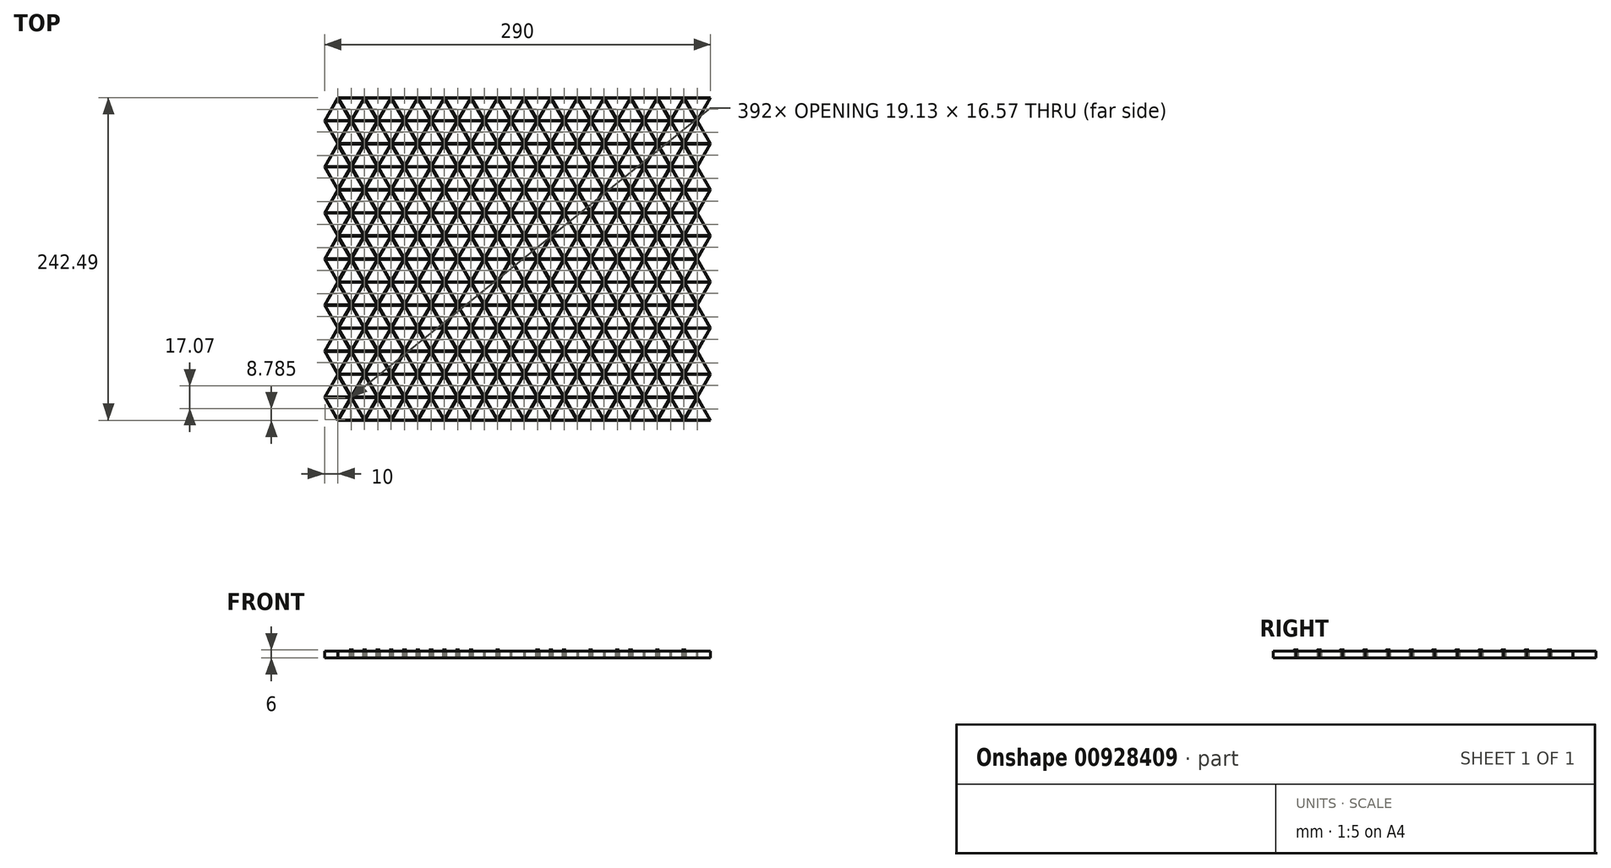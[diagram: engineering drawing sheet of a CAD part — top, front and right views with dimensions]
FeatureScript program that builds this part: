
annotation { "Feature Type Name" : "Feature", "Feature Type Description" : "" }
export const myFeature = defineFeature(function(context is Context, id is Id, definition is map)
    precondition{}
    {
        {
            var Q0;
            Q0=qCreatedBy(makeId("Top.planeOp"),FACE);
            var sketch = newSketch(context, id + "F0", { "sketchPlane" : qUnion([Q0])});
            skLineSegment(sketch, "E0", {"start": v(0, 0) * mm, "end": v(20, 0) * mm, "construction": true});
            skLineSegment(sketch, "E1", {"start": v(20, 0) * mm, "end": v(10, 17.32) * mm, "construction": true});
            skLineSegment(sketch, "E2", {"start": v(10, 17.32) * mm, "end": v(0, 0) * mm});
            skLineSegment(sketch, "E3.MirrorCS", {"start": v(10, -17.32) * mm, "end": v(0, 0) * mm});
            skLineSegment(sketch, "E4.MirrorCS", {"start": v(20, 0) * mm, "end": v(10, -17.32) * mm, "construction": true});
            skLineSegment(sketch, "E5.MirrorCS", {"start": v(30, -17.32) * mm, "end": v(20, 0) * mm, "construction": true});
            skLineSegment(sketch, "E6.MirrorCS", {"start": v(10, -17.32) * mm, "end": v(30, -17.32) * mm});
            skLineSegment(sketch, "E7.MirrorCS", {"start": v(30, 17.32) * mm, "end": v(20, 0) * mm, "construction": true});
            skLineSegment(sketch, "E8.MirrorCS", {"start": v(10, 17.32) * mm, "end": v(30, 17.32) * mm, "construction": true});
            skLineSegment(sketch, "E9.0.1.1", {"start": v(20, 34.64) * mm, "end": v(10, 17.32) * mm, "construction": true});
            skLineSegment(sketch, "E9.0.1.2", {"start": v(30, 17.32) * mm, "end": v(20, 34.64) * mm, "construction": true});
            skLineSegment(sketch, "E9.0.1.3", {"start": v(0, 34.64) * mm, "end": v(20, 34.64) * mm, "construction": true});
            skLineSegment(sketch, "E9.0.1.4", {"start": v(10, 17.32) * mm, "end": v(0, 34.64) * mm});
            skLineSegment(sketch, "E9.0.1.5", {"start": v(10, 51.96) * mm, "end": v(0, 34.64) * mm});
            skLineSegment(sketch, "E9.0.1.6", {"start": v(20, 34.64) * mm, "end": v(10, 51.96) * mm, "construction": true});
            skLineSegment(sketch, "E9.0.1.7", {"start": v(10, 51.96) * mm, "end": v(30, 51.96) * mm, "construction": true});
            skLineSegment(sketch, "E9.0.1.8", {"start": v(30, 51.96) * mm, "end": v(20, 34.64) * mm, "construction": true});
            skLineSegment(sketch, "E9.0.2.0", {"start": v(10, 51.96) * mm, "end": v(30, 51.96) * mm, "construction": true});
            skLineSegment(sketch, "E9.0.2.1", {"start": v(20, 69.28) * mm, "end": v(10, 51.96) * mm, "construction": true});
            skLineSegment(sketch, "E9.0.2.2", {"start": v(30, 51.96) * mm, "end": v(20, 69.28) * mm, "construction": true});
            skLineSegment(sketch, "E9.0.2.3", {"start": v(0, 69.28) * mm, "end": v(20, 69.28) * mm, "construction": true});
            skLineSegment(sketch, "E9.0.2.4", {"start": v(10, 51.96) * mm, "end": v(0, 69.28) * mm});
            skLineSegment(sketch, "E9.0.2.5", {"start": v(10, 86.6) * mm, "end": v(0, 69.28) * mm});
            skLineSegment(sketch, "E9.0.2.6", {"start": v(20, 69.28) * mm, "end": v(10, 86.6) * mm, "construction": true});
            skLineSegment(sketch, "E9.0.2.7", {"start": v(10, 86.6) * mm, "end": v(30, 86.6) * mm, "construction": true});
            skLineSegment(sketch, "E9.0.2.8", {"start": v(30, 86.6) * mm, "end": v(20, 69.28) * mm, "construction": true});
            skLineSegment(sketch, "E9.0.3.0", {"start": v(10, 86.6) * mm, "end": v(30, 86.6) * mm, "construction": true});
            skLineSegment(sketch, "E9.0.3.1", {"start": v(20, 103.92) * mm, "end": v(10, 86.6) * mm, "construction": true});
            skLineSegment(sketch, "E9.0.3.2", {"start": v(30, 86.6) * mm, "end": v(20, 103.92) * mm, "construction": true});
            skLineSegment(sketch, "E9.0.3.3", {"start": v(0, 103.92) * mm, "end": v(20, 103.92) * mm, "construction": true});
            skLineSegment(sketch, "E9.0.3.4", {"start": v(10, 86.6) * mm, "end": v(0, 103.92) * mm});
            skLineSegment(sketch, "E9.0.3.5", {"start": v(10, 121.24) * mm, "end": v(0, 103.92) * mm});
            skLineSegment(sketch, "E9.0.3.6", {"start": v(20, 103.92) * mm, "end": v(10, 121.24) * mm, "construction": true});
            skLineSegment(sketch, "E9.0.3.7", {"start": v(10, 121.24) * mm, "end": v(30, 121.24) * mm, "construction": true});
            skLineSegment(sketch, "E9.0.3.8", {"start": v(30, 121.24) * mm, "end": v(20, 103.92) * mm, "construction": true});
            skLineSegment(sketch, "E9.0.4.0", {"start": v(10, 121.24) * mm, "end": v(30, 121.24) * mm, "construction": true});
            skLineSegment(sketch, "E9.0.4.1", {"start": v(20, 138.56) * mm, "end": v(10, 121.24) * mm, "construction": true});
            skLineSegment(sketch, "E9.0.4.2", {"start": v(30, 121.24) * mm, "end": v(20, 138.56) * mm, "construction": true});
            skLineSegment(sketch, "E9.0.4.3", {"start": v(0, 138.56) * mm, "end": v(20, 138.56) * mm, "construction": true});
            skLineSegment(sketch, "E9.0.4.4", {"start": v(10, 121.24) * mm, "end": v(0, 138.56) * mm});
            skLineSegment(sketch, "E9.0.4.5", {"start": v(10, 155.88) * mm, "end": v(0, 138.56) * mm});
            skLineSegment(sketch, "E9.0.4.6", {"start": v(20, 138.56) * mm, "end": v(10, 155.88) * mm, "construction": true});
            skLineSegment(sketch, "E9.0.4.7", {"start": v(10, 155.88) * mm, "end": v(30, 155.88) * mm, "construction": true});
            skLineSegment(sketch, "E9.0.4.8", {"start": v(30, 155.88) * mm, "end": v(20, 138.56) * mm, "construction": true});
            skLineSegment(sketch, "E9.0.5.0", {"start": v(10, 155.88) * mm, "end": v(30, 155.88) * mm, "construction": true});
            skLineSegment(sketch, "E9.0.5.1", {"start": v(20, 173.2) * mm, "end": v(10, 155.88) * mm, "construction": true});
            skLineSegment(sketch, "E9.0.5.2", {"start": v(30, 155.88) * mm, "end": v(20, 173.2) * mm, "construction": true});
            skLineSegment(sketch, "E9.0.5.3", {"start": v(0, 173.2) * mm, "end": v(20, 173.2) * mm, "construction": true});
            skLineSegment(sketch, "E9.0.5.4", {"start": v(10, 155.88) * mm, "end": v(0, 173.2) * mm});
            skLineSegment(sketch, "E9.0.5.5", {"start": v(10, 190.53) * mm, "end": v(0, 173.2) * mm});
            skLineSegment(sketch, "E9.0.5.6", {"start": v(20, 173.2) * mm, "end": v(10, 190.53) * mm, "construction": true});
            skLineSegment(sketch, "E9.0.5.7", {"start": v(10, 190.53) * mm, "end": v(30, 190.53) * mm, "construction": true});
            skLineSegment(sketch, "E9.0.5.8", {"start": v(30, 190.53) * mm, "end": v(20, 173.2) * mm, "construction": true});
            skLineSegment(sketch, "E9.0.6.0", {"start": v(10, 190.53) * mm, "end": v(30, 190.53) * mm, "construction": true});
            skLineSegment(sketch, "E9.0.6.1", {"start": v(20, 207.85) * mm, "end": v(10, 190.53) * mm, "construction": true});
            skLineSegment(sketch, "E9.0.6.2", {"start": v(30, 190.53) * mm, "end": v(20, 207.85) * mm, "construction": true});
            skLineSegment(sketch, "E9.0.6.3", {"start": v(0, 207.85) * mm, "end": v(20, 207.85) * mm, "construction": true});
            skLineSegment(sketch, "E9.0.6.4", {"start": v(10, 190.53) * mm, "end": v(0, 207.85) * mm});
            skLineSegment(sketch, "E9.0.6.5", {"start": v(10, 225.17) * mm, "end": v(0, 207.85) * mm});
            skLineSegment(sketch, "E9.0.6.6", {"start": v(20, 207.85) * mm, "end": v(10, 225.17) * mm, "construction": true});
            skLineSegment(sketch, "E9.0.6.7", {"start": v(10, 225.17) * mm, "end": v(30, 225.17) * mm});
            skLineSegment(sketch, "E9.0.6.8", {"start": v(30, 225.17) * mm, "end": v(20, 207.85) * mm, "construction": true});
            skLineSegment(sketch, "E9.1.0.0", {"start": v(30, -17.32) * mm, "end": v(50, -17.32) * mm});
            skLineSegment(sketch, "E9.1.0.1", {"start": v(40, 0) * mm, "end": v(30, -17.32) * mm, "construction": true});
            skLineSegment(sketch, "E9.1.0.2", {"start": v(50, -17.32) * mm, "end": v(40, 0) * mm, "construction": true});
            skLineSegment(sketch, "E9.1.0.3", {"start": v(20, 0) * mm, "end": v(40, 0) * mm, "construction": true});
            skLineSegment(sketch, "E9.1.0.6", {"start": v(40, 0) * mm, "end": v(30, 17.32) * mm, "construction": true});
            skLineSegment(sketch, "E9.1.0.7", {"start": v(30, 17.32) * mm, "end": v(50, 17.32) * mm, "construction": true});
            skLineSegment(sketch, "E9.1.0.8", {"start": v(50, 17.32) * mm, "end": v(40, 0) * mm, "construction": true});
            skLineSegment(sketch, "E9.1.1.0", {"start": v(30, 17.32) * mm, "end": v(50, 17.32) * mm, "construction": true});
            skLineSegment(sketch, "E9.1.1.1", {"start": v(40, 34.64) * mm, "end": v(30, 17.32) * mm, "construction": true});
            skLineSegment(sketch, "E9.1.1.2", {"start": v(50, 17.32) * mm, "end": v(40, 34.64) * mm, "construction": true});
            skLineSegment(sketch, "E9.1.1.3", {"start": v(20, 34.64) * mm, "end": v(40, 34.64) * mm, "construction": true});
            skLineSegment(sketch, "E9.1.1.4", {"start": v(30, 17.32) * mm, "end": v(20, 34.64) * mm, "construction": true});
            skLineSegment(sketch, "E9.1.1.5", {"start": v(30, 51.96) * mm, "end": v(20, 34.64) * mm, "construction": true});
            skLineSegment(sketch, "E9.1.1.6", {"start": v(40, 34.64) * mm, "end": v(30, 51.96) * mm, "construction": true});
            skLineSegment(sketch, "E9.1.1.7", {"start": v(30, 51.96) * mm, "end": v(50, 51.96) * mm, "construction": true});
            skLineSegment(sketch, "E9.1.1.8", {"start": v(50, 51.96) * mm, "end": v(40, 34.64) * mm, "construction": true});
            skLineSegment(sketch, "E9.1.2.0", {"start": v(30, 51.96) * mm, "end": v(50, 51.96) * mm, "construction": true});
            skLineSegment(sketch, "E9.1.2.1", {"start": v(40, 69.28) * mm, "end": v(30, 51.96) * mm, "construction": true});
            skLineSegment(sketch, "E9.1.2.2", {"start": v(50, 51.96) * mm, "end": v(40, 69.28) * mm, "construction": true});
            skLineSegment(sketch, "E9.1.2.3", {"start": v(20, 69.28) * mm, "end": v(40, 69.28) * mm, "construction": true});
            skLineSegment(sketch, "E9.1.2.4", {"start": v(30, 51.96) * mm, "end": v(20, 69.28) * mm, "construction": true});
            skLineSegment(sketch, "E9.1.2.5", {"start": v(30, 86.6) * mm, "end": v(20, 69.28) * mm, "construction": true});
            skLineSegment(sketch, "E9.1.2.6", {"start": v(40, 69.28) * mm, "end": v(30, 86.6) * mm, "construction": true});
            skLineSegment(sketch, "E9.1.2.7", {"start": v(30, 86.6) * mm, "end": v(50, 86.6) * mm, "construction": true});
            skLineSegment(sketch, "E9.1.2.8", {"start": v(50, 86.6) * mm, "end": v(40, 69.28) * mm, "construction": true});
            skLineSegment(sketch, "E9.1.3.0", {"start": v(30, 86.6) * mm, "end": v(50, 86.6) * mm, "construction": true});
            skLineSegment(sketch, "E9.1.3.1", {"start": v(40, 103.92) * mm, "end": v(30, 86.6) * mm, "construction": true});
            skLineSegment(sketch, "E9.1.3.2", {"start": v(50, 86.6) * mm, "end": v(40, 103.92) * mm, "construction": true});
            skLineSegment(sketch, "E9.1.3.3", {"start": v(20, 103.92) * mm, "end": v(40, 103.92) * mm, "construction": true});
            skLineSegment(sketch, "E9.1.3.4", {"start": v(30, 86.6) * mm, "end": v(20, 103.92) * mm, "construction": true});
            skLineSegment(sketch, "E9.1.3.5", {"start": v(30, 121.24) * mm, "end": v(20, 103.92) * mm, "construction": true});
            skLineSegment(sketch, "E9.1.3.6", {"start": v(40, 103.92) * mm, "end": v(30, 121.24) * mm, "construction": true});
            skLineSegment(sketch, "E9.1.3.7", {"start": v(30, 121.24) * mm, "end": v(50, 121.24) * mm, "construction": true});
            skLineSegment(sketch, "E9.1.3.8", {"start": v(50, 121.24) * mm, "end": v(40, 103.92) * mm, "construction": true});
            skLineSegment(sketch, "E9.1.4.0", {"start": v(30, 121.24) * mm, "end": v(50, 121.24) * mm, "construction": true});
            skLineSegment(sketch, "E9.1.4.1", {"start": v(40, 138.56) * mm, "end": v(30, 121.24) * mm, "construction": true});
            skLineSegment(sketch, "E9.1.4.2", {"start": v(50, 121.24) * mm, "end": v(40, 138.56) * mm, "construction": true});
            skLineSegment(sketch, "E9.1.4.3", {"start": v(20, 138.56) * mm, "end": v(40, 138.56) * mm, "construction": true});
            skLineSegment(sketch, "E9.1.4.4", {"start": v(30, 121.24) * mm, "end": v(20, 138.56) * mm, "construction": true});
            skLineSegment(sketch, "E9.1.4.5", {"start": v(30, 155.88) * mm, "end": v(20, 138.56) * mm, "construction": true});
            skLineSegment(sketch, "E9.1.4.6", {"start": v(40, 138.56) * mm, "end": v(30, 155.88) * mm, "construction": true});
            skLineSegment(sketch, "E9.1.4.7", {"start": v(30, 155.88) * mm, "end": v(50, 155.88) * mm, "construction": true});
            skLineSegment(sketch, "E9.1.4.8", {"start": v(50, 155.88) * mm, "end": v(40, 138.56) * mm, "construction": true});
            skLineSegment(sketch, "E9.1.5.0", {"start": v(30, 155.88) * mm, "end": v(50, 155.88) * mm, "construction": true});
            skLineSegment(sketch, "E9.1.5.1", {"start": v(40, 173.2) * mm, "end": v(30, 155.88) * mm, "construction": true});
            skLineSegment(sketch, "E9.1.5.2", {"start": v(50, 155.88) * mm, "end": v(40, 173.2) * mm, "construction": true});
            skLineSegment(sketch, "E9.1.5.3", {"start": v(20, 173.2) * mm, "end": v(40, 173.2) * mm, "construction": true});
            skLineSegment(sketch, "E9.1.5.4", {"start": v(30, 155.88) * mm, "end": v(20, 173.2) * mm, "construction": true});
            skLineSegment(sketch, "E9.1.5.5", {"start": v(30, 190.53) * mm, "end": v(20, 173.2) * mm, "construction": true});
            skLineSegment(sketch, "E9.1.5.6", {"start": v(40, 173.2) * mm, "end": v(30, 190.53) * mm, "construction": true});
            skLineSegment(sketch, "E9.1.5.7", {"start": v(30, 190.53) * mm, "end": v(50, 190.53) * mm, "construction": true});
            skLineSegment(sketch, "E9.1.5.8", {"start": v(50, 190.53) * mm, "end": v(40, 173.2) * mm, "construction": true});
            skLineSegment(sketch, "E9.1.6.0", {"start": v(30, 190.53) * mm, "end": v(50, 190.53) * mm, "construction": true});
            skLineSegment(sketch, "E9.1.6.1", {"start": v(40, 207.85) * mm, "end": v(30, 190.53) * mm, "construction": true});
            skLineSegment(sketch, "E9.1.6.2", {"start": v(50, 190.53) * mm, "end": v(40, 207.85) * mm, "construction": true});
            skLineSegment(sketch, "E9.1.6.3", {"start": v(20, 207.85) * mm, "end": v(40, 207.85) * mm, "construction": true});
            skLineSegment(sketch, "E9.1.6.4", {"start": v(30, 190.53) * mm, "end": v(20, 207.85) * mm, "construction": true});
            skLineSegment(sketch, "E9.1.6.5", {"start": v(30, 225.17) * mm, "end": v(20, 207.85) * mm, "construction": true});
            skLineSegment(sketch, "E9.1.6.6", {"start": v(40, 207.85) * mm, "end": v(30, 225.17) * mm, "construction": true});
            skLineSegment(sketch, "E9.1.6.7", {"start": v(30, 225.17) * mm, "end": v(50, 225.17) * mm});
            skLineSegment(sketch, "E9.1.6.8", {"start": v(50, 225.17) * mm, "end": v(40, 207.85) * mm, "construction": true});
            skLineSegment(sketch, "E9.2.0.0", {"start": v(50, -17.32) * mm, "end": v(70, -17.32) * mm});
            skLineSegment(sketch, "E9.2.0.1", {"start": v(60, 0) * mm, "end": v(50, -17.32) * mm, "construction": true});
            skLineSegment(sketch, "E9.2.0.2", {"start": v(70, -17.32) * mm, "end": v(60, 0) * mm, "construction": true});
            skLineSegment(sketch, "E9.2.0.3", {"start": v(40, 0) * mm, "end": v(60, 0) * mm, "construction": true});
            skLineSegment(sketch, "E9.2.0.4", {"start": v(50, -17.32) * mm, "end": v(40, 0) * mm, "construction": true});
            skLineSegment(sketch, "E9.2.0.5", {"start": v(50, 17.32) * mm, "end": v(40, 0) * mm, "construction": true});
            skLineSegment(sketch, "E9.2.0.6", {"start": v(60, 0) * mm, "end": v(50, 17.32) * mm, "construction": true});
            skLineSegment(sketch, "E9.2.0.7", {"start": v(50, 17.32) * mm, "end": v(70, 17.32) * mm, "construction": true});
            skLineSegment(sketch, "E9.2.0.8", {"start": v(70, 17.32) * mm, "end": v(60, 0) * mm, "construction": true});
            skLineSegment(sketch, "E9.2.1.0", {"start": v(50, 17.32) * mm, "end": v(70, 17.32) * mm, "construction": true});
            skLineSegment(sketch, "E9.2.1.1", {"start": v(60, 34.64) * mm, "end": v(50, 17.32) * mm, "construction": true});
            skLineSegment(sketch, "E9.2.1.2", {"start": v(70, 17.32) * mm, "end": v(60, 34.64) * mm, "construction": true});
            skLineSegment(sketch, "E9.2.1.3", {"start": v(40, 34.64) * mm, "end": v(60, 34.64) * mm, "construction": true});
            skLineSegment(sketch, "E9.2.1.4", {"start": v(50, 17.32) * mm, "end": v(40, 34.64) * mm, "construction": true});
            skLineSegment(sketch, "E9.2.1.5", {"start": v(50, 51.96) * mm, "end": v(40, 34.64) * mm, "construction": true});
            skLineSegment(sketch, "E9.2.1.6", {"start": v(60, 34.64) * mm, "end": v(50, 51.96) * mm, "construction": true});
            skLineSegment(sketch, "E9.2.1.7", {"start": v(50, 51.96) * mm, "end": v(70, 51.96) * mm, "construction": true});
            skLineSegment(sketch, "E9.2.1.8", {"start": v(70, 51.96) * mm, "end": v(60, 34.64) * mm, "construction": true});
            skLineSegment(sketch, "E9.2.2.0", {"start": v(50, 51.96) * mm, "end": v(70, 51.96) * mm, "construction": true});
            skLineSegment(sketch, "E9.2.2.1", {"start": v(60, 69.28) * mm, "end": v(50, 51.96) * mm, "construction": true});
            skLineSegment(sketch, "E9.2.2.2", {"start": v(70, 51.96) * mm, "end": v(60, 69.28) * mm, "construction": true});
            skLineSegment(sketch, "E9.2.2.3", {"start": v(40, 69.28) * mm, "end": v(60, 69.28) * mm, "construction": true});
            skLineSegment(sketch, "E9.2.2.4", {"start": v(50, 51.96) * mm, "end": v(40, 69.28) * mm, "construction": true});
            skLineSegment(sketch, "E9.2.2.5", {"start": v(50, 86.6) * mm, "end": v(40, 69.28) * mm, "construction": true});
            skLineSegment(sketch, "E9.2.2.6", {"start": v(60, 69.28) * mm, "end": v(50, 86.6) * mm, "construction": true});
            skLineSegment(sketch, "E9.2.2.7", {"start": v(50, 86.6) * mm, "end": v(70, 86.6) * mm, "construction": true});
            skLineSegment(sketch, "E9.2.2.8", {"start": v(70, 86.6) * mm, "end": v(60, 69.28) * mm, "construction": true});
            skLineSegment(sketch, "E9.2.3.0", {"start": v(50, 86.6) * mm, "end": v(70, 86.6) * mm, "construction": true});
            skLineSegment(sketch, "E9.2.3.1", {"start": v(60, 103.92) * mm, "end": v(50, 86.6) * mm, "construction": true});
            skLineSegment(sketch, "E9.2.3.2", {"start": v(70, 86.6) * mm, "end": v(60, 103.92) * mm, "construction": true});
            skLineSegment(sketch, "E9.2.3.3", {"start": v(40, 103.92) * mm, "end": v(60, 103.92) * mm, "construction": true});
            skLineSegment(sketch, "E9.2.3.4", {"start": v(50, 86.6) * mm, "end": v(40, 103.92) * mm, "construction": true});
            skLineSegment(sketch, "E9.2.3.5", {"start": v(50, 121.24) * mm, "end": v(40, 103.92) * mm, "construction": true});
            skLineSegment(sketch, "E9.2.3.6", {"start": v(60, 103.92) * mm, "end": v(50, 121.24) * mm, "construction": true});
            skLineSegment(sketch, "E9.2.3.7", {"start": v(50, 121.24) * mm, "end": v(70, 121.24) * mm, "construction": true});
            skLineSegment(sketch, "E9.2.3.8", {"start": v(70, 121.24) * mm, "end": v(60, 103.92) * mm, "construction": true});
            skLineSegment(sketch, "E9.2.4.0", {"start": v(50, 121.24) * mm, "end": v(70, 121.24) * mm, "construction": true});
            skLineSegment(sketch, "E9.2.4.1", {"start": v(60, 138.56) * mm, "end": v(50, 121.24) * mm, "construction": true});
            skLineSegment(sketch, "E9.2.4.2", {"start": v(70, 121.24) * mm, "end": v(60, 138.56) * mm, "construction": true});
            skLineSegment(sketch, "E9.2.4.3", {"start": v(40, 138.56) * mm, "end": v(60, 138.56) * mm, "construction": true});
            skLineSegment(sketch, "E9.2.4.4", {"start": v(50, 121.24) * mm, "end": v(40, 138.56) * mm, "construction": true});
            skLineSegment(sketch, "E9.2.4.5", {"start": v(50, 155.88) * mm, "end": v(40, 138.56) * mm, "construction": true});
            skLineSegment(sketch, "E9.2.4.6", {"start": v(60, 138.56) * mm, "end": v(50, 155.88) * mm, "construction": true});
            skLineSegment(sketch, "E9.2.4.7", {"start": v(50, 155.88) * mm, "end": v(70, 155.88) * mm, "construction": true});
            skLineSegment(sketch, "E9.2.4.8", {"start": v(70, 155.88) * mm, "end": v(60, 138.56) * mm, "construction": true});
            skLineSegment(sketch, "E9.2.5.0", {"start": v(50, 155.88) * mm, "end": v(70, 155.88) * mm, "construction": true});
            skLineSegment(sketch, "E9.2.5.1", {"start": v(60, 173.2) * mm, "end": v(50, 155.88) * mm, "construction": true});
            skLineSegment(sketch, "E9.2.5.2", {"start": v(70, 155.88) * mm, "end": v(60, 173.2) * mm, "construction": true});
            skLineSegment(sketch, "E9.2.5.3", {"start": v(40, 173.2) * mm, "end": v(60, 173.2) * mm, "construction": true});
            skLineSegment(sketch, "E9.2.5.4", {"start": v(50, 155.88) * mm, "end": v(40, 173.2) * mm, "construction": true});
            skLineSegment(sketch, "E9.2.5.5", {"start": v(50, 190.53) * mm, "end": v(40, 173.2) * mm, "construction": true});
            skLineSegment(sketch, "E9.2.5.6", {"start": v(60, 173.2) * mm, "end": v(50, 190.53) * mm, "construction": true});
            skLineSegment(sketch, "E9.2.5.7", {"start": v(50, 190.53) * mm, "end": v(70, 190.53) * mm, "construction": true});
            skLineSegment(sketch, "E9.2.5.8", {"start": v(70, 190.53) * mm, "end": v(60, 173.2) * mm, "construction": true});
            skLineSegment(sketch, "E9.2.6.0", {"start": v(50, 190.53) * mm, "end": v(70, 190.53) * mm, "construction": true});
            skLineSegment(sketch, "E9.2.6.1", {"start": v(60, 207.85) * mm, "end": v(50, 190.53) * mm, "construction": true});
            skLineSegment(sketch, "E9.2.6.2", {"start": v(70, 190.53) * mm, "end": v(60, 207.85) * mm, "construction": true});
            skLineSegment(sketch, "E9.2.6.3", {"start": v(40, 207.85) * mm, "end": v(60, 207.85) * mm, "construction": true});
            skLineSegment(sketch, "E9.2.6.4", {"start": v(50, 190.53) * mm, "end": v(40, 207.85) * mm, "construction": true});
            skLineSegment(sketch, "E9.2.6.5", {"start": v(50, 225.17) * mm, "end": v(40, 207.85) * mm, "construction": true});
            skLineSegment(sketch, "E9.2.6.6", {"start": v(60, 207.85) * mm, "end": v(50, 225.17) * mm, "construction": true});
            skLineSegment(sketch, "E9.2.6.7", {"start": v(50, 225.17) * mm, "end": v(70, 225.17) * mm});
            skLineSegment(sketch, "E9.2.6.8", {"start": v(70, 225.17) * mm, "end": v(60, 207.85) * mm, "construction": true});
            skLineSegment(sketch, "E9.3.0.0", {"start": v(70, -17.32) * mm, "end": v(90, -17.32) * mm});
            skLineSegment(sketch, "E9.3.0.1", {"start": v(80, 0) * mm, "end": v(70, -17.32) * mm, "construction": true});
            skLineSegment(sketch, "E9.3.0.2", {"start": v(90, -17.32) * mm, "end": v(80, 0) * mm, "construction": true});
            skLineSegment(sketch, "E9.3.0.3", {"start": v(60, 0) * mm, "end": v(80, 0) * mm, "construction": true});
            skLineSegment(sketch, "E9.3.0.4", {"start": v(70, -17.32) * mm, "end": v(60, 0) * mm, "construction": true});
            skLineSegment(sketch, "E9.3.0.5", {"start": v(70, 17.32) * mm, "end": v(60, 0) * mm, "construction": true});
            skLineSegment(sketch, "E9.3.0.6", {"start": v(80, 0) * mm, "end": v(70, 17.32) * mm, "construction": true});
            skLineSegment(sketch, "E9.3.0.7", {"start": v(70, 17.32) * mm, "end": v(90, 17.32) * mm, "construction": true});
            skLineSegment(sketch, "E9.3.0.8", {"start": v(90, 17.32) * mm, "end": v(80, 0) * mm, "construction": true});
            skLineSegment(sketch, "E9.3.1.0", {"start": v(70, 17.32) * mm, "end": v(90, 17.32) * mm, "construction": true});
            skLineSegment(sketch, "E9.3.1.1", {"start": v(80, 34.64) * mm, "end": v(70, 17.32) * mm, "construction": true});
            skLineSegment(sketch, "E9.3.1.2", {"start": v(90, 17.32) * mm, "end": v(80, 34.64) * mm, "construction": true});
            skLineSegment(sketch, "E9.3.1.3", {"start": v(60, 34.64) * mm, "end": v(80, 34.64) * mm, "construction": true});
            skLineSegment(sketch, "E9.3.1.4", {"start": v(70, 17.32) * mm, "end": v(60, 34.64) * mm, "construction": true});
            skLineSegment(sketch, "E9.3.1.5", {"start": v(70, 51.96) * mm, "end": v(60, 34.64) * mm, "construction": true});
            skLineSegment(sketch, "E9.3.1.6", {"start": v(80, 34.64) * mm, "end": v(70, 51.96) * mm, "construction": true});
            skLineSegment(sketch, "E9.3.1.7", {"start": v(70, 51.96) * mm, "end": v(90, 51.96) * mm, "construction": true});
            skLineSegment(sketch, "E9.3.1.8", {"start": v(90, 51.96) * mm, "end": v(80, 34.64) * mm, "construction": true});
            skLineSegment(sketch, "E9.3.2.0", {"start": v(70, 51.96) * mm, "end": v(90, 51.96) * mm, "construction": true});
            skLineSegment(sketch, "E9.3.2.1", {"start": v(80, 69.28) * mm, "end": v(70, 51.96) * mm, "construction": true});
            skLineSegment(sketch, "E9.3.2.2", {"start": v(90, 51.96) * mm, "end": v(80, 69.28) * mm, "construction": true});
            skLineSegment(sketch, "E9.3.2.3", {"start": v(60, 69.28) * mm, "end": v(80, 69.28) * mm, "construction": true});
            skLineSegment(sketch, "E9.3.2.4", {"start": v(70, 51.96) * mm, "end": v(60, 69.28) * mm, "construction": true});
            skLineSegment(sketch, "E9.3.2.5", {"start": v(70, 86.6) * mm, "end": v(60, 69.28) * mm, "construction": true});
            skLineSegment(sketch, "E9.3.2.6", {"start": v(80, 69.28) * mm, "end": v(70, 86.6) * mm, "construction": true});
            skLineSegment(sketch, "E9.3.2.7", {"start": v(70, 86.6) * mm, "end": v(90, 86.6) * mm, "construction": true});
            skLineSegment(sketch, "E9.3.2.8", {"start": v(90, 86.6) * mm, "end": v(80, 69.28) * mm, "construction": true});
            skLineSegment(sketch, "E9.3.3.0", {"start": v(70, 86.6) * mm, "end": v(90, 86.6) * mm, "construction": true});
            skLineSegment(sketch, "E9.3.3.1", {"start": v(80, 103.92) * mm, "end": v(70, 86.6) * mm, "construction": true});
            skLineSegment(sketch, "E9.3.3.2", {"start": v(90, 86.6) * mm, "end": v(80, 103.92) * mm, "construction": true});
            skLineSegment(sketch, "E9.3.3.3", {"start": v(60, 103.92) * mm, "end": v(80, 103.92) * mm, "construction": true});
            skLineSegment(sketch, "E9.3.3.4", {"start": v(70, 86.6) * mm, "end": v(60, 103.92) * mm, "construction": true});
            skLineSegment(sketch, "E9.3.3.5", {"start": v(70, 121.24) * mm, "end": v(60, 103.92) * mm, "construction": true});
            skLineSegment(sketch, "E9.3.3.6", {"start": v(80, 103.92) * mm, "end": v(70, 121.24) * mm, "construction": true});
            skLineSegment(sketch, "E9.3.3.7", {"start": v(70, 121.24) * mm, "end": v(90, 121.24) * mm, "construction": true});
            skLineSegment(sketch, "E9.3.3.8", {"start": v(90, 121.24) * mm, "end": v(80, 103.92) * mm, "construction": true});
            skLineSegment(sketch, "E9.3.4.0", {"start": v(70, 121.24) * mm, "end": v(90, 121.24) * mm, "construction": true});
            skLineSegment(sketch, "E9.3.4.1", {"start": v(80, 138.56) * mm, "end": v(70, 121.24) * mm, "construction": true});
            skLineSegment(sketch, "E9.3.4.2", {"start": v(90, 121.24) * mm, "end": v(80, 138.56) * mm, "construction": true});
            skLineSegment(sketch, "E9.3.4.3", {"start": v(60, 138.56) * mm, "end": v(80, 138.56) * mm, "construction": true});
            skLineSegment(sketch, "E9.3.4.4", {"start": v(70, 121.24) * mm, "end": v(60, 138.56) * mm, "construction": true});
            skLineSegment(sketch, "E9.3.4.5", {"start": v(70, 155.88) * mm, "end": v(60, 138.56) * mm, "construction": true});
            skLineSegment(sketch, "E9.3.4.6", {"start": v(80, 138.56) * mm, "end": v(70, 155.88) * mm, "construction": true});
            skLineSegment(sketch, "E9.3.4.7", {"start": v(70, 155.88) * mm, "end": v(90, 155.88) * mm, "construction": true});
            skLineSegment(sketch, "E9.3.4.8", {"start": v(90, 155.88) * mm, "end": v(80, 138.56) * mm, "construction": true});
            skLineSegment(sketch, "E9.3.5.0", {"start": v(70, 155.88) * mm, "end": v(90, 155.88) * mm, "construction": true});
            skLineSegment(sketch, "E9.3.5.1", {"start": v(80, 173.2) * mm, "end": v(70, 155.88) * mm, "construction": true});
            skLineSegment(sketch, "E9.3.5.2", {"start": v(90, 155.88) * mm, "end": v(80, 173.2) * mm, "construction": true});
            skLineSegment(sketch, "E9.3.5.3", {"start": v(60, 173.2) * mm, "end": v(80, 173.2) * mm, "construction": true});
            skLineSegment(sketch, "E9.3.5.4", {"start": v(70, 155.88) * mm, "end": v(60, 173.2) * mm, "construction": true});
            skLineSegment(sketch, "E9.3.5.5", {"start": v(70, 190.53) * mm, "end": v(60, 173.2) * mm, "construction": true});
            skLineSegment(sketch, "E9.3.5.6", {"start": v(80, 173.2) * mm, "end": v(70, 190.53) * mm, "construction": true});
            skLineSegment(sketch, "E9.3.5.7", {"start": v(70, 190.53) * mm, "end": v(90, 190.53) * mm, "construction": true});
            skLineSegment(sketch, "E9.3.5.8", {"start": v(90, 190.53) * mm, "end": v(80, 173.2) * mm, "construction": true});
            skLineSegment(sketch, "E9.3.6.0", {"start": v(70, 190.53) * mm, "end": v(90, 190.53) * mm, "construction": true});
            skLineSegment(sketch, "E9.3.6.1", {"start": v(80, 207.85) * mm, "end": v(70, 190.53) * mm, "construction": true});
            skLineSegment(sketch, "E9.3.6.2", {"start": v(90, 190.53) * mm, "end": v(80, 207.85) * mm, "construction": true});
            skLineSegment(sketch, "E9.3.6.3", {"start": v(60, 207.85) * mm, "end": v(80, 207.85) * mm, "construction": true});
            skLineSegment(sketch, "E9.3.6.4", {"start": v(70, 190.53) * mm, "end": v(60, 207.85) * mm, "construction": true});
            skLineSegment(sketch, "E9.3.6.5", {"start": v(70, 225.17) * mm, "end": v(60, 207.85) * mm, "construction": true});
            skLineSegment(sketch, "E9.3.6.6", {"start": v(80, 207.85) * mm, "end": v(70, 225.17) * mm, "construction": true});
            skLineSegment(sketch, "E9.3.6.7", {"start": v(70, 225.17) * mm, "end": v(90, 225.17) * mm});
            skLineSegment(sketch, "E9.3.6.8", {"start": v(90, 225.17) * mm, "end": v(80, 207.85) * mm, "construction": true});
            skLineSegment(sketch, "E9.4.0.0", {"start": v(90, -17.32) * mm, "end": v(110, -17.32) * mm});
            skLineSegment(sketch, "E9.4.0.1", {"start": v(100, 0) * mm, "end": v(90, -17.32) * mm, "construction": true});
            skLineSegment(sketch, "E9.4.0.2", {"start": v(110, -17.32) * mm, "end": v(100, 0) * mm, "construction": true});
            skLineSegment(sketch, "E9.4.0.3", {"start": v(80, 0) * mm, "end": v(100, 0) * mm, "construction": true});
            skLineSegment(sketch, "E9.4.0.4", {"start": v(90, -17.32) * mm, "end": v(80, 0) * mm, "construction": true});
            skLineSegment(sketch, "E9.4.0.5", {"start": v(90, 17.32) * mm, "end": v(80, 0) * mm, "construction": true});
            skLineSegment(sketch, "E9.4.0.6", {"start": v(100, 0) * mm, "end": v(90, 17.32) * mm, "construction": true});
            skLineSegment(sketch, "E9.4.0.7", {"start": v(90, 17.32) * mm, "end": v(110, 17.32) * mm, "construction": true});
            skLineSegment(sketch, "E9.4.0.8", {"start": v(110, 17.32) * mm, "end": v(100, 0) * mm, "construction": true});
            skLineSegment(sketch, "E9.4.1.0", {"start": v(90, 17.32) * mm, "end": v(110, 17.32) * mm, "construction": true});
            skLineSegment(sketch, "E9.4.1.1", {"start": v(100, 34.64) * mm, "end": v(90, 17.32) * mm, "construction": true});
            skLineSegment(sketch, "E9.4.1.2", {"start": v(110, 17.32) * mm, "end": v(100, 34.64) * mm, "construction": true});
            skLineSegment(sketch, "E9.4.1.3", {"start": v(80, 34.64) * mm, "end": v(100, 34.64) * mm, "construction": true});
            skLineSegment(sketch, "E9.4.1.4", {"start": v(90, 17.32) * mm, "end": v(80, 34.64) * mm, "construction": true});
            skLineSegment(sketch, "E9.4.1.5", {"start": v(90, 51.96) * mm, "end": v(80, 34.64) * mm, "construction": true});
            skLineSegment(sketch, "E9.4.1.6", {"start": v(100, 34.64) * mm, "end": v(90, 51.96) * mm, "construction": true});
            skLineSegment(sketch, "E9.4.1.7", {"start": v(90, 51.96) * mm, "end": v(110, 51.96) * mm, "construction": true});
            skLineSegment(sketch, "E9.4.1.8", {"start": v(110, 51.96) * mm, "end": v(100, 34.64) * mm, "construction": true});
            skLineSegment(sketch, "E9.4.2.0", {"start": v(90, 51.96) * mm, "end": v(110, 51.96) * mm, "construction": true});
            skLineSegment(sketch, "E9.4.2.1", {"start": v(100, 69.28) * mm, "end": v(90, 51.96) * mm, "construction": true});
            skLineSegment(sketch, "E9.4.2.2", {"start": v(110, 51.96) * mm, "end": v(100, 69.28) * mm, "construction": true});
            skLineSegment(sketch, "E9.4.2.3", {"start": v(80, 69.28) * mm, "end": v(100, 69.28) * mm, "construction": true});
            skLineSegment(sketch, "E9.4.2.4", {"start": v(90, 51.96) * mm, "end": v(80, 69.28) * mm, "construction": true});
            skLineSegment(sketch, "E9.4.2.5", {"start": v(90, 86.6) * mm, "end": v(80, 69.28) * mm, "construction": true});
            skLineSegment(sketch, "E9.4.2.6", {"start": v(100, 69.28) * mm, "end": v(90, 86.6) * mm, "construction": true});
            skLineSegment(sketch, "E9.4.2.7", {"start": v(90, 86.6) * mm, "end": v(110, 86.6) * mm, "construction": true});
            skLineSegment(sketch, "E9.4.2.8", {"start": v(110, 86.6) * mm, "end": v(100, 69.28) * mm, "construction": true});
            skLineSegment(sketch, "E9.4.3.0", {"start": v(90, 86.6) * mm, "end": v(110, 86.6) * mm, "construction": true});
            skLineSegment(sketch, "E9.4.3.1", {"start": v(100, 103.92) * mm, "end": v(90, 86.6) * mm, "construction": true});
            skLineSegment(sketch, "E9.4.3.2", {"start": v(110, 86.6) * mm, "end": v(100, 103.92) * mm, "construction": true});
            skLineSegment(sketch, "E9.4.3.3", {"start": v(80, 103.92) * mm, "end": v(100, 103.92) * mm, "construction": true});
            skLineSegment(sketch, "E9.4.3.4", {"start": v(90, 86.6) * mm, "end": v(80, 103.92) * mm, "construction": true});
            skLineSegment(sketch, "E9.4.3.5", {"start": v(90, 121.24) * mm, "end": v(80, 103.92) * mm, "construction": true});
            skLineSegment(sketch, "E9.4.3.6", {"start": v(100, 103.92) * mm, "end": v(90, 121.24) * mm, "construction": true});
            skLineSegment(sketch, "E9.4.3.7", {"start": v(90, 121.24) * mm, "end": v(110, 121.24) * mm, "construction": true});
            skLineSegment(sketch, "E9.4.3.8", {"start": v(110, 121.24) * mm, "end": v(100, 103.92) * mm, "construction": true});
            skLineSegment(sketch, "E9.4.4.0", {"start": v(90, 121.24) * mm, "end": v(110, 121.24) * mm, "construction": true});
            skLineSegment(sketch, "E9.4.4.1", {"start": v(100, 138.56) * mm, "end": v(90, 121.24) * mm, "construction": true});
            skLineSegment(sketch, "E9.4.4.2", {"start": v(110, 121.24) * mm, "end": v(100, 138.56) * mm, "construction": true});
            skLineSegment(sketch, "E9.4.4.3", {"start": v(80, 138.56) * mm, "end": v(100, 138.56) * mm, "construction": true});
            skLineSegment(sketch, "E9.4.4.4", {"start": v(90, 121.24) * mm, "end": v(80, 138.56) * mm, "construction": true});
            skLineSegment(sketch, "E9.4.4.5", {"start": v(90, 155.88) * mm, "end": v(80, 138.56) * mm, "construction": true});
            skLineSegment(sketch, "E9.4.4.6", {"start": v(100, 138.56) * mm, "end": v(90, 155.88) * mm, "construction": true});
            skLineSegment(sketch, "E9.4.4.7", {"start": v(90, 155.88) * mm, "end": v(110, 155.88) * mm, "construction": true});
            skLineSegment(sketch, "E9.4.4.8", {"start": v(110, 155.88) * mm, "end": v(100, 138.56) * mm, "construction": true});
            skLineSegment(sketch, "E9.4.5.0", {"start": v(90, 155.88) * mm, "end": v(110, 155.88) * mm, "construction": true});
            skLineSegment(sketch, "E9.4.5.1", {"start": v(100, 173.2) * mm, "end": v(90, 155.88) * mm, "construction": true});
            skLineSegment(sketch, "E9.4.5.2", {"start": v(110, 155.88) * mm, "end": v(100, 173.2) * mm, "construction": true});
            skLineSegment(sketch, "E9.4.5.3", {"start": v(80, 173.2) * mm, "end": v(100, 173.2) * mm, "construction": true});
            skLineSegment(sketch, "E9.4.5.4", {"start": v(90, 155.88) * mm, "end": v(80, 173.2) * mm, "construction": true});
            skLineSegment(sketch, "E9.4.5.5", {"start": v(90, 190.53) * mm, "end": v(80, 173.2) * mm, "construction": true});
            skLineSegment(sketch, "E9.4.5.6", {"start": v(100, 173.2) * mm, "end": v(90, 190.53) * mm, "construction": true});
            skLineSegment(sketch, "E9.4.5.7", {"start": v(90, 190.53) * mm, "end": v(110, 190.53) * mm, "construction": true});
            skLineSegment(sketch, "E9.4.5.8", {"start": v(110, 190.53) * mm, "end": v(100, 173.2) * mm, "construction": true});
            skLineSegment(sketch, "E9.4.6.0", {"start": v(90, 190.53) * mm, "end": v(110, 190.53) * mm, "construction": true});
            skLineSegment(sketch, "E9.4.6.1", {"start": v(100, 207.85) * mm, "end": v(90, 190.53) * mm, "construction": true});
            skLineSegment(sketch, "E9.4.6.2", {"start": v(110, 190.53) * mm, "end": v(100, 207.85) * mm, "construction": true});
            skLineSegment(sketch, "E9.4.6.3", {"start": v(80, 207.85) * mm, "end": v(100, 207.85) * mm, "construction": true});
            skLineSegment(sketch, "E9.4.6.4", {"start": v(90, 190.53) * mm, "end": v(80, 207.85) * mm, "construction": true});
            skLineSegment(sketch, "E9.4.6.5", {"start": v(90, 225.17) * mm, "end": v(80, 207.85) * mm, "construction": true});
            skLineSegment(sketch, "E9.4.6.6", {"start": v(100, 207.85) * mm, "end": v(90, 225.17) * mm, "construction": true});
            skLineSegment(sketch, "E9.4.6.7", {"start": v(90, 225.17) * mm, "end": v(110, 225.17) * mm});
            skLineSegment(sketch, "E9.4.6.8", {"start": v(110, 225.17) * mm, "end": v(100, 207.85) * mm, "construction": true});
            skLineSegment(sketch, "E9.5.0.0", {"start": v(110, -17.32) * mm, "end": v(130, -17.32) * mm});
            skLineSegment(sketch, "E9.5.0.1", {"start": v(120, 0) * mm, "end": v(110, -17.32) * mm, "construction": true});
            skLineSegment(sketch, "E9.5.0.2", {"start": v(130, -17.32) * mm, "end": v(120, 0) * mm, "construction": true});
            skLineSegment(sketch, "E9.5.0.3", {"start": v(100, 0) * mm, "end": v(120, 0) * mm, "construction": true});
            skLineSegment(sketch, "E9.5.0.4", {"start": v(110, -17.32) * mm, "end": v(100, 0) * mm, "construction": true});
            skLineSegment(sketch, "E9.5.0.5", {"start": v(110, 17.32) * mm, "end": v(100, 0) * mm, "construction": true});
            skLineSegment(sketch, "E9.5.0.6", {"start": v(120, 0) * mm, "end": v(110, 17.32) * mm, "construction": true});
            skLineSegment(sketch, "E9.5.0.7", {"start": v(110, 17.32) * mm, "end": v(130, 17.32) * mm, "construction": true});
            skLineSegment(sketch, "E9.5.0.8", {"start": v(130, 17.32) * mm, "end": v(120, 0) * mm, "construction": true});
            skLineSegment(sketch, "E9.5.1.0", {"start": v(110, 17.32) * mm, "end": v(130, 17.32) * mm, "construction": true});
            skLineSegment(sketch, "E9.5.1.1", {"start": v(120, 34.64) * mm, "end": v(110, 17.32) * mm, "construction": true});
            skLineSegment(sketch, "E9.5.1.2", {"start": v(130, 17.32) * mm, "end": v(120, 34.64) * mm, "construction": true});
            skLineSegment(sketch, "E9.5.1.3", {"start": v(100, 34.64) * mm, "end": v(120, 34.64) * mm, "construction": true});
            skLineSegment(sketch, "E9.5.1.4", {"start": v(110, 17.32) * mm, "end": v(100, 34.64) * mm, "construction": true});
            skLineSegment(sketch, "E9.5.1.5", {"start": v(110, 51.96) * mm, "end": v(100, 34.64) * mm, "construction": true});
            skLineSegment(sketch, "E9.5.1.6", {"start": v(120, 34.64) * mm, "end": v(110, 51.96) * mm, "construction": true});
            skLineSegment(sketch, "E9.5.1.7", {"start": v(110, 51.96) * mm, "end": v(130, 51.96) * mm, "construction": true});
            skLineSegment(sketch, "E9.5.1.8", {"start": v(130, 51.96) * mm, "end": v(120, 34.64) * mm, "construction": true});
            skLineSegment(sketch, "E9.5.2.0", {"start": v(110, 51.96) * mm, "end": v(130, 51.96) * mm, "construction": true});
            skLineSegment(sketch, "E9.5.2.1", {"start": v(120, 69.28) * mm, "end": v(110, 51.96) * mm, "construction": true});
            skLineSegment(sketch, "E9.5.2.2", {"start": v(130, 51.96) * mm, "end": v(120, 69.28) * mm, "construction": true});
            skLineSegment(sketch, "E9.5.2.3", {"start": v(100, 69.28) * mm, "end": v(120, 69.28) * mm, "construction": true});
            skLineSegment(sketch, "E9.5.2.4", {"start": v(110, 51.96) * mm, "end": v(100, 69.28) * mm, "construction": true});
            skLineSegment(sketch, "E9.5.2.5", {"start": v(110, 86.6) * mm, "end": v(100, 69.28) * mm, "construction": true});
            skLineSegment(sketch, "E9.5.2.6", {"start": v(120, 69.28) * mm, "end": v(110, 86.6) * mm, "construction": true});
            skLineSegment(sketch, "E9.5.2.7", {"start": v(110, 86.6) * mm, "end": v(130, 86.6) * mm, "construction": true});
            skLineSegment(sketch, "E9.5.2.8", {"start": v(130, 86.6) * mm, "end": v(120, 69.28) * mm, "construction": true});
            skLineSegment(sketch, "E9.5.3.0", {"start": v(110, 86.6) * mm, "end": v(130, 86.6) * mm, "construction": true});
            skLineSegment(sketch, "E9.5.3.1", {"start": v(120, 103.92) * mm, "end": v(110, 86.6) * mm, "construction": true});
            skLineSegment(sketch, "E9.5.3.2", {"start": v(130, 86.6) * mm, "end": v(120, 103.92) * mm, "construction": true});
            skLineSegment(sketch, "E9.5.3.3", {"start": v(100, 103.92) * mm, "end": v(120, 103.92) * mm, "construction": true});
            skLineSegment(sketch, "E9.5.3.4", {"start": v(110, 86.6) * mm, "end": v(100, 103.92) * mm, "construction": true});
            skLineSegment(sketch, "E9.5.3.5", {"start": v(110, 121.24) * mm, "end": v(100, 103.92) * mm, "construction": true});
            skLineSegment(sketch, "E9.5.3.6", {"start": v(120, 103.92) * mm, "end": v(110, 121.24) * mm, "construction": true});
            skLineSegment(sketch, "E9.5.3.7", {"start": v(110, 121.24) * mm, "end": v(130, 121.24) * mm, "construction": true});
            skLineSegment(sketch, "E9.5.3.8", {"start": v(130, 121.24) * mm, "end": v(120, 103.92) * mm, "construction": true});
            skLineSegment(sketch, "E9.5.4.0", {"start": v(110, 121.24) * mm, "end": v(130, 121.24) * mm, "construction": true});
            skLineSegment(sketch, "E9.5.4.1", {"start": v(120, 138.56) * mm, "end": v(110, 121.24) * mm, "construction": true});
            skLineSegment(sketch, "E9.5.4.2", {"start": v(130, 121.24) * mm, "end": v(120, 138.56) * mm, "construction": true});
            skLineSegment(sketch, "E9.5.4.3", {"start": v(100, 138.56) * mm, "end": v(120, 138.56) * mm, "construction": true});
            skLineSegment(sketch, "E9.5.4.4", {"start": v(110, 121.24) * mm, "end": v(100, 138.56) * mm, "construction": true});
            skLineSegment(sketch, "E9.5.4.5", {"start": v(110, 155.88) * mm, "end": v(100, 138.56) * mm, "construction": true});
            skLineSegment(sketch, "E9.5.4.6", {"start": v(120, 138.56) * mm, "end": v(110, 155.88) * mm, "construction": true});
            skLineSegment(sketch, "E9.5.4.7", {"start": v(110, 155.88) * mm, "end": v(130, 155.88) * mm, "construction": true});
            skLineSegment(sketch, "E9.5.4.8", {"start": v(130, 155.88) * mm, "end": v(120, 138.56) * mm, "construction": true});
            skLineSegment(sketch, "E9.5.5.0", {"start": v(110, 155.88) * mm, "end": v(130, 155.88) * mm, "construction": true});
            skLineSegment(sketch, "E9.5.5.1", {"start": v(120, 173.2) * mm, "end": v(110, 155.88) * mm, "construction": true});
            skLineSegment(sketch, "E9.5.5.2", {"start": v(130, 155.88) * mm, "end": v(120, 173.2) * mm, "construction": true});
            skLineSegment(sketch, "E9.5.5.3", {"start": v(100, 173.2) * mm, "end": v(120, 173.2) * mm, "construction": true});
            skLineSegment(sketch, "E9.5.5.4", {"start": v(110, 155.88) * mm, "end": v(100, 173.2) * mm, "construction": true});
            skLineSegment(sketch, "E9.5.5.5", {"start": v(110, 190.53) * mm, "end": v(100, 173.2) * mm, "construction": true});
            skLineSegment(sketch, "E9.5.5.6", {"start": v(120, 173.2) * mm, "end": v(110, 190.53) * mm, "construction": true});
            skLineSegment(sketch, "E9.5.5.7", {"start": v(110, 190.53) * mm, "end": v(130, 190.53) * mm, "construction": true});
            skLineSegment(sketch, "E9.5.5.8", {"start": v(130, 190.53) * mm, "end": v(120, 173.2) * mm, "construction": true});
            skLineSegment(sketch, "E9.5.6.0", {"start": v(110, 190.53) * mm, "end": v(130, 190.53) * mm, "construction": true});
            skLineSegment(sketch, "E9.5.6.1", {"start": v(120, 207.85) * mm, "end": v(110, 190.53) * mm, "construction": true});
            skLineSegment(sketch, "E9.5.6.2", {"start": v(130, 190.53) * mm, "end": v(120, 207.85) * mm, "construction": true});
            skLineSegment(sketch, "E9.5.6.3", {"start": v(100, 207.85) * mm, "end": v(120, 207.85) * mm, "construction": true});
            skLineSegment(sketch, "E9.5.6.4", {"start": v(110, 190.53) * mm, "end": v(100, 207.85) * mm, "construction": true});
            skLineSegment(sketch, "E9.5.6.5", {"start": v(110, 225.17) * mm, "end": v(100, 207.85) * mm, "construction": true});
            skLineSegment(sketch, "E9.5.6.6", {"start": v(120, 207.85) * mm, "end": v(110, 225.17) * mm, "construction": true});
            skLineSegment(sketch, "E9.5.6.7", {"start": v(110, 225.17) * mm, "end": v(130, 225.17) * mm});
            skLineSegment(sketch, "E9.5.6.8", {"start": v(130, 225.17) * mm, "end": v(120, 207.85) * mm, "construction": true});
            skLineSegment(sketch, "E9.6.0.0", {"start": v(130, -17.32) * mm, "end": v(150, -17.32) * mm});
            skLineSegment(sketch, "E9.6.0.1", {"start": v(140, 0) * mm, "end": v(130, -17.32) * mm, "construction": true});
            skLineSegment(sketch, "E9.6.0.2", {"start": v(150, -17.32) * mm, "end": v(140, 0) * mm, "construction": true});
            skLineSegment(sketch, "E9.6.0.3", {"start": v(120, 0) * mm, "end": v(140, 0) * mm, "construction": true});
            skLineSegment(sketch, "E9.6.0.4", {"start": v(130, -17.32) * mm, "end": v(120, 0) * mm, "construction": true});
            skLineSegment(sketch, "E9.6.0.5", {"start": v(130, 17.32) * mm, "end": v(120, 0) * mm, "construction": true});
            skLineSegment(sketch, "E9.6.0.6", {"start": v(140, 0) * mm, "end": v(130, 17.32) * mm, "construction": true});
            skLineSegment(sketch, "E9.6.0.7", {"start": v(130, 17.32) * mm, "end": v(150, 17.32) * mm, "construction": true});
            skLineSegment(sketch, "E9.6.0.8", {"start": v(150, 17.32) * mm, "end": v(140, 0) * mm, "construction": true});
            skLineSegment(sketch, "E9.6.1.0", {"start": v(130, 17.32) * mm, "end": v(150, 17.32) * mm, "construction": true});
            skLineSegment(sketch, "E9.6.1.1", {"start": v(140, 34.64) * mm, "end": v(130, 17.32) * mm, "construction": true});
            skLineSegment(sketch, "E9.6.1.2", {"start": v(150, 17.32) * mm, "end": v(140, 34.64) * mm, "construction": true});
            skLineSegment(sketch, "E9.6.1.3", {"start": v(120, 34.64) * mm, "end": v(140, 34.64) * mm, "construction": true});
            skLineSegment(sketch, "E9.6.1.4", {"start": v(130, 17.32) * mm, "end": v(120, 34.64) * mm, "construction": true});
            skLineSegment(sketch, "E9.6.1.5", {"start": v(130, 51.96) * mm, "end": v(120, 34.64) * mm, "construction": true});
            skLineSegment(sketch, "E9.6.1.6", {"start": v(140, 34.64) * mm, "end": v(130, 51.96) * mm, "construction": true});
            skLineSegment(sketch, "E9.6.1.7", {"start": v(130, 51.96) * mm, "end": v(150, 51.96) * mm, "construction": true});
            skLineSegment(sketch, "E9.6.1.8", {"start": v(150, 51.96) * mm, "end": v(140, 34.64) * mm, "construction": true});
            skLineSegment(sketch, "E9.6.2.0", {"start": v(130, 51.96) * mm, "end": v(150, 51.96) * mm, "construction": true});
            skLineSegment(sketch, "E9.6.2.1", {"start": v(140, 69.28) * mm, "end": v(130, 51.96) * mm, "construction": true});
            skLineSegment(sketch, "E9.6.2.2", {"start": v(150, 51.96) * mm, "end": v(140, 69.28) * mm, "construction": true});
            skLineSegment(sketch, "E9.6.2.3", {"start": v(120, 69.28) * mm, "end": v(140, 69.28) * mm, "construction": true});
            skLineSegment(sketch, "E9.6.2.4", {"start": v(130, 51.96) * mm, "end": v(120, 69.28) * mm, "construction": true});
            skLineSegment(sketch, "E9.6.2.5", {"start": v(130, 86.6) * mm, "end": v(120, 69.28) * mm, "construction": true});
            skLineSegment(sketch, "E9.6.2.6", {"start": v(140, 69.28) * mm, "end": v(130, 86.6) * mm, "construction": true});
            skLineSegment(sketch, "E9.6.2.7", {"start": v(130, 86.6) * mm, "end": v(150, 86.6) * mm, "construction": true});
            skLineSegment(sketch, "E9.6.2.8", {"start": v(150, 86.6) * mm, "end": v(140, 69.28) * mm, "construction": true});
            skLineSegment(sketch, "E9.6.3.0", {"start": v(130, 86.6) * mm, "end": v(150, 86.6) * mm, "construction": true});
            skLineSegment(sketch, "E9.6.3.1", {"start": v(140, 103.92) * mm, "end": v(130, 86.6) * mm, "construction": true});
            skLineSegment(sketch, "E9.6.3.2", {"start": v(150, 86.6) * mm, "end": v(140, 103.92) * mm, "construction": true});
            skLineSegment(sketch, "E9.6.3.3", {"start": v(120, 103.92) * mm, "end": v(140, 103.92) * mm, "construction": true});
            skLineSegment(sketch, "E9.6.3.4", {"start": v(130, 86.6) * mm, "end": v(120, 103.92) * mm, "construction": true});
            skLineSegment(sketch, "E9.6.3.5", {"start": v(130, 121.24) * mm, "end": v(120, 103.92) * mm, "construction": true});
            skLineSegment(sketch, "E9.6.3.6", {"start": v(140, 103.92) * mm, "end": v(130, 121.24) * mm, "construction": true});
            skLineSegment(sketch, "E9.6.3.7", {"start": v(130, 121.24) * mm, "end": v(150, 121.24) * mm, "construction": true});
            skLineSegment(sketch, "E9.6.3.8", {"start": v(150, 121.24) * mm, "end": v(140, 103.92) * mm, "construction": true});
            skLineSegment(sketch, "E9.6.4.0", {"start": v(130, 121.24) * mm, "end": v(150, 121.24) * mm, "construction": true});
            skLineSegment(sketch, "E9.6.4.1", {"start": v(140, 138.56) * mm, "end": v(130, 121.24) * mm, "construction": true});
            skLineSegment(sketch, "E9.6.4.2", {"start": v(150, 121.24) * mm, "end": v(140, 138.56) * mm, "construction": true});
            skLineSegment(sketch, "E9.6.4.3", {"start": v(120, 138.56) * mm, "end": v(140, 138.56) * mm, "construction": true});
            skLineSegment(sketch, "E9.6.4.4", {"start": v(130, 121.24) * mm, "end": v(120, 138.56) * mm, "construction": true});
            skLineSegment(sketch, "E9.6.4.5", {"start": v(130, 155.88) * mm, "end": v(120, 138.56) * mm, "construction": true});
            skLineSegment(sketch, "E9.6.4.6", {"start": v(140, 138.56) * mm, "end": v(130, 155.88) * mm, "construction": true});
            skLineSegment(sketch, "E9.6.4.7", {"start": v(130, 155.88) * mm, "end": v(150, 155.88) * mm, "construction": true});
            skLineSegment(sketch, "E9.6.4.8", {"start": v(150, 155.88) * mm, "end": v(140, 138.56) * mm, "construction": true});
            skLineSegment(sketch, "E9.6.5.0", {"start": v(130, 155.88) * mm, "end": v(150, 155.88) * mm, "construction": true});
            skLineSegment(sketch, "E9.6.5.1", {"start": v(140, 173.2) * mm, "end": v(130, 155.88) * mm, "construction": true});
            skLineSegment(sketch, "E9.6.5.2", {"start": v(150, 155.88) * mm, "end": v(140, 173.2) * mm, "construction": true});
            skLineSegment(sketch, "E9.6.5.3", {"start": v(120, 173.2) * mm, "end": v(140, 173.2) * mm, "construction": true});
            skLineSegment(sketch, "E9.6.5.4", {"start": v(130, 155.88) * mm, "end": v(120, 173.2) * mm, "construction": true});
            skLineSegment(sketch, "E9.6.5.5", {"start": v(130, 190.53) * mm, "end": v(120, 173.2) * mm, "construction": true});
            skLineSegment(sketch, "E9.6.5.6", {"start": v(140, 173.2) * mm, "end": v(130, 190.53) * mm, "construction": true});
            skLineSegment(sketch, "E9.6.5.7", {"start": v(130, 190.53) * mm, "end": v(150, 190.53) * mm, "construction": true});
            skLineSegment(sketch, "E9.6.5.8", {"start": v(150, 190.53) * mm, "end": v(140, 173.2) * mm, "construction": true});
            skLineSegment(sketch, "E9.6.6.0", {"start": v(130, 190.53) * mm, "end": v(150, 190.53) * mm, "construction": true});
            skLineSegment(sketch, "E9.6.6.1", {"start": v(140, 207.85) * mm, "end": v(130, 190.53) * mm, "construction": true});
            skLineSegment(sketch, "E9.6.6.2", {"start": v(150, 190.53) * mm, "end": v(140, 207.85) * mm, "construction": true});
            skLineSegment(sketch, "E9.6.6.3", {"start": v(120, 207.85) * mm, "end": v(140, 207.85) * mm, "construction": true});
            skLineSegment(sketch, "E9.6.6.4", {"start": v(130, 190.53) * mm, "end": v(120, 207.85) * mm, "construction": true});
            skLineSegment(sketch, "E9.6.6.5", {"start": v(130, 225.17) * mm, "end": v(120, 207.85) * mm, "construction": true});
            skLineSegment(sketch, "E9.6.6.6", {"start": v(140, 207.85) * mm, "end": v(130, 225.17) * mm, "construction": true});
            skLineSegment(sketch, "E9.6.6.7", {"start": v(130, 225.17) * mm, "end": v(150, 225.17) * mm});
            skLineSegment(sketch, "E9.6.6.8", {"start": v(150, 225.17) * mm, "end": v(140, 207.85) * mm, "construction": true});
            skLineSegment(sketch, "E9.7.0.0", {"start": v(150, -17.32) * mm, "end": v(170, -17.32) * mm});
            skLineSegment(sketch, "E9.7.0.1", {"start": v(160, 0) * mm, "end": v(150, -17.32) * mm, "construction": true});
            skLineSegment(sketch, "E9.7.0.2", {"start": v(170, -17.32) * mm, "end": v(160, 0) * mm, "construction": true});
            skLineSegment(sketch, "E9.7.0.3", {"start": v(140, 0) * mm, "end": v(160, 0) * mm, "construction": true});
            skLineSegment(sketch, "E9.7.0.4", {"start": v(150, -17.32) * mm, "end": v(140, 0) * mm, "construction": true});
            skLineSegment(sketch, "E9.7.0.5", {"start": v(150, 17.32) * mm, "end": v(140, 0) * mm, "construction": true});
            skLineSegment(sketch, "E9.7.0.6", {"start": v(160, 0) * mm, "end": v(150, 17.32) * mm, "construction": true});
            skLineSegment(sketch, "E9.7.0.7", {"start": v(150, 17.32) * mm, "end": v(170, 17.32) * mm, "construction": true});
            skLineSegment(sketch, "E9.7.0.8", {"start": v(170, 17.32) * mm, "end": v(160, 0) * mm, "construction": true});
            skLineSegment(sketch, "E9.7.1.0", {"start": v(150, 17.32) * mm, "end": v(170, 17.32) * mm, "construction": true});
            skLineSegment(sketch, "E9.7.1.1", {"start": v(160, 34.64) * mm, "end": v(150, 17.32) * mm, "construction": true});
            skLineSegment(sketch, "E9.7.1.2", {"start": v(170, 17.32) * mm, "end": v(160, 34.64) * mm, "construction": true});
            skLineSegment(sketch, "E9.7.1.3", {"start": v(140, 34.64) * mm, "end": v(160, 34.64) * mm, "construction": true});
            skLineSegment(sketch, "E9.7.1.4", {"start": v(150, 17.32) * mm, "end": v(140, 34.64) * mm, "construction": true});
            skLineSegment(sketch, "E9.7.1.5", {"start": v(150, 51.96) * mm, "end": v(140, 34.64) * mm, "construction": true});
            skLineSegment(sketch, "E9.7.1.6", {"start": v(160, 34.64) * mm, "end": v(150, 51.96) * mm, "construction": true});
            skLineSegment(sketch, "E9.7.1.7", {"start": v(150, 51.96) * mm, "end": v(170, 51.96) * mm, "construction": true});
            skLineSegment(sketch, "E9.7.1.8", {"start": v(170, 51.96) * mm, "end": v(160, 34.64) * mm, "construction": true});
            skLineSegment(sketch, "E9.7.2.0", {"start": v(150, 51.96) * mm, "end": v(170, 51.96) * mm, "construction": true});
            skLineSegment(sketch, "E9.7.2.1", {"start": v(160, 69.28) * mm, "end": v(150, 51.96) * mm, "construction": true});
            skLineSegment(sketch, "E9.7.2.2", {"start": v(170, 51.96) * mm, "end": v(160, 69.28) * mm, "construction": true});
            skLineSegment(sketch, "E9.7.2.3", {"start": v(140, 69.28) * mm, "end": v(160, 69.28) * mm, "construction": true});
            skLineSegment(sketch, "E9.7.2.4", {"start": v(150, 51.96) * mm, "end": v(140, 69.28) * mm, "construction": true});
            skLineSegment(sketch, "E9.7.2.5", {"start": v(150, 86.6) * mm, "end": v(140, 69.28) * mm, "construction": true});
            skLineSegment(sketch, "E9.7.2.6", {"start": v(160, 69.28) * mm, "end": v(150, 86.6) * mm, "construction": true});
            skLineSegment(sketch, "E9.7.2.7", {"start": v(150, 86.6) * mm, "end": v(170, 86.6) * mm, "construction": true});
            skLineSegment(sketch, "E9.7.2.8", {"start": v(170, 86.6) * mm, "end": v(160, 69.28) * mm, "construction": true});
            skLineSegment(sketch, "E9.7.3.0", {"start": v(150, 86.6) * mm, "end": v(170, 86.6) * mm, "construction": true});
            skLineSegment(sketch, "E9.7.3.1", {"start": v(160, 103.92) * mm, "end": v(150, 86.6) * mm, "construction": true});
            skLineSegment(sketch, "E9.7.3.2", {"start": v(170, 86.6) * mm, "end": v(160, 103.92) * mm, "construction": true});
            skLineSegment(sketch, "E9.7.3.3", {"start": v(140, 103.92) * mm, "end": v(160, 103.92) * mm, "construction": true});
            skLineSegment(sketch, "E9.7.3.4", {"start": v(150, 86.6) * mm, "end": v(140, 103.92) * mm, "construction": true});
            skLineSegment(sketch, "E9.7.3.5", {"start": v(150, 121.24) * mm, "end": v(140, 103.92) * mm, "construction": true});
            skLineSegment(sketch, "E9.7.3.6", {"start": v(160, 103.92) * mm, "end": v(150, 121.24) * mm, "construction": true});
            skLineSegment(sketch, "E9.7.3.7", {"start": v(150, 121.24) * mm, "end": v(170, 121.24) * mm, "construction": true});
            skLineSegment(sketch, "E9.7.3.8", {"start": v(170, 121.24) * mm, "end": v(160, 103.92) * mm, "construction": true});
            skLineSegment(sketch, "E9.7.4.0", {"start": v(150, 121.24) * mm, "end": v(170, 121.24) * mm, "construction": true});
            skLineSegment(sketch, "E9.7.4.1", {"start": v(160, 138.56) * mm, "end": v(150, 121.24) * mm, "construction": true});
            skLineSegment(sketch, "E9.7.4.2", {"start": v(170, 121.24) * mm, "end": v(160, 138.56) * mm, "construction": true});
            skLineSegment(sketch, "E9.7.4.3", {"start": v(140, 138.56) * mm, "end": v(160, 138.56) * mm, "construction": true});
            skLineSegment(sketch, "E9.7.4.4", {"start": v(150, 121.24) * mm, "end": v(140, 138.56) * mm, "construction": true});
            skLineSegment(sketch, "E9.7.4.5", {"start": v(150, 155.88) * mm, "end": v(140, 138.56) * mm, "construction": true});
            skLineSegment(sketch, "E9.7.4.6", {"start": v(160, 138.56) * mm, "end": v(150, 155.88) * mm, "construction": true});
            skLineSegment(sketch, "E9.7.4.7", {"start": v(150, 155.88) * mm, "end": v(170, 155.88) * mm, "construction": true});
            skLineSegment(sketch, "E9.7.4.8", {"start": v(170, 155.88) * mm, "end": v(160, 138.56) * mm, "construction": true});
            skLineSegment(sketch, "E9.7.5.0", {"start": v(150, 155.88) * mm, "end": v(170, 155.88) * mm, "construction": true});
            skLineSegment(sketch, "E9.7.5.1", {"start": v(160, 173.2) * mm, "end": v(150, 155.88) * mm, "construction": true});
            skLineSegment(sketch, "E9.7.5.2", {"start": v(170, 155.88) * mm, "end": v(160, 173.2) * mm, "construction": true});
            skLineSegment(sketch, "E9.7.5.3", {"start": v(140, 173.2) * mm, "end": v(160, 173.2) * mm, "construction": true});
            skLineSegment(sketch, "E9.7.5.4", {"start": v(150, 155.88) * mm, "end": v(140, 173.2) * mm, "construction": true});
            skLineSegment(sketch, "E9.7.5.5", {"start": v(150, 190.53) * mm, "end": v(140, 173.2) * mm, "construction": true});
            skLineSegment(sketch, "E9.7.5.6", {"start": v(160, 173.2) * mm, "end": v(150, 190.53) * mm, "construction": true});
            skLineSegment(sketch, "E9.7.5.7", {"start": v(150, 190.53) * mm, "end": v(170, 190.53) * mm, "construction": true});
            skLineSegment(sketch, "E9.7.5.8", {"start": v(170, 190.53) * mm, "end": v(160, 173.2) * mm, "construction": true});
            skLineSegment(sketch, "E9.7.6.0", {"start": v(150, 190.53) * mm, "end": v(170, 190.53) * mm, "construction": true});
            skLineSegment(sketch, "E9.7.6.1", {"start": v(160, 207.85) * mm, "end": v(150, 190.53) * mm, "construction": true});
            skLineSegment(sketch, "E9.7.6.2", {"start": v(170, 190.53) * mm, "end": v(160, 207.85) * mm, "construction": true});
            skLineSegment(sketch, "E9.7.6.3", {"start": v(140, 207.85) * mm, "end": v(160, 207.85) * mm, "construction": true});
            skLineSegment(sketch, "E9.7.6.4", {"start": v(150, 190.53) * mm, "end": v(140, 207.85) * mm, "construction": true});
            skLineSegment(sketch, "E9.7.6.5", {"start": v(150, 225.17) * mm, "end": v(140, 207.85) * mm, "construction": true});
            skLineSegment(sketch, "E9.7.6.6", {"start": v(160, 207.85) * mm, "end": v(150, 225.17) * mm, "construction": true});
            skLineSegment(sketch, "E9.7.6.7", {"start": v(150, 225.17) * mm, "end": v(170, 225.17) * mm});
            skLineSegment(sketch, "E9.7.6.8", {"start": v(170, 225.17) * mm, "end": v(160, 207.85) * mm, "construction": true});
            skLineSegment(sketch, "E9.8.0.0", {"start": v(170, -17.32) * mm, "end": v(190, -17.32) * mm});
            skLineSegment(sketch, "E9.8.0.1", {"start": v(180, 0) * mm, "end": v(170, -17.32) * mm, "construction": true});
            skLineSegment(sketch, "E9.8.0.2", {"start": v(190, -17.32) * mm, "end": v(180, 0) * mm, "construction": true});
            skLineSegment(sketch, "E9.8.0.3", {"start": v(160, 0) * mm, "end": v(180, 0) * mm, "construction": true});
            skLineSegment(sketch, "E9.8.0.4", {"start": v(170, -17.32) * mm, "end": v(160, 0) * mm, "construction": true});
            skLineSegment(sketch, "E9.8.0.5", {"start": v(170, 17.32) * mm, "end": v(160, 0) * mm, "construction": true});
            skLineSegment(sketch, "E9.8.0.6", {"start": v(180, 0) * mm, "end": v(170, 17.32) * mm, "construction": true});
            skLineSegment(sketch, "E9.8.0.7", {"start": v(170, 17.32) * mm, "end": v(190, 17.32) * mm, "construction": true});
            skLineSegment(sketch, "E9.8.0.8", {"start": v(190, 17.32) * mm, "end": v(180, 0) * mm, "construction": true});
            skLineSegment(sketch, "E9.8.1.0", {"start": v(170, 17.32) * mm, "end": v(190, 17.32) * mm, "construction": true});
            skLineSegment(sketch, "E9.8.1.1", {"start": v(180, 34.64) * mm, "end": v(170, 17.32) * mm, "construction": true});
            skLineSegment(sketch, "E9.8.1.2", {"start": v(190, 17.32) * mm, "end": v(180, 34.64) * mm, "construction": true});
            skLineSegment(sketch, "E9.8.1.3", {"start": v(160, 34.64) * mm, "end": v(180, 34.64) * mm, "construction": true});
            skLineSegment(sketch, "E9.8.1.4", {"start": v(170, 17.32) * mm, "end": v(160, 34.64) * mm, "construction": true});
            skLineSegment(sketch, "E9.8.1.5", {"start": v(170, 51.96) * mm, "end": v(160, 34.64) * mm, "construction": true});
            skLineSegment(sketch, "E9.8.1.6", {"start": v(180, 34.64) * mm, "end": v(170, 51.96) * mm, "construction": true});
            skLineSegment(sketch, "E9.8.1.7", {"start": v(170, 51.96) * mm, "end": v(190, 51.96) * mm, "construction": true});
            skLineSegment(sketch, "E9.8.1.8", {"start": v(190, 51.96) * mm, "end": v(180, 34.64) * mm, "construction": true});
            skLineSegment(sketch, "E9.8.2.0", {"start": v(170, 51.96) * mm, "end": v(190, 51.96) * mm, "construction": true});
            skLineSegment(sketch, "E9.8.2.1", {"start": v(180, 69.28) * mm, "end": v(170, 51.96) * mm, "construction": true});
            skLineSegment(sketch, "E9.8.2.2", {"start": v(190, 51.96) * mm, "end": v(180, 69.28) * mm, "construction": true});
            skLineSegment(sketch, "E9.8.2.3", {"start": v(160, 69.28) * mm, "end": v(180, 69.28) * mm, "construction": true});
            skLineSegment(sketch, "E9.8.2.4", {"start": v(170, 51.96) * mm, "end": v(160, 69.28) * mm, "construction": true});
            skLineSegment(sketch, "E9.8.2.5", {"start": v(170, 86.6) * mm, "end": v(160, 69.28) * mm, "construction": true});
            skLineSegment(sketch, "E9.8.2.6", {"start": v(180, 69.28) * mm, "end": v(170, 86.6) * mm, "construction": true});
            skLineSegment(sketch, "E9.8.2.7", {"start": v(170, 86.6) * mm, "end": v(190, 86.6) * mm, "construction": true});
            skLineSegment(sketch, "E9.8.2.8", {"start": v(190, 86.6) * mm, "end": v(180, 69.28) * mm, "construction": true});
            skLineSegment(sketch, "E9.8.3.0", {"start": v(170, 86.6) * mm, "end": v(190, 86.6) * mm, "construction": true});
            skLineSegment(sketch, "E9.8.3.1", {"start": v(180, 103.92) * mm, "end": v(170, 86.6) * mm, "construction": true});
            skLineSegment(sketch, "E9.8.3.2", {"start": v(190, 86.6) * mm, "end": v(180, 103.92) * mm, "construction": true});
            skLineSegment(sketch, "E9.8.3.3", {"start": v(160, 103.92) * mm, "end": v(180, 103.92) * mm, "construction": true});
            skLineSegment(sketch, "E9.8.3.4", {"start": v(170, 86.6) * mm, "end": v(160, 103.92) * mm, "construction": true});
            skLineSegment(sketch, "E9.8.3.5", {"start": v(170, 121.24) * mm, "end": v(160, 103.92) * mm, "construction": true});
            skLineSegment(sketch, "E9.8.3.6", {"start": v(180, 103.92) * mm, "end": v(170, 121.24) * mm, "construction": true});
            skLineSegment(sketch, "E9.8.3.7", {"start": v(170, 121.24) * mm, "end": v(190, 121.24) * mm, "construction": true});
            skLineSegment(sketch, "E9.8.3.8", {"start": v(190, 121.24) * mm, "end": v(180, 103.92) * mm, "construction": true});
            skLineSegment(sketch, "E9.8.4.0", {"start": v(170, 121.24) * mm, "end": v(190, 121.24) * mm, "construction": true});
            skLineSegment(sketch, "E9.8.4.1", {"start": v(180, 138.56) * mm, "end": v(170, 121.24) * mm, "construction": true});
            skLineSegment(sketch, "E9.8.4.2", {"start": v(190, 121.24) * mm, "end": v(180, 138.56) * mm, "construction": true});
            skLineSegment(sketch, "E9.8.4.3", {"start": v(160, 138.56) * mm, "end": v(180, 138.56) * mm, "construction": true});
            skLineSegment(sketch, "E9.8.4.4", {"start": v(170, 121.24) * mm, "end": v(160, 138.56) * mm, "construction": true});
            skLineSegment(sketch, "E9.8.4.5", {"start": v(170, 155.88) * mm, "end": v(160, 138.56) * mm, "construction": true});
            skLineSegment(sketch, "E9.8.4.6", {"start": v(180, 138.56) * mm, "end": v(170, 155.88) * mm, "construction": true});
            skLineSegment(sketch, "E9.8.4.7", {"start": v(170, 155.88) * mm, "end": v(190, 155.88) * mm, "construction": true});
            skLineSegment(sketch, "E9.8.4.8", {"start": v(190, 155.88) * mm, "end": v(180, 138.56) * mm, "construction": true});
            skLineSegment(sketch, "E9.8.5.0", {"start": v(170, 155.88) * mm, "end": v(190, 155.88) * mm, "construction": true});
            skLineSegment(sketch, "E9.8.5.1", {"start": v(180, 173.2) * mm, "end": v(170, 155.88) * mm, "construction": true});
            skLineSegment(sketch, "E9.8.5.2", {"start": v(190, 155.88) * mm, "end": v(180, 173.2) * mm, "construction": true});
            skLineSegment(sketch, "E9.8.5.3", {"start": v(160, 173.2) * mm, "end": v(180, 173.2) * mm, "construction": true});
            skLineSegment(sketch, "E9.8.5.4", {"start": v(170, 155.88) * mm, "end": v(160, 173.2) * mm, "construction": true});
            skLineSegment(sketch, "E9.8.5.5", {"start": v(170, 190.53) * mm, "end": v(160, 173.2) * mm, "construction": true});
            skLineSegment(sketch, "E9.8.5.6", {"start": v(180, 173.2) * mm, "end": v(170, 190.53) * mm, "construction": true});
            skLineSegment(sketch, "E9.8.5.7", {"start": v(170, 190.53) * mm, "end": v(190, 190.53) * mm, "construction": true});
            skLineSegment(sketch, "E9.8.5.8", {"start": v(190, 190.53) * mm, "end": v(180, 173.2) * mm, "construction": true});
            skLineSegment(sketch, "E9.8.6.0", {"start": v(170, 190.53) * mm, "end": v(190, 190.53) * mm, "construction": true});
            skLineSegment(sketch, "E9.8.6.1", {"start": v(180, 207.85) * mm, "end": v(170, 190.53) * mm, "construction": true});
            skLineSegment(sketch, "E9.8.6.2", {"start": v(190, 190.53) * mm, "end": v(180, 207.85) * mm, "construction": true});
            skLineSegment(sketch, "E9.8.6.3", {"start": v(160, 207.85) * mm, "end": v(180, 207.85) * mm, "construction": true});
            skLineSegment(sketch, "E9.8.6.4", {"start": v(170, 190.53) * mm, "end": v(160, 207.85) * mm, "construction": true});
            skLineSegment(sketch, "E9.8.6.5", {"start": v(170, 225.17) * mm, "end": v(160, 207.85) * mm, "construction": true});
            skLineSegment(sketch, "E9.8.6.6", {"start": v(180, 207.85) * mm, "end": v(170, 225.17) * mm, "construction": true});
            skLineSegment(sketch, "E9.8.6.7", {"start": v(170, 225.17) * mm, "end": v(190, 225.17) * mm});
            skLineSegment(sketch, "E9.8.6.8", {"start": v(190, 225.17) * mm, "end": v(180, 207.85) * mm, "construction": true});
            skLineSegment(sketch, "E9.9.0.0", {"start": v(190, -17.32) * mm, "end": v(210, -17.32) * mm});
            skLineSegment(sketch, "E9.9.0.1", {"start": v(200, 0) * mm, "end": v(190, -17.32) * mm, "construction": true});
            skLineSegment(sketch, "E9.9.0.2", {"start": v(210, -17.32) * mm, "end": v(200, 0) * mm, "construction": true});
            skLineSegment(sketch, "E9.9.0.3", {"start": v(180, 0) * mm, "end": v(200, 0) * mm, "construction": true});
            skLineSegment(sketch, "E9.9.0.4", {"start": v(190, -17.32) * mm, "end": v(180, 0) * mm, "construction": true});
            skLineSegment(sketch, "E9.9.0.5", {"start": v(190, 17.32) * mm, "end": v(180, 0) * mm, "construction": true});
            skLineSegment(sketch, "E9.9.0.6", {"start": v(200, 0) * mm, "end": v(190, 17.32) * mm, "construction": true});
            skLineSegment(sketch, "E9.9.0.7", {"start": v(190, 17.32) * mm, "end": v(210, 17.32) * mm, "construction": true});
            skLineSegment(sketch, "E9.9.0.8", {"start": v(210, 17.32) * mm, "end": v(200, 0) * mm, "construction": true});
            skLineSegment(sketch, "E9.9.1.0", {"start": v(190, 17.32) * mm, "end": v(210, 17.32) * mm, "construction": true});
            skLineSegment(sketch, "E9.9.1.1", {"start": v(200, 34.64) * mm, "end": v(190, 17.32) * mm, "construction": true});
            skLineSegment(sketch, "E9.9.1.2", {"start": v(210, 17.32) * mm, "end": v(200, 34.64) * mm, "construction": true});
            skLineSegment(sketch, "E9.9.1.3", {"start": v(180, 34.64) * mm, "end": v(200, 34.64) * mm, "construction": true});
            skLineSegment(sketch, "E9.9.1.4", {"start": v(190, 17.32) * mm, "end": v(180, 34.64) * mm, "construction": true});
            skLineSegment(sketch, "E9.9.1.5", {"start": v(190, 51.96) * mm, "end": v(180, 34.64) * mm, "construction": true});
            skLineSegment(sketch, "E9.9.1.6", {"start": v(200, 34.64) * mm, "end": v(190, 51.96) * mm, "construction": true});
            skLineSegment(sketch, "E9.9.1.7", {"start": v(190, 51.96) * mm, "end": v(210, 51.96) * mm, "construction": true});
            skLineSegment(sketch, "E9.9.1.8", {"start": v(210, 51.96) * mm, "end": v(200, 34.64) * mm, "construction": true});
            skLineSegment(sketch, "E9.9.2.0", {"start": v(190, 51.96) * mm, "end": v(210, 51.96) * mm, "construction": true});
            skLineSegment(sketch, "E9.9.2.1", {"start": v(200, 69.28) * mm, "end": v(190, 51.96) * mm, "construction": true});
            skLineSegment(sketch, "E9.9.2.2", {"start": v(210, 51.96) * mm, "end": v(200, 69.28) * mm, "construction": true});
            skLineSegment(sketch, "E9.9.2.3", {"start": v(180, 69.28) * mm, "end": v(200, 69.28) * mm, "construction": true});
            skLineSegment(sketch, "E9.9.2.4", {"start": v(190, 51.96) * mm, "end": v(180, 69.28) * mm, "construction": true});
            skLineSegment(sketch, "E9.9.2.5", {"start": v(190, 86.6) * mm, "end": v(180, 69.28) * mm, "construction": true});
            skLineSegment(sketch, "E9.9.2.6", {"start": v(200, 69.28) * mm, "end": v(190, 86.6) * mm, "construction": true});
            skLineSegment(sketch, "E9.9.2.7", {"start": v(190, 86.6) * mm, "end": v(210, 86.6) * mm, "construction": true});
            skLineSegment(sketch, "E9.9.2.8", {"start": v(210, 86.6) * mm, "end": v(200, 69.28) * mm, "construction": true});
            skLineSegment(sketch, "E9.9.3.0", {"start": v(190, 86.6) * mm, "end": v(210, 86.6) * mm, "construction": true});
            skLineSegment(sketch, "E9.9.3.1", {"start": v(200, 103.92) * mm, "end": v(190, 86.6) * mm, "construction": true});
            skLineSegment(sketch, "E9.9.3.2", {"start": v(210, 86.6) * mm, "end": v(200, 103.92) * mm, "construction": true});
            skLineSegment(sketch, "E9.9.3.3", {"start": v(180, 103.92) * mm, "end": v(200, 103.92) * mm, "construction": true});
            skLineSegment(sketch, "E9.9.3.4", {"start": v(190, 86.6) * mm, "end": v(180, 103.92) * mm, "construction": true});
            skLineSegment(sketch, "E9.9.3.5", {"start": v(190, 121.24) * mm, "end": v(180, 103.92) * mm, "construction": true});
            skLineSegment(sketch, "E9.9.3.6", {"start": v(200, 103.92) * mm, "end": v(190, 121.24) * mm, "construction": true});
            skLineSegment(sketch, "E9.9.3.7", {"start": v(190, 121.24) * mm, "end": v(210, 121.24) * mm, "construction": true});
            skLineSegment(sketch, "E9.9.3.8", {"start": v(210, 121.24) * mm, "end": v(200, 103.92) * mm, "construction": true});
            skLineSegment(sketch, "E9.9.4.0", {"start": v(190, 121.24) * mm, "end": v(210, 121.24) * mm, "construction": true});
            skLineSegment(sketch, "E9.9.4.1", {"start": v(200, 138.56) * mm, "end": v(190, 121.24) * mm, "construction": true});
            skLineSegment(sketch, "E9.9.4.2", {"start": v(210, 121.24) * mm, "end": v(200, 138.56) * mm, "construction": true});
            skLineSegment(sketch, "E9.9.4.3", {"start": v(180, 138.56) * mm, "end": v(200, 138.56) * mm, "construction": true});
            skLineSegment(sketch, "E9.9.4.4", {"start": v(190, 121.24) * mm, "end": v(180, 138.56) * mm, "construction": true});
            skLineSegment(sketch, "E9.9.4.5", {"start": v(190, 155.88) * mm, "end": v(180, 138.56) * mm, "construction": true});
            skLineSegment(sketch, "E9.9.4.6", {"start": v(200, 138.56) * mm, "end": v(190, 155.88) * mm, "construction": true});
            skLineSegment(sketch, "E9.9.4.7", {"start": v(190, 155.88) * mm, "end": v(210, 155.88) * mm, "construction": true});
            skLineSegment(sketch, "E9.9.4.8", {"start": v(210, 155.88) * mm, "end": v(200, 138.56) * mm, "construction": true});
            skLineSegment(sketch, "E9.9.5.0", {"start": v(190, 155.88) * mm, "end": v(210, 155.88) * mm, "construction": true});
            skLineSegment(sketch, "E9.9.5.1", {"start": v(200, 173.2) * mm, "end": v(190, 155.88) * mm, "construction": true});
            skLineSegment(sketch, "E9.9.5.2", {"start": v(210, 155.88) * mm, "end": v(200, 173.2) * mm, "construction": true});
            skLineSegment(sketch, "E9.9.5.3", {"start": v(180, 173.2) * mm, "end": v(200, 173.2) * mm, "construction": true});
            skLineSegment(sketch, "E9.9.5.4", {"start": v(190, 155.88) * mm, "end": v(180, 173.2) * mm, "construction": true});
            skLineSegment(sketch, "E9.9.5.5", {"start": v(190, 190.53) * mm, "end": v(180, 173.2) * mm, "construction": true});
            skLineSegment(sketch, "E9.9.5.6", {"start": v(200, 173.2) * mm, "end": v(190, 190.53) * mm, "construction": true});
            skLineSegment(sketch, "E9.9.5.7", {"start": v(190, 190.53) * mm, "end": v(210, 190.53) * mm, "construction": true});
            skLineSegment(sketch, "E9.9.5.8", {"start": v(210, 190.53) * mm, "end": v(200, 173.2) * mm, "construction": true});
            skLineSegment(sketch, "E9.9.6.0", {"start": v(190, 190.53) * mm, "end": v(210, 190.53) * mm, "construction": true});
            skLineSegment(sketch, "E9.9.6.1", {"start": v(200, 207.85) * mm, "end": v(190, 190.53) * mm, "construction": true});
            skLineSegment(sketch, "E9.9.6.2", {"start": v(210, 190.53) * mm, "end": v(200, 207.85) * mm, "construction": true});
            skLineSegment(sketch, "E9.9.6.3", {"start": v(180, 207.85) * mm, "end": v(200, 207.85) * mm, "construction": true});
            skLineSegment(sketch, "E9.9.6.4", {"start": v(190, 190.53) * mm, "end": v(180, 207.85) * mm, "construction": true});
            skLineSegment(sketch, "E9.9.6.5", {"start": v(190, 225.17) * mm, "end": v(180, 207.85) * mm, "construction": true});
            skLineSegment(sketch, "E9.9.6.6", {"start": v(200, 207.85) * mm, "end": v(190, 225.17) * mm, "construction": true});
            skLineSegment(sketch, "E9.9.6.7", {"start": v(190, 225.17) * mm, "end": v(210, 225.17) * mm});
            skLineSegment(sketch, "E9.9.6.8", {"start": v(210, 225.17) * mm, "end": v(200, 207.85) * mm, "construction": true});
            skLineSegment(sketch, "E9.10.0.0", {"start": v(210, -17.32) * mm, "end": v(230, -17.32) * mm});
            skLineSegment(sketch, "E9.10.0.1", {"start": v(220, 0) * mm, "end": v(210, -17.32) * mm, "construction": true});
            skLineSegment(sketch, "E9.10.0.2", {"start": v(230, -17.32) * mm, "end": v(220, 0) * mm, "construction": true});
            skLineSegment(sketch, "E9.10.0.3", {"start": v(200, 0) * mm, "end": v(220, 0) * mm, "construction": true});
            skLineSegment(sketch, "E9.10.0.4", {"start": v(210, -17.32) * mm, "end": v(200, 0) * mm, "construction": true});
            skLineSegment(sketch, "E9.10.0.5", {"start": v(210, 17.32) * mm, "end": v(200, 0) * mm, "construction": true});
            skLineSegment(sketch, "E9.10.0.6", {"start": v(220, 0) * mm, "end": v(210, 17.32) * mm, "construction": true});
            skLineSegment(sketch, "E9.10.0.7", {"start": v(210, 17.32) * mm, "end": v(230, 17.32) * mm, "construction": true});
            skLineSegment(sketch, "E9.10.0.8", {"start": v(230, 17.32) * mm, "end": v(220, 0) * mm, "construction": true});
            skLineSegment(sketch, "E9.10.1.0", {"start": v(210, 17.32) * mm, "end": v(230, 17.32) * mm, "construction": true});
            skLineSegment(sketch, "E9.10.1.1", {"start": v(220, 34.64) * mm, "end": v(210, 17.32) * mm, "construction": true});
            skLineSegment(sketch, "E9.10.1.2", {"start": v(230, 17.32) * mm, "end": v(220, 34.64) * mm, "construction": true});
            skLineSegment(sketch, "E9.10.1.3", {"start": v(200, 34.64) * mm, "end": v(220, 34.64) * mm, "construction": true});
            skLineSegment(sketch, "E9.10.1.4", {"start": v(210, 17.32) * mm, "end": v(200, 34.64) * mm, "construction": true});
            skLineSegment(sketch, "E9.10.1.5", {"start": v(210, 51.96) * mm, "end": v(200, 34.64) * mm, "construction": true});
            skLineSegment(sketch, "E9.10.1.6", {"start": v(220, 34.64) * mm, "end": v(210, 51.96) * mm, "construction": true});
            skLineSegment(sketch, "E9.10.1.7", {"start": v(210, 51.96) * mm, "end": v(230, 51.96) * mm, "construction": true});
            skLineSegment(sketch, "E9.10.1.8", {"start": v(230, 51.96) * mm, "end": v(220, 34.64) * mm, "construction": true});
            skLineSegment(sketch, "E9.10.2.0", {"start": v(210, 51.96) * mm, "end": v(230, 51.96) * mm, "construction": true});
            skLineSegment(sketch, "E9.10.2.1", {"start": v(220, 69.28) * mm, "end": v(210, 51.96) * mm, "construction": true});
            skLineSegment(sketch, "E9.10.2.2", {"start": v(230, 51.96) * mm, "end": v(220, 69.28) * mm, "construction": true});
            skLineSegment(sketch, "E9.10.2.3", {"start": v(200, 69.28) * mm, "end": v(220, 69.28) * mm, "construction": true});
            skLineSegment(sketch, "E9.10.2.4", {"start": v(210, 51.96) * mm, "end": v(200, 69.28) * mm, "construction": true});
            skLineSegment(sketch, "E9.10.2.5", {"start": v(210, 86.6) * mm, "end": v(200, 69.28) * mm, "construction": true});
            skLineSegment(sketch, "E9.10.2.6", {"start": v(220, 69.28) * mm, "end": v(210, 86.6) * mm, "construction": true});
            skLineSegment(sketch, "E9.10.2.7", {"start": v(210, 86.6) * mm, "end": v(230, 86.6) * mm, "construction": true});
            skLineSegment(sketch, "E9.10.2.8", {"start": v(230, 86.6) * mm, "end": v(220, 69.28) * mm, "construction": true});
            skLineSegment(sketch, "E9.10.3.0", {"start": v(210, 86.6) * mm, "end": v(230, 86.6) * mm, "construction": true});
            skLineSegment(sketch, "E9.10.3.1", {"start": v(220, 103.92) * mm, "end": v(210, 86.6) * mm, "construction": true});
            skLineSegment(sketch, "E9.10.3.2", {"start": v(230, 86.6) * mm, "end": v(220, 103.92) * mm, "construction": true});
            skLineSegment(sketch, "E9.10.3.3", {"start": v(200, 103.92) * mm, "end": v(220, 103.92) * mm, "construction": true});
            skLineSegment(sketch, "E9.10.3.4", {"start": v(210, 86.6) * mm, "end": v(200, 103.92) * mm, "construction": true});
            skLineSegment(sketch, "E9.10.3.5", {"start": v(210, 121.24) * mm, "end": v(200, 103.92) * mm, "construction": true});
            skLineSegment(sketch, "E9.10.3.6", {"start": v(220, 103.92) * mm, "end": v(210, 121.24) * mm, "construction": true});
            skLineSegment(sketch, "E9.10.3.7", {"start": v(210, 121.24) * mm, "end": v(230, 121.24) * mm, "construction": true});
            skLineSegment(sketch, "E9.10.3.8", {"start": v(230, 121.24) * mm, "end": v(220, 103.92) * mm, "construction": true});
            skLineSegment(sketch, "E9.10.4.0", {"start": v(210, 121.24) * mm, "end": v(230, 121.24) * mm, "construction": true});
            skLineSegment(sketch, "E9.10.4.1", {"start": v(220, 138.56) * mm, "end": v(210, 121.24) * mm, "construction": true});
            skLineSegment(sketch, "E9.10.4.2", {"start": v(230, 121.24) * mm, "end": v(220, 138.56) * mm, "construction": true});
            skLineSegment(sketch, "E9.10.4.3", {"start": v(200, 138.56) * mm, "end": v(220, 138.56) * mm, "construction": true});
            skLineSegment(sketch, "E9.10.4.4", {"start": v(210, 121.24) * mm, "end": v(200, 138.56) * mm, "construction": true});
            skLineSegment(sketch, "E9.10.4.5", {"start": v(210, 155.88) * mm, "end": v(200, 138.56) * mm, "construction": true});
            skLineSegment(sketch, "E9.10.4.6", {"start": v(220, 138.56) * mm, "end": v(210, 155.88) * mm, "construction": true});
            skLineSegment(sketch, "E9.10.4.7", {"start": v(210, 155.88) * mm, "end": v(230, 155.88) * mm, "construction": true});
            skLineSegment(sketch, "E9.10.4.8", {"start": v(230, 155.88) * mm, "end": v(220, 138.56) * mm, "construction": true});
            skLineSegment(sketch, "E9.10.5.0", {"start": v(210, 155.88) * mm, "end": v(230, 155.88) * mm, "construction": true});
            skLineSegment(sketch, "E9.10.5.1", {"start": v(220, 173.2) * mm, "end": v(210, 155.88) * mm, "construction": true});
            skLineSegment(sketch, "E9.10.5.2", {"start": v(230, 155.88) * mm, "end": v(220, 173.2) * mm, "construction": true});
            skLineSegment(sketch, "E9.10.5.3", {"start": v(200, 173.2) * mm, "end": v(220, 173.2) * mm, "construction": true});
            skLineSegment(sketch, "E9.10.5.4", {"start": v(210, 155.88) * mm, "end": v(200, 173.2) * mm, "construction": true});
            skLineSegment(sketch, "E9.10.5.5", {"start": v(210, 190.53) * mm, "end": v(200, 173.2) * mm, "construction": true});
            skLineSegment(sketch, "E9.10.5.6", {"start": v(220, 173.2) * mm, "end": v(210, 190.53) * mm, "construction": true});
            skLineSegment(sketch, "E9.10.5.7", {"start": v(210, 190.53) * mm, "end": v(230, 190.53) * mm, "construction": true});
            skLineSegment(sketch, "E9.10.5.8", {"start": v(230, 190.53) * mm, "end": v(220, 173.2) * mm, "construction": true});
            skLineSegment(sketch, "E9.10.6.0", {"start": v(210, 190.53) * mm, "end": v(230, 190.53) * mm, "construction": true});
            skLineSegment(sketch, "E9.10.6.1", {"start": v(220, 207.85) * mm, "end": v(210, 190.53) * mm, "construction": true});
            skLineSegment(sketch, "E9.10.6.2", {"start": v(230, 190.53) * mm, "end": v(220, 207.85) * mm, "construction": true});
            skLineSegment(sketch, "E9.10.6.3", {"start": v(200, 207.85) * mm, "end": v(220, 207.85) * mm, "construction": true});
            skLineSegment(sketch, "E9.10.6.4", {"start": v(210, 190.53) * mm, "end": v(200, 207.85) * mm, "construction": true});
            skLineSegment(sketch, "E9.10.6.5", {"start": v(210, 225.17) * mm, "end": v(200, 207.85) * mm, "construction": true});
            skLineSegment(sketch, "E9.10.6.6", {"start": v(220, 207.85) * mm, "end": v(210, 225.17) * mm, "construction": true});
            skLineSegment(sketch, "E9.10.6.7", {"start": v(210, 225.17) * mm, "end": v(230, 225.17) * mm});
            skLineSegment(sketch, "E9.10.6.8", {"start": v(230, 225.17) * mm, "end": v(220, 207.85) * mm, "construction": true});
            skLineSegment(sketch, "E9.11.0.0", {"start": v(230, -17.32) * mm, "end": v(250, -17.32) * mm});
            skLineSegment(sketch, "E9.11.0.1", {"start": v(240, 0) * mm, "end": v(230, -17.32) * mm, "construction": true});
            skLineSegment(sketch, "E9.11.0.2", {"start": v(250, -17.32) * mm, "end": v(240, 0) * mm, "construction": true});
            skLineSegment(sketch, "E9.11.0.3", {"start": v(220, 0) * mm, "end": v(240, 0) * mm, "construction": true});
            skLineSegment(sketch, "E9.11.0.4", {"start": v(230, -17.32) * mm, "end": v(220, 0) * mm, "construction": true});
            skLineSegment(sketch, "E9.11.0.5", {"start": v(230, 17.32) * mm, "end": v(220, 0) * mm, "construction": true});
            skLineSegment(sketch, "E9.11.0.6", {"start": v(240, 0) * mm, "end": v(230, 17.32) * mm, "construction": true});
            skLineSegment(sketch, "E9.11.0.7", {"start": v(230, 17.32) * mm, "end": v(250, 17.32) * mm, "construction": true});
            skLineSegment(sketch, "E9.11.0.8", {"start": v(250, 17.32) * mm, "end": v(240, 0) * mm, "construction": true});
            skLineSegment(sketch, "E9.11.1.0", {"start": v(230, 17.32) * mm, "end": v(250, 17.32) * mm, "construction": true});
            skLineSegment(sketch, "E9.11.1.1", {"start": v(240, 34.64) * mm, "end": v(230, 17.32) * mm, "construction": true});
            skLineSegment(sketch, "E9.11.1.2", {"start": v(250, 17.32) * mm, "end": v(240, 34.64) * mm, "construction": true});
            skLineSegment(sketch, "E9.11.1.3", {"start": v(220, 34.64) * mm, "end": v(240, 34.64) * mm, "construction": true});
            skLineSegment(sketch, "E9.11.1.4", {"start": v(230, 17.32) * mm, "end": v(220, 34.64) * mm, "construction": true});
            skLineSegment(sketch, "E9.11.1.5", {"start": v(230, 51.96) * mm, "end": v(220, 34.64) * mm, "construction": true});
            skLineSegment(sketch, "E9.11.1.6", {"start": v(240, 34.64) * mm, "end": v(230, 51.96) * mm, "construction": true});
            skLineSegment(sketch, "E9.11.1.7", {"start": v(230, 51.96) * mm, "end": v(250, 51.96) * mm, "construction": true});
            skLineSegment(sketch, "E9.11.1.8", {"start": v(250, 51.96) * mm, "end": v(240, 34.64) * mm, "construction": true});
            skLineSegment(sketch, "E9.11.2.0", {"start": v(230, 51.96) * mm, "end": v(250, 51.96) * mm, "construction": true});
            skLineSegment(sketch, "E9.11.2.1", {"start": v(240, 69.28) * mm, "end": v(230, 51.96) * mm, "construction": true});
            skLineSegment(sketch, "E9.11.2.2", {"start": v(250, 51.96) * mm, "end": v(240, 69.28) * mm, "construction": true});
            skLineSegment(sketch, "E9.11.2.3", {"start": v(220, 69.28) * mm, "end": v(240, 69.28) * mm, "construction": true});
            skLineSegment(sketch, "E9.11.2.4", {"start": v(230, 51.96) * mm, "end": v(220, 69.28) * mm, "construction": true});
            skLineSegment(sketch, "E9.11.2.5", {"start": v(230, 86.6) * mm, "end": v(220, 69.28) * mm, "construction": true});
            skLineSegment(sketch, "E9.11.2.6", {"start": v(240, 69.28) * mm, "end": v(230, 86.6) * mm, "construction": true});
            skLineSegment(sketch, "E9.11.2.7", {"start": v(230, 86.6) * mm, "end": v(250, 86.6) * mm, "construction": true});
            skLineSegment(sketch, "E9.11.2.8", {"start": v(250, 86.6) * mm, "end": v(240, 69.28) * mm, "construction": true});
            skLineSegment(sketch, "E9.11.3.0", {"start": v(230, 86.6) * mm, "end": v(250, 86.6) * mm, "construction": true});
            skLineSegment(sketch, "E9.11.3.1", {"start": v(240, 103.92) * mm, "end": v(230, 86.6) * mm, "construction": true});
            skLineSegment(sketch, "E9.11.3.2", {"start": v(250, 86.6) * mm, "end": v(240, 103.92) * mm, "construction": true});
            skLineSegment(sketch, "E9.11.3.3", {"start": v(220, 103.92) * mm, "end": v(240, 103.92) * mm, "construction": true});
            skLineSegment(sketch, "E9.11.3.4", {"start": v(230, 86.6) * mm, "end": v(220, 103.92) * mm, "construction": true});
            skLineSegment(sketch, "E9.11.3.5", {"start": v(230, 121.24) * mm, "end": v(220, 103.92) * mm, "construction": true});
            skLineSegment(sketch, "E9.11.3.6", {"start": v(240, 103.92) * mm, "end": v(230, 121.24) * mm, "construction": true});
            skLineSegment(sketch, "E9.11.3.7", {"start": v(230, 121.24) * mm, "end": v(250, 121.24) * mm, "construction": true});
            skLineSegment(sketch, "E9.11.3.8", {"start": v(250, 121.24) * mm, "end": v(240, 103.92) * mm, "construction": true});
            skLineSegment(sketch, "E9.11.4.0", {"start": v(230, 121.24) * mm, "end": v(250, 121.24) * mm, "construction": true});
            skLineSegment(sketch, "E9.11.4.1", {"start": v(240, 138.56) * mm, "end": v(230, 121.24) * mm, "construction": true});
            skLineSegment(sketch, "E9.11.4.2", {"start": v(250, 121.24) * mm, "end": v(240, 138.56) * mm, "construction": true});
            skLineSegment(sketch, "E9.11.4.3", {"start": v(220, 138.56) * mm, "end": v(240, 138.56) * mm, "construction": true});
            skLineSegment(sketch, "E9.11.4.4", {"start": v(230, 121.24) * mm, "end": v(220, 138.56) * mm, "construction": true});
            skLineSegment(sketch, "E9.11.4.5", {"start": v(230, 155.88) * mm, "end": v(220, 138.56) * mm, "construction": true});
            skLineSegment(sketch, "E9.11.4.6", {"start": v(240, 138.56) * mm, "end": v(230, 155.88) * mm, "construction": true});
            skLineSegment(sketch, "E9.11.4.7", {"start": v(230, 155.88) * mm, "end": v(250, 155.88) * mm, "construction": true});
            skLineSegment(sketch, "E9.11.4.8", {"start": v(250, 155.88) * mm, "end": v(240, 138.56) * mm, "construction": true});
            skLineSegment(sketch, "E9.11.5.0", {"start": v(230, 155.88) * mm, "end": v(250, 155.88) * mm, "construction": true});
            skLineSegment(sketch, "E9.11.5.1", {"start": v(240, 173.2) * mm, "end": v(230, 155.88) * mm, "construction": true});
            skLineSegment(sketch, "E9.11.5.2", {"start": v(250, 155.88) * mm, "end": v(240, 173.2) * mm, "construction": true});
            skLineSegment(sketch, "E9.11.5.3", {"start": v(220, 173.2) * mm, "end": v(240, 173.2) * mm, "construction": true});
            skLineSegment(sketch, "E9.11.5.4", {"start": v(230, 155.88) * mm, "end": v(220, 173.2) * mm, "construction": true});
            skLineSegment(sketch, "E9.11.5.5", {"start": v(230, 190.53) * mm, "end": v(220, 173.2) * mm, "construction": true});
            skLineSegment(sketch, "E9.11.5.6", {"start": v(240, 173.2) * mm, "end": v(230, 190.53) * mm, "construction": true});
            skLineSegment(sketch, "E9.11.5.7", {"start": v(230, 190.53) * mm, "end": v(250, 190.53) * mm, "construction": true});
            skLineSegment(sketch, "E9.11.5.8", {"start": v(250, 190.53) * mm, "end": v(240, 173.2) * mm, "construction": true});
            skLineSegment(sketch, "E9.11.6.0", {"start": v(230, 190.53) * mm, "end": v(250, 190.53) * mm, "construction": true});
            skLineSegment(sketch, "E9.11.6.1", {"start": v(240, 207.85) * mm, "end": v(230, 190.53) * mm, "construction": true});
            skLineSegment(sketch, "E9.11.6.2", {"start": v(250, 190.53) * mm, "end": v(240, 207.85) * mm, "construction": true});
            skLineSegment(sketch, "E9.11.6.3", {"start": v(220, 207.85) * mm, "end": v(240, 207.85) * mm, "construction": true});
            skLineSegment(sketch, "E9.11.6.4", {"start": v(230, 190.53) * mm, "end": v(220, 207.85) * mm, "construction": true});
            skLineSegment(sketch, "E9.11.6.5", {"start": v(230, 225.17) * mm, "end": v(220, 207.85) * mm, "construction": true});
            skLineSegment(sketch, "E9.11.6.6", {"start": v(240, 207.85) * mm, "end": v(230, 225.17) * mm, "construction": true});
            skLineSegment(sketch, "E9.11.6.7", {"start": v(230, 225.17) * mm, "end": v(250, 225.17) * mm});
            skLineSegment(sketch, "E9.11.6.8", {"start": v(250, 225.17) * mm, "end": v(240, 207.85) * mm, "construction": true});
            skLineSegment(sketch, "E9.12.0.0", {"start": v(250, -17.32) * mm, "end": v(270, -17.32) * mm});
            skLineSegment(sketch, "E9.12.0.1", {"start": v(260, 0) * mm, "end": v(250, -17.32) * mm, "construction": true});
            skLineSegment(sketch, "E9.12.0.2", {"start": v(270, -17.32) * mm, "end": v(260, 0) * mm, "construction": true});
            skLineSegment(sketch, "E9.12.0.3", {"start": v(240, 0) * mm, "end": v(260, 0) * mm, "construction": true});
            skLineSegment(sketch, "E9.12.0.4", {"start": v(250, -17.32) * mm, "end": v(240, 0) * mm, "construction": true});
            skLineSegment(sketch, "E9.12.0.5", {"start": v(250, 17.32) * mm, "end": v(240, 0) * mm, "construction": true});
            skLineSegment(sketch, "E9.12.0.6", {"start": v(260, 0) * mm, "end": v(250, 17.32) * mm, "construction": true});
            skLineSegment(sketch, "E9.12.0.7", {"start": v(250, 17.32) * mm, "end": v(270, 17.32) * mm, "construction": true});
            skLineSegment(sketch, "E9.12.0.8", {"start": v(270, 17.32) * mm, "end": v(260, 0) * mm, "construction": true});
            skLineSegment(sketch, "E9.12.1.0", {"start": v(250, 17.32) * mm, "end": v(270, 17.32) * mm, "construction": true});
            skLineSegment(sketch, "E9.12.1.1", {"start": v(260, 34.64) * mm, "end": v(250, 17.32) * mm, "construction": true});
            skLineSegment(sketch, "E9.12.1.2", {"start": v(270, 17.32) * mm, "end": v(260, 34.64) * mm, "construction": true});
            skLineSegment(sketch, "E9.12.1.3", {"start": v(240, 34.64) * mm, "end": v(260, 34.64) * mm, "construction": true});
            skLineSegment(sketch, "E9.12.1.4", {"start": v(250, 17.32) * mm, "end": v(240, 34.64) * mm, "construction": true});
            skLineSegment(sketch, "E9.12.1.5", {"start": v(250, 51.96) * mm, "end": v(240, 34.64) * mm, "construction": true});
            skLineSegment(sketch, "E9.12.1.6", {"start": v(260, 34.64) * mm, "end": v(250, 51.96) * mm, "construction": true});
            skLineSegment(sketch, "E9.12.1.7", {"start": v(250, 51.96) * mm, "end": v(270, 51.96) * mm, "construction": true});
            skLineSegment(sketch, "E9.12.1.8", {"start": v(270, 51.96) * mm, "end": v(260, 34.64) * mm, "construction": true});
            skLineSegment(sketch, "E9.12.2.0", {"start": v(250, 51.96) * mm, "end": v(270, 51.96) * mm, "construction": true});
            skLineSegment(sketch, "E9.12.2.1", {"start": v(260, 69.28) * mm, "end": v(250, 51.96) * mm, "construction": true});
            skLineSegment(sketch, "E9.12.2.2", {"start": v(270, 51.96) * mm, "end": v(260, 69.28) * mm, "construction": true});
            skLineSegment(sketch, "E9.12.2.3", {"start": v(240, 69.28) * mm, "end": v(260, 69.28) * mm, "construction": true});
            skLineSegment(sketch, "E9.12.2.4", {"start": v(250, 51.96) * mm, "end": v(240, 69.28) * mm, "construction": true});
            skLineSegment(sketch, "E9.12.2.5", {"start": v(250, 86.6) * mm, "end": v(240, 69.28) * mm, "construction": true});
            skLineSegment(sketch, "E9.12.2.6", {"start": v(260, 69.28) * mm, "end": v(250, 86.6) * mm, "construction": true});
            skLineSegment(sketch, "E9.12.2.7", {"start": v(250, 86.6) * mm, "end": v(270, 86.6) * mm, "construction": true});
            skLineSegment(sketch, "E9.12.2.8", {"start": v(270, 86.6) * mm, "end": v(260, 69.28) * mm, "construction": true});
            skLineSegment(sketch, "E9.12.3.0", {"start": v(250, 86.6) * mm, "end": v(270, 86.6) * mm, "construction": true});
            skLineSegment(sketch, "E9.12.3.1", {"start": v(260, 103.92) * mm, "end": v(250, 86.6) * mm, "construction": true});
            skLineSegment(sketch, "E9.12.3.2", {"start": v(270, 86.6) * mm, "end": v(260, 103.92) * mm, "construction": true});
            skLineSegment(sketch, "E9.12.3.3", {"start": v(240, 103.92) * mm, "end": v(260, 103.92) * mm, "construction": true});
            skLineSegment(sketch, "E9.12.3.4", {"start": v(250, 86.6) * mm, "end": v(240, 103.92) * mm, "construction": true});
            skLineSegment(sketch, "E9.12.3.5", {"start": v(250, 121.24) * mm, "end": v(240, 103.92) * mm, "construction": true});
            skLineSegment(sketch, "E9.12.3.6", {"start": v(260, 103.92) * mm, "end": v(250, 121.24) * mm, "construction": true});
            skLineSegment(sketch, "E9.12.3.7", {"start": v(250, 121.24) * mm, "end": v(270, 121.24) * mm, "construction": true});
            skLineSegment(sketch, "E9.12.3.8", {"start": v(270, 121.24) * mm, "end": v(260, 103.92) * mm, "construction": true});
            skLineSegment(sketch, "E9.12.4.0", {"start": v(250, 121.24) * mm, "end": v(270, 121.24) * mm, "construction": true});
            skLineSegment(sketch, "E9.12.4.1", {"start": v(260, 138.56) * mm, "end": v(250, 121.24) * mm, "construction": true});
            skLineSegment(sketch, "E9.12.4.2", {"start": v(270, 121.24) * mm, "end": v(260, 138.56) * mm, "construction": true});
            skLineSegment(sketch, "E9.12.4.3", {"start": v(240, 138.56) * mm, "end": v(260, 138.56) * mm, "construction": true});
            skLineSegment(sketch, "E9.12.4.4", {"start": v(250, 121.24) * mm, "end": v(240, 138.56) * mm, "construction": true});
            skLineSegment(sketch, "E9.12.4.5", {"start": v(250, 155.88) * mm, "end": v(240, 138.56) * mm, "construction": true});
            skLineSegment(sketch, "E9.12.4.6", {"start": v(260, 138.56) * mm, "end": v(250, 155.88) * mm, "construction": true});
            skLineSegment(sketch, "E9.12.4.7", {"start": v(250, 155.88) * mm, "end": v(270, 155.88) * mm, "construction": true});
            skLineSegment(sketch, "E9.12.4.8", {"start": v(270, 155.88) * mm, "end": v(260, 138.56) * mm, "construction": true});
            skLineSegment(sketch, "E9.12.5.0", {"start": v(250, 155.88) * mm, "end": v(270, 155.88) * mm, "construction": true});
            skLineSegment(sketch, "E9.12.5.1", {"start": v(260, 173.2) * mm, "end": v(250, 155.88) * mm, "construction": true});
            skLineSegment(sketch, "E9.12.5.2", {"start": v(270, 155.88) * mm, "end": v(260, 173.2) * mm, "construction": true});
            skLineSegment(sketch, "E9.12.5.3", {"start": v(240, 173.2) * mm, "end": v(260, 173.2) * mm, "construction": true});
            skLineSegment(sketch, "E9.12.5.4", {"start": v(250, 155.88) * mm, "end": v(240, 173.2) * mm, "construction": true});
            skLineSegment(sketch, "E9.12.5.5", {"start": v(250, 190.53) * mm, "end": v(240, 173.2) * mm, "construction": true});
            skLineSegment(sketch, "E9.12.5.6", {"start": v(260, 173.2) * mm, "end": v(250, 190.53) * mm, "construction": true});
            skLineSegment(sketch, "E9.12.5.7", {"start": v(250, 190.53) * mm, "end": v(270, 190.53) * mm, "construction": true});
            skLineSegment(sketch, "E9.12.5.8", {"start": v(270, 190.53) * mm, "end": v(260, 173.2) * mm, "construction": true});
            skLineSegment(sketch, "E9.12.6.0", {"start": v(250, 190.53) * mm, "end": v(270, 190.53) * mm, "construction": true});
            skLineSegment(sketch, "E9.12.6.1", {"start": v(260, 207.85) * mm, "end": v(250, 190.53) * mm, "construction": true});
            skLineSegment(sketch, "E9.12.6.2", {"start": v(270, 190.53) * mm, "end": v(260, 207.85) * mm, "construction": true});
            skLineSegment(sketch, "E9.12.6.3", {"start": v(240, 207.85) * mm, "end": v(260, 207.85) * mm, "construction": true});
            skLineSegment(sketch, "E9.12.6.4", {"start": v(250, 190.53) * mm, "end": v(240, 207.85) * mm, "construction": true});
            skLineSegment(sketch, "E9.12.6.5", {"start": v(250, 225.17) * mm, "end": v(240, 207.85) * mm, "construction": true});
            skLineSegment(sketch, "E9.12.6.6", {"start": v(260, 207.85) * mm, "end": v(250, 225.17) * mm, "construction": true});
            skLineSegment(sketch, "E9.12.6.7", {"start": v(250, 225.17) * mm, "end": v(270, 225.17) * mm});
            skLineSegment(sketch, "E9.12.6.8", {"start": v(270, 225.17) * mm, "end": v(260, 207.85) * mm, "construction": true});
            skLineSegment(sketch, "E9.13.0.0", {"start": v(270, -17.32) * mm, "end": v(290, -17.32) * mm});
            skLineSegment(sketch, "E9.13.0.1", {"start": v(280, 0) * mm, "end": v(270, -17.32) * mm, "construction": true});
            skLineSegment(sketch, "E9.13.0.2", {"start": v(290, -17.32) * mm, "end": v(280, 0) * mm});
            skLineSegment(sketch, "E9.13.0.3", {"start": v(260, 0) * mm, "end": v(280, 0) * mm, "construction": true});
            skLineSegment(sketch, "E9.13.0.4", {"start": v(270, -17.32) * mm, "end": v(260, 0) * mm, "construction": true});
            skLineSegment(sketch, "E9.13.0.5", {"start": v(270, 17.32) * mm, "end": v(260, 0) * mm, "construction": true});
            skLineSegment(sketch, "E9.13.0.6", {"start": v(280, 0) * mm, "end": v(270, 17.32) * mm, "construction": true});
            skLineSegment(sketch, "E9.13.0.7", {"start": v(270, 17.32) * mm, "end": v(290, 17.32) * mm, "construction": true});
            skLineSegment(sketch, "E9.13.0.8", {"start": v(290, 17.32) * mm, "end": v(280, 0) * mm});
            skLineSegment(sketch, "E9.13.1.0", {"start": v(270, 17.32) * mm, "end": v(290, 17.32) * mm, "construction": true});
            skLineSegment(sketch, "E9.13.1.1", {"start": v(280, 34.64) * mm, "end": v(270, 17.32) * mm, "construction": true});
            skLineSegment(sketch, "E9.13.1.2", {"start": v(290, 17.32) * mm, "end": v(280, 34.64) * mm});
            skLineSegment(sketch, "E9.13.1.3", {"start": v(260, 34.64) * mm, "end": v(280, 34.64) * mm, "construction": true});
            skLineSegment(sketch, "E9.13.1.4", {"start": v(270, 17.32) * mm, "end": v(260, 34.64) * mm, "construction": true});
            skLineSegment(sketch, "E9.13.1.5", {"start": v(270, 51.96) * mm, "end": v(260, 34.64) * mm, "construction": true});
            skLineSegment(sketch, "E9.13.1.6", {"start": v(280, 34.64) * mm, "end": v(270, 51.96) * mm, "construction": true});
            skLineSegment(sketch, "E9.13.1.7", {"start": v(270, 51.96) * mm, "end": v(290, 51.96) * mm, "construction": true});
            skLineSegment(sketch, "E9.13.1.8", {"start": v(290, 51.96) * mm, "end": v(280, 34.64) * mm});
            skLineSegment(sketch, "E9.13.2.0", {"start": v(270, 51.96) * mm, "end": v(290, 51.96) * mm, "construction": true});
            skLineSegment(sketch, "E9.13.2.1", {"start": v(280, 69.28) * mm, "end": v(270, 51.96) * mm, "construction": true});
            skLineSegment(sketch, "E9.13.2.2", {"start": v(290, 51.96) * mm, "end": v(280, 69.28) * mm});
            skLineSegment(sketch, "E9.13.2.3", {"start": v(260, 69.28) * mm, "end": v(280, 69.28) * mm, "construction": true});
            skLineSegment(sketch, "E9.13.2.4", {"start": v(270, 51.96) * mm, "end": v(260, 69.28) * mm, "construction": true});
            skLineSegment(sketch, "E9.13.2.5", {"start": v(270, 86.6) * mm, "end": v(260, 69.28) * mm, "construction": true});
            skLineSegment(sketch, "E9.13.2.6", {"start": v(280, 69.28) * mm, "end": v(270, 86.6) * mm, "construction": true});
            skLineSegment(sketch, "E9.13.2.7", {"start": v(270, 86.6) * mm, "end": v(290, 86.6) * mm, "construction": true});
            skLineSegment(sketch, "E9.13.2.8", {"start": v(290, 86.6) * mm, "end": v(280, 69.28) * mm});
            skLineSegment(sketch, "E9.13.3.0", {"start": v(270, 86.6) * mm, "end": v(290, 86.6) * mm, "construction": true});
            skLineSegment(sketch, "E9.13.3.1", {"start": v(280, 103.92) * mm, "end": v(270, 86.6) * mm, "construction": true});
            skLineSegment(sketch, "E9.13.3.2", {"start": v(290, 86.6) * mm, "end": v(280, 103.92) * mm});
            skLineSegment(sketch, "E9.13.3.3", {"start": v(260, 103.92) * mm, "end": v(280, 103.92) * mm, "construction": true});
            skLineSegment(sketch, "E9.13.3.4", {"start": v(270, 86.6) * mm, "end": v(260, 103.92) * mm, "construction": true});
            skLineSegment(sketch, "E9.13.3.5", {"start": v(270, 121.24) * mm, "end": v(260, 103.92) * mm, "construction": true});
            skLineSegment(sketch, "E9.13.3.6", {"start": v(280, 103.92) * mm, "end": v(270, 121.24) * mm, "construction": true});
            skLineSegment(sketch, "E9.13.3.7", {"start": v(270, 121.24) * mm, "end": v(290, 121.24) * mm, "construction": true});
            skLineSegment(sketch, "E9.13.3.8", {"start": v(290, 121.24) * mm, "end": v(280, 103.92) * mm});
            skLineSegment(sketch, "E9.13.4.0", {"start": v(270, 121.24) * mm, "end": v(290, 121.24) * mm, "construction": true});
            skLineSegment(sketch, "E9.13.4.1", {"start": v(280, 138.56) * mm, "end": v(270, 121.24) * mm, "construction": true});
            skLineSegment(sketch, "E9.13.4.2", {"start": v(290, 121.24) * mm, "end": v(280, 138.56) * mm});
            skLineSegment(sketch, "E9.13.4.3", {"start": v(260, 138.56) * mm, "end": v(280, 138.56) * mm, "construction": true});
            skLineSegment(sketch, "E9.13.4.4", {"start": v(270, 121.24) * mm, "end": v(260, 138.56) * mm, "construction": true});
            skLineSegment(sketch, "E9.13.4.5", {"start": v(270, 155.88) * mm, "end": v(260, 138.56) * mm, "construction": true});
            skLineSegment(sketch, "E9.13.4.6", {"start": v(280, 138.56) * mm, "end": v(270, 155.88) * mm, "construction": true});
            skLineSegment(sketch, "E9.13.4.7", {"start": v(270, 155.88) * mm, "end": v(290, 155.88) * mm, "construction": true});
            skLineSegment(sketch, "E9.13.4.8", {"start": v(290, 155.88) * mm, "end": v(280, 138.56) * mm});
            skLineSegment(sketch, "E9.13.5.0", {"start": v(270, 155.88) * mm, "end": v(290, 155.88) * mm, "construction": true});
            skLineSegment(sketch, "E9.13.5.1", {"start": v(280, 173.2) * mm, "end": v(270, 155.88) * mm, "construction": true});
            skLineSegment(sketch, "E9.13.5.2", {"start": v(290, 155.88) * mm, "end": v(280, 173.2) * mm});
            skLineSegment(sketch, "E9.13.5.3", {"start": v(260, 173.2) * mm, "end": v(280, 173.2) * mm, "construction": true});
            skLineSegment(sketch, "E9.13.5.4", {"start": v(270, 155.88) * mm, "end": v(260, 173.2) * mm, "construction": true});
            skLineSegment(sketch, "E9.13.5.5", {"start": v(270, 190.53) * mm, "end": v(260, 173.2) * mm, "construction": true});
            skLineSegment(sketch, "E9.13.5.6", {"start": v(280, 173.2) * mm, "end": v(270, 190.53) * mm, "construction": true});
            skLineSegment(sketch, "E9.13.5.7", {"start": v(270, 190.53) * mm, "end": v(290, 190.53) * mm, "construction": true});
            skLineSegment(sketch, "E9.13.5.8", {"start": v(290, 190.53) * mm, "end": v(280, 173.2) * mm});
            skLineSegment(sketch, "E9.13.6.0", {"start": v(270, 190.53) * mm, "end": v(290, 190.53) * mm, "construction": true});
            skLineSegment(sketch, "E9.13.6.1", {"start": v(280, 207.85) * mm, "end": v(270, 190.53) * mm, "construction": true});
            skLineSegment(sketch, "E9.13.6.2", {"start": v(290, 190.53) * mm, "end": v(280, 207.85) * mm});
            skLineSegment(sketch, "E9.13.6.3", {"start": v(260, 207.85) * mm, "end": v(280, 207.85) * mm, "construction": true});
            skLineSegment(sketch, "E9.13.6.4", {"start": v(270, 190.53) * mm, "end": v(260, 207.85) * mm, "construction": true});
            skLineSegment(sketch, "E9.13.6.5", {"start": v(270, 225.17) * mm, "end": v(260, 207.85) * mm, "construction": true});
            skLineSegment(sketch, "E9.13.6.6", {"start": v(280, 207.85) * mm, "end": v(270, 225.17) * mm, "construction": true});
            skLineSegment(sketch, "E9.13.6.7", {"start": v(270, 225.17) * mm, "end": v(290, 225.17) * mm});
            skLineSegment(sketch, "E9.13.6.8", {"start": v(290, 225.17) * mm, "end": v(280, 207.85) * mm});
            skLineSegment(sketch, "E9.direction1", {"start": v(10, -17.32) * mm, "end": v(30, -17.32) * mm, "construction": true});
            skLineSegment(sketch, "E9.direction2", {"start": v(10, -17.32) * mm, "end": v(10, 17.32) * mm, "construction": true});
            skLineSegment(sketch, "E10.bottom", {"start": v(-70, -44.58) * mm, "end": v(350, -44.58) * mm});
            skLineSegment(sketch, "E10.top", {"start": v(-70, 252.42) * mm, "end": v(350, 252.42) * mm});
            skLineSegment(sketch, "E10.left", {"start": v(-70, -44.58) * mm, "end": v(-70, 252.42) * mm});
            skLineSegment(sketch, "E10.right", {"start": v(350, -44.58) * mm, "end": v(350, 252.42) * mm});
            skPoint(sketch, "E10.middle", {"position": v(140, 103.92) * mm});
            skLineSegment(sketch, "E11", {"start": v(0.43, -0.25) * mm, "end": v(19.57, -0.25) * mm});
            skLineSegment(sketch, "E12", {"start": v(19.57, -0.25) * mm, "end": v(10, -16.82) * mm});
            skLineSegment(sketch, "E13", {"start": v(10, -16.82) * mm, "end": v(0.43, -0.25) * mm});
            skLineSegment(sketch, "E14.MirrorCS", {"start": v(0.43, 0.25) * mm, "end": v(19.57, 0.25) * mm});
            skLineSegment(sketch, "E15.MirrorCS", {"start": v(10, 16.82) * mm, "end": v(0.43, 0.25) * mm});
            skLineSegment(sketch, "E16.MirrorCS", {"start": v(19.57, 0.25) * mm, "end": v(10, 16.82) * mm});
            skLineSegment(sketch, "E17.MirrorCS", {"start": v(20, -0.5) * mm, "end": v(10.43, -17.07) * mm});
            skLineSegment(sketch, "E18.MirrorCS", {"start": v(29.57, -17.07) * mm, "end": v(20, -0.5) * mm});
            skLineSegment(sketch, "E19.MirrorCS", {"start": v(10.43, -17.07) * mm, "end": v(29.57, -17.07) * mm});
            skLineSegment(sketch, "E20.MirrorCS", {"start": v(20, 0.5) * mm, "end": v(10.43, 17.07) * mm});
            skLineSegment(sketch, "E21.MirrorCS", {"start": v(10.43, 17.07) * mm, "end": v(29.57, 17.07) * mm});
            skLineSegment(sketch, "E22.MirrorCS", {"start": v(29.57, 17.07) * mm, "end": v(20, 0.5) * mm});
            skLineSegment(sketch, "E23.0.1.0", {"start": v(10.43, 17.57) * mm, "end": v(29.57, 17.57) * mm});
            skLineSegment(sketch, "E23.0.1.1", {"start": v(20, 34.14) * mm, "end": v(10.43, 17.57) * mm});
            skLineSegment(sketch, "E23.0.1.2", {"start": v(29.57, 17.57) * mm, "end": v(20, 34.14) * mm});
            skLineSegment(sketch, "E23.0.1.3", {"start": v(0.43, 34.4) * mm, "end": v(19.57, 34.4) * mm});
            skLineSegment(sketch, "E23.0.1.4", {"start": v(19.57, 34.4) * mm, "end": v(10, 17.82) * mm});
            skLineSegment(sketch, "E23.0.1.5", {"start": v(10, 17.82) * mm, "end": v(0.43, 34.4) * mm});
            skLineSegment(sketch, "E23.0.1.6", {"start": v(10, 51.46) * mm, "end": v(0.43, 34.9) * mm});
            skLineSegment(sketch, "E23.0.1.7", {"start": v(0.43, 34.9) * mm, "end": v(19.57, 34.9) * mm});
            skLineSegment(sketch, "E23.0.1.8", {"start": v(19.57, 34.9) * mm, "end": v(10, 51.46) * mm});
            skLineSegment(sketch, "E23.0.1.9", {"start": v(20, 35.14) * mm, "end": v(10.43, 51.71) * mm});
            skLineSegment(sketch, "E23.0.1.10", {"start": v(29.57, 51.71) * mm, "end": v(20, 35.14) * mm});
            skLineSegment(sketch, "E23.0.1.11", {"start": v(10.43, 51.71) * mm, "end": v(29.57, 51.71) * mm});
            skLineSegment(sketch, "E23.0.2.0", {"start": v(10.43, 52.21) * mm, "end": v(29.57, 52.21) * mm});
            skLineSegment(sketch, "E23.0.2.1", {"start": v(20, 68.78) * mm, "end": v(10.43, 52.21) * mm});
            skLineSegment(sketch, "E23.0.2.2", {"start": v(29.57, 52.21) * mm, "end": v(20, 68.78) * mm});
            skLineSegment(sketch, "E23.0.2.3", {"start": v(0.43, 69.03) * mm, "end": v(19.57, 69.03) * mm});
            skLineSegment(sketch, "E23.0.2.4", {"start": v(19.57, 69.03) * mm, "end": v(10, 52.46) * mm});
            skLineSegment(sketch, "E23.0.2.5", {"start": v(10, 52.46) * mm, "end": v(0.43, 69.03) * mm});
            skLineSegment(sketch, "E23.0.2.6", {"start": v(10, 86.1) * mm, "end": v(0.43, 69.53) * mm});
            skLineSegment(sketch, "E23.0.2.7", {"start": v(0.43, 69.53) * mm, "end": v(19.57, 69.53) * mm});
            skLineSegment(sketch, "E23.0.2.8", {"start": v(19.57, 69.53) * mm, "end": v(10, 86.1) * mm});
            skLineSegment(sketch, "E23.0.2.9", {"start": v(20, 69.78) * mm, "end": v(10.43, 86.35) * mm});
            skLineSegment(sketch, "E23.0.2.10", {"start": v(29.57, 86.35) * mm, "end": v(20, 69.78) * mm});
            skLineSegment(sketch, "E23.0.2.11", {"start": v(10.43, 86.35) * mm, "end": v(29.57, 86.35) * mm});
            skLineSegment(sketch, "E23.0.3.0", {"start": v(10.43, 86.85) * mm, "end": v(29.57, 86.85) * mm});
            skLineSegment(sketch, "E23.0.3.1", {"start": v(20, 103.42) * mm, "end": v(10.43, 86.85) * mm});
            skLineSegment(sketch, "E23.0.3.2", {"start": v(29.57, 86.85) * mm, "end": v(20, 103.42) * mm});
            skLineSegment(sketch, "E23.0.3.3", {"start": v(0.43, 103.67) * mm, "end": v(19.57, 103.67) * mm});
            skLineSegment(sketch, "E23.0.3.4", {"start": v(19.57, 103.67) * mm, "end": v(10, 87.1) * mm});
            skLineSegment(sketch, "E23.0.3.5", {"start": v(10, 87.1) * mm, "end": v(0.43, 103.67) * mm});
            skLineSegment(sketch, "E23.0.3.6", {"start": v(10, 120.74) * mm, "end": v(0.43, 104.17) * mm});
            skLineSegment(sketch, "E23.0.3.7", {"start": v(0.43, 104.17) * mm, "end": v(19.57, 104.17) * mm});
            skLineSegment(sketch, "E23.0.3.8", {"start": v(19.57, 104.17) * mm, "end": v(10, 120.74) * mm});
            skLineSegment(sketch, "E23.0.3.9", {"start": v(20, 104.42) * mm, "end": v(10.43, 121) * mm});
            skLineSegment(sketch, "E23.0.3.10", {"start": v(29.57, 121) * mm, "end": v(20, 104.42) * mm});
            skLineSegment(sketch, "E23.0.3.11", {"start": v(10.43, 121) * mm, "end": v(29.57, 121) * mm});
            skLineSegment(sketch, "E23.0.4.0", {"start": v(10.43, 121.5) * mm, "end": v(29.57, 121.5) * mm});
            skLineSegment(sketch, "E23.0.4.1", {"start": v(20, 138.06) * mm, "end": v(10.43, 121.5) * mm});
            skLineSegment(sketch, "E23.0.4.2", {"start": v(29.57, 121.5) * mm, "end": v(20, 138.06) * mm});
            skLineSegment(sketch, "E23.0.4.3", {"start": v(0.43, 138.31) * mm, "end": v(19.57, 138.31) * mm});
            skLineSegment(sketch, "E23.0.4.4", {"start": v(19.57, 138.31) * mm, "end": v(10, 121.74) * mm});
            skLineSegment(sketch, "E23.0.4.5", {"start": v(10, 121.74) * mm, "end": v(0.43, 138.31) * mm});
            skLineSegment(sketch, "E23.0.4.6", {"start": v(10, 155.38) * mm, "end": v(0.43, 138.81) * mm});
            skLineSegment(sketch, "E23.0.4.7", {"start": v(0.43, 138.81) * mm, "end": v(19.57, 138.81) * mm});
            skLineSegment(sketch, "E23.0.4.8", {"start": v(19.57, 138.81) * mm, "end": v(10, 155.38) * mm});
            skLineSegment(sketch, "E23.0.4.9", {"start": v(20, 139.06) * mm, "end": v(10.43, 155.63) * mm});
            skLineSegment(sketch, "E23.0.4.10", {"start": v(29.57, 155.63) * mm, "end": v(20, 139.06) * mm});
            skLineSegment(sketch, "E23.0.4.11", {"start": v(10.43, 155.63) * mm, "end": v(29.57, 155.63) * mm});
            skLineSegment(sketch, "E23.0.5.0", {"start": v(10.43, 156.13) * mm, "end": v(29.57, 156.13) * mm});
            skLineSegment(sketch, "E23.0.5.1", {"start": v(20, 172.7) * mm, "end": v(10.43, 156.13) * mm});
            skLineSegment(sketch, "E23.0.5.2", {"start": v(29.57, 156.13) * mm, "end": v(20, 172.7) * mm});
            skLineSegment(sketch, "E23.0.5.3", {"start": v(0.43, 172.96) * mm, "end": v(19.57, 172.96) * mm});
            skLineSegment(sketch, "E23.0.5.4", {"start": v(19.57, 172.96) * mm, "end": v(10, 156.38) * mm});
            skLineSegment(sketch, "E23.0.5.5", {"start": v(10, 156.38) * mm, "end": v(0.43, 172.96) * mm});
            skLineSegment(sketch, "E23.0.5.6", {"start": v(10, 190.03) * mm, "end": v(0.43, 173.46) * mm});
            skLineSegment(sketch, "E23.0.5.7", {"start": v(0.43, 173.46) * mm, "end": v(19.57, 173.46) * mm});
            skLineSegment(sketch, "E23.0.5.8", {"start": v(19.57, 173.46) * mm, "end": v(10, 190.03) * mm});
            skLineSegment(sketch, "E23.0.5.9", {"start": v(20, 173.7) * mm, "end": v(10.43, 190.28) * mm});
            skLineSegment(sketch, "E23.0.5.10", {"start": v(29.57, 190.28) * mm, "end": v(20, 173.7) * mm});
            skLineSegment(sketch, "E23.0.5.11", {"start": v(10.43, 190.28) * mm, "end": v(29.57, 190.28) * mm});
            skLineSegment(sketch, "E23.0.6.0", {"start": v(10.43, 190.78) * mm, "end": v(29.57, 190.78) * mm});
            skLineSegment(sketch, "E23.0.6.1", {"start": v(20, 207.35) * mm, "end": v(10.43, 190.78) * mm});
            skLineSegment(sketch, "E23.0.6.2", {"start": v(29.57, 190.78) * mm, "end": v(20, 207.35) * mm});
            skLineSegment(sketch, "E23.0.6.3", {"start": v(0.43, 207.6) * mm, "end": v(19.57, 207.6) * mm});
            skLineSegment(sketch, "E23.0.6.4", {"start": v(19.57, 207.6) * mm, "end": v(10, 191.03) * mm});
            skLineSegment(sketch, "E23.0.6.5", {"start": v(10, 191.03) * mm, "end": v(0.43, 207.6) * mm});
            skLineSegment(sketch, "E23.0.6.6", {"start": v(10, 224.67) * mm, "end": v(0.43, 208.1) * mm});
            skLineSegment(sketch, "E23.0.6.7", {"start": v(0.43, 208.1) * mm, "end": v(19.57, 208.1) * mm});
            skLineSegment(sketch, "E23.0.6.8", {"start": v(19.57, 208.1) * mm, "end": v(10, 224.67) * mm});
            skLineSegment(sketch, "E23.0.6.9", {"start": v(20, 208.35) * mm, "end": v(10.43, 224.92) * mm});
            skLineSegment(sketch, "E23.0.6.10", {"start": v(29.57, 224.92) * mm, "end": v(20, 208.35) * mm});
            skLineSegment(sketch, "E23.0.6.11", {"start": v(10.43, 224.92) * mm, "end": v(29.57, 224.92) * mm});
            skLineSegment(sketch, "E23.1.0.0", {"start": v(30.43, -17.07) * mm, "end": v(49.57, -17.07) * mm});
            skLineSegment(sketch, "E23.1.0.1", {"start": v(40, -0.5) * mm, "end": v(30.43, -17.07) * mm});
            skLineSegment(sketch, "E23.1.0.2", {"start": v(49.57, -17.07) * mm, "end": v(40, -0.5) * mm});
            skLineSegment(sketch, "E23.1.0.3", {"start": v(20.43, -0.25) * mm, "end": v(39.57, -0.25) * mm});
            skLineSegment(sketch, "E23.1.0.4", {"start": v(39.57, -0.25) * mm, "end": v(30, -16.82) * mm});
            skLineSegment(sketch, "E23.1.0.5", {"start": v(30, -16.82) * mm, "end": v(20.43, -0.25) * mm});
            skLineSegment(sketch, "E23.1.0.6", {"start": v(30, 16.82) * mm, "end": v(20.43, 0.25) * mm});
            skLineSegment(sketch, "E23.1.0.7", {"start": v(20.43, 0.25) * mm, "end": v(39.57, 0.25) * mm});
            skLineSegment(sketch, "E23.1.0.8", {"start": v(39.57, 0.25) * mm, "end": v(30, 16.82) * mm});
            skLineSegment(sketch, "E23.1.0.9", {"start": v(40, 0.5) * mm, "end": v(30.43, 17.07) * mm});
            skLineSegment(sketch, "E23.1.0.10", {"start": v(49.57, 17.07) * mm, "end": v(40, 0.5) * mm});
            skLineSegment(sketch, "E23.1.0.11", {"start": v(30.43, 17.07) * mm, "end": v(49.57, 17.07) * mm});
            skLineSegment(sketch, "E23.1.1.0", {"start": v(30.43, 17.57) * mm, "end": v(49.57, 17.57) * mm});
            skLineSegment(sketch, "E23.1.1.1", {"start": v(40, 34.14) * mm, "end": v(30.43, 17.57) * mm});
            skLineSegment(sketch, "E23.1.1.2", {"start": v(49.57, 17.57) * mm, "end": v(40, 34.14) * mm});
            skLineSegment(sketch, "E23.1.1.3", {"start": v(20.43, 34.4) * mm, "end": v(39.57, 34.4) * mm});
            skLineSegment(sketch, "E23.1.1.4", {"start": v(39.57, 34.4) * mm, "end": v(30, 17.82) * mm});
            skLineSegment(sketch, "E23.1.1.5", {"start": v(30, 17.82) * mm, "end": v(20.43, 34.4) * mm});
            skLineSegment(sketch, "E23.1.1.6", {"start": v(30, 51.46) * mm, "end": v(20.43, 34.9) * mm});
            skLineSegment(sketch, "E23.1.1.7", {"start": v(20.43, 34.9) * mm, "end": v(39.57, 34.9) * mm});
            skLineSegment(sketch, "E23.1.1.8", {"start": v(39.57, 34.9) * mm, "end": v(30, 51.46) * mm});
            skLineSegment(sketch, "E23.1.1.9", {"start": v(40, 35.14) * mm, "end": v(30.43, 51.71) * mm});
            skLineSegment(sketch, "E23.1.1.10", {"start": v(49.57, 51.71) * mm, "end": v(40, 35.14) * mm});
            skLineSegment(sketch, "E23.1.1.11", {"start": v(30.43, 51.71) * mm, "end": v(49.57, 51.71) * mm});
            skLineSegment(sketch, "E23.1.2.0", {"start": v(30.43, 52.21) * mm, "end": v(49.57, 52.21) * mm});
            skLineSegment(sketch, "E23.1.2.1", {"start": v(40, 68.78) * mm, "end": v(30.43, 52.21) * mm});
            skLineSegment(sketch, "E23.1.2.2", {"start": v(49.57, 52.21) * mm, "end": v(40, 68.78) * mm});
            skLineSegment(sketch, "E23.1.2.3", {"start": v(20.43, 69.03) * mm, "end": v(39.57, 69.03) * mm});
            skLineSegment(sketch, "E23.1.2.4", {"start": v(39.57, 69.03) * mm, "end": v(30, 52.46) * mm});
            skLineSegment(sketch, "E23.1.2.5", {"start": v(30, 52.46) * mm, "end": v(20.43, 69.03) * mm});
            skLineSegment(sketch, "E23.1.2.6", {"start": v(30, 86.1) * mm, "end": v(20.43, 69.53) * mm});
            skLineSegment(sketch, "E23.1.2.7", {"start": v(20.43, 69.53) * mm, "end": v(39.57, 69.53) * mm});
            skLineSegment(sketch, "E23.1.2.8", {"start": v(39.57, 69.53) * mm, "end": v(30, 86.1) * mm});
            skLineSegment(sketch, "E23.1.2.9", {"start": v(40, 69.78) * mm, "end": v(30.43, 86.35) * mm});
            skLineSegment(sketch, "E23.1.2.10", {"start": v(49.57, 86.35) * mm, "end": v(40, 69.78) * mm});
            skLineSegment(sketch, "E23.1.2.11", {"start": v(30.43, 86.35) * mm, "end": v(49.57, 86.35) * mm});
            skLineSegment(sketch, "E23.1.3.0", {"start": v(30.43, 86.85) * mm, "end": v(49.57, 86.85) * mm});
            skLineSegment(sketch, "E23.1.3.1", {"start": v(40, 103.42) * mm, "end": v(30.43, 86.85) * mm});
            skLineSegment(sketch, "E23.1.3.2", {"start": v(49.57, 86.85) * mm, "end": v(40, 103.42) * mm});
            skLineSegment(sketch, "E23.1.3.3", {"start": v(20.43, 103.67) * mm, "end": v(39.57, 103.67) * mm});
            skLineSegment(sketch, "E23.1.3.4", {"start": v(39.57, 103.67) * mm, "end": v(30, 87.1) * mm});
            skLineSegment(sketch, "E23.1.3.5", {"start": v(30, 87.1) * mm, "end": v(20.43, 103.67) * mm});
            skLineSegment(sketch, "E23.1.3.6", {"start": v(30, 120.74) * mm, "end": v(20.43, 104.17) * mm});
            skLineSegment(sketch, "E23.1.3.7", {"start": v(20.43, 104.17) * mm, "end": v(39.57, 104.17) * mm});
            skLineSegment(sketch, "E23.1.3.8", {"start": v(39.57, 104.17) * mm, "end": v(30, 120.74) * mm});
            skLineSegment(sketch, "E23.1.3.9", {"start": v(40, 104.42) * mm, "end": v(30.43, 121) * mm});
            skLineSegment(sketch, "E23.1.3.10", {"start": v(49.57, 121) * mm, "end": v(40, 104.42) * mm});
            skLineSegment(sketch, "E23.1.3.11", {"start": v(30.43, 121) * mm, "end": v(49.57, 121) * mm});
            skLineSegment(sketch, "E23.1.4.0", {"start": v(30.43, 121.5) * mm, "end": v(49.57, 121.5) * mm});
            skLineSegment(sketch, "E23.1.4.1", {"start": v(40, 138.06) * mm, "end": v(30.43, 121.5) * mm});
            skLineSegment(sketch, "E23.1.4.2", {"start": v(49.57, 121.5) * mm, "end": v(40, 138.06) * mm});
            skLineSegment(sketch, "E23.1.4.3", {"start": v(20.43, 138.31) * mm, "end": v(39.57, 138.31) * mm});
            skLineSegment(sketch, "E23.1.4.4", {"start": v(39.57, 138.31) * mm, "end": v(30, 121.74) * mm});
            skLineSegment(sketch, "E23.1.4.5", {"start": v(30, 121.74) * mm, "end": v(20.43, 138.31) * mm});
            skLineSegment(sketch, "E23.1.4.6", {"start": v(30, 155.38) * mm, "end": v(20.43, 138.81) * mm});
            skLineSegment(sketch, "E23.1.4.7", {"start": v(20.43, 138.81) * mm, "end": v(39.57, 138.81) * mm});
            skLineSegment(sketch, "E23.1.4.8", {"start": v(39.57, 138.81) * mm, "end": v(30, 155.38) * mm});
            skLineSegment(sketch, "E23.1.4.9", {"start": v(40, 139.06) * mm, "end": v(30.43, 155.63) * mm});
            skLineSegment(sketch, "E23.1.4.10", {"start": v(49.57, 155.63) * mm, "end": v(40, 139.06) * mm});
            skLineSegment(sketch, "E23.1.4.11", {"start": v(30.43, 155.63) * mm, "end": v(49.57, 155.63) * mm});
            skLineSegment(sketch, "E23.1.5.0", {"start": v(30.43, 156.13) * mm, "end": v(49.57, 156.13) * mm});
            skLineSegment(sketch, "E23.1.5.1", {"start": v(40, 172.7) * mm, "end": v(30.43, 156.13) * mm});
            skLineSegment(sketch, "E23.1.5.2", {"start": v(49.57, 156.13) * mm, "end": v(40, 172.7) * mm});
            skLineSegment(sketch, "E23.1.5.3", {"start": v(20.43, 172.96) * mm, "end": v(39.57, 172.96) * mm});
            skLineSegment(sketch, "E23.1.5.4", {"start": v(39.57, 172.96) * mm, "end": v(30, 156.38) * mm});
            skLineSegment(sketch, "E23.1.5.5", {"start": v(30, 156.38) * mm, "end": v(20.43, 172.96) * mm});
            skLineSegment(sketch, "E23.1.5.6", {"start": v(30, 190.03) * mm, "end": v(20.43, 173.46) * mm});
            skLineSegment(sketch, "E23.1.5.7", {"start": v(20.43, 173.46) * mm, "end": v(39.57, 173.46) * mm});
            skLineSegment(sketch, "E23.1.5.8", {"start": v(39.57, 173.46) * mm, "end": v(30, 190.03) * mm});
            skLineSegment(sketch, "E23.1.5.9", {"start": v(40, 173.7) * mm, "end": v(30.43, 190.28) * mm});
            skLineSegment(sketch, "E23.1.5.10", {"start": v(49.57, 190.28) * mm, "end": v(40, 173.7) * mm});
            skLineSegment(sketch, "E23.1.5.11", {"start": v(30.43, 190.28) * mm, "end": v(49.57, 190.28) * mm});
            skLineSegment(sketch, "E23.1.6.0", {"start": v(30.43, 190.78) * mm, "end": v(49.57, 190.78) * mm});
            skLineSegment(sketch, "E23.1.6.1", {"start": v(40, 207.35) * mm, "end": v(30.43, 190.78) * mm});
            skLineSegment(sketch, "E23.1.6.2", {"start": v(49.57, 190.78) * mm, "end": v(40, 207.35) * mm});
            skLineSegment(sketch, "E23.1.6.3", {"start": v(20.43, 207.6) * mm, "end": v(39.57, 207.6) * mm});
            skLineSegment(sketch, "E23.1.6.4", {"start": v(39.57, 207.6) * mm, "end": v(30, 191.03) * mm});
            skLineSegment(sketch, "E23.1.6.5", {"start": v(30, 191.03) * mm, "end": v(20.43, 207.6) * mm});
            skLineSegment(sketch, "E23.1.6.6", {"start": v(30, 224.67) * mm, "end": v(20.43, 208.1) * mm});
            skLineSegment(sketch, "E23.1.6.7", {"start": v(20.43, 208.1) * mm, "end": v(39.57, 208.1) * mm});
            skLineSegment(sketch, "E23.1.6.8", {"start": v(39.57, 208.1) * mm, "end": v(30, 224.67) * mm});
            skLineSegment(sketch, "E23.1.6.9", {"start": v(40, 208.35) * mm, "end": v(30.43, 224.92) * mm});
            skLineSegment(sketch, "E23.1.6.10", {"start": v(49.57, 224.92) * mm, "end": v(40, 208.35) * mm});
            skLineSegment(sketch, "E23.1.6.11", {"start": v(30.43, 224.92) * mm, "end": v(49.57, 224.92) * mm});
            skLineSegment(sketch, "E23.2.0.0", {"start": v(50.43, -17.07) * mm, "end": v(69.57, -17.07) * mm});
            skLineSegment(sketch, "E23.2.0.1", {"start": v(60, -0.5) * mm, "end": v(50.43, -17.07) * mm});
            skLineSegment(sketch, "E23.2.0.2", {"start": v(69.57, -17.07) * mm, "end": v(60, -0.5) * mm});
            skLineSegment(sketch, "E23.2.0.3", {"start": v(40.43, -0.25) * mm, "end": v(59.57, -0.25) * mm});
            skLineSegment(sketch, "E23.2.0.4", {"start": v(59.57, -0.25) * mm, "end": v(50, -16.82) * mm});
            skLineSegment(sketch, "E23.2.0.5", {"start": v(50, -16.82) * mm, "end": v(40.43, -0.25) * mm});
            skLineSegment(sketch, "E23.2.0.6", {"start": v(50, 16.82) * mm, "end": v(40.43, 0.25) * mm});
            skLineSegment(sketch, "E23.2.0.7", {"start": v(40.43, 0.25) * mm, "end": v(59.57, 0.25) * mm});
            skLineSegment(sketch, "E23.2.0.8", {"start": v(59.57, 0.25) * mm, "end": v(50, 16.82) * mm});
            skLineSegment(sketch, "E23.2.0.9", {"start": v(60, 0.5) * mm, "end": v(50.43, 17.07) * mm});
            skLineSegment(sketch, "E23.2.0.10", {"start": v(69.57, 17.07) * mm, "end": v(60, 0.5) * mm});
            skLineSegment(sketch, "E23.2.0.11", {"start": v(50.43, 17.07) * mm, "end": v(69.57, 17.07) * mm});
            skLineSegment(sketch, "E23.2.1.0", {"start": v(50.43, 17.57) * mm, "end": v(69.57, 17.57) * mm});
            skLineSegment(sketch, "E23.2.1.1", {"start": v(60, 34.14) * mm, "end": v(50.43, 17.57) * mm});
            skLineSegment(sketch, "E23.2.1.2", {"start": v(69.57, 17.57) * mm, "end": v(60, 34.14) * mm});
            skLineSegment(sketch, "E23.2.1.3", {"start": v(40.43, 34.4) * mm, "end": v(59.57, 34.4) * mm});
            skLineSegment(sketch, "E23.2.1.4", {"start": v(59.57, 34.4) * mm, "end": v(50, 17.82) * mm});
            skLineSegment(sketch, "E23.2.1.5", {"start": v(50, 17.82) * mm, "end": v(40.43, 34.4) * mm});
            skLineSegment(sketch, "E23.2.1.6", {"start": v(50, 51.46) * mm, "end": v(40.43, 34.9) * mm});
            skLineSegment(sketch, "E23.2.1.7", {"start": v(40.43, 34.9) * mm, "end": v(59.57, 34.9) * mm});
            skLineSegment(sketch, "E23.2.1.8", {"start": v(59.57, 34.9) * mm, "end": v(50, 51.46) * mm});
            skLineSegment(sketch, "E23.2.1.9", {"start": v(60, 35.14) * mm, "end": v(50.43, 51.71) * mm});
            skLineSegment(sketch, "E23.2.1.10", {"start": v(69.57, 51.71) * mm, "end": v(60, 35.14) * mm});
            skLineSegment(sketch, "E23.2.1.11", {"start": v(50.43, 51.71) * mm, "end": v(69.57, 51.71) * mm});
            skLineSegment(sketch, "E23.2.2.0", {"start": v(50.43, 52.21) * mm, "end": v(69.57, 52.21) * mm});
            skLineSegment(sketch, "E23.2.2.1", {"start": v(60, 68.78) * mm, "end": v(50.43, 52.21) * mm});
            skLineSegment(sketch, "E23.2.2.2", {"start": v(69.57, 52.21) * mm, "end": v(60, 68.78) * mm});
            skLineSegment(sketch, "E23.2.2.3", {"start": v(40.43, 69.03) * mm, "end": v(59.57, 69.03) * mm});
            skLineSegment(sketch, "E23.2.2.4", {"start": v(59.57, 69.03) * mm, "end": v(50, 52.46) * mm});
            skLineSegment(sketch, "E23.2.2.5", {"start": v(50, 52.46) * mm, "end": v(40.43, 69.03) * mm});
            skLineSegment(sketch, "E23.2.2.6", {"start": v(50, 86.1) * mm, "end": v(40.43, 69.53) * mm});
            skLineSegment(sketch, "E23.2.2.7", {"start": v(40.43, 69.53) * mm, "end": v(59.57, 69.53) * mm});
            skLineSegment(sketch, "E23.2.2.8", {"start": v(59.57, 69.53) * mm, "end": v(50, 86.1) * mm});
            skLineSegment(sketch, "E23.2.2.9", {"start": v(60, 69.78) * mm, "end": v(50.43, 86.35) * mm});
            skLineSegment(sketch, "E23.2.2.10", {"start": v(69.57, 86.35) * mm, "end": v(60, 69.78) * mm});
            skLineSegment(sketch, "E23.2.2.11", {"start": v(50.43, 86.35) * mm, "end": v(69.57, 86.35) * mm});
            skLineSegment(sketch, "E23.2.3.0", {"start": v(50.43, 86.85) * mm, "end": v(69.57, 86.85) * mm});
            skLineSegment(sketch, "E23.2.3.1", {"start": v(60, 103.42) * mm, "end": v(50.43, 86.85) * mm});
            skLineSegment(sketch, "E23.2.3.2", {"start": v(69.57, 86.85) * mm, "end": v(60, 103.42) * mm});
            skLineSegment(sketch, "E23.2.3.3", {"start": v(40.43, 103.67) * mm, "end": v(59.57, 103.67) * mm});
            skLineSegment(sketch, "E23.2.3.4", {"start": v(59.57, 103.67) * mm, "end": v(50, 87.1) * mm});
            skLineSegment(sketch, "E23.2.3.5", {"start": v(50, 87.1) * mm, "end": v(40.43, 103.67) * mm});
            skLineSegment(sketch, "E23.2.3.6", {"start": v(50, 120.74) * mm, "end": v(40.43, 104.17) * mm});
            skLineSegment(sketch, "E23.2.3.7", {"start": v(40.43, 104.17) * mm, "end": v(59.57, 104.17) * mm});
            skLineSegment(sketch, "E23.2.3.8", {"start": v(59.57, 104.17) * mm, "end": v(50, 120.74) * mm});
            skLineSegment(sketch, "E23.2.3.9", {"start": v(60, 104.42) * mm, "end": v(50.43, 121) * mm});
            skLineSegment(sketch, "E23.2.3.10", {"start": v(69.57, 121) * mm, "end": v(60, 104.42) * mm});
            skLineSegment(sketch, "E23.2.3.11", {"start": v(50.43, 121) * mm, "end": v(69.57, 121) * mm});
            skLineSegment(sketch, "E23.2.4.0", {"start": v(50.43, 121.5) * mm, "end": v(69.57, 121.5) * mm});
            skLineSegment(sketch, "E23.2.4.1", {"start": v(60, 138.06) * mm, "end": v(50.43, 121.5) * mm});
            skLineSegment(sketch, "E23.2.4.2", {"start": v(69.57, 121.5) * mm, "end": v(60, 138.06) * mm});
            skLineSegment(sketch, "E23.2.4.3", {"start": v(40.43, 138.31) * mm, "end": v(59.57, 138.31) * mm});
            skLineSegment(sketch, "E23.2.4.4", {"start": v(59.57, 138.31) * mm, "end": v(50, 121.74) * mm});
            skLineSegment(sketch, "E23.2.4.5", {"start": v(50, 121.74) * mm, "end": v(40.43, 138.31) * mm});
            skLineSegment(sketch, "E23.2.4.6", {"start": v(50, 155.38) * mm, "end": v(40.43, 138.81) * mm});
            skLineSegment(sketch, "E23.2.4.7", {"start": v(40.43, 138.81) * mm, "end": v(59.57, 138.81) * mm});
            skLineSegment(sketch, "E23.2.4.8", {"start": v(59.57, 138.81) * mm, "end": v(50, 155.38) * mm});
            skLineSegment(sketch, "E23.2.4.9", {"start": v(60, 139.06) * mm, "end": v(50.43, 155.63) * mm});
            skLineSegment(sketch, "E23.2.4.10", {"start": v(69.57, 155.63) * mm, "end": v(60, 139.06) * mm});
            skLineSegment(sketch, "E23.2.4.11", {"start": v(50.43, 155.63) * mm, "end": v(69.57, 155.63) * mm});
            skLineSegment(sketch, "E23.2.5.0", {"start": v(50.43, 156.13) * mm, "end": v(69.57, 156.13) * mm});
            skLineSegment(sketch, "E23.2.5.1", {"start": v(60, 172.7) * mm, "end": v(50.43, 156.13) * mm});
            skLineSegment(sketch, "E23.2.5.2", {"start": v(69.57, 156.13) * mm, "end": v(60, 172.7) * mm});
            skLineSegment(sketch, "E23.2.5.3", {"start": v(40.43, 172.96) * mm, "end": v(59.57, 172.96) * mm});
            skLineSegment(sketch, "E23.2.5.4", {"start": v(59.57, 172.96) * mm, "end": v(50, 156.38) * mm});
            skLineSegment(sketch, "E23.2.5.5", {"start": v(50, 156.38) * mm, "end": v(40.43, 172.96) * mm});
            skLineSegment(sketch, "E23.2.5.6", {"start": v(50, 190.03) * mm, "end": v(40.43, 173.46) * mm});
            skLineSegment(sketch, "E23.2.5.7", {"start": v(40.43, 173.46) * mm, "end": v(59.57, 173.46) * mm});
            skLineSegment(sketch, "E23.2.5.8", {"start": v(59.57, 173.46) * mm, "end": v(50, 190.03) * mm});
            skLineSegment(sketch, "E23.2.5.9", {"start": v(60, 173.7) * mm, "end": v(50.43, 190.28) * mm});
            skLineSegment(sketch, "E23.2.5.10", {"start": v(69.57, 190.28) * mm, "end": v(60, 173.7) * mm});
            skLineSegment(sketch, "E23.2.5.11", {"start": v(50.43, 190.28) * mm, "end": v(69.57, 190.28) * mm});
            skLineSegment(sketch, "E23.2.6.0", {"start": v(50.43, 190.78) * mm, "end": v(69.57, 190.78) * mm});
            skLineSegment(sketch, "E23.2.6.1", {"start": v(60, 207.35) * mm, "end": v(50.43, 190.78) * mm});
            skLineSegment(sketch, "E23.2.6.2", {"start": v(69.57, 190.78) * mm, "end": v(60, 207.35) * mm});
            skLineSegment(sketch, "E23.2.6.3", {"start": v(40.43, 207.6) * mm, "end": v(59.57, 207.6) * mm});
            skLineSegment(sketch, "E23.2.6.4", {"start": v(59.57, 207.6) * mm, "end": v(50, 191.03) * mm});
            skLineSegment(sketch, "E23.2.6.5", {"start": v(50, 191.03) * mm, "end": v(40.43, 207.6) * mm});
            skLineSegment(sketch, "E23.2.6.6", {"start": v(50, 224.67) * mm, "end": v(40.43, 208.1) * mm});
            skLineSegment(sketch, "E23.2.6.7", {"start": v(40.43, 208.1) * mm, "end": v(59.57, 208.1) * mm});
            skLineSegment(sketch, "E23.2.6.8", {"start": v(59.57, 208.1) * mm, "end": v(50, 224.67) * mm});
            skLineSegment(sketch, "E23.2.6.9", {"start": v(60, 208.35) * mm, "end": v(50.43, 224.92) * mm});
            skLineSegment(sketch, "E23.2.6.10", {"start": v(69.57, 224.92) * mm, "end": v(60, 208.35) * mm});
            skLineSegment(sketch, "E23.2.6.11", {"start": v(50.43, 224.92) * mm, "end": v(69.57, 224.92) * mm});
            skLineSegment(sketch, "E23.3.0.0", {"start": v(70.43, -17.07) * mm, "end": v(89.57, -17.07) * mm});
            skLineSegment(sketch, "E23.3.0.1", {"start": v(80, -0.5) * mm, "end": v(70.43, -17.07) * mm});
            skLineSegment(sketch, "E23.3.0.2", {"start": v(89.57, -17.07) * mm, "end": v(80, -0.5) * mm});
            skLineSegment(sketch, "E23.3.0.3", {"start": v(60.43, -0.25) * mm, "end": v(79.57, -0.25) * mm});
            skLineSegment(sketch, "E23.3.0.4", {"start": v(79.57, -0.25) * mm, "end": v(70, -16.82) * mm});
            skLineSegment(sketch, "E23.3.0.5", {"start": v(70, -16.82) * mm, "end": v(60.43, -0.25) * mm});
            skLineSegment(sketch, "E23.3.0.6", {"start": v(70, 16.82) * mm, "end": v(60.43, 0.25) * mm});
            skLineSegment(sketch, "E23.3.0.7", {"start": v(60.43, 0.25) * mm, "end": v(79.57, 0.25) * mm});
            skLineSegment(sketch, "E23.3.0.8", {"start": v(79.57, 0.25) * mm, "end": v(70, 16.82) * mm});
            skLineSegment(sketch, "E23.3.0.9", {"start": v(80, 0.5) * mm, "end": v(70.43, 17.07) * mm});
            skLineSegment(sketch, "E23.3.0.10", {"start": v(89.57, 17.07) * mm, "end": v(80, 0.5) * mm});
            skLineSegment(sketch, "E23.3.0.11", {"start": v(70.43, 17.07) * mm, "end": v(89.57, 17.07) * mm});
            skLineSegment(sketch, "E23.3.1.0", {"start": v(70.43, 17.57) * mm, "end": v(89.57, 17.57) * mm});
            skLineSegment(sketch, "E23.3.1.1", {"start": v(80, 34.14) * mm, "end": v(70.43, 17.57) * mm});
            skLineSegment(sketch, "E23.3.1.2", {"start": v(89.57, 17.57) * mm, "end": v(80, 34.14) * mm});
            skLineSegment(sketch, "E23.3.1.3", {"start": v(60.43, 34.4) * mm, "end": v(79.57, 34.4) * mm});
            skLineSegment(sketch, "E23.3.1.4", {"start": v(79.57, 34.4) * mm, "end": v(70, 17.82) * mm});
            skLineSegment(sketch, "E23.3.1.5", {"start": v(70, 17.82) * mm, "end": v(60.43, 34.4) * mm});
            skLineSegment(sketch, "E23.3.1.6", {"start": v(70, 51.46) * mm, "end": v(60.43, 34.9) * mm});
            skLineSegment(sketch, "E23.3.1.7", {"start": v(60.43, 34.9) * mm, "end": v(79.57, 34.9) * mm});
            skLineSegment(sketch, "E23.3.1.8", {"start": v(79.57, 34.9) * mm, "end": v(70, 51.46) * mm});
            skLineSegment(sketch, "E23.3.1.9", {"start": v(80, 35.14) * mm, "end": v(70.43, 51.71) * mm});
            skLineSegment(sketch, "E23.3.1.10", {"start": v(89.57, 51.71) * mm, "end": v(80, 35.14) * mm});
            skLineSegment(sketch, "E23.3.1.11", {"start": v(70.43, 51.71) * mm, "end": v(89.57, 51.71) * mm});
            skLineSegment(sketch, "E23.3.2.0", {"start": v(70.43, 52.21) * mm, "end": v(89.57, 52.21) * mm});
            skLineSegment(sketch, "E23.3.2.1", {"start": v(80, 68.78) * mm, "end": v(70.43, 52.21) * mm});
            skLineSegment(sketch, "E23.3.2.2", {"start": v(89.57, 52.21) * mm, "end": v(80, 68.78) * mm});
            skLineSegment(sketch, "E23.3.2.3", {"start": v(60.43, 69.03) * mm, "end": v(79.57, 69.03) * mm});
            skLineSegment(sketch, "E23.3.2.4", {"start": v(79.57, 69.03) * mm, "end": v(70, 52.46) * mm});
            skLineSegment(sketch, "E23.3.2.5", {"start": v(70, 52.46) * mm, "end": v(60.43, 69.03) * mm});
            skLineSegment(sketch, "E23.3.2.6", {"start": v(70, 86.1) * mm, "end": v(60.43, 69.53) * mm});
            skLineSegment(sketch, "E23.3.2.7", {"start": v(60.43, 69.53) * mm, "end": v(79.57, 69.53) * mm});
            skLineSegment(sketch, "E23.3.2.8", {"start": v(79.57, 69.53) * mm, "end": v(70, 86.1) * mm});
            skLineSegment(sketch, "E23.3.2.9", {"start": v(80, 69.78) * mm, "end": v(70.43, 86.35) * mm});
            skLineSegment(sketch, "E23.3.2.10", {"start": v(89.57, 86.35) * mm, "end": v(80, 69.78) * mm});
            skLineSegment(sketch, "E23.3.2.11", {"start": v(70.43, 86.35) * mm, "end": v(89.57, 86.35) * mm});
            skLineSegment(sketch, "E23.3.3.0", {"start": v(70.43, 86.85) * mm, "end": v(89.57, 86.85) * mm});
            skLineSegment(sketch, "E23.3.3.1", {"start": v(80, 103.42) * mm, "end": v(70.43, 86.85) * mm});
            skLineSegment(sketch, "E23.3.3.2", {"start": v(89.57, 86.85) * mm, "end": v(80, 103.42) * mm});
            skLineSegment(sketch, "E23.3.3.3", {"start": v(60.43, 103.67) * mm, "end": v(79.57, 103.67) * mm});
            skLineSegment(sketch, "E23.3.3.4", {"start": v(79.57, 103.67) * mm, "end": v(70, 87.1) * mm});
            skLineSegment(sketch, "E23.3.3.5", {"start": v(70, 87.1) * mm, "end": v(60.43, 103.67) * mm});
            skLineSegment(sketch, "E23.3.3.6", {"start": v(70, 120.74) * mm, "end": v(60.43, 104.17) * mm});
            skLineSegment(sketch, "E23.3.3.7", {"start": v(60.43, 104.17) * mm, "end": v(79.57, 104.17) * mm});
            skLineSegment(sketch, "E23.3.3.8", {"start": v(79.57, 104.17) * mm, "end": v(70, 120.74) * mm});
            skLineSegment(sketch, "E23.3.3.9", {"start": v(80, 104.42) * mm, "end": v(70.43, 121) * mm});
            skLineSegment(sketch, "E23.3.3.10", {"start": v(89.57, 121) * mm, "end": v(80, 104.42) * mm});
            skLineSegment(sketch, "E23.3.3.11", {"start": v(70.43, 121) * mm, "end": v(89.57, 121) * mm});
            skLineSegment(sketch, "E23.3.4.0", {"start": v(70.43, 121.5) * mm, "end": v(89.57, 121.5) * mm});
            skLineSegment(sketch, "E23.3.4.1", {"start": v(80, 138.06) * mm, "end": v(70.43, 121.5) * mm});
            skLineSegment(sketch, "E23.3.4.2", {"start": v(89.57, 121.5) * mm, "end": v(80, 138.06) * mm});
            skLineSegment(sketch, "E23.3.4.3", {"start": v(60.43, 138.31) * mm, "end": v(79.57, 138.31) * mm});
            skLineSegment(sketch, "E23.3.4.4", {"start": v(79.57, 138.31) * mm, "end": v(70, 121.74) * mm});
            skLineSegment(sketch, "E23.3.4.5", {"start": v(70, 121.74) * mm, "end": v(60.43, 138.31) * mm});
            skLineSegment(sketch, "E23.3.4.6", {"start": v(70, 155.38) * mm, "end": v(60.43, 138.81) * mm});
            skLineSegment(sketch, "E23.3.4.7", {"start": v(60.43, 138.81) * mm, "end": v(79.57, 138.81) * mm});
            skLineSegment(sketch, "E23.3.4.8", {"start": v(79.57, 138.81) * mm, "end": v(70, 155.38) * mm});
            skLineSegment(sketch, "E23.3.4.9", {"start": v(80, 139.06) * mm, "end": v(70.43, 155.63) * mm});
            skLineSegment(sketch, "E23.3.4.10", {"start": v(89.57, 155.63) * mm, "end": v(80, 139.06) * mm});
            skLineSegment(sketch, "E23.3.4.11", {"start": v(70.43, 155.63) * mm, "end": v(89.57, 155.63) * mm});
            skLineSegment(sketch, "E23.3.5.0", {"start": v(70.43, 156.13) * mm, "end": v(89.57, 156.13) * mm});
            skLineSegment(sketch, "E23.3.5.1", {"start": v(80, 172.7) * mm, "end": v(70.43, 156.13) * mm});
            skLineSegment(sketch, "E23.3.5.2", {"start": v(89.57, 156.13) * mm, "end": v(80, 172.7) * mm});
            skLineSegment(sketch, "E23.3.5.3", {"start": v(60.43, 172.96) * mm, "end": v(79.57, 172.96) * mm});
            skLineSegment(sketch, "E23.3.5.4", {"start": v(79.57, 172.96) * mm, "end": v(70, 156.38) * mm});
            skLineSegment(sketch, "E23.3.5.5", {"start": v(70, 156.38) * mm, "end": v(60.43, 172.96) * mm});
            skLineSegment(sketch, "E23.3.5.6", {"start": v(70, 190.03) * mm, "end": v(60.43, 173.46) * mm});
            skLineSegment(sketch, "E23.3.5.7", {"start": v(60.43, 173.46) * mm, "end": v(79.57, 173.46) * mm});
            skLineSegment(sketch, "E23.3.5.8", {"start": v(79.57, 173.46) * mm, "end": v(70, 190.03) * mm});
            skLineSegment(sketch, "E23.3.5.9", {"start": v(80, 173.7) * mm, "end": v(70.43, 190.28) * mm});
            skLineSegment(sketch, "E23.3.5.10", {"start": v(89.57, 190.28) * mm, "end": v(80, 173.7) * mm});
            skLineSegment(sketch, "E23.3.5.11", {"start": v(70.43, 190.28) * mm, "end": v(89.57, 190.28) * mm});
            skLineSegment(sketch, "E23.3.6.0", {"start": v(70.43, 190.78) * mm, "end": v(89.57, 190.78) * mm});
            skLineSegment(sketch, "E23.3.6.1", {"start": v(80, 207.35) * mm, "end": v(70.43, 190.78) * mm});
            skLineSegment(sketch, "E23.3.6.2", {"start": v(89.57, 190.78) * mm, "end": v(80, 207.35) * mm});
            skLineSegment(sketch, "E23.3.6.3", {"start": v(60.43, 207.6) * mm, "end": v(79.57, 207.6) * mm});
            skLineSegment(sketch, "E23.3.6.4", {"start": v(79.57, 207.6) * mm, "end": v(70, 191.03) * mm});
            skLineSegment(sketch, "E23.3.6.5", {"start": v(70, 191.03) * mm, "end": v(60.43, 207.6) * mm});
            skLineSegment(sketch, "E23.3.6.6", {"start": v(70, 224.67) * mm, "end": v(60.43, 208.1) * mm});
            skLineSegment(sketch, "E23.3.6.7", {"start": v(60.43, 208.1) * mm, "end": v(79.57, 208.1) * mm});
            skLineSegment(sketch, "E23.3.6.8", {"start": v(79.57, 208.1) * mm, "end": v(70, 224.67) * mm});
            skLineSegment(sketch, "E23.3.6.9", {"start": v(80, 208.35) * mm, "end": v(70.43, 224.92) * mm});
            skLineSegment(sketch, "E23.3.6.10", {"start": v(89.57, 224.92) * mm, "end": v(80, 208.35) * mm});
            skLineSegment(sketch, "E23.3.6.11", {"start": v(70.43, 224.92) * mm, "end": v(89.57, 224.92) * mm});
            skLineSegment(sketch, "E23.4.0.0", {"start": v(90.43, -17.07) * mm, "end": v(109.57, -17.07) * mm});
            skLineSegment(sketch, "E23.4.0.1", {"start": v(100, -0.5) * mm, "end": v(90.43, -17.07) * mm});
            skLineSegment(sketch, "E23.4.0.2", {"start": v(109.57, -17.07) * mm, "end": v(100, -0.5) * mm});
            skLineSegment(sketch, "E23.4.0.3", {"start": v(80.43, -0.25) * mm, "end": v(99.57, -0.25) * mm});
            skLineSegment(sketch, "E23.4.0.4", {"start": v(99.57, -0.25) * mm, "end": v(90, -16.82) * mm});
            skLineSegment(sketch, "E23.4.0.5", {"start": v(90, -16.82) * mm, "end": v(80.43, -0.25) * mm});
            skLineSegment(sketch, "E23.4.0.6", {"start": v(90, 16.82) * mm, "end": v(80.43, 0.25) * mm});
            skLineSegment(sketch, "E23.4.0.7", {"start": v(80.43, 0.25) * mm, "end": v(99.57, 0.25) * mm});
            skLineSegment(sketch, "E23.4.0.8", {"start": v(99.57, 0.25) * mm, "end": v(90, 16.82) * mm});
            skLineSegment(sketch, "E23.4.0.9", {"start": v(100, 0.5) * mm, "end": v(90.43, 17.07) * mm});
            skLineSegment(sketch, "E23.4.0.10", {"start": v(109.57, 17.07) * mm, "end": v(100, 0.5) * mm});
            skLineSegment(sketch, "E23.4.0.11", {"start": v(90.43, 17.07) * mm, "end": v(109.57, 17.07) * mm});
            skLineSegment(sketch, "E23.4.1.0", {"start": v(90.43, 17.57) * mm, "end": v(109.57, 17.57) * mm});
            skLineSegment(sketch, "E23.4.1.1", {"start": v(100, 34.14) * mm, "end": v(90.43, 17.57) * mm});
            skLineSegment(sketch, "E23.4.1.2", {"start": v(109.57, 17.57) * mm, "end": v(100, 34.14) * mm});
            skLineSegment(sketch, "E23.4.1.3", {"start": v(80.43, 34.4) * mm, "end": v(99.57, 34.4) * mm});
            skLineSegment(sketch, "E23.4.1.4", {"start": v(99.57, 34.4) * mm, "end": v(90, 17.82) * mm});
            skLineSegment(sketch, "E23.4.1.5", {"start": v(90, 17.82) * mm, "end": v(80.43, 34.4) * mm});
            skLineSegment(sketch, "E23.4.1.6", {"start": v(90, 51.46) * mm, "end": v(80.43, 34.9) * mm});
            skLineSegment(sketch, "E23.4.1.7", {"start": v(80.43, 34.9) * mm, "end": v(99.57, 34.9) * mm});
            skLineSegment(sketch, "E23.4.1.8", {"start": v(99.57, 34.9) * mm, "end": v(90, 51.46) * mm});
            skLineSegment(sketch, "E23.4.1.9", {"start": v(100, 35.14) * mm, "end": v(90.43, 51.71) * mm});
            skLineSegment(sketch, "E23.4.1.10", {"start": v(109.57, 51.71) * mm, "end": v(100, 35.14) * mm});
            skLineSegment(sketch, "E23.4.1.11", {"start": v(90.43, 51.71) * mm, "end": v(109.57, 51.71) * mm});
            skLineSegment(sketch, "E23.4.2.0", {"start": v(90.43, 52.21) * mm, "end": v(109.57, 52.21) * mm});
            skLineSegment(sketch, "E23.4.2.1", {"start": v(100, 68.78) * mm, "end": v(90.43, 52.21) * mm});
            skLineSegment(sketch, "E23.4.2.2", {"start": v(109.57, 52.21) * mm, "end": v(100, 68.78) * mm});
            skLineSegment(sketch, "E23.4.2.3", {"start": v(80.43, 69.03) * mm, "end": v(99.57, 69.03) * mm});
            skLineSegment(sketch, "E23.4.2.4", {"start": v(99.57, 69.03) * mm, "end": v(90, 52.46) * mm});
            skLineSegment(sketch, "E23.4.2.5", {"start": v(90, 52.46) * mm, "end": v(80.43, 69.03) * mm});
            skLineSegment(sketch, "E23.4.2.6", {"start": v(90, 86.1) * mm, "end": v(80.43, 69.53) * mm});
            skLineSegment(sketch, "E23.4.2.7", {"start": v(80.43, 69.53) * mm, "end": v(99.57, 69.53) * mm});
            skLineSegment(sketch, "E23.4.2.8", {"start": v(99.57, 69.53) * mm, "end": v(90, 86.1) * mm});
            skLineSegment(sketch, "E23.4.2.9", {"start": v(100, 69.78) * mm, "end": v(90.43, 86.35) * mm});
            skLineSegment(sketch, "E23.4.2.10", {"start": v(109.57, 86.35) * mm, "end": v(100, 69.78) * mm});
            skLineSegment(sketch, "E23.4.2.11", {"start": v(90.43, 86.35) * mm, "end": v(109.57, 86.35) * mm});
            skLineSegment(sketch, "E23.4.3.0", {"start": v(90.43, 86.85) * mm, "end": v(109.57, 86.85) * mm});
            skLineSegment(sketch, "E23.4.3.1", {"start": v(100, 103.42) * mm, "end": v(90.43, 86.85) * mm});
            skLineSegment(sketch, "E23.4.3.2", {"start": v(109.57, 86.85) * mm, "end": v(100, 103.42) * mm});
            skLineSegment(sketch, "E23.4.3.3", {"start": v(80.43, 103.67) * mm, "end": v(99.57, 103.67) * mm});
            skLineSegment(sketch, "E23.4.3.4", {"start": v(99.57, 103.67) * mm, "end": v(90, 87.1) * mm});
            skLineSegment(sketch, "E23.4.3.5", {"start": v(90, 87.1) * mm, "end": v(80.43, 103.67) * mm});
            skLineSegment(sketch, "E23.4.3.6", {"start": v(90, 120.74) * mm, "end": v(80.43, 104.17) * mm});
            skLineSegment(sketch, "E23.4.3.7", {"start": v(80.43, 104.17) * mm, "end": v(99.57, 104.17) * mm});
            skLineSegment(sketch, "E23.4.3.8", {"start": v(99.57, 104.17) * mm, "end": v(90, 120.74) * mm});
            skLineSegment(sketch, "E23.4.3.9", {"start": v(100, 104.42) * mm, "end": v(90.43, 121) * mm});
            skLineSegment(sketch, "E23.4.3.10", {"start": v(109.57, 121) * mm, "end": v(100, 104.42) * mm});
            skLineSegment(sketch, "E23.4.3.11", {"start": v(90.43, 121) * mm, "end": v(109.57, 121) * mm});
            skLineSegment(sketch, "E23.4.4.0", {"start": v(90.43, 121.5) * mm, "end": v(109.57, 121.5) * mm});
            skLineSegment(sketch, "E23.4.4.1", {"start": v(100, 138.06) * mm, "end": v(90.43, 121.5) * mm});
            skLineSegment(sketch, "E23.4.4.2", {"start": v(109.57, 121.5) * mm, "end": v(100, 138.06) * mm});
            skLineSegment(sketch, "E23.4.4.3", {"start": v(80.43, 138.31) * mm, "end": v(99.57, 138.31) * mm});
            skLineSegment(sketch, "E23.4.4.4", {"start": v(99.57, 138.31) * mm, "end": v(90, 121.74) * mm});
            skLineSegment(sketch, "E23.4.4.5", {"start": v(90, 121.74) * mm, "end": v(80.43, 138.31) * mm});
            skLineSegment(sketch, "E23.4.4.6", {"start": v(90, 155.38) * mm, "end": v(80.43, 138.81) * mm});
            skLineSegment(sketch, "E23.4.4.7", {"start": v(80.43, 138.81) * mm, "end": v(99.57, 138.81) * mm});
            skLineSegment(sketch, "E23.4.4.8", {"start": v(99.57, 138.81) * mm, "end": v(90, 155.38) * mm});
            skLineSegment(sketch, "E23.4.4.9", {"start": v(100, 139.06) * mm, "end": v(90.43, 155.63) * mm});
            skLineSegment(sketch, "E23.4.4.10", {"start": v(109.57, 155.63) * mm, "end": v(100, 139.06) * mm});
            skLineSegment(sketch, "E23.4.4.11", {"start": v(90.43, 155.63) * mm, "end": v(109.57, 155.63) * mm});
            skLineSegment(sketch, "E23.4.5.0", {"start": v(90.43, 156.13) * mm, "end": v(109.57, 156.13) * mm});
            skLineSegment(sketch, "E23.4.5.1", {"start": v(100, 172.7) * mm, "end": v(90.43, 156.13) * mm});
            skLineSegment(sketch, "E23.4.5.2", {"start": v(109.57, 156.13) * mm, "end": v(100, 172.7) * mm});
            skLineSegment(sketch, "E23.4.5.3", {"start": v(80.43, 172.96) * mm, "end": v(99.57, 172.96) * mm});
            skLineSegment(sketch, "E23.4.5.4", {"start": v(99.57, 172.96) * mm, "end": v(90, 156.38) * mm});
            skLineSegment(sketch, "E23.4.5.5", {"start": v(90, 156.38) * mm, "end": v(80.43, 172.96) * mm});
            skLineSegment(sketch, "E23.4.5.6", {"start": v(90, 190.03) * mm, "end": v(80.43, 173.46) * mm});
            skLineSegment(sketch, "E23.4.5.7", {"start": v(80.43, 173.46) * mm, "end": v(99.57, 173.46) * mm});
            skLineSegment(sketch, "E23.4.5.8", {"start": v(99.57, 173.46) * mm, "end": v(90, 190.03) * mm});
            skLineSegment(sketch, "E23.4.5.9", {"start": v(100, 173.7) * mm, "end": v(90.43, 190.28) * mm});
            skLineSegment(sketch, "E23.4.5.10", {"start": v(109.57, 190.28) * mm, "end": v(100, 173.7) * mm});
            skLineSegment(sketch, "E23.4.5.11", {"start": v(90.43, 190.28) * mm, "end": v(109.57, 190.28) * mm});
            skLineSegment(sketch, "E23.4.6.0", {"start": v(90.43, 190.78) * mm, "end": v(109.57, 190.78) * mm});
            skLineSegment(sketch, "E23.4.6.1", {"start": v(100, 207.35) * mm, "end": v(90.43, 190.78) * mm});
            skLineSegment(sketch, "E23.4.6.2", {"start": v(109.57, 190.78) * mm, "end": v(100, 207.35) * mm});
            skLineSegment(sketch, "E23.4.6.3", {"start": v(80.43, 207.6) * mm, "end": v(99.57, 207.6) * mm});
            skLineSegment(sketch, "E23.4.6.4", {"start": v(99.57, 207.6) * mm, "end": v(90, 191.03) * mm});
            skLineSegment(sketch, "E23.4.6.5", {"start": v(90, 191.03) * mm, "end": v(80.43, 207.6) * mm});
            skLineSegment(sketch, "E23.4.6.6", {"start": v(90, 224.67) * mm, "end": v(80.43, 208.1) * mm});
            skLineSegment(sketch, "E23.4.6.7", {"start": v(80.43, 208.1) * mm, "end": v(99.57, 208.1) * mm});
            skLineSegment(sketch, "E23.4.6.8", {"start": v(99.57, 208.1) * mm, "end": v(90, 224.67) * mm});
            skLineSegment(sketch, "E23.4.6.9", {"start": v(100, 208.35) * mm, "end": v(90.43, 224.92) * mm});
            skLineSegment(sketch, "E23.4.6.10", {"start": v(109.57, 224.92) * mm, "end": v(100, 208.35) * mm});
            skLineSegment(sketch, "E23.4.6.11", {"start": v(90.43, 224.92) * mm, "end": v(109.57, 224.92) * mm});
            skLineSegment(sketch, "E23.5.0.0", {"start": v(110.43, -17.07) * mm, "end": v(129.57, -17.07) * mm});
            skLineSegment(sketch, "E23.5.0.1", {"start": v(120, -0.5) * mm, "end": v(110.43, -17.07) * mm});
            skLineSegment(sketch, "E23.5.0.2", {"start": v(129.57, -17.07) * mm, "end": v(120, -0.5) * mm});
            skLineSegment(sketch, "E23.5.0.3", {"start": v(100.43, -0.25) * mm, "end": v(119.57, -0.25) * mm});
            skLineSegment(sketch, "E23.5.0.4", {"start": v(119.57, -0.25) * mm, "end": v(110, -16.82) * mm});
            skLineSegment(sketch, "E23.5.0.5", {"start": v(110, -16.82) * mm, "end": v(100.43, -0.25) * mm});
            skLineSegment(sketch, "E23.5.0.6", {"start": v(110, 16.82) * mm, "end": v(100.43, 0.25) * mm});
            skLineSegment(sketch, "E23.5.0.7", {"start": v(100.43, 0.25) * mm, "end": v(119.57, 0.25) * mm});
            skLineSegment(sketch, "E23.5.0.8", {"start": v(119.57, 0.25) * mm, "end": v(110, 16.82) * mm});
            skLineSegment(sketch, "E23.5.0.9", {"start": v(120, 0.5) * mm, "end": v(110.43, 17.07) * mm});
            skLineSegment(sketch, "E23.5.0.10", {"start": v(129.57, 17.07) * mm, "end": v(120, 0.5) * mm});
            skLineSegment(sketch, "E23.5.0.11", {"start": v(110.43, 17.07) * mm, "end": v(129.57, 17.07) * mm});
            skLineSegment(sketch, "E23.5.1.0", {"start": v(110.43, 17.57) * mm, "end": v(129.57, 17.57) * mm});
            skLineSegment(sketch, "E23.5.1.1", {"start": v(120, 34.14) * mm, "end": v(110.43, 17.57) * mm});
            skLineSegment(sketch, "E23.5.1.2", {"start": v(129.57, 17.57) * mm, "end": v(120, 34.14) * mm});
            skLineSegment(sketch, "E23.5.1.3", {"start": v(100.43, 34.4) * mm, "end": v(119.57, 34.4) * mm});
            skLineSegment(sketch, "E23.5.1.4", {"start": v(119.57, 34.4) * mm, "end": v(110, 17.82) * mm});
            skLineSegment(sketch, "E23.5.1.5", {"start": v(110, 17.82) * mm, "end": v(100.43, 34.4) * mm});
            skLineSegment(sketch, "E23.5.1.6", {"start": v(110, 51.46) * mm, "end": v(100.43, 34.9) * mm});
            skLineSegment(sketch, "E23.5.1.7", {"start": v(100.43, 34.9) * mm, "end": v(119.57, 34.9) * mm});
            skLineSegment(sketch, "E23.5.1.8", {"start": v(119.57, 34.9) * mm, "end": v(110, 51.46) * mm});
            skLineSegment(sketch, "E23.5.1.9", {"start": v(120, 35.14) * mm, "end": v(110.43, 51.71) * mm});
            skLineSegment(sketch, "E23.5.1.10", {"start": v(129.57, 51.71) * mm, "end": v(120, 35.14) * mm});
            skLineSegment(sketch, "E23.5.1.11", {"start": v(110.43, 51.71) * mm, "end": v(129.57, 51.71) * mm});
            skLineSegment(sketch, "E23.5.2.0", {"start": v(110.43, 52.21) * mm, "end": v(129.57, 52.21) * mm});
            skLineSegment(sketch, "E23.5.2.1", {"start": v(120, 68.78) * mm, "end": v(110.43, 52.21) * mm});
            skLineSegment(sketch, "E23.5.2.2", {"start": v(129.57, 52.21) * mm, "end": v(120, 68.78) * mm});
            skLineSegment(sketch, "E23.5.2.3", {"start": v(100.43, 69.03) * mm, "end": v(119.57, 69.03) * mm});
            skLineSegment(sketch, "E23.5.2.4", {"start": v(119.57, 69.03) * mm, "end": v(110, 52.46) * mm});
            skLineSegment(sketch, "E23.5.2.5", {"start": v(110, 52.46) * mm, "end": v(100.43, 69.03) * mm});
            skLineSegment(sketch, "E23.5.2.6", {"start": v(110, 86.1) * mm, "end": v(100.43, 69.53) * mm});
            skLineSegment(sketch, "E23.5.2.7", {"start": v(100.43, 69.53) * mm, "end": v(119.57, 69.53) * mm});
            skLineSegment(sketch, "E23.5.2.8", {"start": v(119.57, 69.53) * mm, "end": v(110, 86.1) * mm});
            skLineSegment(sketch, "E23.5.2.9", {"start": v(120, 69.78) * mm, "end": v(110.43, 86.35) * mm});
            skLineSegment(sketch, "E23.5.2.10", {"start": v(129.57, 86.35) * mm, "end": v(120, 69.78) * mm});
            skLineSegment(sketch, "E23.5.2.11", {"start": v(110.43, 86.35) * mm, "end": v(129.57, 86.35) * mm});
            skLineSegment(sketch, "E23.5.3.0", {"start": v(110.43, 86.85) * mm, "end": v(129.57, 86.85) * mm});
            skLineSegment(sketch, "E23.5.3.1", {"start": v(120, 103.42) * mm, "end": v(110.43, 86.85) * mm});
            skLineSegment(sketch, "E23.5.3.2", {"start": v(129.57, 86.85) * mm, "end": v(120, 103.42) * mm});
            skLineSegment(sketch, "E23.5.3.3", {"start": v(100.43, 103.67) * mm, "end": v(119.57, 103.67) * mm});
            skLineSegment(sketch, "E23.5.3.4", {"start": v(119.57, 103.67) * mm, "end": v(110, 87.1) * mm});
            skLineSegment(sketch, "E23.5.3.5", {"start": v(110, 87.1) * mm, "end": v(100.43, 103.67) * mm});
            skLineSegment(sketch, "E23.5.3.6", {"start": v(110, 120.74) * mm, "end": v(100.43, 104.17) * mm});
            skLineSegment(sketch, "E23.5.3.7", {"start": v(100.43, 104.17) * mm, "end": v(119.57, 104.17) * mm});
            skLineSegment(sketch, "E23.5.3.8", {"start": v(119.57, 104.17) * mm, "end": v(110, 120.74) * mm});
            skLineSegment(sketch, "E23.5.3.9", {"start": v(120, 104.42) * mm, "end": v(110.43, 121) * mm});
            skLineSegment(sketch, "E23.5.3.10", {"start": v(129.57, 121) * mm, "end": v(120, 104.42) * mm});
            skLineSegment(sketch, "E23.5.3.11", {"start": v(110.43, 121) * mm, "end": v(129.57, 121) * mm});
            skLineSegment(sketch, "E23.5.4.0", {"start": v(110.43, 121.5) * mm, "end": v(129.57, 121.5) * mm});
            skLineSegment(sketch, "E23.5.4.1", {"start": v(120, 138.06) * mm, "end": v(110.43, 121.5) * mm});
            skLineSegment(sketch, "E23.5.4.2", {"start": v(129.57, 121.5) * mm, "end": v(120, 138.06) * mm});
            skLineSegment(sketch, "E23.5.4.3", {"start": v(100.43, 138.31) * mm, "end": v(119.57, 138.31) * mm});
            skLineSegment(sketch, "E23.5.4.4", {"start": v(119.57, 138.31) * mm, "end": v(110, 121.74) * mm});
            skLineSegment(sketch, "E23.5.4.5", {"start": v(110, 121.74) * mm, "end": v(100.43, 138.31) * mm});
            skLineSegment(sketch, "E23.5.4.6", {"start": v(110, 155.38) * mm, "end": v(100.43, 138.81) * mm});
            skLineSegment(sketch, "E23.5.4.7", {"start": v(100.43, 138.81) * mm, "end": v(119.57, 138.81) * mm});
            skLineSegment(sketch, "E23.5.4.8", {"start": v(119.57, 138.81) * mm, "end": v(110, 155.38) * mm});
            skLineSegment(sketch, "E23.5.4.9", {"start": v(120, 139.06) * mm, "end": v(110.43, 155.63) * mm});
            skLineSegment(sketch, "E23.5.4.10", {"start": v(129.57, 155.63) * mm, "end": v(120, 139.06) * mm});
            skLineSegment(sketch, "E23.5.4.11", {"start": v(110.43, 155.63) * mm, "end": v(129.57, 155.63) * mm});
            skLineSegment(sketch, "E23.5.5.0", {"start": v(110.43, 156.13) * mm, "end": v(129.57, 156.13) * mm});
            skLineSegment(sketch, "E23.5.5.1", {"start": v(120, 172.7) * mm, "end": v(110.43, 156.13) * mm});
            skLineSegment(sketch, "E23.5.5.2", {"start": v(129.57, 156.13) * mm, "end": v(120, 172.7) * mm});
            skLineSegment(sketch, "E23.5.5.3", {"start": v(100.43, 172.96) * mm, "end": v(119.57, 172.96) * mm});
            skLineSegment(sketch, "E23.5.5.4", {"start": v(119.57, 172.96) * mm, "end": v(110, 156.38) * mm});
            skLineSegment(sketch, "E23.5.5.5", {"start": v(110, 156.38) * mm, "end": v(100.43, 172.96) * mm});
            skLineSegment(sketch, "E23.5.5.6", {"start": v(110, 190.03) * mm, "end": v(100.43, 173.46) * mm});
            skLineSegment(sketch, "E23.5.5.7", {"start": v(100.43, 173.46) * mm, "end": v(119.57, 173.46) * mm});
            skLineSegment(sketch, "E23.5.5.8", {"start": v(119.57, 173.46) * mm, "end": v(110, 190.03) * mm});
            skLineSegment(sketch, "E23.5.5.9", {"start": v(120, 173.7) * mm, "end": v(110.43, 190.28) * mm});
            skLineSegment(sketch, "E23.5.5.10", {"start": v(129.57, 190.28) * mm, "end": v(120, 173.7) * mm});
            skLineSegment(sketch, "E23.5.5.11", {"start": v(110.43, 190.28) * mm, "end": v(129.57, 190.28) * mm});
            skLineSegment(sketch, "E23.5.6.0", {"start": v(110.43, 190.78) * mm, "end": v(129.57, 190.78) * mm});
            skLineSegment(sketch, "E23.5.6.1", {"start": v(120, 207.35) * mm, "end": v(110.43, 190.78) * mm});
            skLineSegment(sketch, "E23.5.6.2", {"start": v(129.57, 190.78) * mm, "end": v(120, 207.35) * mm});
            skLineSegment(sketch, "E23.5.6.3", {"start": v(100.43, 207.6) * mm, "end": v(119.57, 207.6) * mm});
            skLineSegment(sketch, "E23.5.6.4", {"start": v(119.57, 207.6) * mm, "end": v(110, 191.03) * mm});
            skLineSegment(sketch, "E23.5.6.5", {"start": v(110, 191.03) * mm, "end": v(100.43, 207.6) * mm});
            skLineSegment(sketch, "E23.5.6.6", {"start": v(110, 224.67) * mm, "end": v(100.43, 208.1) * mm});
            skLineSegment(sketch, "E23.5.6.7", {"start": v(100.43, 208.1) * mm, "end": v(119.57, 208.1) * mm});
            skLineSegment(sketch, "E23.5.6.8", {"start": v(119.57, 208.1) * mm, "end": v(110, 224.67) * mm});
            skLineSegment(sketch, "E23.5.6.9", {"start": v(120, 208.35) * mm, "end": v(110.43, 224.92) * mm});
            skLineSegment(sketch, "E23.5.6.10", {"start": v(129.57, 224.92) * mm, "end": v(120, 208.35) * mm});
            skLineSegment(sketch, "E23.5.6.11", {"start": v(110.43, 224.92) * mm, "end": v(129.57, 224.92) * mm});
            skLineSegment(sketch, "E23.6.0.0", {"start": v(130.43, -17.07) * mm, "end": v(149.57, -17.07) * mm});
            skLineSegment(sketch, "E23.6.0.1", {"start": v(140, -0.5) * mm, "end": v(130.43, -17.07) * mm});
            skLineSegment(sketch, "E23.6.0.2", {"start": v(149.57, -17.07) * mm, "end": v(140, -0.5) * mm});
            skLineSegment(sketch, "E23.6.0.3", {"start": v(120.43, -0.25) * mm, "end": v(139.57, -0.25) * mm});
            skLineSegment(sketch, "E23.6.0.4", {"start": v(139.57, -0.25) * mm, "end": v(130, -16.82) * mm});
            skLineSegment(sketch, "E23.6.0.5", {"start": v(130, -16.82) * mm, "end": v(120.43, -0.25) * mm});
            skLineSegment(sketch, "E23.6.0.6", {"start": v(130, 16.82) * mm, "end": v(120.43, 0.25) * mm});
            skLineSegment(sketch, "E23.6.0.7", {"start": v(120.43, 0.25) * mm, "end": v(139.57, 0.25) * mm});
            skLineSegment(sketch, "E23.6.0.8", {"start": v(139.57, 0.25) * mm, "end": v(130, 16.82) * mm});
            skLineSegment(sketch, "E23.6.0.9", {"start": v(140, 0.5) * mm, "end": v(130.43, 17.07) * mm});
            skLineSegment(sketch, "E23.6.0.10", {"start": v(149.57, 17.07) * mm, "end": v(140, 0.5) * mm});
            skLineSegment(sketch, "E23.6.0.11", {"start": v(130.43, 17.07) * mm, "end": v(149.57, 17.07) * mm});
            skLineSegment(sketch, "E23.6.1.0", {"start": v(130.43, 17.57) * mm, "end": v(149.57, 17.57) * mm});
            skLineSegment(sketch, "E23.6.1.1", {"start": v(140, 34.14) * mm, "end": v(130.43, 17.57) * mm});
            skLineSegment(sketch, "E23.6.1.2", {"start": v(149.57, 17.57) * mm, "end": v(140, 34.14) * mm});
            skLineSegment(sketch, "E23.6.1.3", {"start": v(120.43, 34.4) * mm, "end": v(139.57, 34.4) * mm});
            skLineSegment(sketch, "E23.6.1.4", {"start": v(139.57, 34.4) * mm, "end": v(130, 17.82) * mm});
            skLineSegment(sketch, "E23.6.1.5", {"start": v(130, 17.82) * mm, "end": v(120.43, 34.4) * mm});
            skLineSegment(sketch, "E23.6.1.6", {"start": v(130, 51.46) * mm, "end": v(120.43, 34.9) * mm});
            skLineSegment(sketch, "E23.6.1.7", {"start": v(120.43, 34.9) * mm, "end": v(139.57, 34.9) * mm});
            skLineSegment(sketch, "E23.6.1.8", {"start": v(139.57, 34.9) * mm, "end": v(130, 51.46) * mm});
            skLineSegment(sketch, "E23.6.1.9", {"start": v(140, 35.14) * mm, "end": v(130.43, 51.71) * mm});
            skLineSegment(sketch, "E23.6.1.10", {"start": v(149.57, 51.71) * mm, "end": v(140, 35.14) * mm});
            skLineSegment(sketch, "E23.6.1.11", {"start": v(130.43, 51.71) * mm, "end": v(149.57, 51.71) * mm});
            skLineSegment(sketch, "E23.6.2.0", {"start": v(130.43, 52.21) * mm, "end": v(149.57, 52.21) * mm});
            skLineSegment(sketch, "E23.6.2.1", {"start": v(140, 68.78) * mm, "end": v(130.43, 52.21) * mm});
            skLineSegment(sketch, "E23.6.2.2", {"start": v(149.57, 52.21) * mm, "end": v(140, 68.78) * mm});
            skLineSegment(sketch, "E23.6.2.3", {"start": v(120.43, 69.03) * mm, "end": v(139.57, 69.03) * mm});
            skLineSegment(sketch, "E23.6.2.4", {"start": v(139.57, 69.03) * mm, "end": v(130, 52.46) * mm});
            skLineSegment(sketch, "E23.6.2.5", {"start": v(130, 52.46) * mm, "end": v(120.43, 69.03) * mm});
            skLineSegment(sketch, "E23.6.2.6", {"start": v(130, 86.1) * mm, "end": v(120.43, 69.53) * mm});
            skLineSegment(sketch, "E23.6.2.7", {"start": v(120.43, 69.53) * mm, "end": v(139.57, 69.53) * mm});
            skLineSegment(sketch, "E23.6.2.8", {"start": v(139.57, 69.53) * mm, "end": v(130, 86.1) * mm});
            skLineSegment(sketch, "E23.6.2.9", {"start": v(140, 69.78) * mm, "end": v(130.43, 86.35) * mm});
            skLineSegment(sketch, "E23.6.2.10", {"start": v(149.57, 86.35) * mm, "end": v(140, 69.78) * mm});
            skLineSegment(sketch, "E23.6.2.11", {"start": v(130.43, 86.35) * mm, "end": v(149.57, 86.35) * mm});
            skLineSegment(sketch, "E23.6.3.0", {"start": v(130.43, 86.85) * mm, "end": v(149.57, 86.85) * mm});
            skLineSegment(sketch, "E23.6.3.1", {"start": v(140, 103.42) * mm, "end": v(130.43, 86.85) * mm});
            skLineSegment(sketch, "E23.6.3.2", {"start": v(149.57, 86.85) * mm, "end": v(140, 103.42) * mm});
            skLineSegment(sketch, "E23.6.3.3", {"start": v(120.43, 103.67) * mm, "end": v(139.57, 103.67) * mm});
            skLineSegment(sketch, "E23.6.3.4", {"start": v(139.57, 103.67) * mm, "end": v(130, 87.1) * mm});
            skLineSegment(sketch, "E23.6.3.5", {"start": v(130, 87.1) * mm, "end": v(120.43, 103.67) * mm});
            skLineSegment(sketch, "E23.6.3.6", {"start": v(130, 120.74) * mm, "end": v(120.43, 104.17) * mm});
            skLineSegment(sketch, "E23.6.3.7", {"start": v(120.43, 104.17) * mm, "end": v(139.57, 104.17) * mm});
            skLineSegment(sketch, "E23.6.3.8", {"start": v(139.57, 104.17) * mm, "end": v(130, 120.74) * mm});
            skLineSegment(sketch, "E23.6.3.9", {"start": v(140, 104.42) * mm, "end": v(130.43, 121) * mm});
            skLineSegment(sketch, "E23.6.3.10", {"start": v(149.57, 121) * mm, "end": v(140, 104.42) * mm});
            skLineSegment(sketch, "E23.6.3.11", {"start": v(130.43, 121) * mm, "end": v(149.57, 121) * mm});
            skLineSegment(sketch, "E23.6.4.0", {"start": v(130.43, 121.5) * mm, "end": v(149.57, 121.5) * mm});
            skLineSegment(sketch, "E23.6.4.1", {"start": v(140, 138.06) * mm, "end": v(130.43, 121.5) * mm});
            skLineSegment(sketch, "E23.6.4.2", {"start": v(149.57, 121.5) * mm, "end": v(140, 138.06) * mm});
            skLineSegment(sketch, "E23.6.4.3", {"start": v(120.43, 138.31) * mm, "end": v(139.57, 138.31) * mm});
            skLineSegment(sketch, "E23.6.4.4", {"start": v(139.57, 138.31) * mm, "end": v(130, 121.74) * mm});
            skLineSegment(sketch, "E23.6.4.5", {"start": v(130, 121.74) * mm, "end": v(120.43, 138.31) * mm});
            skLineSegment(sketch, "E23.6.4.6", {"start": v(130, 155.38) * mm, "end": v(120.43, 138.81) * mm});
            skLineSegment(sketch, "E23.6.4.7", {"start": v(120.43, 138.81) * mm, "end": v(139.57, 138.81) * mm});
            skLineSegment(sketch, "E23.6.4.8", {"start": v(139.57, 138.81) * mm, "end": v(130, 155.38) * mm});
            skLineSegment(sketch, "E23.6.4.9", {"start": v(140, 139.06) * mm, "end": v(130.43, 155.63) * mm});
            skLineSegment(sketch, "E23.6.4.10", {"start": v(149.57, 155.63) * mm, "end": v(140, 139.06) * mm});
            skLineSegment(sketch, "E23.6.4.11", {"start": v(130.43, 155.63) * mm, "end": v(149.57, 155.63) * mm});
            skLineSegment(sketch, "E23.6.5.0", {"start": v(130.43, 156.13) * mm, "end": v(149.57, 156.13) * mm});
            skLineSegment(sketch, "E23.6.5.1", {"start": v(140, 172.7) * mm, "end": v(130.43, 156.13) * mm});
            skLineSegment(sketch, "E23.6.5.2", {"start": v(149.57, 156.13) * mm, "end": v(140, 172.7) * mm});
            skLineSegment(sketch, "E23.6.5.3", {"start": v(120.43, 172.96) * mm, "end": v(139.57, 172.96) * mm});
            skLineSegment(sketch, "E23.6.5.4", {"start": v(139.57, 172.96) * mm, "end": v(130, 156.38) * mm});
            skLineSegment(sketch, "E23.6.5.5", {"start": v(130, 156.38) * mm, "end": v(120.43, 172.96) * mm});
            skLineSegment(sketch, "E23.6.5.6", {"start": v(130, 190.03) * mm, "end": v(120.43, 173.46) * mm});
            skLineSegment(sketch, "E23.6.5.7", {"start": v(120.43, 173.46) * mm, "end": v(139.57, 173.46) * mm});
            skLineSegment(sketch, "E23.6.5.8", {"start": v(139.57, 173.46) * mm, "end": v(130, 190.03) * mm});
            skLineSegment(sketch, "E23.6.5.9", {"start": v(140, 173.7) * mm, "end": v(130.43, 190.28) * mm});
            skLineSegment(sketch, "E23.6.5.10", {"start": v(149.57, 190.28) * mm, "end": v(140, 173.7) * mm});
            skLineSegment(sketch, "E23.6.5.11", {"start": v(130.43, 190.28) * mm, "end": v(149.57, 190.28) * mm});
            skLineSegment(sketch, "E23.6.6.0", {"start": v(130.43, 190.78) * mm, "end": v(149.57, 190.78) * mm});
            skLineSegment(sketch, "E23.6.6.1", {"start": v(140, 207.35) * mm, "end": v(130.43, 190.78) * mm});
            skLineSegment(sketch, "E23.6.6.2", {"start": v(149.57, 190.78) * mm, "end": v(140, 207.35) * mm});
            skLineSegment(sketch, "E23.6.6.3", {"start": v(120.43, 207.6) * mm, "end": v(139.57, 207.6) * mm});
            skLineSegment(sketch, "E23.6.6.4", {"start": v(139.57, 207.6) * mm, "end": v(130, 191.03) * mm});
            skLineSegment(sketch, "E23.6.6.5", {"start": v(130, 191.03) * mm, "end": v(120.43, 207.6) * mm});
            skLineSegment(sketch, "E23.6.6.6", {"start": v(130, 224.67) * mm, "end": v(120.43, 208.1) * mm});
            skLineSegment(sketch, "E23.6.6.7", {"start": v(120.43, 208.1) * mm, "end": v(139.57, 208.1) * mm});
            skLineSegment(sketch, "E23.6.6.8", {"start": v(139.57, 208.1) * mm, "end": v(130, 224.67) * mm});
            skLineSegment(sketch, "E23.6.6.9", {"start": v(140, 208.35) * mm, "end": v(130.43, 224.92) * mm});
            skLineSegment(sketch, "E23.6.6.10", {"start": v(149.57, 224.92) * mm, "end": v(140, 208.35) * mm});
            skLineSegment(sketch, "E23.6.6.11", {"start": v(130.43, 224.92) * mm, "end": v(149.57, 224.92) * mm});
            skLineSegment(sketch, "E23.7.0.0", {"start": v(150.43, -17.07) * mm, "end": v(169.57, -17.07) * mm});
            skLineSegment(sketch, "E23.7.0.1", {"start": v(160, -0.5) * mm, "end": v(150.43, -17.07) * mm});
            skLineSegment(sketch, "E23.7.0.2", {"start": v(169.57, -17.07) * mm, "end": v(160, -0.5) * mm});
            skLineSegment(sketch, "E23.7.0.3", {"start": v(140.43, -0.25) * mm, "end": v(159.57, -0.25) * mm});
            skLineSegment(sketch, "E23.7.0.4", {"start": v(159.57, -0.25) * mm, "end": v(150, -16.82) * mm});
            skLineSegment(sketch, "E23.7.0.5", {"start": v(150, -16.82) * mm, "end": v(140.43, -0.25) * mm});
            skLineSegment(sketch, "E23.7.0.6", {"start": v(150, 16.82) * mm, "end": v(140.43, 0.25) * mm});
            skLineSegment(sketch, "E23.7.0.7", {"start": v(140.43, 0.25) * mm, "end": v(159.57, 0.25) * mm});
            skLineSegment(sketch, "E23.7.0.8", {"start": v(159.57, 0.25) * mm, "end": v(150, 16.82) * mm});
            skLineSegment(sketch, "E23.7.0.9", {"start": v(160, 0.5) * mm, "end": v(150.43, 17.07) * mm});
            skLineSegment(sketch, "E23.7.0.10", {"start": v(169.57, 17.07) * mm, "end": v(160, 0.5) * mm});
            skLineSegment(sketch, "E23.7.0.11", {"start": v(150.43, 17.07) * mm, "end": v(169.57, 17.07) * mm});
            skLineSegment(sketch, "E23.7.1.0", {"start": v(150.43, 17.57) * mm, "end": v(169.57, 17.57) * mm});
            skLineSegment(sketch, "E23.7.1.1", {"start": v(160, 34.14) * mm, "end": v(150.43, 17.57) * mm});
            skLineSegment(sketch, "E23.7.1.2", {"start": v(169.57, 17.57) * mm, "end": v(160, 34.14) * mm});
            skLineSegment(sketch, "E23.7.1.3", {"start": v(140.43, 34.4) * mm, "end": v(159.57, 34.4) * mm});
            skLineSegment(sketch, "E23.7.1.4", {"start": v(159.57, 34.4) * mm, "end": v(150, 17.82) * mm});
            skLineSegment(sketch, "E23.7.1.5", {"start": v(150, 17.82) * mm, "end": v(140.43, 34.4) * mm});
            skLineSegment(sketch, "E23.7.1.6", {"start": v(150, 51.46) * mm, "end": v(140.43, 34.9) * mm});
            skLineSegment(sketch, "E23.7.1.7", {"start": v(140.43, 34.9) * mm, "end": v(159.57, 34.9) * mm});
            skLineSegment(sketch, "E23.7.1.8", {"start": v(159.57, 34.9) * mm, "end": v(150, 51.46) * mm});
            skLineSegment(sketch, "E23.7.1.9", {"start": v(160, 35.14) * mm, "end": v(150.43, 51.71) * mm});
            skLineSegment(sketch, "E23.7.1.10", {"start": v(169.57, 51.71) * mm, "end": v(160, 35.14) * mm});
            skLineSegment(sketch, "E23.7.1.11", {"start": v(150.43, 51.71) * mm, "end": v(169.57, 51.71) * mm});
            skLineSegment(sketch, "E23.7.2.0", {"start": v(150.43, 52.21) * mm, "end": v(169.57, 52.21) * mm});
            skLineSegment(sketch, "E23.7.2.1", {"start": v(160, 68.78) * mm, "end": v(150.43, 52.21) * mm});
            skLineSegment(sketch, "E23.7.2.2", {"start": v(169.57, 52.21) * mm, "end": v(160, 68.78) * mm});
            skLineSegment(sketch, "E23.7.2.3", {"start": v(140.43, 69.03) * mm, "end": v(159.57, 69.03) * mm});
            skLineSegment(sketch, "E23.7.2.4", {"start": v(159.57, 69.03) * mm, "end": v(150, 52.46) * mm});
            skLineSegment(sketch, "E23.7.2.5", {"start": v(150, 52.46) * mm, "end": v(140.43, 69.03) * mm});
            skLineSegment(sketch, "E23.7.2.6", {"start": v(150, 86.1) * mm, "end": v(140.43, 69.53) * mm});
            skLineSegment(sketch, "E23.7.2.7", {"start": v(140.43, 69.53) * mm, "end": v(159.57, 69.53) * mm});
            skLineSegment(sketch, "E23.7.2.8", {"start": v(159.57, 69.53) * mm, "end": v(150, 86.1) * mm});
            skLineSegment(sketch, "E23.7.2.9", {"start": v(160, 69.78) * mm, "end": v(150.43, 86.35) * mm});
            skLineSegment(sketch, "E23.7.2.10", {"start": v(169.57, 86.35) * mm, "end": v(160, 69.78) * mm});
            skLineSegment(sketch, "E23.7.2.11", {"start": v(150.43, 86.35) * mm, "end": v(169.57, 86.35) * mm});
            skLineSegment(sketch, "E23.7.3.0", {"start": v(150.43, 86.85) * mm, "end": v(169.57, 86.85) * mm});
            skLineSegment(sketch, "E23.7.3.1", {"start": v(160, 103.42) * mm, "end": v(150.43, 86.85) * mm});
            skLineSegment(sketch, "E23.7.3.2", {"start": v(169.57, 86.85) * mm, "end": v(160, 103.42) * mm});
            skLineSegment(sketch, "E23.7.3.3", {"start": v(140.43, 103.67) * mm, "end": v(159.57, 103.67) * mm});
            skLineSegment(sketch, "E23.7.3.4", {"start": v(159.57, 103.67) * mm, "end": v(150, 87.1) * mm});
            skLineSegment(sketch, "E23.7.3.5", {"start": v(150, 87.1) * mm, "end": v(140.43, 103.67) * mm});
            skLineSegment(sketch, "E23.7.3.6", {"start": v(150, 120.74) * mm, "end": v(140.43, 104.17) * mm});
            skLineSegment(sketch, "E23.7.3.7", {"start": v(140.43, 104.17) * mm, "end": v(159.57, 104.17) * mm});
            skLineSegment(sketch, "E23.7.3.8", {"start": v(159.57, 104.17) * mm, "end": v(150, 120.74) * mm});
            skLineSegment(sketch, "E23.7.3.9", {"start": v(160, 104.42) * mm, "end": v(150.43, 121) * mm});
            skLineSegment(sketch, "E23.7.3.10", {"start": v(169.57, 121) * mm, "end": v(160, 104.42) * mm});
            skLineSegment(sketch, "E23.7.3.11", {"start": v(150.43, 121) * mm, "end": v(169.57, 121) * mm});
            skLineSegment(sketch, "E23.7.4.0", {"start": v(150.43, 121.5) * mm, "end": v(169.57, 121.5) * mm});
            skLineSegment(sketch, "E23.7.4.1", {"start": v(160, 138.06) * mm, "end": v(150.43, 121.5) * mm});
            skLineSegment(sketch, "E23.7.4.2", {"start": v(169.57, 121.5) * mm, "end": v(160, 138.06) * mm});
            skLineSegment(sketch, "E23.7.4.3", {"start": v(140.43, 138.31) * mm, "end": v(159.57, 138.31) * mm});
            skLineSegment(sketch, "E23.7.4.4", {"start": v(159.57, 138.31) * mm, "end": v(150, 121.74) * mm});
            skLineSegment(sketch, "E23.7.4.5", {"start": v(150, 121.74) * mm, "end": v(140.43, 138.31) * mm});
            skLineSegment(sketch, "E23.7.4.6", {"start": v(150, 155.38) * mm, "end": v(140.43, 138.81) * mm});
            skLineSegment(sketch, "E23.7.4.7", {"start": v(140.43, 138.81) * mm, "end": v(159.57, 138.81) * mm});
            skLineSegment(sketch, "E23.7.4.8", {"start": v(159.57, 138.81) * mm, "end": v(150, 155.38) * mm});
            skLineSegment(sketch, "E23.7.4.9", {"start": v(160, 139.06) * mm, "end": v(150.43, 155.63) * mm});
            skLineSegment(sketch, "E23.7.4.10", {"start": v(169.57, 155.63) * mm, "end": v(160, 139.06) * mm});
            skLineSegment(sketch, "E23.7.4.11", {"start": v(150.43, 155.63) * mm, "end": v(169.57, 155.63) * mm});
            skLineSegment(sketch, "E23.7.5.0", {"start": v(150.43, 156.13) * mm, "end": v(169.57, 156.13) * mm});
            skLineSegment(sketch, "E23.7.5.1", {"start": v(160, 172.7) * mm, "end": v(150.43, 156.13) * mm});
            skLineSegment(sketch, "E23.7.5.2", {"start": v(169.57, 156.13) * mm, "end": v(160, 172.7) * mm});
            skLineSegment(sketch, "E23.7.5.3", {"start": v(140.43, 172.96) * mm, "end": v(159.57, 172.96) * mm});
            skLineSegment(sketch, "E23.7.5.4", {"start": v(159.57, 172.96) * mm, "end": v(150, 156.38) * mm});
            skLineSegment(sketch, "E23.7.5.5", {"start": v(150, 156.38) * mm, "end": v(140.43, 172.96) * mm});
            skLineSegment(sketch, "E23.7.5.6", {"start": v(150, 190.03) * mm, "end": v(140.43, 173.46) * mm});
            skLineSegment(sketch, "E23.7.5.7", {"start": v(140.43, 173.46) * mm, "end": v(159.57, 173.46) * mm});
            skLineSegment(sketch, "E23.7.5.8", {"start": v(159.57, 173.46) * mm, "end": v(150, 190.03) * mm});
            skLineSegment(sketch, "E23.7.5.9", {"start": v(160, 173.7) * mm, "end": v(150.43, 190.28) * mm});
            skLineSegment(sketch, "E23.7.5.10", {"start": v(169.57, 190.28) * mm, "end": v(160, 173.7) * mm});
            skLineSegment(sketch, "E23.7.5.11", {"start": v(150.43, 190.28) * mm, "end": v(169.57, 190.28) * mm});
            skLineSegment(sketch, "E23.7.6.0", {"start": v(150.43, 190.78) * mm, "end": v(169.57, 190.78) * mm});
            skLineSegment(sketch, "E23.7.6.1", {"start": v(160, 207.35) * mm, "end": v(150.43, 190.78) * mm});
            skLineSegment(sketch, "E23.7.6.2", {"start": v(169.57, 190.78) * mm, "end": v(160, 207.35) * mm});
            skLineSegment(sketch, "E23.7.6.3", {"start": v(140.43, 207.6) * mm, "end": v(159.57, 207.6) * mm});
            skLineSegment(sketch, "E23.7.6.4", {"start": v(159.57, 207.6) * mm, "end": v(150, 191.03) * mm});
            skLineSegment(sketch, "E23.7.6.5", {"start": v(150, 191.03) * mm, "end": v(140.43, 207.6) * mm});
            skLineSegment(sketch, "E23.7.6.6", {"start": v(150, 224.67) * mm, "end": v(140.43, 208.1) * mm});
            skLineSegment(sketch, "E23.7.6.7", {"start": v(140.43, 208.1) * mm, "end": v(159.57, 208.1) * mm});
            skLineSegment(sketch, "E23.7.6.8", {"start": v(159.57, 208.1) * mm, "end": v(150, 224.67) * mm});
            skLineSegment(sketch, "E23.7.6.9", {"start": v(160, 208.35) * mm, "end": v(150.43, 224.92) * mm});
            skLineSegment(sketch, "E23.7.6.10", {"start": v(169.57, 224.92) * mm, "end": v(160, 208.35) * mm});
            skLineSegment(sketch, "E23.7.6.11", {"start": v(150.43, 224.92) * mm, "end": v(169.57, 224.92) * mm});
            skLineSegment(sketch, "E23.8.0.0", {"start": v(170.43, -17.07) * mm, "end": v(189.57, -17.07) * mm});
            skLineSegment(sketch, "E23.8.0.1", {"start": v(180, -0.5) * mm, "end": v(170.43, -17.07) * mm});
            skLineSegment(sketch, "E23.8.0.2", {"start": v(189.57, -17.07) * mm, "end": v(180, -0.5) * mm});
            skLineSegment(sketch, "E23.8.0.3", {"start": v(160.43, -0.25) * mm, "end": v(179.57, -0.25) * mm});
            skLineSegment(sketch, "E23.8.0.4", {"start": v(179.57, -0.25) * mm, "end": v(170, -16.82) * mm});
            skLineSegment(sketch, "E23.8.0.5", {"start": v(170, -16.82) * mm, "end": v(160.43, -0.25) * mm});
            skLineSegment(sketch, "E23.8.0.6", {"start": v(170, 16.82) * mm, "end": v(160.43, 0.25) * mm});
            skLineSegment(sketch, "E23.8.0.7", {"start": v(160.43, 0.25) * mm, "end": v(179.57, 0.25) * mm});
            skLineSegment(sketch, "E23.8.0.8", {"start": v(179.57, 0.25) * mm, "end": v(170, 16.82) * mm});
            skLineSegment(sketch, "E23.8.0.9", {"start": v(180, 0.5) * mm, "end": v(170.43, 17.07) * mm});
            skLineSegment(sketch, "E23.8.0.10", {"start": v(189.57, 17.07) * mm, "end": v(180, 0.5) * mm});
            skLineSegment(sketch, "E23.8.0.11", {"start": v(170.43, 17.07) * mm, "end": v(189.57, 17.07) * mm});
            skLineSegment(sketch, "E23.8.1.0", {"start": v(170.43, 17.57) * mm, "end": v(189.57, 17.57) * mm});
            skLineSegment(sketch, "E23.8.1.1", {"start": v(180, 34.14) * mm, "end": v(170.43, 17.57) * mm});
            skLineSegment(sketch, "E23.8.1.2", {"start": v(189.57, 17.57) * mm, "end": v(180, 34.14) * mm});
            skLineSegment(sketch, "E23.8.1.3", {"start": v(160.43, 34.4) * mm, "end": v(179.57, 34.4) * mm});
            skLineSegment(sketch, "E23.8.1.4", {"start": v(179.57, 34.4) * mm, "end": v(170, 17.82) * mm});
            skLineSegment(sketch, "E23.8.1.5", {"start": v(170, 17.82) * mm, "end": v(160.43, 34.4) * mm});
            skLineSegment(sketch, "E23.8.1.6", {"start": v(170, 51.46) * mm, "end": v(160.43, 34.9) * mm});
            skLineSegment(sketch, "E23.8.1.7", {"start": v(160.43, 34.9) * mm, "end": v(179.57, 34.9) * mm});
            skLineSegment(sketch, "E23.8.1.8", {"start": v(179.57, 34.9) * mm, "end": v(170, 51.46) * mm});
            skLineSegment(sketch, "E23.8.1.9", {"start": v(180, 35.14) * mm, "end": v(170.43, 51.71) * mm});
            skLineSegment(sketch, "E23.8.1.10", {"start": v(189.57, 51.71) * mm, "end": v(180, 35.14) * mm});
            skLineSegment(sketch, "E23.8.1.11", {"start": v(170.43, 51.71) * mm, "end": v(189.57, 51.71) * mm});
            skLineSegment(sketch, "E23.8.2.0", {"start": v(170.43, 52.21) * mm, "end": v(189.57, 52.21) * mm});
            skLineSegment(sketch, "E23.8.2.1", {"start": v(180, 68.78) * mm, "end": v(170.43, 52.21) * mm});
            skLineSegment(sketch, "E23.8.2.2", {"start": v(189.57, 52.21) * mm, "end": v(180, 68.78) * mm});
            skLineSegment(sketch, "E23.8.2.3", {"start": v(160.43, 69.03) * mm, "end": v(179.57, 69.03) * mm});
            skLineSegment(sketch, "E23.8.2.4", {"start": v(179.57, 69.03) * mm, "end": v(170, 52.46) * mm});
            skLineSegment(sketch, "E23.8.2.5", {"start": v(170, 52.46) * mm, "end": v(160.43, 69.03) * mm});
            skLineSegment(sketch, "E23.8.2.6", {"start": v(170, 86.1) * mm, "end": v(160.43, 69.53) * mm});
            skLineSegment(sketch, "E23.8.2.7", {"start": v(160.43, 69.53) * mm, "end": v(179.57, 69.53) * mm});
            skLineSegment(sketch, "E23.8.2.8", {"start": v(179.57, 69.53) * mm, "end": v(170, 86.1) * mm});
            skLineSegment(sketch, "E23.8.2.9", {"start": v(180, 69.78) * mm, "end": v(170.43, 86.35) * mm});
            skLineSegment(sketch, "E23.8.2.10", {"start": v(189.57, 86.35) * mm, "end": v(180, 69.78) * mm});
            skLineSegment(sketch, "E23.8.2.11", {"start": v(170.43, 86.35) * mm, "end": v(189.57, 86.35) * mm});
            skLineSegment(sketch, "E23.8.3.0", {"start": v(170.43, 86.85) * mm, "end": v(189.57, 86.85) * mm});
            skLineSegment(sketch, "E23.8.3.1", {"start": v(180, 103.42) * mm, "end": v(170.43, 86.85) * mm});
            skLineSegment(sketch, "E23.8.3.2", {"start": v(189.57, 86.85) * mm, "end": v(180, 103.42) * mm});
            skLineSegment(sketch, "E23.8.3.3", {"start": v(160.43, 103.67) * mm, "end": v(179.57, 103.67) * mm});
            skLineSegment(sketch, "E23.8.3.4", {"start": v(179.57, 103.67) * mm, "end": v(170, 87.1) * mm});
            skLineSegment(sketch, "E23.8.3.5", {"start": v(170, 87.1) * mm, "end": v(160.43, 103.67) * mm});
            skLineSegment(sketch, "E23.8.3.6", {"start": v(170, 120.74) * mm, "end": v(160.43, 104.17) * mm});
            skLineSegment(sketch, "E23.8.3.7", {"start": v(160.43, 104.17) * mm, "end": v(179.57, 104.17) * mm});
            skLineSegment(sketch, "E23.8.3.8", {"start": v(179.57, 104.17) * mm, "end": v(170, 120.74) * mm});
            skLineSegment(sketch, "E23.8.3.9", {"start": v(180, 104.42) * mm, "end": v(170.43, 121) * mm});
            skLineSegment(sketch, "E23.8.3.10", {"start": v(189.57, 121) * mm, "end": v(180, 104.42) * mm});
            skLineSegment(sketch, "E23.8.3.11", {"start": v(170.43, 121) * mm, "end": v(189.57, 121) * mm});
            skLineSegment(sketch, "E23.8.4.0", {"start": v(170.43, 121.5) * mm, "end": v(189.57, 121.5) * mm});
            skLineSegment(sketch, "E23.8.4.1", {"start": v(180, 138.06) * mm, "end": v(170.43, 121.5) * mm});
            skLineSegment(sketch, "E23.8.4.2", {"start": v(189.57, 121.5) * mm, "end": v(180, 138.06) * mm});
            skLineSegment(sketch, "E23.8.4.3", {"start": v(160.43, 138.31) * mm, "end": v(179.57, 138.31) * mm});
            skLineSegment(sketch, "E23.8.4.4", {"start": v(179.57, 138.31) * mm, "end": v(170, 121.74) * mm});
            skLineSegment(sketch, "E23.8.4.5", {"start": v(170, 121.74) * mm, "end": v(160.43, 138.31) * mm});
            skLineSegment(sketch, "E23.8.4.6", {"start": v(170, 155.38) * mm, "end": v(160.43, 138.81) * mm});
            skLineSegment(sketch, "E23.8.4.7", {"start": v(160.43, 138.81) * mm, "end": v(179.57, 138.81) * mm});
            skLineSegment(sketch, "E23.8.4.8", {"start": v(179.57, 138.81) * mm, "end": v(170, 155.38) * mm});
            skLineSegment(sketch, "E23.8.4.9", {"start": v(180, 139.06) * mm, "end": v(170.43, 155.63) * mm});
            skLineSegment(sketch, "E23.8.4.10", {"start": v(189.57, 155.63) * mm, "end": v(180, 139.06) * mm});
            skLineSegment(sketch, "E23.8.4.11", {"start": v(170.43, 155.63) * mm, "end": v(189.57, 155.63) * mm});
            skLineSegment(sketch, "E23.8.5.0", {"start": v(170.43, 156.13) * mm, "end": v(189.57, 156.13) * mm});
            skLineSegment(sketch, "E23.8.5.1", {"start": v(180, 172.7) * mm, "end": v(170.43, 156.13) * mm});
            skLineSegment(sketch, "E23.8.5.2", {"start": v(189.57, 156.13) * mm, "end": v(180, 172.7) * mm});
            skLineSegment(sketch, "E23.8.5.3", {"start": v(160.43, 172.96) * mm, "end": v(179.57, 172.96) * mm});
            skLineSegment(sketch, "E23.8.5.4", {"start": v(179.57, 172.96) * mm, "end": v(170, 156.38) * mm});
            skLineSegment(sketch, "E23.8.5.5", {"start": v(170, 156.38) * mm, "end": v(160.43, 172.96) * mm});
            skLineSegment(sketch, "E23.8.5.6", {"start": v(170, 190.03) * mm, "end": v(160.43, 173.46) * mm});
            skLineSegment(sketch, "E23.8.5.7", {"start": v(160.43, 173.46) * mm, "end": v(179.57, 173.46) * mm});
            skLineSegment(sketch, "E23.8.5.8", {"start": v(179.57, 173.46) * mm, "end": v(170, 190.03) * mm});
            skLineSegment(sketch, "E23.8.5.9", {"start": v(180, 173.7) * mm, "end": v(170.43, 190.28) * mm});
            skLineSegment(sketch, "E23.8.5.10", {"start": v(189.57, 190.28) * mm, "end": v(180, 173.7) * mm});
            skLineSegment(sketch, "E23.8.5.11", {"start": v(170.43, 190.28) * mm, "end": v(189.57, 190.28) * mm});
            skLineSegment(sketch, "E23.8.6.0", {"start": v(170.43, 190.78) * mm, "end": v(189.57, 190.78) * mm});
            skLineSegment(sketch, "E23.8.6.1", {"start": v(180, 207.35) * mm, "end": v(170.43, 190.78) * mm});
            skLineSegment(sketch, "E23.8.6.2", {"start": v(189.57, 190.78) * mm, "end": v(180, 207.35) * mm});
            skLineSegment(sketch, "E23.8.6.3", {"start": v(160.43, 207.6) * mm, "end": v(179.57, 207.6) * mm});
            skLineSegment(sketch, "E23.8.6.4", {"start": v(179.57, 207.6) * mm, "end": v(170, 191.03) * mm});
            skLineSegment(sketch, "E23.8.6.5", {"start": v(170, 191.03) * mm, "end": v(160.43, 207.6) * mm});
            skLineSegment(sketch, "E23.8.6.6", {"start": v(170, 224.67) * mm, "end": v(160.43, 208.1) * mm});
            skLineSegment(sketch, "E23.8.6.7", {"start": v(160.43, 208.1) * mm, "end": v(179.57, 208.1) * mm});
            skLineSegment(sketch, "E23.8.6.8", {"start": v(179.57, 208.1) * mm, "end": v(170, 224.67) * mm});
            skLineSegment(sketch, "E23.8.6.9", {"start": v(180, 208.35) * mm, "end": v(170.43, 224.92) * mm});
            skLineSegment(sketch, "E23.8.6.10", {"start": v(189.57, 224.92) * mm, "end": v(180, 208.35) * mm});
            skLineSegment(sketch, "E23.8.6.11", {"start": v(170.43, 224.92) * mm, "end": v(189.57, 224.92) * mm});
            skLineSegment(sketch, "E23.9.0.0", {"start": v(190.43, -17.07) * mm, "end": v(209.57, -17.07) * mm});
            skLineSegment(sketch, "E23.9.0.1", {"start": v(200, -0.5) * mm, "end": v(190.43, -17.07) * mm});
            skLineSegment(sketch, "E23.9.0.2", {"start": v(209.57, -17.07) * mm, "end": v(200, -0.5) * mm});
            skLineSegment(sketch, "E23.9.0.3", {"start": v(180.43, -0.25) * mm, "end": v(199.57, -0.25) * mm});
            skLineSegment(sketch, "E23.9.0.4", {"start": v(199.57, -0.25) * mm, "end": v(190, -16.82) * mm});
            skLineSegment(sketch, "E23.9.0.5", {"start": v(190, -16.82) * mm, "end": v(180.43, -0.25) * mm});
            skLineSegment(sketch, "E23.9.0.6", {"start": v(190, 16.82) * mm, "end": v(180.43, 0.25) * mm});
            skLineSegment(sketch, "E23.9.0.7", {"start": v(180.43, 0.25) * mm, "end": v(199.57, 0.25) * mm});
            skLineSegment(sketch, "E23.9.0.8", {"start": v(199.57, 0.25) * mm, "end": v(190, 16.82) * mm});
            skLineSegment(sketch, "E23.9.0.9", {"start": v(200, 0.5) * mm, "end": v(190.43, 17.07) * mm});
            skLineSegment(sketch, "E23.9.0.10", {"start": v(209.57, 17.07) * mm, "end": v(200, 0.5) * mm});
            skLineSegment(sketch, "E23.9.0.11", {"start": v(190.43, 17.07) * mm, "end": v(209.57, 17.07) * mm});
            skLineSegment(sketch, "E23.9.1.0", {"start": v(190.43, 17.57) * mm, "end": v(209.57, 17.57) * mm});
            skLineSegment(sketch, "E23.9.1.1", {"start": v(200, 34.14) * mm, "end": v(190.43, 17.57) * mm});
            skLineSegment(sketch, "E23.9.1.2", {"start": v(209.57, 17.57) * mm, "end": v(200, 34.14) * mm});
            skLineSegment(sketch, "E23.9.1.3", {"start": v(180.43, 34.4) * mm, "end": v(199.57, 34.4) * mm});
            skLineSegment(sketch, "E23.9.1.4", {"start": v(199.57, 34.4) * mm, "end": v(190, 17.82) * mm});
            skLineSegment(sketch, "E23.9.1.5", {"start": v(190, 17.82) * mm, "end": v(180.43, 34.4) * mm});
            skLineSegment(sketch, "E23.9.1.6", {"start": v(190, 51.46) * mm, "end": v(180.43, 34.9) * mm});
            skLineSegment(sketch, "E23.9.1.7", {"start": v(180.43, 34.9) * mm, "end": v(199.57, 34.9) * mm});
            skLineSegment(sketch, "E23.9.1.8", {"start": v(199.57, 34.9) * mm, "end": v(190, 51.46) * mm});
            skLineSegment(sketch, "E23.9.1.9", {"start": v(200, 35.14) * mm, "end": v(190.43, 51.71) * mm});
            skLineSegment(sketch, "E23.9.1.10", {"start": v(209.57, 51.71) * mm, "end": v(200, 35.14) * mm});
            skLineSegment(sketch, "E23.9.1.11", {"start": v(190.43, 51.71) * mm, "end": v(209.57, 51.71) * mm});
            skLineSegment(sketch, "E23.9.2.0", {"start": v(190.43, 52.21) * mm, "end": v(209.57, 52.21) * mm});
            skLineSegment(sketch, "E23.9.2.1", {"start": v(200, 68.78) * mm, "end": v(190.43, 52.21) * mm});
            skLineSegment(sketch, "E23.9.2.2", {"start": v(209.57, 52.21) * mm, "end": v(200, 68.78) * mm});
            skLineSegment(sketch, "E23.9.2.3", {"start": v(180.43, 69.03) * mm, "end": v(199.57, 69.03) * mm});
            skLineSegment(sketch, "E23.9.2.4", {"start": v(199.57, 69.03) * mm, "end": v(190, 52.46) * mm});
            skLineSegment(sketch, "E23.9.2.5", {"start": v(190, 52.46) * mm, "end": v(180.43, 69.03) * mm});
            skLineSegment(sketch, "E23.9.2.6", {"start": v(190, 86.1) * mm, "end": v(180.43, 69.53) * mm});
            skLineSegment(sketch, "E23.9.2.7", {"start": v(180.43, 69.53) * mm, "end": v(199.57, 69.53) * mm});
            skLineSegment(sketch, "E23.9.2.8", {"start": v(199.57, 69.53) * mm, "end": v(190, 86.1) * mm});
            skLineSegment(sketch, "E23.9.2.9", {"start": v(200, 69.78) * mm, "end": v(190.43, 86.35) * mm});
            skLineSegment(sketch, "E23.9.2.10", {"start": v(209.57, 86.35) * mm, "end": v(200, 69.78) * mm});
            skLineSegment(sketch, "E23.9.2.11", {"start": v(190.43, 86.35) * mm, "end": v(209.57, 86.35) * mm});
            skLineSegment(sketch, "E23.9.3.0", {"start": v(190.43, 86.85) * mm, "end": v(209.57, 86.85) * mm});
            skLineSegment(sketch, "E23.9.3.1", {"start": v(200, 103.42) * mm, "end": v(190.43, 86.85) * mm});
            skLineSegment(sketch, "E23.9.3.2", {"start": v(209.57, 86.85) * mm, "end": v(200, 103.42) * mm});
            skLineSegment(sketch, "E23.9.3.3", {"start": v(180.43, 103.67) * mm, "end": v(199.57, 103.67) * mm});
            skLineSegment(sketch, "E23.9.3.4", {"start": v(199.57, 103.67) * mm, "end": v(190, 87.1) * mm});
            skLineSegment(sketch, "E23.9.3.5", {"start": v(190, 87.1) * mm, "end": v(180.43, 103.67) * mm});
            skLineSegment(sketch, "E23.9.3.6", {"start": v(190, 120.74) * mm, "end": v(180.43, 104.17) * mm});
            skLineSegment(sketch, "E23.9.3.7", {"start": v(180.43, 104.17) * mm, "end": v(199.57, 104.17) * mm});
            skLineSegment(sketch, "E23.9.3.8", {"start": v(199.57, 104.17) * mm, "end": v(190, 120.74) * mm});
            skLineSegment(sketch, "E23.9.3.9", {"start": v(200, 104.42) * mm, "end": v(190.43, 121) * mm});
            skLineSegment(sketch, "E23.9.3.10", {"start": v(209.57, 121) * mm, "end": v(200, 104.42) * mm});
            skLineSegment(sketch, "E23.9.3.11", {"start": v(190.43, 121) * mm, "end": v(209.57, 121) * mm});
            skLineSegment(sketch, "E23.9.4.0", {"start": v(190.43, 121.5) * mm, "end": v(209.57, 121.5) * mm});
            skLineSegment(sketch, "E23.9.4.1", {"start": v(200, 138.06) * mm, "end": v(190.43, 121.5) * mm});
            skLineSegment(sketch, "E23.9.4.2", {"start": v(209.57, 121.5) * mm, "end": v(200, 138.06) * mm});
            skLineSegment(sketch, "E23.9.4.3", {"start": v(180.43, 138.31) * mm, "end": v(199.57, 138.31) * mm});
            skLineSegment(sketch, "E23.9.4.4", {"start": v(199.57, 138.31) * mm, "end": v(190, 121.74) * mm});
            skLineSegment(sketch, "E23.9.4.5", {"start": v(190, 121.74) * mm, "end": v(180.43, 138.31) * mm});
            skLineSegment(sketch, "E23.9.4.6", {"start": v(190, 155.38) * mm, "end": v(180.43, 138.81) * mm});
            skLineSegment(sketch, "E23.9.4.7", {"start": v(180.43, 138.81) * mm, "end": v(199.57, 138.81) * mm});
            skLineSegment(sketch, "E23.9.4.8", {"start": v(199.57, 138.81) * mm, "end": v(190, 155.38) * mm});
            skLineSegment(sketch, "E23.9.4.9", {"start": v(200, 139.06) * mm, "end": v(190.43, 155.63) * mm});
            skLineSegment(sketch, "E23.9.4.10", {"start": v(209.57, 155.63) * mm, "end": v(200, 139.06) * mm});
            skLineSegment(sketch, "E23.9.4.11", {"start": v(190.43, 155.63) * mm, "end": v(209.57, 155.63) * mm});
            skLineSegment(sketch, "E23.9.5.0", {"start": v(190.43, 156.13) * mm, "end": v(209.57, 156.13) * mm});
            skLineSegment(sketch, "E23.9.5.1", {"start": v(200, 172.7) * mm, "end": v(190.43, 156.13) * mm});
            skLineSegment(sketch, "E23.9.5.2", {"start": v(209.57, 156.13) * mm, "end": v(200, 172.7) * mm});
            skLineSegment(sketch, "E23.9.5.3", {"start": v(180.43, 172.96) * mm, "end": v(199.57, 172.96) * mm});
            skLineSegment(sketch, "E23.9.5.4", {"start": v(199.57, 172.96) * mm, "end": v(190, 156.38) * mm});
            skLineSegment(sketch, "E23.9.5.5", {"start": v(190, 156.38) * mm, "end": v(180.43, 172.96) * mm});
            skLineSegment(sketch, "E23.9.5.6", {"start": v(190, 190.03) * mm, "end": v(180.43, 173.46) * mm});
            skLineSegment(sketch, "E23.9.5.7", {"start": v(180.43, 173.46) * mm, "end": v(199.57, 173.46) * mm});
            skLineSegment(sketch, "E23.9.5.8", {"start": v(199.57, 173.46) * mm, "end": v(190, 190.03) * mm});
            skLineSegment(sketch, "E23.9.5.9", {"start": v(200, 173.7) * mm, "end": v(190.43, 190.28) * mm});
            skLineSegment(sketch, "E23.9.5.10", {"start": v(209.57, 190.28) * mm, "end": v(200, 173.7) * mm});
            skLineSegment(sketch, "E23.9.5.11", {"start": v(190.43, 190.28) * mm, "end": v(209.57, 190.28) * mm});
            skLineSegment(sketch, "E23.9.6.0", {"start": v(190.43, 190.78) * mm, "end": v(209.57, 190.78) * mm});
            skLineSegment(sketch, "E23.9.6.1", {"start": v(200, 207.35) * mm, "end": v(190.43, 190.78) * mm});
            skLineSegment(sketch, "E23.9.6.2", {"start": v(209.57, 190.78) * mm, "end": v(200, 207.35) * mm});
            skLineSegment(sketch, "E23.9.6.3", {"start": v(180.43, 207.6) * mm, "end": v(199.57, 207.6) * mm});
            skLineSegment(sketch, "E23.9.6.4", {"start": v(199.57, 207.6) * mm, "end": v(190, 191.03) * mm});
            skLineSegment(sketch, "E23.9.6.5", {"start": v(190, 191.03) * mm, "end": v(180.43, 207.6) * mm});
            skLineSegment(sketch, "E23.9.6.6", {"start": v(190, 224.67) * mm, "end": v(180.43, 208.1) * mm});
            skLineSegment(sketch, "E23.9.6.7", {"start": v(180.43, 208.1) * mm, "end": v(199.57, 208.1) * mm});
            skLineSegment(sketch, "E23.9.6.8", {"start": v(199.57, 208.1) * mm, "end": v(190, 224.67) * mm});
            skLineSegment(sketch, "E23.9.6.9", {"start": v(200, 208.35) * mm, "end": v(190.43, 224.92) * mm});
            skLineSegment(sketch, "E23.9.6.10", {"start": v(209.57, 224.92) * mm, "end": v(200, 208.35) * mm});
            skLineSegment(sketch, "E23.9.6.11", {"start": v(190.43, 224.92) * mm, "end": v(209.57, 224.92) * mm});
            skLineSegment(sketch, "E23.10.0.0", {"start": v(210.43, -17.07) * mm, "end": v(229.57, -17.07) * mm});
            skLineSegment(sketch, "E23.10.0.1", {"start": v(220, -0.5) * mm, "end": v(210.43, -17.07) * mm});
            skLineSegment(sketch, "E23.10.0.2", {"start": v(229.57, -17.07) * mm, "end": v(220, -0.5) * mm});
            skLineSegment(sketch, "E23.10.0.3", {"start": v(200.43, -0.25) * mm, "end": v(219.57, -0.25) * mm});
            skLineSegment(sketch, "E23.10.0.4", {"start": v(219.57, -0.25) * mm, "end": v(210, -16.82) * mm});
            skLineSegment(sketch, "E23.10.0.5", {"start": v(210, -16.82) * mm, "end": v(200.43, -0.25) * mm});
            skLineSegment(sketch, "E23.10.0.6", {"start": v(210, 16.82) * mm, "end": v(200.43, 0.25) * mm});
            skLineSegment(sketch, "E23.10.0.7", {"start": v(200.43, 0.25) * mm, "end": v(219.57, 0.25) * mm});
            skLineSegment(sketch, "E23.10.0.8", {"start": v(219.57, 0.25) * mm, "end": v(210, 16.82) * mm});
            skLineSegment(sketch, "E23.10.0.9", {"start": v(220, 0.5) * mm, "end": v(210.43, 17.07) * mm});
            skLineSegment(sketch, "E23.10.0.10", {"start": v(229.57, 17.07) * mm, "end": v(220, 0.5) * mm});
            skLineSegment(sketch, "E23.10.0.11", {"start": v(210.43, 17.07) * mm, "end": v(229.57, 17.07) * mm});
            skLineSegment(sketch, "E23.10.1.0", {"start": v(210.43, 17.57) * mm, "end": v(229.57, 17.57) * mm});
            skLineSegment(sketch, "E23.10.1.1", {"start": v(220, 34.14) * mm, "end": v(210.43, 17.57) * mm});
            skLineSegment(sketch, "E23.10.1.2", {"start": v(229.57, 17.57) * mm, "end": v(220, 34.14) * mm});
            skLineSegment(sketch, "E23.10.1.3", {"start": v(200.43, 34.4) * mm, "end": v(219.57, 34.4) * mm});
            skLineSegment(sketch, "E23.10.1.4", {"start": v(219.57, 34.4) * mm, "end": v(210, 17.82) * mm});
            skLineSegment(sketch, "E23.10.1.5", {"start": v(210, 17.82) * mm, "end": v(200.43, 34.4) * mm});
            skLineSegment(sketch, "E23.10.1.6", {"start": v(210, 51.46) * mm, "end": v(200.43, 34.9) * mm});
            skLineSegment(sketch, "E23.10.1.7", {"start": v(200.43, 34.9) * mm, "end": v(219.57, 34.9) * mm});
            skLineSegment(sketch, "E23.10.1.8", {"start": v(219.57, 34.9) * mm, "end": v(210, 51.46) * mm});
            skLineSegment(sketch, "E23.10.1.9", {"start": v(220, 35.14) * mm, "end": v(210.43, 51.71) * mm});
            skLineSegment(sketch, "E23.10.1.10", {"start": v(229.57, 51.71) * mm, "end": v(220, 35.14) * mm});
            skLineSegment(sketch, "E23.10.1.11", {"start": v(210.43, 51.71) * mm, "end": v(229.57, 51.71) * mm});
            skLineSegment(sketch, "E23.10.2.0", {"start": v(210.43, 52.21) * mm, "end": v(229.57, 52.21) * mm});
            skLineSegment(sketch, "E23.10.2.1", {"start": v(220, 68.78) * mm, "end": v(210.43, 52.21) * mm});
            skLineSegment(sketch, "E23.10.2.2", {"start": v(229.57, 52.21) * mm, "end": v(220, 68.78) * mm});
            skLineSegment(sketch, "E23.10.2.3", {"start": v(200.43, 69.03) * mm, "end": v(219.57, 69.03) * mm});
            skLineSegment(sketch, "E23.10.2.4", {"start": v(219.57, 69.03) * mm, "end": v(210, 52.46) * mm});
            skLineSegment(sketch, "E23.10.2.5", {"start": v(210, 52.46) * mm, "end": v(200.43, 69.03) * mm});
            skLineSegment(sketch, "E23.10.2.6", {"start": v(210, 86.1) * mm, "end": v(200.43, 69.53) * mm});
            skLineSegment(sketch, "E23.10.2.7", {"start": v(200.43, 69.53) * mm, "end": v(219.57, 69.53) * mm});
            skLineSegment(sketch, "E23.10.2.8", {"start": v(219.57, 69.53) * mm, "end": v(210, 86.1) * mm});
            skLineSegment(sketch, "E23.10.2.9", {"start": v(220, 69.78) * mm, "end": v(210.43, 86.35) * mm});
            skLineSegment(sketch, "E23.10.2.10", {"start": v(229.57, 86.35) * mm, "end": v(220, 69.78) * mm});
            skLineSegment(sketch, "E23.10.2.11", {"start": v(210.43, 86.35) * mm, "end": v(229.57, 86.35) * mm});
            skLineSegment(sketch, "E23.10.3.0", {"start": v(210.43, 86.85) * mm, "end": v(229.57, 86.85) * mm});
            skLineSegment(sketch, "E23.10.3.1", {"start": v(220, 103.42) * mm, "end": v(210.43, 86.85) * mm});
            skLineSegment(sketch, "E23.10.3.2", {"start": v(229.57, 86.85) * mm, "end": v(220, 103.42) * mm});
            skLineSegment(sketch, "E23.10.3.3", {"start": v(200.43, 103.67) * mm, "end": v(219.57, 103.67) * mm});
            skLineSegment(sketch, "E23.10.3.4", {"start": v(219.57, 103.67) * mm, "end": v(210, 87.1) * mm});
            skLineSegment(sketch, "E23.10.3.5", {"start": v(210, 87.1) * mm, "end": v(200.43, 103.67) * mm});
            skLineSegment(sketch, "E23.10.3.6", {"start": v(210, 120.74) * mm, "end": v(200.43, 104.17) * mm});
            skLineSegment(sketch, "E23.10.3.7", {"start": v(200.43, 104.17) * mm, "end": v(219.57, 104.17) * mm});
            skLineSegment(sketch, "E23.10.3.8", {"start": v(219.57, 104.17) * mm, "end": v(210, 120.74) * mm});
            skLineSegment(sketch, "E23.10.3.9", {"start": v(220, 104.42) * mm, "end": v(210.43, 121) * mm});
            skLineSegment(sketch, "E23.10.3.10", {"start": v(229.57, 121) * mm, "end": v(220, 104.42) * mm});
            skLineSegment(sketch, "E23.10.3.11", {"start": v(210.43, 121) * mm, "end": v(229.57, 121) * mm});
            skLineSegment(sketch, "E23.10.4.0", {"start": v(210.43, 121.5) * mm, "end": v(229.57, 121.5) * mm});
            skLineSegment(sketch, "E23.10.4.1", {"start": v(220, 138.06) * mm, "end": v(210.43, 121.5) * mm});
            skLineSegment(sketch, "E23.10.4.2", {"start": v(229.57, 121.5) * mm, "end": v(220, 138.06) * mm});
            skLineSegment(sketch, "E23.10.4.3", {"start": v(200.43, 138.31) * mm, "end": v(219.57, 138.31) * mm});
            skLineSegment(sketch, "E23.10.4.4", {"start": v(219.57, 138.31) * mm, "end": v(210, 121.74) * mm});
            skLineSegment(sketch, "E23.10.4.5", {"start": v(210, 121.74) * mm, "end": v(200.43, 138.31) * mm});
            skLineSegment(sketch, "E23.10.4.6", {"start": v(210, 155.38) * mm, "end": v(200.43, 138.81) * mm});
            skLineSegment(sketch, "E23.10.4.7", {"start": v(200.43, 138.81) * mm, "end": v(219.57, 138.81) * mm});
            skLineSegment(sketch, "E23.10.4.8", {"start": v(219.57, 138.81) * mm, "end": v(210, 155.38) * mm});
            skLineSegment(sketch, "E23.10.4.9", {"start": v(220, 139.06) * mm, "end": v(210.43, 155.63) * mm});
            skLineSegment(sketch, "E23.10.4.10", {"start": v(229.57, 155.63) * mm, "end": v(220, 139.06) * mm});
            skLineSegment(sketch, "E23.10.4.11", {"start": v(210.43, 155.63) * mm, "end": v(229.57, 155.63) * mm});
            skLineSegment(sketch, "E23.10.5.0", {"start": v(210.43, 156.13) * mm, "end": v(229.57, 156.13) * mm});
            skLineSegment(sketch, "E23.10.5.1", {"start": v(220, 172.7) * mm, "end": v(210.43, 156.13) * mm});
            skLineSegment(sketch, "E23.10.5.2", {"start": v(229.57, 156.13) * mm, "end": v(220, 172.7) * mm});
            skLineSegment(sketch, "E23.10.5.3", {"start": v(200.43, 172.96) * mm, "end": v(219.57, 172.96) * mm});
            skLineSegment(sketch, "E23.10.5.4", {"start": v(219.57, 172.96) * mm, "end": v(210, 156.38) * mm});
            skLineSegment(sketch, "E23.10.5.5", {"start": v(210, 156.38) * mm, "end": v(200.43, 172.96) * mm});
            skLineSegment(sketch, "E23.10.5.6", {"start": v(210, 190.03) * mm, "end": v(200.43, 173.46) * mm});
            skLineSegment(sketch, "E23.10.5.7", {"start": v(200.43, 173.46) * mm, "end": v(219.57, 173.46) * mm});
            skLineSegment(sketch, "E23.10.5.8", {"start": v(219.57, 173.46) * mm, "end": v(210, 190.03) * mm});
            skLineSegment(sketch, "E23.10.5.9", {"start": v(220, 173.7) * mm, "end": v(210.43, 190.28) * mm});
            skLineSegment(sketch, "E23.10.5.10", {"start": v(229.57, 190.28) * mm, "end": v(220, 173.7) * mm});
            skLineSegment(sketch, "E23.10.5.11", {"start": v(210.43, 190.28) * mm, "end": v(229.57, 190.28) * mm});
            skLineSegment(sketch, "E23.10.6.0", {"start": v(210.43, 190.78) * mm, "end": v(229.57, 190.78) * mm});
            skLineSegment(sketch, "E23.10.6.1", {"start": v(220, 207.35) * mm, "end": v(210.43, 190.78) * mm});
            skLineSegment(sketch, "E23.10.6.2", {"start": v(229.57, 190.78) * mm, "end": v(220, 207.35) * mm});
            skLineSegment(sketch, "E23.10.6.3", {"start": v(200.43, 207.6) * mm, "end": v(219.57, 207.6) * mm});
            skLineSegment(sketch, "E23.10.6.4", {"start": v(219.57, 207.6) * mm, "end": v(210, 191.03) * mm});
            skLineSegment(sketch, "E23.10.6.5", {"start": v(210, 191.03) * mm, "end": v(200.43, 207.6) * mm});
            skLineSegment(sketch, "E23.10.6.6", {"start": v(210, 224.67) * mm, "end": v(200.43, 208.1) * mm});
            skLineSegment(sketch, "E23.10.6.7", {"start": v(200.43, 208.1) * mm, "end": v(219.57, 208.1) * mm});
            skLineSegment(sketch, "E23.10.6.8", {"start": v(219.57, 208.1) * mm, "end": v(210, 224.67) * mm});
            skLineSegment(sketch, "E23.10.6.9", {"start": v(220, 208.35) * mm, "end": v(210.43, 224.92) * mm});
            skLineSegment(sketch, "E23.10.6.10", {"start": v(229.57, 224.92) * mm, "end": v(220, 208.35) * mm});
            skLineSegment(sketch, "E23.10.6.11", {"start": v(210.43, 224.92) * mm, "end": v(229.57, 224.92) * mm});
            skLineSegment(sketch, "E23.11.0.0", {"start": v(230.43, -17.07) * mm, "end": v(249.57, -17.07) * mm});
            skLineSegment(sketch, "E23.11.0.1", {"start": v(240, -0.5) * mm, "end": v(230.43, -17.07) * mm});
            skLineSegment(sketch, "E23.11.0.2", {"start": v(249.57, -17.07) * mm, "end": v(240, -0.5) * mm});
            skLineSegment(sketch, "E23.11.0.3", {"start": v(220.43, -0.25) * mm, "end": v(239.57, -0.25) * mm});
            skLineSegment(sketch, "E23.11.0.4", {"start": v(239.57, -0.25) * mm, "end": v(230, -16.82) * mm});
            skLineSegment(sketch, "E23.11.0.5", {"start": v(230, -16.82) * mm, "end": v(220.43, -0.25) * mm});
            skLineSegment(sketch, "E23.11.0.6", {"start": v(230, 16.82) * mm, "end": v(220.43, 0.25) * mm});
            skLineSegment(sketch, "E23.11.0.7", {"start": v(220.43, 0.25) * mm, "end": v(239.57, 0.25) * mm});
            skLineSegment(sketch, "E23.11.0.8", {"start": v(239.57, 0.25) * mm, "end": v(230, 16.82) * mm});
            skLineSegment(sketch, "E23.11.0.9", {"start": v(240, 0.5) * mm, "end": v(230.43, 17.07) * mm});
            skLineSegment(sketch, "E23.11.0.10", {"start": v(249.57, 17.07) * mm, "end": v(240, 0.5) * mm});
            skLineSegment(sketch, "E23.11.0.11", {"start": v(230.43, 17.07) * mm, "end": v(249.57, 17.07) * mm});
            skLineSegment(sketch, "E23.11.1.0", {"start": v(230.43, 17.57) * mm, "end": v(249.57, 17.57) * mm});
            skLineSegment(sketch, "E23.11.1.1", {"start": v(240, 34.14) * mm, "end": v(230.43, 17.57) * mm});
            skLineSegment(sketch, "E23.11.1.2", {"start": v(249.57, 17.57) * mm, "end": v(240, 34.14) * mm});
            skLineSegment(sketch, "E23.11.1.3", {"start": v(220.43, 34.4) * mm, "end": v(239.57, 34.4) * mm});
            skLineSegment(sketch, "E23.11.1.4", {"start": v(239.57, 34.4) * mm, "end": v(230, 17.82) * mm});
            skLineSegment(sketch, "E23.11.1.5", {"start": v(230, 17.82) * mm, "end": v(220.43, 34.4) * mm});
            skLineSegment(sketch, "E23.11.1.6", {"start": v(230, 51.46) * mm, "end": v(220.43, 34.9) * mm});
            skLineSegment(sketch, "E23.11.1.7", {"start": v(220.43, 34.9) * mm, "end": v(239.57, 34.9) * mm});
            skLineSegment(sketch, "E23.11.1.8", {"start": v(239.57, 34.9) * mm, "end": v(230, 51.46) * mm});
            skLineSegment(sketch, "E23.11.1.9", {"start": v(240, 35.14) * mm, "end": v(230.43, 51.71) * mm});
            skLineSegment(sketch, "E23.11.1.10", {"start": v(249.57, 51.71) * mm, "end": v(240, 35.14) * mm});
            skLineSegment(sketch, "E23.11.1.11", {"start": v(230.43, 51.71) * mm, "end": v(249.57, 51.71) * mm});
            skLineSegment(sketch, "E23.11.2.0", {"start": v(230.43, 52.21) * mm, "end": v(249.57, 52.21) * mm});
            skLineSegment(sketch, "E23.11.2.1", {"start": v(240, 68.78) * mm, "end": v(230.43, 52.21) * mm});
            skLineSegment(sketch, "E23.11.2.2", {"start": v(249.57, 52.21) * mm, "end": v(240, 68.78) * mm});
            skLineSegment(sketch, "E23.11.2.3", {"start": v(220.43, 69.03) * mm, "end": v(239.57, 69.03) * mm});
            skLineSegment(sketch, "E23.11.2.4", {"start": v(239.57, 69.03) * mm, "end": v(230, 52.46) * mm});
            skLineSegment(sketch, "E23.11.2.5", {"start": v(230, 52.46) * mm, "end": v(220.43, 69.03) * mm});
            skLineSegment(sketch, "E23.11.2.6", {"start": v(230, 86.1) * mm, "end": v(220.43, 69.53) * mm});
            skLineSegment(sketch, "E23.11.2.7", {"start": v(220.43, 69.53) * mm, "end": v(239.57, 69.53) * mm});
            skLineSegment(sketch, "E23.11.2.8", {"start": v(239.57, 69.53) * mm, "end": v(230, 86.1) * mm});
            skLineSegment(sketch, "E23.11.2.9", {"start": v(240, 69.78) * mm, "end": v(230.43, 86.35) * mm});
            skLineSegment(sketch, "E23.11.2.10", {"start": v(249.57, 86.35) * mm, "end": v(240, 69.78) * mm});
            skLineSegment(sketch, "E23.11.2.11", {"start": v(230.43, 86.35) * mm, "end": v(249.57, 86.35) * mm});
            skLineSegment(sketch, "E23.11.3.0", {"start": v(230.43, 86.85) * mm, "end": v(249.57, 86.85) * mm});
            skLineSegment(sketch, "E23.11.3.1", {"start": v(240, 103.42) * mm, "end": v(230.43, 86.85) * mm});
            skLineSegment(sketch, "E23.11.3.2", {"start": v(249.57, 86.85) * mm, "end": v(240, 103.42) * mm});
            skLineSegment(sketch, "E23.11.3.3", {"start": v(220.43, 103.67) * mm, "end": v(239.57, 103.67) * mm});
            skLineSegment(sketch, "E23.11.3.4", {"start": v(239.57, 103.67) * mm, "end": v(230, 87.1) * mm});
            skLineSegment(sketch, "E23.11.3.5", {"start": v(230, 87.1) * mm, "end": v(220.43, 103.67) * mm});
            skLineSegment(sketch, "E23.11.3.6", {"start": v(230, 120.74) * mm, "end": v(220.43, 104.17) * mm});
            skLineSegment(sketch, "E23.11.3.7", {"start": v(220.43, 104.17) * mm, "end": v(239.57, 104.17) * mm});
            skLineSegment(sketch, "E23.11.3.8", {"start": v(239.57, 104.17) * mm, "end": v(230, 120.74) * mm});
            skLineSegment(sketch, "E23.11.3.9", {"start": v(240, 104.42) * mm, "end": v(230.43, 121) * mm});
            skLineSegment(sketch, "E23.11.3.10", {"start": v(249.57, 121) * mm, "end": v(240, 104.42) * mm});
            skLineSegment(sketch, "E23.11.3.11", {"start": v(230.43, 121) * mm, "end": v(249.57, 121) * mm});
            skLineSegment(sketch, "E23.11.4.0", {"start": v(230.43, 121.5) * mm, "end": v(249.57, 121.5) * mm});
            skLineSegment(sketch, "E23.11.4.1", {"start": v(240, 138.06) * mm, "end": v(230.43, 121.5) * mm});
            skLineSegment(sketch, "E23.11.4.2", {"start": v(249.57, 121.5) * mm, "end": v(240, 138.06) * mm});
            skLineSegment(sketch, "E23.11.4.3", {"start": v(220.43, 138.31) * mm, "end": v(239.57, 138.31) * mm});
            skLineSegment(sketch, "E23.11.4.4", {"start": v(239.57, 138.31) * mm, "end": v(230, 121.74) * mm});
            skLineSegment(sketch, "E23.11.4.5", {"start": v(230, 121.74) * mm, "end": v(220.43, 138.31) * mm});
            skLineSegment(sketch, "E23.11.4.6", {"start": v(230, 155.38) * mm, "end": v(220.43, 138.81) * mm});
            skLineSegment(sketch, "E23.11.4.7", {"start": v(220.43, 138.81) * mm, "end": v(239.57, 138.81) * mm});
            skLineSegment(sketch, "E23.11.4.8", {"start": v(239.57, 138.81) * mm, "end": v(230, 155.38) * mm});
            skLineSegment(sketch, "E23.11.4.9", {"start": v(240, 139.06) * mm, "end": v(230.43, 155.63) * mm});
            skLineSegment(sketch, "E23.11.4.10", {"start": v(249.57, 155.63) * mm, "end": v(240, 139.06) * mm});
            skLineSegment(sketch, "E23.11.4.11", {"start": v(230.43, 155.63) * mm, "end": v(249.57, 155.63) * mm});
            skLineSegment(sketch, "E23.11.5.0", {"start": v(230.43, 156.13) * mm, "end": v(249.57, 156.13) * mm});
            skLineSegment(sketch, "E23.11.5.1", {"start": v(240, 172.7) * mm, "end": v(230.43, 156.13) * mm});
            skLineSegment(sketch, "E23.11.5.2", {"start": v(249.57, 156.13) * mm, "end": v(240, 172.7) * mm});
            skLineSegment(sketch, "E23.11.5.3", {"start": v(220.43, 172.96) * mm, "end": v(239.57, 172.96) * mm});
            skLineSegment(sketch, "E23.11.5.4", {"start": v(239.57, 172.96) * mm, "end": v(230, 156.38) * mm});
            skLineSegment(sketch, "E23.11.5.5", {"start": v(230, 156.38) * mm, "end": v(220.43, 172.96) * mm});
            skLineSegment(sketch, "E23.11.5.6", {"start": v(230, 190.03) * mm, "end": v(220.43, 173.46) * mm});
            skLineSegment(sketch, "E23.11.5.7", {"start": v(220.43, 173.46) * mm, "end": v(239.57, 173.46) * mm});
            skLineSegment(sketch, "E23.11.5.8", {"start": v(239.57, 173.46) * mm, "end": v(230, 190.03) * mm});
            skLineSegment(sketch, "E23.11.5.9", {"start": v(240, 173.7) * mm, "end": v(230.43, 190.28) * mm});
            skLineSegment(sketch, "E23.11.5.10", {"start": v(249.57, 190.28) * mm, "end": v(240, 173.7) * mm});
            skLineSegment(sketch, "E23.11.5.11", {"start": v(230.43, 190.28) * mm, "end": v(249.57, 190.28) * mm});
            skLineSegment(sketch, "E23.11.6.0", {"start": v(230.43, 190.78) * mm, "end": v(249.57, 190.78) * mm});
            skLineSegment(sketch, "E23.11.6.1", {"start": v(240, 207.35) * mm, "end": v(230.43, 190.78) * mm});
            skLineSegment(sketch, "E23.11.6.2", {"start": v(249.57, 190.78) * mm, "end": v(240, 207.35) * mm});
            skLineSegment(sketch, "E23.11.6.3", {"start": v(220.43, 207.6) * mm, "end": v(239.57, 207.6) * mm});
            skLineSegment(sketch, "E23.11.6.4", {"start": v(239.57, 207.6) * mm, "end": v(230, 191.03) * mm});
            skLineSegment(sketch, "E23.11.6.5", {"start": v(230, 191.03) * mm, "end": v(220.43, 207.6) * mm});
            skLineSegment(sketch, "E23.11.6.6", {"start": v(230, 224.67) * mm, "end": v(220.43, 208.1) * mm});
            skLineSegment(sketch, "E23.11.6.7", {"start": v(220.43, 208.1) * mm, "end": v(239.57, 208.1) * mm});
            skLineSegment(sketch, "E23.11.6.8", {"start": v(239.57, 208.1) * mm, "end": v(230, 224.67) * mm});
            skLineSegment(sketch, "E23.11.6.9", {"start": v(240, 208.35) * mm, "end": v(230.43, 224.92) * mm});
            skLineSegment(sketch, "E23.11.6.10", {"start": v(249.57, 224.92) * mm, "end": v(240, 208.35) * mm});
            skLineSegment(sketch, "E23.11.6.11", {"start": v(230.43, 224.92) * mm, "end": v(249.57, 224.92) * mm});
            skLineSegment(sketch, "E23.12.0.0", {"start": v(250.43, -17.07) * mm, "end": v(269.57, -17.07) * mm});
            skLineSegment(sketch, "E23.12.0.1", {"start": v(260, -0.5) * mm, "end": v(250.43, -17.07) * mm});
            skLineSegment(sketch, "E23.12.0.2", {"start": v(269.57, -17.07) * mm, "end": v(260, -0.5) * mm});
            skLineSegment(sketch, "E23.12.0.3", {"start": v(240.43, -0.25) * mm, "end": v(259.57, -0.25) * mm});
            skLineSegment(sketch, "E23.12.0.4", {"start": v(259.57, -0.25) * mm, "end": v(250, -16.82) * mm});
            skLineSegment(sketch, "E23.12.0.5", {"start": v(250, -16.82) * mm, "end": v(240.43, -0.25) * mm});
            skLineSegment(sketch, "E23.12.0.6", {"start": v(250, 16.82) * mm, "end": v(240.43, 0.25) * mm});
            skLineSegment(sketch, "E23.12.0.7", {"start": v(240.43, 0.25) * mm, "end": v(259.57, 0.25) * mm});
            skLineSegment(sketch, "E23.12.0.8", {"start": v(259.57, 0.25) * mm, "end": v(250, 16.82) * mm});
            skLineSegment(sketch, "E23.12.0.9", {"start": v(260, 0.5) * mm, "end": v(250.43, 17.07) * mm});
            skLineSegment(sketch, "E23.12.0.10", {"start": v(269.57, 17.07) * mm, "end": v(260, 0.5) * mm});
            skLineSegment(sketch, "E23.12.0.11", {"start": v(250.43, 17.07) * mm, "end": v(269.57, 17.07) * mm});
            skLineSegment(sketch, "E23.12.1.0", {"start": v(250.43, 17.57) * mm, "end": v(269.57, 17.57) * mm});
            skLineSegment(sketch, "E23.12.1.1", {"start": v(260, 34.14) * mm, "end": v(250.43, 17.57) * mm});
            skLineSegment(sketch, "E23.12.1.2", {"start": v(269.57, 17.57) * mm, "end": v(260, 34.14) * mm});
            skLineSegment(sketch, "E23.12.1.3", {"start": v(240.43, 34.4) * mm, "end": v(259.57, 34.4) * mm});
            skLineSegment(sketch, "E23.12.1.4", {"start": v(259.57, 34.4) * mm, "end": v(250, 17.82) * mm});
            skLineSegment(sketch, "E23.12.1.5", {"start": v(250, 17.82) * mm, "end": v(240.43, 34.4) * mm});
            skLineSegment(sketch, "E23.12.1.6", {"start": v(250, 51.46) * mm, "end": v(240.43, 34.9) * mm});
            skLineSegment(sketch, "E23.12.1.7", {"start": v(240.43, 34.9) * mm, "end": v(259.57, 34.9) * mm});
            skLineSegment(sketch, "E23.12.1.8", {"start": v(259.57, 34.9) * mm, "end": v(250, 51.46) * mm});
            skLineSegment(sketch, "E23.12.1.9", {"start": v(260, 35.14) * mm, "end": v(250.43, 51.71) * mm});
            skLineSegment(sketch, "E23.12.1.10", {"start": v(269.57, 51.71) * mm, "end": v(260, 35.14) * mm});
            skLineSegment(sketch, "E23.12.1.11", {"start": v(250.43, 51.71) * mm, "end": v(269.57, 51.71) * mm});
            skLineSegment(sketch, "E23.12.2.0", {"start": v(250.43, 52.21) * mm, "end": v(269.57, 52.21) * mm});
            skLineSegment(sketch, "E23.12.2.1", {"start": v(260, 68.78) * mm, "end": v(250.43, 52.21) * mm});
            skLineSegment(sketch, "E23.12.2.2", {"start": v(269.57, 52.21) * mm, "end": v(260, 68.78) * mm});
            skLineSegment(sketch, "E23.12.2.3", {"start": v(240.43, 69.03) * mm, "end": v(259.57, 69.03) * mm});
            skLineSegment(sketch, "E23.12.2.4", {"start": v(259.57, 69.03) * mm, "end": v(250, 52.46) * mm});
            skLineSegment(sketch, "E23.12.2.5", {"start": v(250, 52.46) * mm, "end": v(240.43, 69.03) * mm});
            skLineSegment(sketch, "E23.12.2.6", {"start": v(250, 86.1) * mm, "end": v(240.43, 69.53) * mm});
            skLineSegment(sketch, "E23.12.2.7", {"start": v(240.43, 69.53) * mm, "end": v(259.57, 69.53) * mm});
            skLineSegment(sketch, "E23.12.2.8", {"start": v(259.57, 69.53) * mm, "end": v(250, 86.1) * mm});
            skLineSegment(sketch, "E23.12.2.9", {"start": v(260, 69.78) * mm, "end": v(250.43, 86.35) * mm});
            skLineSegment(sketch, "E23.12.2.10", {"start": v(269.57, 86.35) * mm, "end": v(260, 69.78) * mm});
            skLineSegment(sketch, "E23.12.2.11", {"start": v(250.43, 86.35) * mm, "end": v(269.57, 86.35) * mm});
            skLineSegment(sketch, "E23.12.3.0", {"start": v(250.43, 86.85) * mm, "end": v(269.57, 86.85) * mm});
            skLineSegment(sketch, "E23.12.3.1", {"start": v(260, 103.42) * mm, "end": v(250.43, 86.85) * mm});
            skLineSegment(sketch, "E23.12.3.2", {"start": v(269.57, 86.85) * mm, "end": v(260, 103.42) * mm});
            skLineSegment(sketch, "E23.12.3.3", {"start": v(240.43, 103.67) * mm, "end": v(259.57, 103.67) * mm});
            skLineSegment(sketch, "E23.12.3.4", {"start": v(259.57, 103.67) * mm, "end": v(250, 87.1) * mm});
            skLineSegment(sketch, "E23.12.3.5", {"start": v(250, 87.1) * mm, "end": v(240.43, 103.67) * mm});
            skLineSegment(sketch, "E23.12.3.6", {"start": v(250, 120.74) * mm, "end": v(240.43, 104.17) * mm});
            skLineSegment(sketch, "E23.12.3.7", {"start": v(240.43, 104.17) * mm, "end": v(259.57, 104.17) * mm});
            skLineSegment(sketch, "E23.12.3.8", {"start": v(259.57, 104.17) * mm, "end": v(250, 120.74) * mm});
            skLineSegment(sketch, "E23.12.3.9", {"start": v(260, 104.42) * mm, "end": v(250.43, 121) * mm});
            skLineSegment(sketch, "E23.12.3.10", {"start": v(269.57, 121) * mm, "end": v(260, 104.42) * mm});
            skLineSegment(sketch, "E23.12.3.11", {"start": v(250.43, 121) * mm, "end": v(269.57, 121) * mm});
            skLineSegment(sketch, "E23.12.4.0", {"start": v(250.43, 121.5) * mm, "end": v(269.57, 121.5) * mm});
            skLineSegment(sketch, "E23.12.4.1", {"start": v(260, 138.06) * mm, "end": v(250.43, 121.5) * mm});
            skLineSegment(sketch, "E23.12.4.2", {"start": v(269.57, 121.5) * mm, "end": v(260, 138.06) * mm});
            skLineSegment(sketch, "E23.12.4.3", {"start": v(240.43, 138.31) * mm, "end": v(259.57, 138.31) * mm});
            skLineSegment(sketch, "E23.12.4.4", {"start": v(259.57, 138.31) * mm, "end": v(250, 121.74) * mm});
            skLineSegment(sketch, "E23.12.4.5", {"start": v(250, 121.74) * mm, "end": v(240.43, 138.31) * mm});
            skLineSegment(sketch, "E23.12.4.6", {"start": v(250, 155.38) * mm, "end": v(240.43, 138.81) * mm});
            skLineSegment(sketch, "E23.12.4.7", {"start": v(240.43, 138.81) * mm, "end": v(259.57, 138.81) * mm});
            skLineSegment(sketch, "E23.12.4.8", {"start": v(259.57, 138.81) * mm, "end": v(250, 155.38) * mm});
            skLineSegment(sketch, "E23.12.4.9", {"start": v(260, 139.06) * mm, "end": v(250.43, 155.63) * mm});
            skLineSegment(sketch, "E23.12.4.10", {"start": v(269.57, 155.63) * mm, "end": v(260, 139.06) * mm});
            skLineSegment(sketch, "E23.12.4.11", {"start": v(250.43, 155.63) * mm, "end": v(269.57, 155.63) * mm});
            skLineSegment(sketch, "E23.12.5.0", {"start": v(250.43, 156.13) * mm, "end": v(269.57, 156.13) * mm});
            skLineSegment(sketch, "E23.12.5.1", {"start": v(260, 172.7) * mm, "end": v(250.43, 156.13) * mm});
            skLineSegment(sketch, "E23.12.5.2", {"start": v(269.57, 156.13) * mm, "end": v(260, 172.7) * mm});
            skLineSegment(sketch, "E23.12.5.3", {"start": v(240.43, 172.96) * mm, "end": v(259.57, 172.96) * mm});
            skLineSegment(sketch, "E23.12.5.4", {"start": v(259.57, 172.96) * mm, "end": v(250, 156.38) * mm});
            skLineSegment(sketch, "E23.12.5.5", {"start": v(250, 156.38) * mm, "end": v(240.43, 172.96) * mm});
            skLineSegment(sketch, "E23.12.5.6", {"start": v(250, 190.03) * mm, "end": v(240.43, 173.46) * mm});
            skLineSegment(sketch, "E23.12.5.7", {"start": v(240.43, 173.46) * mm, "end": v(259.57, 173.46) * mm});
            skLineSegment(sketch, "E23.12.5.8", {"start": v(259.57, 173.46) * mm, "end": v(250, 190.03) * mm});
            skLineSegment(sketch, "E23.12.5.9", {"start": v(260, 173.7) * mm, "end": v(250.43, 190.28) * mm});
            skLineSegment(sketch, "E23.12.5.10", {"start": v(269.57, 190.28) * mm, "end": v(260, 173.7) * mm});
            skLineSegment(sketch, "E23.12.5.11", {"start": v(250.43, 190.28) * mm, "end": v(269.57, 190.28) * mm});
            skLineSegment(sketch, "E23.12.6.0", {"start": v(250.43, 190.78) * mm, "end": v(269.57, 190.78) * mm});
            skLineSegment(sketch, "E23.12.6.1", {"start": v(260, 207.35) * mm, "end": v(250.43, 190.78) * mm});
            skLineSegment(sketch, "E23.12.6.2", {"start": v(269.57, 190.78) * mm, "end": v(260, 207.35) * mm});
            skLineSegment(sketch, "E23.12.6.3", {"start": v(240.43, 207.6) * mm, "end": v(259.57, 207.6) * mm});
            skLineSegment(sketch, "E23.12.6.4", {"start": v(259.57, 207.6) * mm, "end": v(250, 191.03) * mm});
            skLineSegment(sketch, "E23.12.6.5", {"start": v(250, 191.03) * mm, "end": v(240.43, 207.6) * mm});
            skLineSegment(sketch, "E23.12.6.6", {"start": v(250, 224.67) * mm, "end": v(240.43, 208.1) * mm});
            skLineSegment(sketch, "E23.12.6.7", {"start": v(240.43, 208.1) * mm, "end": v(259.57, 208.1) * mm});
            skLineSegment(sketch, "E23.12.6.8", {"start": v(259.57, 208.1) * mm, "end": v(250, 224.67) * mm});
            skLineSegment(sketch, "E23.12.6.9", {"start": v(260, 208.35) * mm, "end": v(250.43, 224.92) * mm});
            skLineSegment(sketch, "E23.12.6.10", {"start": v(269.57, 224.92) * mm, "end": v(260, 208.35) * mm});
            skLineSegment(sketch, "E23.12.6.11", {"start": v(250.43, 224.92) * mm, "end": v(269.57, 224.92) * mm});
            skLineSegment(sketch, "E23.13.0.0", {"start": v(270.43, -17.07) * mm, "end": v(289.57, -17.07) * mm});
            skLineSegment(sketch, "E23.13.0.1", {"start": v(280, -0.5) * mm, "end": v(270.43, -17.07) * mm});
            skLineSegment(sketch, "E23.13.0.2", {"start": v(289.57, -17.07) * mm, "end": v(280, -0.5) * mm});
            skLineSegment(sketch, "E23.13.0.3", {"start": v(260.43, -0.25) * mm, "end": v(279.57, -0.25) * mm});
            skLineSegment(sketch, "E23.13.0.4", {"start": v(279.57, -0.25) * mm, "end": v(270, -16.82) * mm});
            skLineSegment(sketch, "E23.13.0.5", {"start": v(270, -16.82) * mm, "end": v(260.43, -0.25) * mm});
            skLineSegment(sketch, "E23.13.0.6", {"start": v(270, 16.82) * mm, "end": v(260.43, 0.25) * mm});
            skLineSegment(sketch, "E23.13.0.7", {"start": v(260.43, 0.25) * mm, "end": v(279.57, 0.25) * mm});
            skLineSegment(sketch, "E23.13.0.8", {"start": v(279.57, 0.25) * mm, "end": v(270, 16.82) * mm});
            skLineSegment(sketch, "E23.13.0.9", {"start": v(280, 0.5) * mm, "end": v(270.43, 17.07) * mm});
            skLineSegment(sketch, "E23.13.0.10", {"start": v(289.57, 17.07) * mm, "end": v(280, 0.5) * mm});
            skLineSegment(sketch, "E23.13.0.11", {"start": v(270.43, 17.07) * mm, "end": v(289.57, 17.07) * mm});
            skLineSegment(sketch, "E23.13.1.0", {"start": v(270.43, 17.57) * mm, "end": v(289.57, 17.57) * mm});
            skLineSegment(sketch, "E23.13.1.1", {"start": v(280, 34.14) * mm, "end": v(270.43, 17.57) * mm});
            skLineSegment(sketch, "E23.13.1.2", {"start": v(289.57, 17.57) * mm, "end": v(280, 34.14) * mm});
            skLineSegment(sketch, "E23.13.1.3", {"start": v(260.43, 34.4) * mm, "end": v(279.57, 34.4) * mm});
            skLineSegment(sketch, "E23.13.1.4", {"start": v(279.57, 34.4) * mm, "end": v(270, 17.82) * mm});
            skLineSegment(sketch, "E23.13.1.5", {"start": v(270, 17.82) * mm, "end": v(260.43, 34.4) * mm});
            skLineSegment(sketch, "E23.13.1.6", {"start": v(270, 51.46) * mm, "end": v(260.43, 34.9) * mm});
            skLineSegment(sketch, "E23.13.1.7", {"start": v(260.43, 34.9) * mm, "end": v(279.57, 34.9) * mm});
            skLineSegment(sketch, "E23.13.1.8", {"start": v(279.57, 34.9) * mm, "end": v(270, 51.46) * mm});
            skLineSegment(sketch, "E23.13.1.9", {"start": v(280, 35.14) * mm, "end": v(270.43, 51.71) * mm});
            skLineSegment(sketch, "E23.13.1.10", {"start": v(289.57, 51.71) * mm, "end": v(280, 35.14) * mm});
            skLineSegment(sketch, "E23.13.1.11", {"start": v(270.43, 51.71) * mm, "end": v(289.57, 51.71) * mm});
            skLineSegment(sketch, "E23.13.2.0", {"start": v(270.43, 52.21) * mm, "end": v(289.57, 52.21) * mm});
            skLineSegment(sketch, "E23.13.2.1", {"start": v(280, 68.78) * mm, "end": v(270.43, 52.21) * mm});
            skLineSegment(sketch, "E23.13.2.2", {"start": v(289.57, 52.21) * mm, "end": v(280, 68.78) * mm});
            skLineSegment(sketch, "E23.13.2.3", {"start": v(260.43, 69.03) * mm, "end": v(279.57, 69.03) * mm});
            skLineSegment(sketch, "E23.13.2.4", {"start": v(279.57, 69.03) * mm, "end": v(270, 52.46) * mm});
            skLineSegment(sketch, "E23.13.2.5", {"start": v(270, 52.46) * mm, "end": v(260.43, 69.03) * mm});
            skLineSegment(sketch, "E23.13.2.6", {"start": v(270, 86.1) * mm, "end": v(260.43, 69.53) * mm});
            skLineSegment(sketch, "E23.13.2.7", {"start": v(260.43, 69.53) * mm, "end": v(279.57, 69.53) * mm});
            skLineSegment(sketch, "E23.13.2.8", {"start": v(279.57, 69.53) * mm, "end": v(270, 86.1) * mm});
            skLineSegment(sketch, "E23.13.2.9", {"start": v(280, 69.78) * mm, "end": v(270.43, 86.35) * mm});
            skLineSegment(sketch, "E23.13.2.10", {"start": v(289.57, 86.35) * mm, "end": v(280, 69.78) * mm});
            skLineSegment(sketch, "E23.13.2.11", {"start": v(270.43, 86.35) * mm, "end": v(289.57, 86.35) * mm});
            skLineSegment(sketch, "E23.13.3.0", {"start": v(270.43, 86.85) * mm, "end": v(289.57, 86.85) * mm});
            skLineSegment(sketch, "E23.13.3.1", {"start": v(280, 103.42) * mm, "end": v(270.43, 86.85) * mm});
            skLineSegment(sketch, "E23.13.3.2", {"start": v(289.57, 86.85) * mm, "end": v(280, 103.42) * mm});
            skLineSegment(sketch, "E23.13.3.3", {"start": v(260.43, 103.67) * mm, "end": v(279.57, 103.67) * mm});
            skLineSegment(sketch, "E23.13.3.4", {"start": v(279.57, 103.67) * mm, "end": v(270, 87.1) * mm});
            skLineSegment(sketch, "E23.13.3.5", {"start": v(270, 87.1) * mm, "end": v(260.43, 103.67) * mm});
            skLineSegment(sketch, "E23.13.3.6", {"start": v(270, 120.74) * mm, "end": v(260.43, 104.17) * mm});
            skLineSegment(sketch, "E23.13.3.7", {"start": v(260.43, 104.17) * mm, "end": v(279.57, 104.17) * mm});
            skLineSegment(sketch, "E23.13.3.8", {"start": v(279.57, 104.17) * mm, "end": v(270, 120.74) * mm});
            skLineSegment(sketch, "E23.13.3.9", {"start": v(280, 104.42) * mm, "end": v(270.43, 121) * mm});
            skLineSegment(sketch, "E23.13.3.10", {"start": v(289.57, 121) * mm, "end": v(280, 104.42) * mm});
            skLineSegment(sketch, "E23.13.3.11", {"start": v(270.43, 121) * mm, "end": v(289.57, 121) * mm});
            skLineSegment(sketch, "E23.13.4.0", {"start": v(270.43, 121.5) * mm, "end": v(289.57, 121.5) * mm});
            skLineSegment(sketch, "E23.13.4.1", {"start": v(280, 138.06) * mm, "end": v(270.43, 121.5) * mm});
            skLineSegment(sketch, "E23.13.4.2", {"start": v(289.57, 121.5) * mm, "end": v(280, 138.06) * mm});
            skLineSegment(sketch, "E23.13.4.3", {"start": v(260.43, 138.31) * mm, "end": v(279.57, 138.31) * mm});
            skLineSegment(sketch, "E23.13.4.4", {"start": v(279.57, 138.31) * mm, "end": v(270, 121.74) * mm});
            skLineSegment(sketch, "E23.13.4.5", {"start": v(270, 121.74) * mm, "end": v(260.43, 138.31) * mm});
            skLineSegment(sketch, "E23.13.4.6", {"start": v(270, 155.38) * mm, "end": v(260.43, 138.81) * mm});
            skLineSegment(sketch, "E23.13.4.7", {"start": v(260.43, 138.81) * mm, "end": v(279.57, 138.81) * mm});
            skLineSegment(sketch, "E23.13.4.8", {"start": v(279.57, 138.81) * mm, "end": v(270, 155.38) * mm});
            skLineSegment(sketch, "E23.13.4.9", {"start": v(280, 139.06) * mm, "end": v(270.43, 155.63) * mm});
            skLineSegment(sketch, "E23.13.4.10", {"start": v(289.57, 155.63) * mm, "end": v(280, 139.06) * mm});
            skLineSegment(sketch, "E23.13.4.11", {"start": v(270.43, 155.63) * mm, "end": v(289.57, 155.63) * mm});
            skLineSegment(sketch, "E23.13.5.0", {"start": v(270.43, 156.13) * mm, "end": v(289.57, 156.13) * mm});
            skLineSegment(sketch, "E23.13.5.1", {"start": v(280, 172.7) * mm, "end": v(270.43, 156.13) * mm});
            skLineSegment(sketch, "E23.13.5.2", {"start": v(289.57, 156.13) * mm, "end": v(280, 172.7) * mm});
            skLineSegment(sketch, "E23.13.5.3", {"start": v(260.43, 172.96) * mm, "end": v(279.57, 172.96) * mm});
            skLineSegment(sketch, "E23.13.5.4", {"start": v(279.57, 172.96) * mm, "end": v(270, 156.38) * mm});
            skLineSegment(sketch, "E23.13.5.5", {"start": v(270, 156.38) * mm, "end": v(260.43, 172.96) * mm});
            skLineSegment(sketch, "E23.13.5.6", {"start": v(270, 190.03) * mm, "end": v(260.43, 173.46) * mm});
            skLineSegment(sketch, "E23.13.5.7", {"start": v(260.43, 173.46) * mm, "end": v(279.57, 173.46) * mm});
            skLineSegment(sketch, "E23.13.5.8", {"start": v(279.57, 173.46) * mm, "end": v(270, 190.03) * mm});
            skLineSegment(sketch, "E23.13.5.9", {"start": v(280, 173.7) * mm, "end": v(270.43, 190.28) * mm});
            skLineSegment(sketch, "E23.13.5.10", {"start": v(289.57, 190.28) * mm, "end": v(280, 173.7) * mm});
            skLineSegment(sketch, "E23.13.5.11", {"start": v(270.43, 190.28) * mm, "end": v(289.57, 190.28) * mm});
            skLineSegment(sketch, "E23.13.6.0", {"start": v(270.43, 190.78) * mm, "end": v(289.57, 190.78) * mm});
            skLineSegment(sketch, "E23.13.6.1", {"start": v(280, 207.35) * mm, "end": v(270.43, 190.78) * mm});
            skLineSegment(sketch, "E23.13.6.2", {"start": v(289.57, 190.78) * mm, "end": v(280, 207.35) * mm});
            skLineSegment(sketch, "E23.13.6.3", {"start": v(260.43, 207.6) * mm, "end": v(279.57, 207.6) * mm});
            skLineSegment(sketch, "E23.13.6.4", {"start": v(279.57, 207.6) * mm, "end": v(270, 191.03) * mm});
            skLineSegment(sketch, "E23.13.6.5", {"start": v(270, 191.03) * mm, "end": v(260.43, 207.6) * mm});
            skLineSegment(sketch, "E23.13.6.6", {"start": v(270, 224.67) * mm, "end": v(260.43, 208.1) * mm});
            skLineSegment(sketch, "E23.13.6.7", {"start": v(260.43, 208.1) * mm, "end": v(279.57, 208.1) * mm});
            skLineSegment(sketch, "E23.13.6.8", {"start": v(279.57, 208.1) * mm, "end": v(270, 224.67) * mm});
            skLineSegment(sketch, "E23.13.6.9", {"start": v(280, 208.35) * mm, "end": v(270.43, 224.92) * mm});
            skLineSegment(sketch, "E23.13.6.10", {"start": v(289.57, 224.92) * mm, "end": v(280, 208.35) * mm});
            skLineSegment(sketch, "E23.13.6.11", {"start": v(270.43, 224.92) * mm, "end": v(289.57, 224.92) * mm});
            skLineSegment(sketch, "E23.direction1", {"start": v(10.43, -17.07) * mm, "end": v(30.43, -17.07) * mm, "construction": true});
            skLineSegment(sketch, "E23.direction2", {"start": v(10.43, -17.07) * mm, "end": v(10.43, 17.57) * mm, "construction": true});
            skPoint(sketch, "E24.middle", {"position": v(-4.97, 0.22) * mm});
            skSolve(sketch);
        }
        {
            var Q0;
            Q0=makeQuery(id+"F0.imprint","IMPRINT",FACE,{"disambiguationData":[TD([[makeQuery(id+"F0.imprint","IMPRINT",EDGE,{"derivedFrom":sQuery(id+"F0.wireOp",EDGE,"E2")}),1.0]])]});
            extrude(context, id + "F1", {"entities" : qUnion([Q0]), "depth" : 5 * mm, "offsetDistance" : 25 * mm});
        }
        {
            var Q0;
            Q0=qCreatedBy(makeId("Top.planeOp"),FACE);
            var sketch = newSketch(context, id + "F2", { "sketchPlane" : qUnion([Q0])});
            skLineSegment(sketch, "E25", {"start": v(0, 0) * mm, "end": v(20, 0) * mm, "construction": true});
            skLineSegment(sketch, "E26", {"start": v(20, 0) * mm, "end": v(10, 17.32) * mm, "construction": true});
            skLineSegment(sketch, "E27", {"start": v(10, 17.32) * mm, "end": v(0, 0) * mm, "construction": true});
            skLineSegment(sketch, "E28.MirrorCS", {"start": v(10, -17.32) * mm, "end": v(0, 0) * mm, "construction": true});
            skLineSegment(sketch, "E29.MirrorCS", {"start": v(20, 0) * mm, "end": v(10, -17.32) * mm, "construction": true});
            skLineSegment(sketch, "E30.MirrorCS", {"start": v(30, -17.32) * mm, "end": v(20, 0) * mm, "construction": true});
            skLineSegment(sketch, "E31.MirrorCS", {"start": v(10, -17.32) * mm, "end": v(30, -17.32) * mm, "construction": true});
            skLineSegment(sketch, "E32.MirrorCS", {"start": v(30, 17.32) * mm, "end": v(20, 0) * mm, "construction": true});
            skLineSegment(sketch, "E33.MirrorCS", {"start": v(10, 17.32) * mm, "end": v(30, 17.32) * mm, "construction": true});
            skLineSegment(sketch, "E34.0.1.1", {"start": v(20, 34.64) * mm, "end": v(10, 17.32) * mm, "construction": true});
            skLineSegment(sketch, "E34.0.1.2", {"start": v(30, 17.32) * mm, "end": v(20, 34.64) * mm, "construction": true});
            skLineSegment(sketch, "E34.0.1.3", {"start": v(0, 34.64) * mm, "end": v(20, 34.64) * mm, "construction": true});
            skLineSegment(sketch, "E34.0.1.4", {"start": v(10, 17.32) * mm, "end": v(0, 34.64) * mm, "construction": true});
            skLineSegment(sketch, "E34.0.1.5", {"start": v(10, 51.96) * mm, "end": v(0, 34.64) * mm, "construction": true});
            skLineSegment(sketch, "E34.0.1.6", {"start": v(20, 34.64) * mm, "end": v(10, 51.96) * mm, "construction": true});
            skLineSegment(sketch, "E34.0.1.7", {"start": v(10, 51.96) * mm, "end": v(30, 51.96) * mm, "construction": true});
            skLineSegment(sketch, "E34.0.1.8", {"start": v(30, 51.96) * mm, "end": v(20, 34.64) * mm, "construction": true});
            skLineSegment(sketch, "E34.0.2.0", {"start": v(10, 51.96) * mm, "end": v(30, 51.96) * mm, "construction": true});
            skLineSegment(sketch, "E34.0.2.1", {"start": v(20, 69.28) * mm, "end": v(10, 51.96) * mm, "construction": true});
            skLineSegment(sketch, "E34.0.2.2", {"start": v(30, 51.96) * mm, "end": v(20, 69.28) * mm, "construction": true});
            skLineSegment(sketch, "E34.0.2.3", {"start": v(0, 69.28) * mm, "end": v(20, 69.28) * mm, "construction": true});
            skLineSegment(sketch, "E34.0.2.4", {"start": v(10, 51.96) * mm, "end": v(0, 69.28) * mm, "construction": true});
            skLineSegment(sketch, "E34.0.2.5", {"start": v(10, 86.6) * mm, "end": v(0, 69.28) * mm, "construction": true});
            skLineSegment(sketch, "E34.0.2.6", {"start": v(20, 69.28) * mm, "end": v(10, 86.6) * mm, "construction": true});
            skLineSegment(sketch, "E34.0.2.7", {"start": v(10, 86.6) * mm, "end": v(30, 86.6) * mm, "construction": true});
            skLineSegment(sketch, "E34.0.2.8", {"start": v(30, 86.6) * mm, "end": v(20, 69.28) * mm, "construction": true});
            skLineSegment(sketch, "E34.0.3.0", {"start": v(10, 86.6) * mm, "end": v(30, 86.6) * mm, "construction": true});
            skLineSegment(sketch, "E34.0.3.1", {"start": v(20, 103.92) * mm, "end": v(10, 86.6) * mm, "construction": true});
            skLineSegment(sketch, "E34.0.3.2", {"start": v(30, 86.6) * mm, "end": v(20, 103.92) * mm, "construction": true});
            skLineSegment(sketch, "E34.0.3.3", {"start": v(0, 103.92) * mm, "end": v(20, 103.92) * mm, "construction": true});
            skLineSegment(sketch, "E34.0.3.4", {"start": v(10, 86.6) * mm, "end": v(0, 103.92) * mm, "construction": true});
            skLineSegment(sketch, "E34.0.3.5", {"start": v(10, 121.24) * mm, "end": v(0, 103.92) * mm, "construction": true});
            skLineSegment(sketch, "E34.0.3.6", {"start": v(20, 103.92) * mm, "end": v(10, 121.24) * mm, "construction": true});
            skLineSegment(sketch, "E34.0.3.7", {"start": v(10, 121.24) * mm, "end": v(30, 121.24) * mm, "construction": true});
            skLineSegment(sketch, "E34.0.3.8", {"start": v(30, 121.24) * mm, "end": v(20, 103.92) * mm, "construction": true});
            skLineSegment(sketch, "E34.0.4.0", {"start": v(10, 121.24) * mm, "end": v(30, 121.24) * mm, "construction": true});
            skLineSegment(sketch, "E34.0.4.1", {"start": v(20, 138.56) * mm, "end": v(10, 121.24) * mm, "construction": true});
            skLineSegment(sketch, "E34.0.4.2", {"start": v(30, 121.24) * mm, "end": v(20, 138.56) * mm, "construction": true});
            skLineSegment(sketch, "E34.0.4.3", {"start": v(0, 138.56) * mm, "end": v(20, 138.56) * mm, "construction": true});
            skLineSegment(sketch, "E34.0.4.4", {"start": v(10, 121.24) * mm, "end": v(0, 138.56) * mm, "construction": true});
            skLineSegment(sketch, "E34.0.4.5", {"start": v(10, 155.88) * mm, "end": v(0, 138.56) * mm, "construction": true});
            skLineSegment(sketch, "E34.0.4.6", {"start": v(20, 138.56) * mm, "end": v(10, 155.88) * mm, "construction": true});
            skLineSegment(sketch, "E34.0.4.7", {"start": v(10, 155.88) * mm, "end": v(30, 155.88) * mm, "construction": true});
            skLineSegment(sketch, "E34.0.4.8", {"start": v(30, 155.88) * mm, "end": v(20, 138.56) * mm, "construction": true});
            skLineSegment(sketch, "E34.0.5.0", {"start": v(10, 155.88) * mm, "end": v(30, 155.88) * mm, "construction": true});
            skLineSegment(sketch, "E34.0.5.1", {"start": v(20, 173.2) * mm, "end": v(10, 155.88) * mm, "construction": true});
            skLineSegment(sketch, "E34.0.5.2", {"start": v(30, 155.88) * mm, "end": v(20, 173.2) * mm, "construction": true});
            skLineSegment(sketch, "E34.0.5.3", {"start": v(0, 173.2) * mm, "end": v(20, 173.2) * mm, "construction": true});
            skLineSegment(sketch, "E34.0.5.4", {"start": v(10, 155.88) * mm, "end": v(0, 173.2) * mm, "construction": true});
            skLineSegment(sketch, "E34.0.5.5", {"start": v(10, 190.53) * mm, "end": v(0, 173.2) * mm, "construction": true});
            skLineSegment(sketch, "E34.0.5.6", {"start": v(20, 173.2) * mm, "end": v(10, 190.53) * mm, "construction": true});
            skLineSegment(sketch, "E34.0.5.7", {"start": v(10, 190.53) * mm, "end": v(30, 190.53) * mm, "construction": true});
            skLineSegment(sketch, "E34.0.5.8", {"start": v(30, 190.53) * mm, "end": v(20, 173.2) * mm, "construction": true});
            skLineSegment(sketch, "E34.0.6.0", {"start": v(10, 190.53) * mm, "end": v(30, 190.53) * mm, "construction": true});
            skLineSegment(sketch, "E34.0.6.1", {"start": v(20, 207.85) * mm, "end": v(10, 190.53) * mm, "construction": true});
            skLineSegment(sketch, "E34.0.6.2", {"start": v(30, 190.53) * mm, "end": v(20, 207.85) * mm, "construction": true});
            skLineSegment(sketch, "E34.0.6.3", {"start": v(0, 207.85) * mm, "end": v(20, 207.85) * mm, "construction": true});
            skLineSegment(sketch, "E34.0.6.4", {"start": v(10, 190.53) * mm, "end": v(0, 207.85) * mm, "construction": true});
            skLineSegment(sketch, "E34.0.6.5", {"start": v(10, 225.17) * mm, "end": v(0, 207.85) * mm, "construction": true});
            skLineSegment(sketch, "E34.0.6.6", {"start": v(20, 207.85) * mm, "end": v(10, 225.17) * mm, "construction": true});
            skLineSegment(sketch, "E34.0.6.7", {"start": v(10, 225.17) * mm, "end": v(30, 225.17) * mm, "construction": true});
            skLineSegment(sketch, "E34.0.6.8", {"start": v(30, 225.17) * mm, "end": v(20, 207.85) * mm, "construction": true});
            skLineSegment(sketch, "E34.1.0.0", {"start": v(30, -17.32) * mm, "end": v(50, -17.32) * mm, "construction": true});
            skLineSegment(sketch, "E34.1.0.1", {"start": v(40, 0) * mm, "end": v(30, -17.32) * mm, "construction": true});
            skLineSegment(sketch, "E34.1.0.2", {"start": v(50, -17.32) * mm, "end": v(40, 0) * mm, "construction": true});
            skLineSegment(sketch, "E34.1.0.3", {"start": v(20, 0) * mm, "end": v(40, 0) * mm, "construction": true});
            skLineSegment(sketch, "E34.1.0.6", {"start": v(40, 0) * mm, "end": v(30, 17.32) * mm, "construction": true});
            skLineSegment(sketch, "E34.1.0.7", {"start": v(30, 17.32) * mm, "end": v(50, 17.32) * mm, "construction": true});
            skLineSegment(sketch, "E34.1.0.8", {"start": v(50, 17.32) * mm, "end": v(40, 0) * mm, "construction": true});
            skLineSegment(sketch, "E34.1.1.0", {"start": v(30, 17.32) * mm, "end": v(50, 17.32) * mm, "construction": true});
            skLineSegment(sketch, "E34.1.1.1", {"start": v(40, 34.64) * mm, "end": v(30, 17.32) * mm, "construction": true});
            skLineSegment(sketch, "E34.1.1.2", {"start": v(50, 17.32) * mm, "end": v(40, 34.64) * mm, "construction": true});
            skLineSegment(sketch, "E34.1.1.3", {"start": v(20, 34.64) * mm, "end": v(40, 34.64) * mm, "construction": true});
            skLineSegment(sketch, "E34.1.1.4", {"start": v(30, 17.32) * mm, "end": v(20, 34.64) * mm, "construction": true});
            skLineSegment(sketch, "E34.1.1.5", {"start": v(30, 51.96) * mm, "end": v(20, 34.64) * mm, "construction": true});
            skLineSegment(sketch, "E34.1.1.6", {"start": v(40, 34.64) * mm, "end": v(30, 51.96) * mm, "construction": true});
            skLineSegment(sketch, "E34.1.1.7", {"start": v(30, 51.96) * mm, "end": v(50, 51.96) * mm, "construction": true});
            skLineSegment(sketch, "E34.1.1.8", {"start": v(50, 51.96) * mm, "end": v(40, 34.64) * mm, "construction": true});
            skLineSegment(sketch, "E34.1.2.0", {"start": v(30, 51.96) * mm, "end": v(50, 51.96) * mm, "construction": true});
            skLineSegment(sketch, "E34.1.2.1", {"start": v(40, 69.28) * mm, "end": v(30, 51.96) * mm, "construction": true});
            skLineSegment(sketch, "E34.1.2.2", {"start": v(50, 51.96) * mm, "end": v(40, 69.28) * mm, "construction": true});
            skLineSegment(sketch, "E34.1.2.3", {"start": v(20, 69.28) * mm, "end": v(40, 69.28) * mm, "construction": true});
            skLineSegment(sketch, "E34.1.2.4", {"start": v(30, 51.96) * mm, "end": v(20, 69.28) * mm, "construction": true});
            skLineSegment(sketch, "E34.1.2.5", {"start": v(30, 86.6) * mm, "end": v(20, 69.28) * mm, "construction": true});
            skLineSegment(sketch, "E34.1.2.6", {"start": v(40, 69.28) * mm, "end": v(30, 86.6) * mm, "construction": true});
            skLineSegment(sketch, "E34.1.2.7", {"start": v(30, 86.6) * mm, "end": v(50, 86.6) * mm, "construction": true});
            skLineSegment(sketch, "E34.1.2.8", {"start": v(50, 86.6) * mm, "end": v(40, 69.28) * mm, "construction": true});
            skLineSegment(sketch, "E34.1.3.0", {"start": v(30, 86.6) * mm, "end": v(50, 86.6) * mm, "construction": true});
            skLineSegment(sketch, "E34.1.3.1", {"start": v(40, 103.92) * mm, "end": v(30, 86.6) * mm, "construction": true});
            skLineSegment(sketch, "E34.1.3.2", {"start": v(50, 86.6) * mm, "end": v(40, 103.92) * mm, "construction": true});
            skLineSegment(sketch, "E34.1.3.3", {"start": v(20, 103.92) * mm, "end": v(40, 103.92) * mm, "construction": true});
            skLineSegment(sketch, "E34.1.3.4", {"start": v(30, 86.6) * mm, "end": v(20, 103.92) * mm, "construction": true});
            skLineSegment(sketch, "E34.1.3.5", {"start": v(30, 121.24) * mm, "end": v(20, 103.92) * mm, "construction": true});
            skLineSegment(sketch, "E34.1.3.6", {"start": v(40, 103.92) * mm, "end": v(30, 121.24) * mm, "construction": true});
            skLineSegment(sketch, "E34.1.3.7", {"start": v(30, 121.24) * mm, "end": v(50, 121.24) * mm, "construction": true});
            skLineSegment(sketch, "E34.1.3.8", {"start": v(50, 121.24) * mm, "end": v(40, 103.92) * mm, "construction": true});
            skLineSegment(sketch, "E34.1.4.0", {"start": v(30, 121.24) * mm, "end": v(50, 121.24) * mm, "construction": true});
            skLineSegment(sketch, "E34.1.4.1", {"start": v(40, 138.56) * mm, "end": v(30, 121.24) * mm, "construction": true});
            skLineSegment(sketch, "E34.1.4.2", {"start": v(50, 121.24) * mm, "end": v(40, 138.56) * mm, "construction": true});
            skLineSegment(sketch, "E34.1.4.3", {"start": v(20, 138.56) * mm, "end": v(40, 138.56) * mm, "construction": true});
            skLineSegment(sketch, "E34.1.4.4", {"start": v(30, 121.24) * mm, "end": v(20, 138.56) * mm, "construction": true});
            skLineSegment(sketch, "E34.1.4.5", {"start": v(30, 155.88) * mm, "end": v(20, 138.56) * mm, "construction": true});
            skLineSegment(sketch, "E34.1.4.6", {"start": v(40, 138.56) * mm, "end": v(30, 155.88) * mm, "construction": true});
            skLineSegment(sketch, "E34.1.4.7", {"start": v(30, 155.88) * mm, "end": v(50, 155.88) * mm, "construction": true});
            skLineSegment(sketch, "E34.1.4.8", {"start": v(50, 155.88) * mm, "end": v(40, 138.56) * mm, "construction": true});
            skLineSegment(sketch, "E34.1.5.0", {"start": v(30, 155.88) * mm, "end": v(50, 155.88) * mm, "construction": true});
            skLineSegment(sketch, "E34.1.5.1", {"start": v(40, 173.2) * mm, "end": v(30, 155.88) * mm, "construction": true});
            skLineSegment(sketch, "E34.1.5.2", {"start": v(50, 155.88) * mm, "end": v(40, 173.2) * mm, "construction": true});
            skLineSegment(sketch, "E34.1.5.3", {"start": v(20, 173.2) * mm, "end": v(40, 173.2) * mm, "construction": true});
            skLineSegment(sketch, "E34.1.5.4", {"start": v(30, 155.88) * mm, "end": v(20, 173.2) * mm, "construction": true});
            skLineSegment(sketch, "E34.1.5.5", {"start": v(30, 190.53) * mm, "end": v(20, 173.2) * mm, "construction": true});
            skLineSegment(sketch, "E34.1.5.6", {"start": v(40, 173.2) * mm, "end": v(30, 190.53) * mm, "construction": true});
            skLineSegment(sketch, "E34.1.5.7", {"start": v(30, 190.53) * mm, "end": v(50, 190.53) * mm, "construction": true});
            skLineSegment(sketch, "E34.1.5.8", {"start": v(50, 190.53) * mm, "end": v(40, 173.2) * mm, "construction": true});
            skLineSegment(sketch, "E34.1.6.0", {"start": v(30, 190.53) * mm, "end": v(50, 190.53) * mm, "construction": true});
            skLineSegment(sketch, "E34.1.6.1", {"start": v(40, 207.85) * mm, "end": v(30, 190.53) * mm, "construction": true});
            skLineSegment(sketch, "E34.1.6.2", {"start": v(50, 190.53) * mm, "end": v(40, 207.85) * mm, "construction": true});
            skLineSegment(sketch, "E34.1.6.3", {"start": v(20, 207.85) * mm, "end": v(40, 207.85) * mm, "construction": true});
            skLineSegment(sketch, "E34.1.6.4", {"start": v(30, 190.53) * mm, "end": v(20, 207.85) * mm, "construction": true});
            skLineSegment(sketch, "E34.1.6.5", {"start": v(30, 225.17) * mm, "end": v(20, 207.85) * mm, "construction": true});
            skLineSegment(sketch, "E34.1.6.6", {"start": v(40, 207.85) * mm, "end": v(30, 225.17) * mm, "construction": true});
            skLineSegment(sketch, "E34.1.6.7", {"start": v(30, 225.17) * mm, "end": v(50, 225.17) * mm, "construction": true});
            skLineSegment(sketch, "E34.1.6.8", {"start": v(50, 225.17) * mm, "end": v(40, 207.85) * mm, "construction": true});
            skLineSegment(sketch, "E34.2.0.0", {"start": v(50, -17.32) * mm, "end": v(70, -17.32) * mm, "construction": true});
            skLineSegment(sketch, "E34.2.0.1", {"start": v(60, 0) * mm, "end": v(50, -17.32) * mm, "construction": true});
            skLineSegment(sketch, "E34.2.0.2", {"start": v(70, -17.32) * mm, "end": v(60, 0) * mm, "construction": true});
            skLineSegment(sketch, "E34.2.0.3", {"start": v(40, 0) * mm, "end": v(60, 0) * mm, "construction": true});
            skLineSegment(sketch, "E34.2.0.4", {"start": v(50, -17.32) * mm, "end": v(40, 0) * mm, "construction": true});
            skLineSegment(sketch, "E34.2.0.5", {"start": v(50, 17.32) * mm, "end": v(40, 0) * mm, "construction": true});
            skLineSegment(sketch, "E34.2.0.6", {"start": v(60, 0) * mm, "end": v(50, 17.32) * mm, "construction": true});
            skLineSegment(sketch, "E34.2.0.7", {"start": v(50, 17.32) * mm, "end": v(70, 17.32) * mm, "construction": true});
            skLineSegment(sketch, "E34.2.0.8", {"start": v(70, 17.32) * mm, "end": v(60, 0) * mm, "construction": true});
            skLineSegment(sketch, "E34.2.1.0", {"start": v(50, 17.32) * mm, "end": v(70, 17.32) * mm, "construction": true});
            skLineSegment(sketch, "E34.2.1.1", {"start": v(60, 34.64) * mm, "end": v(50, 17.32) * mm, "construction": true});
            skLineSegment(sketch, "E34.2.1.2", {"start": v(70, 17.32) * mm, "end": v(60, 34.64) * mm, "construction": true});
            skLineSegment(sketch, "E34.2.1.3", {"start": v(40, 34.64) * mm, "end": v(60, 34.64) * mm, "construction": true});
            skLineSegment(sketch, "E34.2.1.4", {"start": v(50, 17.32) * mm, "end": v(40, 34.64) * mm, "construction": true});
            skLineSegment(sketch, "E34.2.1.5", {"start": v(50, 51.96) * mm, "end": v(40, 34.64) * mm, "construction": true});
            skLineSegment(sketch, "E34.2.1.6", {"start": v(60, 34.64) * mm, "end": v(50, 51.96) * mm, "construction": true});
            skLineSegment(sketch, "E34.2.1.7", {"start": v(50, 51.96) * mm, "end": v(70, 51.96) * mm, "construction": true});
            skLineSegment(sketch, "E34.2.1.8", {"start": v(70, 51.96) * mm, "end": v(60, 34.64) * mm, "construction": true});
            skLineSegment(sketch, "E34.2.2.0", {"start": v(50, 51.96) * mm, "end": v(70, 51.96) * mm, "construction": true});
            skLineSegment(sketch, "E34.2.2.1", {"start": v(60, 69.28) * mm, "end": v(50, 51.96) * mm, "construction": true});
            skLineSegment(sketch, "E34.2.2.2", {"start": v(70, 51.96) * mm, "end": v(60, 69.28) * mm, "construction": true});
            skLineSegment(sketch, "E34.2.2.3", {"start": v(40, 69.28) * mm, "end": v(60, 69.28) * mm, "construction": true});
            skLineSegment(sketch, "E34.2.2.4", {"start": v(50, 51.96) * mm, "end": v(40, 69.28) * mm, "construction": true});
            skLineSegment(sketch, "E34.2.2.5", {"start": v(50, 86.6) * mm, "end": v(40, 69.28) * mm, "construction": true});
            skLineSegment(sketch, "E34.2.2.6", {"start": v(60, 69.28) * mm, "end": v(50, 86.6) * mm, "construction": true});
            skLineSegment(sketch, "E34.2.2.7", {"start": v(50, 86.6) * mm, "end": v(70, 86.6) * mm, "construction": true});
            skLineSegment(sketch, "E34.2.2.8", {"start": v(70, 86.6) * mm, "end": v(60, 69.28) * mm, "construction": true});
            skLineSegment(sketch, "E34.2.3.0", {"start": v(50, 86.6) * mm, "end": v(70, 86.6) * mm, "construction": true});
            skLineSegment(sketch, "E34.2.3.1", {"start": v(60, 103.92) * mm, "end": v(50, 86.6) * mm, "construction": true});
            skLineSegment(sketch, "E34.2.3.2", {"start": v(70, 86.6) * mm, "end": v(60, 103.92) * mm, "construction": true});
            skLineSegment(sketch, "E34.2.3.3", {"start": v(40, 103.92) * mm, "end": v(60, 103.92) * mm, "construction": true});
            skLineSegment(sketch, "E34.2.3.4", {"start": v(50, 86.6) * mm, "end": v(40, 103.92) * mm, "construction": true});
            skLineSegment(sketch, "E34.2.3.5", {"start": v(50, 121.24) * mm, "end": v(40, 103.92) * mm, "construction": true});
            skLineSegment(sketch, "E34.2.3.6", {"start": v(60, 103.92) * mm, "end": v(50, 121.24) * mm, "construction": true});
            skLineSegment(sketch, "E34.2.3.7", {"start": v(50, 121.24) * mm, "end": v(70, 121.24) * mm, "construction": true});
            skLineSegment(sketch, "E34.2.3.8", {"start": v(70, 121.24) * mm, "end": v(60, 103.92) * mm, "construction": true});
            skLineSegment(sketch, "E34.2.4.0", {"start": v(50, 121.24) * mm, "end": v(70, 121.24) * mm, "construction": true});
            skLineSegment(sketch, "E34.2.4.1", {"start": v(60, 138.56) * mm, "end": v(50, 121.24) * mm, "construction": true});
            skLineSegment(sketch, "E34.2.4.2", {"start": v(70, 121.24) * mm, "end": v(60, 138.56) * mm, "construction": true});
            skLineSegment(sketch, "E34.2.4.3", {"start": v(40, 138.56) * mm, "end": v(60, 138.56) * mm, "construction": true});
            skLineSegment(sketch, "E34.2.4.4", {"start": v(50, 121.24) * mm, "end": v(40, 138.56) * mm, "construction": true});
            skLineSegment(sketch, "E34.2.4.5", {"start": v(50, 155.88) * mm, "end": v(40, 138.56) * mm, "construction": true});
            skLineSegment(sketch, "E34.2.4.6", {"start": v(60, 138.56) * mm, "end": v(50, 155.88) * mm, "construction": true});
            skLineSegment(sketch, "E34.2.4.7", {"start": v(50, 155.88) * mm, "end": v(70, 155.88) * mm, "construction": true});
            skLineSegment(sketch, "E34.2.4.8", {"start": v(70, 155.88) * mm, "end": v(60, 138.56) * mm, "construction": true});
            skLineSegment(sketch, "E34.2.5.0", {"start": v(50, 155.88) * mm, "end": v(70, 155.88) * mm, "construction": true});
            skLineSegment(sketch, "E34.2.5.1", {"start": v(60, 173.2) * mm, "end": v(50, 155.88) * mm, "construction": true});
            skLineSegment(sketch, "E34.2.5.2", {"start": v(70, 155.88) * mm, "end": v(60, 173.2) * mm, "construction": true});
            skLineSegment(sketch, "E34.2.5.3", {"start": v(40, 173.2) * mm, "end": v(60, 173.2) * mm, "construction": true});
            skLineSegment(sketch, "E34.2.5.4", {"start": v(50, 155.88) * mm, "end": v(40, 173.2) * mm, "construction": true});
            skLineSegment(sketch, "E34.2.5.5", {"start": v(50, 190.53) * mm, "end": v(40, 173.2) * mm, "construction": true});
            skLineSegment(sketch, "E34.2.5.6", {"start": v(60, 173.2) * mm, "end": v(50, 190.53) * mm, "construction": true});
            skLineSegment(sketch, "E34.2.5.7", {"start": v(50, 190.53) * mm, "end": v(70, 190.53) * mm, "construction": true});
            skLineSegment(sketch, "E34.2.5.8", {"start": v(70, 190.53) * mm, "end": v(60, 173.2) * mm, "construction": true});
            skLineSegment(sketch, "E34.2.6.0", {"start": v(50, 190.53) * mm, "end": v(70, 190.53) * mm, "construction": true});
            skLineSegment(sketch, "E34.2.6.1", {"start": v(60, 207.85) * mm, "end": v(50, 190.53) * mm, "construction": true});
            skLineSegment(sketch, "E34.2.6.2", {"start": v(70, 190.53) * mm, "end": v(60, 207.85) * mm, "construction": true});
            skLineSegment(sketch, "E34.2.6.3", {"start": v(40, 207.85) * mm, "end": v(60, 207.85) * mm, "construction": true});
            skLineSegment(sketch, "E34.2.6.4", {"start": v(50, 190.53) * mm, "end": v(40, 207.85) * mm, "construction": true});
            skLineSegment(sketch, "E34.2.6.5", {"start": v(50, 225.17) * mm, "end": v(40, 207.85) * mm, "construction": true});
            skLineSegment(sketch, "E34.2.6.6", {"start": v(60, 207.85) * mm, "end": v(50, 225.17) * mm, "construction": true});
            skLineSegment(sketch, "E34.2.6.7", {"start": v(50, 225.17) * mm, "end": v(70, 225.17) * mm, "construction": true});
            skLineSegment(sketch, "E34.2.6.8", {"start": v(70, 225.17) * mm, "end": v(60, 207.85) * mm, "construction": true});
            skLineSegment(sketch, "E34.3.0.0", {"start": v(70, -17.32) * mm, "end": v(90, -17.32) * mm, "construction": true});
            skLineSegment(sketch, "E34.3.0.1", {"start": v(80, 0) * mm, "end": v(70, -17.32) * mm, "construction": true});
            skLineSegment(sketch, "E34.3.0.2", {"start": v(90, -17.32) * mm, "end": v(80, 0) * mm, "construction": true});
            skLineSegment(sketch, "E34.3.0.3", {"start": v(60, 0) * mm, "end": v(80, 0) * mm, "construction": true});
            skLineSegment(sketch, "E34.3.0.4", {"start": v(70, -17.32) * mm, "end": v(60, 0) * mm, "construction": true});
            skLineSegment(sketch, "E34.3.0.5", {"start": v(70, 17.32) * mm, "end": v(60, 0) * mm, "construction": true});
            skLineSegment(sketch, "E34.3.0.6", {"start": v(80, 0) * mm, "end": v(70, 17.32) * mm, "construction": true});
            skLineSegment(sketch, "E34.3.0.7", {"start": v(70, 17.32) * mm, "end": v(90, 17.32) * mm, "construction": true});
            skLineSegment(sketch, "E34.3.0.8", {"start": v(90, 17.32) * mm, "end": v(80, 0) * mm, "construction": true});
            skLineSegment(sketch, "E34.3.1.0", {"start": v(70, 17.32) * mm, "end": v(90, 17.32) * mm, "construction": true});
            skLineSegment(sketch, "E34.3.1.1", {"start": v(80, 34.64) * mm, "end": v(70, 17.32) * mm, "construction": true});
            skLineSegment(sketch, "E34.3.1.2", {"start": v(90, 17.32) * mm, "end": v(80, 34.64) * mm, "construction": true});
            skLineSegment(sketch, "E34.3.1.3", {"start": v(60, 34.64) * mm, "end": v(80, 34.64) * mm, "construction": true});
            skLineSegment(sketch, "E34.3.1.4", {"start": v(70, 17.32) * mm, "end": v(60, 34.64) * mm, "construction": true});
            skLineSegment(sketch, "E34.3.1.5", {"start": v(70, 51.96) * mm, "end": v(60, 34.64) * mm, "construction": true});
            skLineSegment(sketch, "E34.3.1.6", {"start": v(80, 34.64) * mm, "end": v(70, 51.96) * mm, "construction": true});
            skLineSegment(sketch, "E34.3.1.7", {"start": v(70, 51.96) * mm, "end": v(90, 51.96) * mm, "construction": true});
            skLineSegment(sketch, "E34.3.1.8", {"start": v(90, 51.96) * mm, "end": v(80, 34.64) * mm, "construction": true});
            skLineSegment(sketch, "E34.3.2.0", {"start": v(70, 51.96) * mm, "end": v(90, 51.96) * mm, "construction": true});
            skLineSegment(sketch, "E34.3.2.1", {"start": v(80, 69.28) * mm, "end": v(70, 51.96) * mm, "construction": true});
            skLineSegment(sketch, "E34.3.2.2", {"start": v(90, 51.96) * mm, "end": v(80, 69.28) * mm, "construction": true});
            skLineSegment(sketch, "E34.3.2.3", {"start": v(60, 69.28) * mm, "end": v(80, 69.28) * mm, "construction": true});
            skLineSegment(sketch, "E34.3.2.4", {"start": v(70, 51.96) * mm, "end": v(60, 69.28) * mm, "construction": true});
            skLineSegment(sketch, "E34.3.2.5", {"start": v(70, 86.6) * mm, "end": v(60, 69.28) * mm, "construction": true});
            skLineSegment(sketch, "E34.3.2.6", {"start": v(80, 69.28) * mm, "end": v(70, 86.6) * mm, "construction": true});
            skLineSegment(sketch, "E34.3.2.7", {"start": v(70, 86.6) * mm, "end": v(90, 86.6) * mm, "construction": true});
            skLineSegment(sketch, "E34.3.2.8", {"start": v(90, 86.6) * mm, "end": v(80, 69.28) * mm, "construction": true});
            skLineSegment(sketch, "E34.3.3.0", {"start": v(70, 86.6) * mm, "end": v(90, 86.6) * mm, "construction": true});
            skLineSegment(sketch, "E34.3.3.1", {"start": v(80, 103.92) * mm, "end": v(70, 86.6) * mm, "construction": true});
            skLineSegment(sketch, "E34.3.3.2", {"start": v(90, 86.6) * mm, "end": v(80, 103.92) * mm, "construction": true});
            skLineSegment(sketch, "E34.3.3.3", {"start": v(60, 103.92) * mm, "end": v(80, 103.92) * mm, "construction": true});
            skLineSegment(sketch, "E34.3.3.4", {"start": v(70, 86.6) * mm, "end": v(60, 103.92) * mm, "construction": true});
            skLineSegment(sketch, "E34.3.3.5", {"start": v(70, 121.24) * mm, "end": v(60, 103.92) * mm, "construction": true});
            skLineSegment(sketch, "E34.3.3.6", {"start": v(80, 103.92) * mm, "end": v(70, 121.24) * mm, "construction": true});
            skLineSegment(sketch, "E34.3.3.7", {"start": v(70, 121.24) * mm, "end": v(90, 121.24) * mm, "construction": true});
            skLineSegment(sketch, "E34.3.3.8", {"start": v(90, 121.24) * mm, "end": v(80, 103.92) * mm, "construction": true});
            skLineSegment(sketch, "E34.3.4.0", {"start": v(70, 121.24) * mm, "end": v(90, 121.24) * mm, "construction": true});
            skLineSegment(sketch, "E34.3.4.1", {"start": v(80, 138.56) * mm, "end": v(70, 121.24) * mm, "construction": true});
            skLineSegment(sketch, "E34.3.4.2", {"start": v(90, 121.24) * mm, "end": v(80, 138.56) * mm, "construction": true});
            skLineSegment(sketch, "E34.3.4.3", {"start": v(60, 138.56) * mm, "end": v(80, 138.56) * mm, "construction": true});
            skLineSegment(sketch, "E34.3.4.4", {"start": v(70, 121.24) * mm, "end": v(60, 138.56) * mm, "construction": true});
            skLineSegment(sketch, "E34.3.4.5", {"start": v(70, 155.88) * mm, "end": v(60, 138.56) * mm, "construction": true});
            skLineSegment(sketch, "E34.3.4.6", {"start": v(80, 138.56) * mm, "end": v(70, 155.88) * mm, "construction": true});
            skLineSegment(sketch, "E34.3.4.7", {"start": v(70, 155.88) * mm, "end": v(90, 155.88) * mm, "construction": true});
            skLineSegment(sketch, "E34.3.4.8", {"start": v(90, 155.88) * mm, "end": v(80, 138.56) * mm, "construction": true});
            skLineSegment(sketch, "E34.3.5.0", {"start": v(70, 155.88) * mm, "end": v(90, 155.88) * mm, "construction": true});
            skLineSegment(sketch, "E34.3.5.1", {"start": v(80, 173.2) * mm, "end": v(70, 155.88) * mm, "construction": true});
            skLineSegment(sketch, "E34.3.5.2", {"start": v(90, 155.88) * mm, "end": v(80, 173.2) * mm, "construction": true});
            skLineSegment(sketch, "E34.3.5.3", {"start": v(60, 173.2) * mm, "end": v(80, 173.2) * mm, "construction": true});
            skLineSegment(sketch, "E34.3.5.4", {"start": v(70, 155.88) * mm, "end": v(60, 173.2) * mm, "construction": true});
            skLineSegment(sketch, "E34.3.5.5", {"start": v(70, 190.53) * mm, "end": v(60, 173.2) * mm, "construction": true});
            skLineSegment(sketch, "E34.3.5.6", {"start": v(80, 173.2) * mm, "end": v(70, 190.53) * mm, "construction": true});
            skLineSegment(sketch, "E34.3.5.7", {"start": v(70, 190.53) * mm, "end": v(90, 190.53) * mm, "construction": true});
            skLineSegment(sketch, "E34.3.5.8", {"start": v(90, 190.53) * mm, "end": v(80, 173.2) * mm, "construction": true});
            skLineSegment(sketch, "E34.3.6.0", {"start": v(70, 190.53) * mm, "end": v(90, 190.53) * mm, "construction": true});
            skLineSegment(sketch, "E34.3.6.1", {"start": v(80, 207.85) * mm, "end": v(70, 190.53) * mm, "construction": true});
            skLineSegment(sketch, "E34.3.6.2", {"start": v(90, 190.53) * mm, "end": v(80, 207.85) * mm, "construction": true});
            skLineSegment(sketch, "E34.3.6.3", {"start": v(60, 207.85) * mm, "end": v(80, 207.85) * mm, "construction": true});
            skLineSegment(sketch, "E34.3.6.4", {"start": v(70, 190.53) * mm, "end": v(60, 207.85) * mm, "construction": true});
            skLineSegment(sketch, "E34.3.6.5", {"start": v(70, 225.17) * mm, "end": v(60, 207.85) * mm, "construction": true});
            skLineSegment(sketch, "E34.3.6.6", {"start": v(80, 207.85) * mm, "end": v(70, 225.17) * mm, "construction": true});
            skLineSegment(sketch, "E34.3.6.7", {"start": v(70, 225.17) * mm, "end": v(90, 225.17) * mm, "construction": true});
            skLineSegment(sketch, "E34.3.6.8", {"start": v(90, 225.17) * mm, "end": v(80, 207.85) * mm, "construction": true});
            skLineSegment(sketch, "E34.4.0.0", {"start": v(90, -17.32) * mm, "end": v(110, -17.32) * mm, "construction": true});
            skLineSegment(sketch, "E34.4.0.1", {"start": v(100, 0) * mm, "end": v(90, -17.32) * mm, "construction": true});
            skLineSegment(sketch, "E34.4.0.2", {"start": v(110, -17.32) * mm, "end": v(100, 0) * mm, "construction": true});
            skLineSegment(sketch, "E34.4.0.3", {"start": v(80, 0) * mm, "end": v(100, 0) * mm, "construction": true});
            skLineSegment(sketch, "E34.4.0.4", {"start": v(90, -17.32) * mm, "end": v(80, 0) * mm, "construction": true});
            skLineSegment(sketch, "E34.4.0.5", {"start": v(90, 17.32) * mm, "end": v(80, 0) * mm, "construction": true});
            skLineSegment(sketch, "E34.4.0.6", {"start": v(100, 0) * mm, "end": v(90, 17.32) * mm, "construction": true});
            skLineSegment(sketch, "E34.4.0.7", {"start": v(90, 17.32) * mm, "end": v(110, 17.32) * mm, "construction": true});
            skLineSegment(sketch, "E34.4.0.8", {"start": v(110, 17.32) * mm, "end": v(100, 0) * mm, "construction": true});
            skLineSegment(sketch, "E34.4.1.0", {"start": v(90, 17.32) * mm, "end": v(110, 17.32) * mm, "construction": true});
            skLineSegment(sketch, "E34.4.1.1", {"start": v(100, 34.64) * mm, "end": v(90, 17.32) * mm, "construction": true});
            skLineSegment(sketch, "E34.4.1.2", {"start": v(110, 17.32) * mm, "end": v(100, 34.64) * mm, "construction": true});
            skLineSegment(sketch, "E34.4.1.3", {"start": v(80, 34.64) * mm, "end": v(100, 34.64) * mm, "construction": true});
            skLineSegment(sketch, "E34.4.1.4", {"start": v(90, 17.32) * mm, "end": v(80, 34.64) * mm, "construction": true});
            skLineSegment(sketch, "E34.4.1.5", {"start": v(90, 51.96) * mm, "end": v(80, 34.64) * mm, "construction": true});
            skLineSegment(sketch, "E34.4.1.6", {"start": v(100, 34.64) * mm, "end": v(90, 51.96) * mm, "construction": true});
            skLineSegment(sketch, "E34.4.1.7", {"start": v(90, 51.96) * mm, "end": v(110, 51.96) * mm, "construction": true});
            skLineSegment(sketch, "E34.4.1.8", {"start": v(110, 51.96) * mm, "end": v(100, 34.64) * mm, "construction": true});
            skLineSegment(sketch, "E34.4.2.0", {"start": v(90, 51.96) * mm, "end": v(110, 51.96) * mm, "construction": true});
            skLineSegment(sketch, "E34.4.2.1", {"start": v(100, 69.28) * mm, "end": v(90, 51.96) * mm, "construction": true});
            skLineSegment(sketch, "E34.4.2.2", {"start": v(110, 51.96) * mm, "end": v(100, 69.28) * mm, "construction": true});
            skLineSegment(sketch, "E34.4.2.3", {"start": v(80, 69.28) * mm, "end": v(100, 69.28) * mm, "construction": true});
            skLineSegment(sketch, "E34.4.2.4", {"start": v(90, 51.96) * mm, "end": v(80, 69.28) * mm, "construction": true});
            skLineSegment(sketch, "E34.4.2.5", {"start": v(90, 86.6) * mm, "end": v(80, 69.28) * mm, "construction": true});
            skLineSegment(sketch, "E34.4.2.6", {"start": v(100, 69.28) * mm, "end": v(90, 86.6) * mm, "construction": true});
            skLineSegment(sketch, "E34.4.2.7", {"start": v(90, 86.6) * mm, "end": v(110, 86.6) * mm, "construction": true});
            skLineSegment(sketch, "E34.4.2.8", {"start": v(110, 86.6) * mm, "end": v(100, 69.28) * mm, "construction": true});
            skLineSegment(sketch, "E34.4.3.0", {"start": v(90, 86.6) * mm, "end": v(110, 86.6) * mm, "construction": true});
            skLineSegment(sketch, "E34.4.3.1", {"start": v(100, 103.92) * mm, "end": v(90, 86.6) * mm, "construction": true});
            skLineSegment(sketch, "E34.4.3.2", {"start": v(110, 86.6) * mm, "end": v(100, 103.92) * mm, "construction": true});
            skLineSegment(sketch, "E34.4.3.3", {"start": v(80, 103.92) * mm, "end": v(100, 103.92) * mm, "construction": true});
            skLineSegment(sketch, "E34.4.3.4", {"start": v(90, 86.6) * mm, "end": v(80, 103.92) * mm, "construction": true});
            skLineSegment(sketch, "E34.4.3.5", {"start": v(90, 121.24) * mm, "end": v(80, 103.92) * mm, "construction": true});
            skLineSegment(sketch, "E34.4.3.6", {"start": v(100, 103.92) * mm, "end": v(90, 121.24) * mm, "construction": true});
            skLineSegment(sketch, "E34.4.3.7", {"start": v(90, 121.24) * mm, "end": v(110, 121.24) * mm, "construction": true});
            skLineSegment(sketch, "E34.4.3.8", {"start": v(110, 121.24) * mm, "end": v(100, 103.92) * mm, "construction": true});
            skLineSegment(sketch, "E34.4.4.0", {"start": v(90, 121.24) * mm, "end": v(110, 121.24) * mm, "construction": true});
            skLineSegment(sketch, "E34.4.4.1", {"start": v(100, 138.56) * mm, "end": v(90, 121.24) * mm, "construction": true});
            skLineSegment(sketch, "E34.4.4.2", {"start": v(110, 121.24) * mm, "end": v(100, 138.56) * mm, "construction": true});
            skLineSegment(sketch, "E34.4.4.3", {"start": v(80, 138.56) * mm, "end": v(100, 138.56) * mm, "construction": true});
            skLineSegment(sketch, "E34.4.4.4", {"start": v(90, 121.24) * mm, "end": v(80, 138.56) * mm, "construction": true});
            skLineSegment(sketch, "E34.4.4.5", {"start": v(90, 155.88) * mm, "end": v(80, 138.56) * mm, "construction": true});
            skLineSegment(sketch, "E34.4.4.6", {"start": v(100, 138.56) * mm, "end": v(90, 155.88) * mm, "construction": true});
            skLineSegment(sketch, "E34.4.4.7", {"start": v(90, 155.88) * mm, "end": v(110, 155.88) * mm, "construction": true});
            skLineSegment(sketch, "E34.4.4.8", {"start": v(110, 155.88) * mm, "end": v(100, 138.56) * mm, "construction": true});
            skLineSegment(sketch, "E34.4.5.0", {"start": v(90, 155.88) * mm, "end": v(110, 155.88) * mm, "construction": true});
            skLineSegment(sketch, "E34.4.5.1", {"start": v(100, 173.2) * mm, "end": v(90, 155.88) * mm, "construction": true});
            skLineSegment(sketch, "E34.4.5.2", {"start": v(110, 155.88) * mm, "end": v(100, 173.2) * mm, "construction": true});
            skLineSegment(sketch, "E34.4.5.3", {"start": v(80, 173.2) * mm, "end": v(100, 173.2) * mm, "construction": true});
            skLineSegment(sketch, "E34.4.5.4", {"start": v(90, 155.88) * mm, "end": v(80, 173.2) * mm, "construction": true});
            skLineSegment(sketch, "E34.4.5.5", {"start": v(90, 190.53) * mm, "end": v(80, 173.2) * mm, "construction": true});
            skLineSegment(sketch, "E34.4.5.6", {"start": v(100, 173.2) * mm, "end": v(90, 190.53) * mm, "construction": true});
            skLineSegment(sketch, "E34.4.5.7", {"start": v(90, 190.53) * mm, "end": v(110, 190.53) * mm, "construction": true});
            skLineSegment(sketch, "E34.4.5.8", {"start": v(110, 190.53) * mm, "end": v(100, 173.2) * mm, "construction": true});
            skLineSegment(sketch, "E34.4.6.0", {"start": v(90, 190.53) * mm, "end": v(110, 190.53) * mm, "construction": true});
            skLineSegment(sketch, "E34.4.6.1", {"start": v(100, 207.85) * mm, "end": v(90, 190.53) * mm, "construction": true});
            skLineSegment(sketch, "E34.4.6.2", {"start": v(110, 190.53) * mm, "end": v(100, 207.85) * mm, "construction": true});
            skLineSegment(sketch, "E34.4.6.3", {"start": v(80, 207.85) * mm, "end": v(100, 207.85) * mm, "construction": true});
            skLineSegment(sketch, "E34.4.6.4", {"start": v(90, 190.53) * mm, "end": v(80, 207.85) * mm, "construction": true});
            skLineSegment(sketch, "E34.4.6.5", {"start": v(90, 225.17) * mm, "end": v(80, 207.85) * mm, "construction": true});
            skLineSegment(sketch, "E34.4.6.6", {"start": v(100, 207.85) * mm, "end": v(90, 225.17) * mm, "construction": true});
            skLineSegment(sketch, "E34.4.6.7", {"start": v(90, 225.17) * mm, "end": v(110, 225.17) * mm, "construction": true});
            skLineSegment(sketch, "E34.4.6.8", {"start": v(110, 225.17) * mm, "end": v(100, 207.85) * mm, "construction": true});
            skLineSegment(sketch, "E34.5.0.0", {"start": v(110, -17.32) * mm, "end": v(130, -17.32) * mm, "construction": true});
            skLineSegment(sketch, "E34.5.0.1", {"start": v(120, 0) * mm, "end": v(110, -17.32) * mm, "construction": true});
            skLineSegment(sketch, "E34.5.0.2", {"start": v(130, -17.32) * mm, "end": v(120, 0) * mm, "construction": true});
            skLineSegment(sketch, "E34.5.0.3", {"start": v(100, 0) * mm, "end": v(120, 0) * mm, "construction": true});
            skLineSegment(sketch, "E34.5.0.4", {"start": v(110, -17.32) * mm, "end": v(100, 0) * mm, "construction": true});
            skLineSegment(sketch, "E34.5.0.5", {"start": v(110, 17.32) * mm, "end": v(100, 0) * mm, "construction": true});
            skLineSegment(sketch, "E34.5.0.6", {"start": v(120, 0) * mm, "end": v(110, 17.32) * mm, "construction": true});
            skLineSegment(sketch, "E34.5.0.7", {"start": v(110, 17.32) * mm, "end": v(130, 17.32) * mm, "construction": true});
            skLineSegment(sketch, "E34.5.0.8", {"start": v(130, 17.32) * mm, "end": v(120, 0) * mm, "construction": true});
            skLineSegment(sketch, "E34.5.1.0", {"start": v(110, 17.32) * mm, "end": v(130, 17.32) * mm, "construction": true});
            skLineSegment(sketch, "E34.5.1.1", {"start": v(120, 34.64) * mm, "end": v(110, 17.32) * mm, "construction": true});
            skLineSegment(sketch, "E34.5.1.2", {"start": v(130, 17.32) * mm, "end": v(120, 34.64) * mm, "construction": true});
            skLineSegment(sketch, "E34.5.1.3", {"start": v(100, 34.64) * mm, "end": v(120, 34.64) * mm, "construction": true});
            skLineSegment(sketch, "E34.5.1.4", {"start": v(110, 17.32) * mm, "end": v(100, 34.64) * mm, "construction": true});
            skLineSegment(sketch, "E34.5.1.5", {"start": v(110, 51.96) * mm, "end": v(100, 34.64) * mm, "construction": true});
            skLineSegment(sketch, "E34.5.1.6", {"start": v(120, 34.64) * mm, "end": v(110, 51.96) * mm, "construction": true});
            skLineSegment(sketch, "E34.5.1.7", {"start": v(110, 51.96) * mm, "end": v(130, 51.96) * mm, "construction": true});
            skLineSegment(sketch, "E34.5.1.8", {"start": v(130, 51.96) * mm, "end": v(120, 34.64) * mm, "construction": true});
            skLineSegment(sketch, "E34.5.2.0", {"start": v(110, 51.96) * mm, "end": v(130, 51.96) * mm, "construction": true});
            skLineSegment(sketch, "E34.5.2.1", {"start": v(120, 69.28) * mm, "end": v(110, 51.96) * mm, "construction": true});
            skLineSegment(sketch, "E34.5.2.2", {"start": v(130, 51.96) * mm, "end": v(120, 69.28) * mm, "construction": true});
            skLineSegment(sketch, "E34.5.2.3", {"start": v(100, 69.28) * mm, "end": v(120, 69.28) * mm, "construction": true});
            skLineSegment(sketch, "E34.5.2.4", {"start": v(110, 51.96) * mm, "end": v(100, 69.28) * mm, "construction": true});
            skLineSegment(sketch, "E34.5.2.5", {"start": v(110, 86.6) * mm, "end": v(100, 69.28) * mm, "construction": true});
            skLineSegment(sketch, "E34.5.2.6", {"start": v(120, 69.28) * mm, "end": v(110, 86.6) * mm, "construction": true});
            skLineSegment(sketch, "E34.5.2.7", {"start": v(110, 86.6) * mm, "end": v(130, 86.6) * mm, "construction": true});
            skLineSegment(sketch, "E34.5.2.8", {"start": v(130, 86.6) * mm, "end": v(120, 69.28) * mm, "construction": true});
            skLineSegment(sketch, "E34.5.3.0", {"start": v(110, 86.6) * mm, "end": v(130, 86.6) * mm, "construction": true});
            skLineSegment(sketch, "E34.5.3.1", {"start": v(120, 103.92) * mm, "end": v(110, 86.6) * mm, "construction": true});
            skLineSegment(sketch, "E34.5.3.2", {"start": v(130, 86.6) * mm, "end": v(120, 103.92) * mm, "construction": true});
            skLineSegment(sketch, "E34.5.3.3", {"start": v(100, 103.92) * mm, "end": v(120, 103.92) * mm, "construction": true});
            skLineSegment(sketch, "E34.5.3.4", {"start": v(110, 86.6) * mm, "end": v(100, 103.92) * mm, "construction": true});
            skLineSegment(sketch, "E34.5.3.5", {"start": v(110, 121.24) * mm, "end": v(100, 103.92) * mm, "construction": true});
            skLineSegment(sketch, "E34.5.3.6", {"start": v(120, 103.92) * mm, "end": v(110, 121.24) * mm, "construction": true});
            skLineSegment(sketch, "E34.5.3.7", {"start": v(110, 121.24) * mm, "end": v(130, 121.24) * mm, "construction": true});
            skLineSegment(sketch, "E34.5.3.8", {"start": v(130, 121.24) * mm, "end": v(120, 103.92) * mm, "construction": true});
            skLineSegment(sketch, "E34.5.4.0", {"start": v(110, 121.24) * mm, "end": v(130, 121.24) * mm, "construction": true});
            skLineSegment(sketch, "E34.5.4.1", {"start": v(120, 138.56) * mm, "end": v(110, 121.24) * mm, "construction": true});
            skLineSegment(sketch, "E34.5.4.2", {"start": v(130, 121.24) * mm, "end": v(120, 138.56) * mm, "construction": true});
            skLineSegment(sketch, "E34.5.4.3", {"start": v(100, 138.56) * mm, "end": v(120, 138.56) * mm, "construction": true});
            skLineSegment(sketch, "E34.5.4.4", {"start": v(110, 121.24) * mm, "end": v(100, 138.56) * mm, "construction": true});
            skLineSegment(sketch, "E34.5.4.5", {"start": v(110, 155.88) * mm, "end": v(100, 138.56) * mm, "construction": true});
            skLineSegment(sketch, "E34.5.4.6", {"start": v(120, 138.56) * mm, "end": v(110, 155.88) * mm, "construction": true});
            skLineSegment(sketch, "E34.5.4.7", {"start": v(110, 155.88) * mm, "end": v(130, 155.88) * mm, "construction": true});
            skLineSegment(sketch, "E34.5.4.8", {"start": v(130, 155.88) * mm, "end": v(120, 138.56) * mm, "construction": true});
            skLineSegment(sketch, "E34.5.5.0", {"start": v(110, 155.88) * mm, "end": v(130, 155.88) * mm, "construction": true});
            skLineSegment(sketch, "E34.5.5.1", {"start": v(120, 173.2) * mm, "end": v(110, 155.88) * mm, "construction": true});
            skLineSegment(sketch, "E34.5.5.2", {"start": v(130, 155.88) * mm, "end": v(120, 173.2) * mm, "construction": true});
            skLineSegment(sketch, "E34.5.5.3", {"start": v(100, 173.2) * mm, "end": v(120, 173.2) * mm, "construction": true});
            skLineSegment(sketch, "E34.5.5.4", {"start": v(110, 155.88) * mm, "end": v(100, 173.2) * mm, "construction": true});
            skLineSegment(sketch, "E34.5.5.5", {"start": v(110, 190.53) * mm, "end": v(100, 173.2) * mm, "construction": true});
            skLineSegment(sketch, "E34.5.5.6", {"start": v(120, 173.2) * mm, "end": v(110, 190.53) * mm, "construction": true});
            skLineSegment(sketch, "E34.5.5.7", {"start": v(110, 190.53) * mm, "end": v(130, 190.53) * mm, "construction": true});
            skLineSegment(sketch, "E34.5.5.8", {"start": v(130, 190.53) * mm, "end": v(120, 173.2) * mm, "construction": true});
            skLineSegment(sketch, "E34.5.6.0", {"start": v(110, 190.53) * mm, "end": v(130, 190.53) * mm, "construction": true});
            skLineSegment(sketch, "E34.5.6.1", {"start": v(120, 207.85) * mm, "end": v(110, 190.53) * mm, "construction": true});
            skLineSegment(sketch, "E34.5.6.2", {"start": v(130, 190.53) * mm, "end": v(120, 207.85) * mm, "construction": true});
            skLineSegment(sketch, "E34.5.6.3", {"start": v(100, 207.85) * mm, "end": v(120, 207.85) * mm, "construction": true});
            skLineSegment(sketch, "E34.5.6.4", {"start": v(110, 190.53) * mm, "end": v(100, 207.85) * mm, "construction": true});
            skLineSegment(sketch, "E34.5.6.5", {"start": v(110, 225.17) * mm, "end": v(100, 207.85) * mm, "construction": true});
            skLineSegment(sketch, "E34.5.6.6", {"start": v(120, 207.85) * mm, "end": v(110, 225.17) * mm, "construction": true});
            skLineSegment(sketch, "E34.5.6.7", {"start": v(110, 225.17) * mm, "end": v(130, 225.17) * mm, "construction": true});
            skLineSegment(sketch, "E34.5.6.8", {"start": v(130, 225.17) * mm, "end": v(120, 207.85) * mm, "construction": true});
            skLineSegment(sketch, "E34.6.0.0", {"start": v(130, -17.32) * mm, "end": v(150, -17.32) * mm, "construction": true});
            skLineSegment(sketch, "E34.6.0.1", {"start": v(140, 0) * mm, "end": v(130, -17.32) * mm, "construction": true});
            skLineSegment(sketch, "E34.6.0.2", {"start": v(150, -17.32) * mm, "end": v(140, 0) * mm, "construction": true});
            skLineSegment(sketch, "E34.6.0.3", {"start": v(120, 0) * mm, "end": v(140, 0) * mm, "construction": true});
            skLineSegment(sketch, "E34.6.0.4", {"start": v(130, -17.32) * mm, "end": v(120, 0) * mm, "construction": true});
            skLineSegment(sketch, "E34.6.0.5", {"start": v(130, 17.32) * mm, "end": v(120, 0) * mm, "construction": true});
            skLineSegment(sketch, "E34.6.0.6", {"start": v(140, 0) * mm, "end": v(130, 17.32) * mm, "construction": true});
            skLineSegment(sketch, "E34.6.0.7", {"start": v(130, 17.32) * mm, "end": v(150, 17.32) * mm, "construction": true});
            skLineSegment(sketch, "E34.6.0.8", {"start": v(150, 17.32) * mm, "end": v(140, 0) * mm, "construction": true});
            skLineSegment(sketch, "E34.6.1.0", {"start": v(130, 17.32) * mm, "end": v(150, 17.32) * mm, "construction": true});
            skLineSegment(sketch, "E34.6.1.1", {"start": v(140, 34.64) * mm, "end": v(130, 17.32) * mm, "construction": true});
            skLineSegment(sketch, "E34.6.1.2", {"start": v(150, 17.32) * mm, "end": v(140, 34.64) * mm, "construction": true});
            skLineSegment(sketch, "E34.6.1.3", {"start": v(120, 34.64) * mm, "end": v(140, 34.64) * mm, "construction": true});
            skLineSegment(sketch, "E34.6.1.4", {"start": v(130, 17.32) * mm, "end": v(120, 34.64) * mm, "construction": true});
            skLineSegment(sketch, "E34.6.1.5", {"start": v(130, 51.96) * mm, "end": v(120, 34.64) * mm, "construction": true});
            skLineSegment(sketch, "E34.6.1.6", {"start": v(140, 34.64) * mm, "end": v(130, 51.96) * mm, "construction": true});
            skLineSegment(sketch, "E34.6.1.7", {"start": v(130, 51.96) * mm, "end": v(150, 51.96) * mm, "construction": true});
            skLineSegment(sketch, "E34.6.1.8", {"start": v(150, 51.96) * mm, "end": v(140, 34.64) * mm, "construction": true});
            skLineSegment(sketch, "E34.6.2.0", {"start": v(130, 51.96) * mm, "end": v(150, 51.96) * mm, "construction": true});
            skLineSegment(sketch, "E34.6.2.1", {"start": v(140, 69.28) * mm, "end": v(130, 51.96) * mm, "construction": true});
            skLineSegment(sketch, "E34.6.2.2", {"start": v(150, 51.96) * mm, "end": v(140, 69.28) * mm, "construction": true});
            skLineSegment(sketch, "E34.6.2.3", {"start": v(120, 69.28) * mm, "end": v(140, 69.28) * mm, "construction": true});
            skLineSegment(sketch, "E34.6.2.4", {"start": v(130, 51.96) * mm, "end": v(120, 69.28) * mm, "construction": true});
            skLineSegment(sketch, "E34.6.2.5", {"start": v(130, 86.6) * mm, "end": v(120, 69.28) * mm, "construction": true});
            skLineSegment(sketch, "E34.6.2.6", {"start": v(140, 69.28) * mm, "end": v(130, 86.6) * mm, "construction": true});
            skLineSegment(sketch, "E34.6.2.7", {"start": v(130, 86.6) * mm, "end": v(150, 86.6) * mm, "construction": true});
            skLineSegment(sketch, "E34.6.2.8", {"start": v(150, 86.6) * mm, "end": v(140, 69.28) * mm, "construction": true});
            skLineSegment(sketch, "E34.6.3.0", {"start": v(130, 86.6) * mm, "end": v(150, 86.6) * mm, "construction": true});
            skLineSegment(sketch, "E34.6.3.1", {"start": v(140, 103.92) * mm, "end": v(130, 86.6) * mm, "construction": true});
            skLineSegment(sketch, "E34.6.3.2", {"start": v(150, 86.6) * mm, "end": v(140, 103.92) * mm, "construction": true});
            skLineSegment(sketch, "E34.6.3.3", {"start": v(120, 103.92) * mm, "end": v(140, 103.92) * mm, "construction": true});
            skLineSegment(sketch, "E34.6.3.4", {"start": v(130, 86.6) * mm, "end": v(120, 103.92) * mm, "construction": true});
            skLineSegment(sketch, "E34.6.3.5", {"start": v(130, 121.24) * mm, "end": v(120, 103.92) * mm, "construction": true});
            skLineSegment(sketch, "E34.6.3.6", {"start": v(140, 103.92) * mm, "end": v(130, 121.24) * mm, "construction": true});
            skLineSegment(sketch, "E34.6.3.7", {"start": v(130, 121.24) * mm, "end": v(150, 121.24) * mm, "construction": true});
            skLineSegment(sketch, "E34.6.3.8", {"start": v(150, 121.24) * mm, "end": v(140, 103.92) * mm, "construction": true});
            skLineSegment(sketch, "E34.6.4.0", {"start": v(130, 121.24) * mm, "end": v(150, 121.24) * mm, "construction": true});
            skLineSegment(sketch, "E34.6.4.1", {"start": v(140, 138.56) * mm, "end": v(130, 121.24) * mm, "construction": true});
            skLineSegment(sketch, "E34.6.4.2", {"start": v(150, 121.24) * mm, "end": v(140, 138.56) * mm, "construction": true});
            skLineSegment(sketch, "E34.6.4.3", {"start": v(120, 138.56) * mm, "end": v(140, 138.56) * mm, "construction": true});
            skLineSegment(sketch, "E34.6.4.4", {"start": v(130, 121.24) * mm, "end": v(120, 138.56) * mm, "construction": true});
            skLineSegment(sketch, "E34.6.4.5", {"start": v(130, 155.88) * mm, "end": v(120, 138.56) * mm, "construction": true});
            skLineSegment(sketch, "E34.6.4.6", {"start": v(140, 138.56) * mm, "end": v(130, 155.88) * mm, "construction": true});
            skLineSegment(sketch, "E34.6.4.7", {"start": v(130, 155.88) * mm, "end": v(150, 155.88) * mm, "construction": true});
            skLineSegment(sketch, "E34.6.4.8", {"start": v(150, 155.88) * mm, "end": v(140, 138.56) * mm, "construction": true});
            skLineSegment(sketch, "E34.6.5.0", {"start": v(130, 155.88) * mm, "end": v(150, 155.88) * mm, "construction": true});
            skLineSegment(sketch, "E34.6.5.1", {"start": v(140, 173.2) * mm, "end": v(130, 155.88) * mm, "construction": true});
            skLineSegment(sketch, "E34.6.5.2", {"start": v(150, 155.88) * mm, "end": v(140, 173.2) * mm, "construction": true});
            skLineSegment(sketch, "E34.6.5.3", {"start": v(120, 173.2) * mm, "end": v(140, 173.2) * mm, "construction": true});
            skLineSegment(sketch, "E34.6.5.4", {"start": v(130, 155.88) * mm, "end": v(120, 173.2) * mm, "construction": true});
            skLineSegment(sketch, "E34.6.5.5", {"start": v(130, 190.53) * mm, "end": v(120, 173.2) * mm, "construction": true});
            skLineSegment(sketch, "E34.6.5.6", {"start": v(140, 173.2) * mm, "end": v(130, 190.53) * mm, "construction": true});
            skLineSegment(sketch, "E34.6.5.7", {"start": v(130, 190.53) * mm, "end": v(150, 190.53) * mm, "construction": true});
            skLineSegment(sketch, "E34.6.5.8", {"start": v(150, 190.53) * mm, "end": v(140, 173.2) * mm, "construction": true});
            skLineSegment(sketch, "E34.6.6.0", {"start": v(130, 190.53) * mm, "end": v(150, 190.53) * mm, "construction": true});
            skLineSegment(sketch, "E34.6.6.1", {"start": v(140, 207.85) * mm, "end": v(130, 190.53) * mm, "construction": true});
            skLineSegment(sketch, "E34.6.6.2", {"start": v(150, 190.53) * mm, "end": v(140, 207.85) * mm, "construction": true});
            skLineSegment(sketch, "E34.6.6.3", {"start": v(120, 207.85) * mm, "end": v(140, 207.85) * mm, "construction": true});
            skLineSegment(sketch, "E34.6.6.4", {"start": v(130, 190.53) * mm, "end": v(120, 207.85) * mm, "construction": true});
            skLineSegment(sketch, "E34.6.6.5", {"start": v(130, 225.17) * mm, "end": v(120, 207.85) * mm, "construction": true});
            skLineSegment(sketch, "E34.6.6.6", {"start": v(140, 207.85) * mm, "end": v(130, 225.17) * mm, "construction": true});
            skLineSegment(sketch, "E34.6.6.7", {"start": v(130, 225.17) * mm, "end": v(150, 225.17) * mm, "construction": true});
            skLineSegment(sketch, "E34.6.6.8", {"start": v(150, 225.17) * mm, "end": v(140, 207.85) * mm, "construction": true});
            skLineSegment(sketch, "E34.7.0.0", {"start": v(150, -17.32) * mm, "end": v(170, -17.32) * mm, "construction": true});
            skLineSegment(sketch, "E34.7.0.1", {"start": v(160, 0) * mm, "end": v(150, -17.32) * mm, "construction": true});
            skLineSegment(sketch, "E34.7.0.2", {"start": v(170, -17.32) * mm, "end": v(160, 0) * mm, "construction": true});
            skLineSegment(sketch, "E34.7.0.3", {"start": v(140, 0) * mm, "end": v(160, 0) * mm, "construction": true});
            skLineSegment(sketch, "E34.7.0.4", {"start": v(150, -17.32) * mm, "end": v(140, 0) * mm, "construction": true});
            skLineSegment(sketch, "E34.7.0.5", {"start": v(150, 17.32) * mm, "end": v(140, 0) * mm, "construction": true});
            skLineSegment(sketch, "E34.7.0.6", {"start": v(160, 0) * mm, "end": v(150, 17.32) * mm, "construction": true});
            skLineSegment(sketch, "E34.7.0.7", {"start": v(150, 17.32) * mm, "end": v(170, 17.32) * mm, "construction": true});
            skLineSegment(sketch, "E34.7.0.8", {"start": v(170, 17.32) * mm, "end": v(160, 0) * mm, "construction": true});
            skLineSegment(sketch, "E34.7.1.0", {"start": v(150, 17.32) * mm, "end": v(170, 17.32) * mm, "construction": true});
            skLineSegment(sketch, "E34.7.1.1", {"start": v(160, 34.64) * mm, "end": v(150, 17.32) * mm, "construction": true});
            skLineSegment(sketch, "E34.7.1.2", {"start": v(170, 17.32) * mm, "end": v(160, 34.64) * mm, "construction": true});
            skLineSegment(sketch, "E34.7.1.3", {"start": v(140, 34.64) * mm, "end": v(160, 34.64) * mm, "construction": true});
            skLineSegment(sketch, "E34.7.1.4", {"start": v(150, 17.32) * mm, "end": v(140, 34.64) * mm, "construction": true});
            skLineSegment(sketch, "E34.7.1.5", {"start": v(150, 51.96) * mm, "end": v(140, 34.64) * mm, "construction": true});
            skLineSegment(sketch, "E34.7.1.6", {"start": v(160, 34.64) * mm, "end": v(150, 51.96) * mm, "construction": true});
            skLineSegment(sketch, "E34.7.1.7", {"start": v(150, 51.96) * mm, "end": v(170, 51.96) * mm, "construction": true});
            skLineSegment(sketch, "E34.7.1.8", {"start": v(170, 51.96) * mm, "end": v(160, 34.64) * mm, "construction": true});
            skLineSegment(sketch, "E34.7.2.0", {"start": v(150, 51.96) * mm, "end": v(170, 51.96) * mm, "construction": true});
            skLineSegment(sketch, "E34.7.2.1", {"start": v(160, 69.28) * mm, "end": v(150, 51.96) * mm, "construction": true});
            skLineSegment(sketch, "E34.7.2.2", {"start": v(170, 51.96) * mm, "end": v(160, 69.28) * mm, "construction": true});
            skLineSegment(sketch, "E34.7.2.3", {"start": v(140, 69.28) * mm, "end": v(160, 69.28) * mm, "construction": true});
            skLineSegment(sketch, "E34.7.2.4", {"start": v(150, 51.96) * mm, "end": v(140, 69.28) * mm, "construction": true});
            skLineSegment(sketch, "E34.7.2.5", {"start": v(150, 86.6) * mm, "end": v(140, 69.28) * mm, "construction": true});
            skLineSegment(sketch, "E34.7.2.6", {"start": v(160, 69.28) * mm, "end": v(150, 86.6) * mm, "construction": true});
            skLineSegment(sketch, "E34.7.2.7", {"start": v(150, 86.6) * mm, "end": v(170, 86.6) * mm, "construction": true});
            skLineSegment(sketch, "E34.7.2.8", {"start": v(170, 86.6) * mm, "end": v(160, 69.28) * mm, "construction": true});
            skLineSegment(sketch, "E34.7.3.0", {"start": v(150, 86.6) * mm, "end": v(170, 86.6) * mm, "construction": true});
            skLineSegment(sketch, "E34.7.3.1", {"start": v(160, 103.92) * mm, "end": v(150, 86.6) * mm, "construction": true});
            skLineSegment(sketch, "E34.7.3.2", {"start": v(170, 86.6) * mm, "end": v(160, 103.92) * mm, "construction": true});
            skLineSegment(sketch, "E34.7.3.3", {"start": v(140, 103.92) * mm, "end": v(160, 103.92) * mm, "construction": true});
            skLineSegment(sketch, "E34.7.3.4", {"start": v(150, 86.6) * mm, "end": v(140, 103.92) * mm, "construction": true});
            skLineSegment(sketch, "E34.7.3.5", {"start": v(150, 121.24) * mm, "end": v(140, 103.92) * mm, "construction": true});
            skLineSegment(sketch, "E34.7.3.6", {"start": v(160, 103.92) * mm, "end": v(150, 121.24) * mm, "construction": true});
            skLineSegment(sketch, "E34.7.3.7", {"start": v(150, 121.24) * mm, "end": v(170, 121.24) * mm, "construction": true});
            skLineSegment(sketch, "E34.7.3.8", {"start": v(170, 121.24) * mm, "end": v(160, 103.92) * mm, "construction": true});
            skLineSegment(sketch, "E34.7.4.0", {"start": v(150, 121.24) * mm, "end": v(170, 121.24) * mm, "construction": true});
            skLineSegment(sketch, "E34.7.4.1", {"start": v(160, 138.56) * mm, "end": v(150, 121.24) * mm, "construction": true});
            skLineSegment(sketch, "E34.7.4.2", {"start": v(170, 121.24) * mm, "end": v(160, 138.56) * mm, "construction": true});
            skLineSegment(sketch, "E34.7.4.3", {"start": v(140, 138.56) * mm, "end": v(160, 138.56) * mm, "construction": true});
            skLineSegment(sketch, "E34.7.4.4", {"start": v(150, 121.24) * mm, "end": v(140, 138.56) * mm, "construction": true});
            skLineSegment(sketch, "E34.7.4.5", {"start": v(150, 155.88) * mm, "end": v(140, 138.56) * mm, "construction": true});
            skLineSegment(sketch, "E34.7.4.6", {"start": v(160, 138.56) * mm, "end": v(150, 155.88) * mm, "construction": true});
            skLineSegment(sketch, "E34.7.4.7", {"start": v(150, 155.88) * mm, "end": v(170, 155.88) * mm, "construction": true});
            skLineSegment(sketch, "E34.7.4.8", {"start": v(170, 155.88) * mm, "end": v(160, 138.56) * mm, "construction": true});
            skLineSegment(sketch, "E34.7.5.0", {"start": v(150, 155.88) * mm, "end": v(170, 155.88) * mm, "construction": true});
            skLineSegment(sketch, "E34.7.5.1", {"start": v(160, 173.2) * mm, "end": v(150, 155.88) * mm, "construction": true});
            skLineSegment(sketch, "E34.7.5.2", {"start": v(170, 155.88) * mm, "end": v(160, 173.2) * mm, "construction": true});
            skLineSegment(sketch, "E34.7.5.3", {"start": v(140, 173.2) * mm, "end": v(160, 173.2) * mm, "construction": true});
            skLineSegment(sketch, "E34.7.5.4", {"start": v(150, 155.88) * mm, "end": v(140, 173.2) * mm, "construction": true});
            skLineSegment(sketch, "E34.7.5.5", {"start": v(150, 190.53) * mm, "end": v(140, 173.2) * mm, "construction": true});
            skLineSegment(sketch, "E34.7.5.6", {"start": v(160, 173.2) * mm, "end": v(150, 190.53) * mm, "construction": true});
            skLineSegment(sketch, "E34.7.5.7", {"start": v(150, 190.53) * mm, "end": v(170, 190.53) * mm, "construction": true});
            skLineSegment(sketch, "E34.7.5.8", {"start": v(170, 190.53) * mm, "end": v(160, 173.2) * mm, "construction": true});
            skLineSegment(sketch, "E34.7.6.0", {"start": v(150, 190.53) * mm, "end": v(170, 190.53) * mm, "construction": true});
            skLineSegment(sketch, "E34.7.6.1", {"start": v(160, 207.85) * mm, "end": v(150, 190.53) * mm, "construction": true});
            skLineSegment(sketch, "E34.7.6.2", {"start": v(170, 190.53) * mm, "end": v(160, 207.85) * mm, "construction": true});
            skLineSegment(sketch, "E34.7.6.3", {"start": v(140, 207.85) * mm, "end": v(160, 207.85) * mm, "construction": true});
            skLineSegment(sketch, "E34.7.6.4", {"start": v(150, 190.53) * mm, "end": v(140, 207.85) * mm, "construction": true});
            skLineSegment(sketch, "E34.7.6.5", {"start": v(150, 225.17) * mm, "end": v(140, 207.85) * mm, "construction": true});
            skLineSegment(sketch, "E34.7.6.6", {"start": v(160, 207.85) * mm, "end": v(150, 225.17) * mm, "construction": true});
            skLineSegment(sketch, "E34.7.6.7", {"start": v(150, 225.17) * mm, "end": v(170, 225.17) * mm, "construction": true});
            skLineSegment(sketch, "E34.7.6.8", {"start": v(170, 225.17) * mm, "end": v(160, 207.85) * mm, "construction": true});
            skLineSegment(sketch, "E34.8.0.0", {"start": v(170, -17.32) * mm, "end": v(190, -17.32) * mm, "construction": true});
            skLineSegment(sketch, "E34.8.0.1", {"start": v(180, 0) * mm, "end": v(170, -17.32) * mm, "construction": true});
            skLineSegment(sketch, "E34.8.0.2", {"start": v(190, -17.32) * mm, "end": v(180, 0) * mm, "construction": true});
            skLineSegment(sketch, "E34.8.0.3", {"start": v(160, 0) * mm, "end": v(180, 0) * mm, "construction": true});
            skLineSegment(sketch, "E34.8.0.4", {"start": v(170, -17.32) * mm, "end": v(160, 0) * mm, "construction": true});
            skLineSegment(sketch, "E34.8.0.5", {"start": v(170, 17.32) * mm, "end": v(160, 0) * mm, "construction": true});
            skLineSegment(sketch, "E34.8.0.6", {"start": v(180, 0) * mm, "end": v(170, 17.32) * mm, "construction": true});
            skLineSegment(sketch, "E34.8.0.7", {"start": v(170, 17.32) * mm, "end": v(190, 17.32) * mm, "construction": true});
            skLineSegment(sketch, "E34.8.0.8", {"start": v(190, 17.32) * mm, "end": v(180, 0) * mm, "construction": true});
            skLineSegment(sketch, "E34.8.1.0", {"start": v(170, 17.32) * mm, "end": v(190, 17.32) * mm, "construction": true});
            skLineSegment(sketch, "E34.8.1.1", {"start": v(180, 34.64) * mm, "end": v(170, 17.32) * mm, "construction": true});
            skLineSegment(sketch, "E34.8.1.2", {"start": v(190, 17.32) * mm, "end": v(180, 34.64) * mm, "construction": true});
            skLineSegment(sketch, "E34.8.1.3", {"start": v(160, 34.64) * mm, "end": v(180, 34.64) * mm, "construction": true});
            skLineSegment(sketch, "E34.8.1.4", {"start": v(170, 17.32) * mm, "end": v(160, 34.64) * mm, "construction": true});
            skLineSegment(sketch, "E34.8.1.5", {"start": v(170, 51.96) * mm, "end": v(160, 34.64) * mm, "construction": true});
            skLineSegment(sketch, "E34.8.1.6", {"start": v(180, 34.64) * mm, "end": v(170, 51.96) * mm, "construction": true});
            skLineSegment(sketch, "E34.8.1.7", {"start": v(170, 51.96) * mm, "end": v(190, 51.96) * mm, "construction": true});
            skLineSegment(sketch, "E34.8.1.8", {"start": v(190, 51.96) * mm, "end": v(180, 34.64) * mm, "construction": true});
            skLineSegment(sketch, "E34.8.2.0", {"start": v(170, 51.96) * mm, "end": v(190, 51.96) * mm, "construction": true});
            skLineSegment(sketch, "E34.8.2.1", {"start": v(180, 69.28) * mm, "end": v(170, 51.96) * mm, "construction": true});
            skLineSegment(sketch, "E34.8.2.2", {"start": v(190, 51.96) * mm, "end": v(180, 69.28) * mm, "construction": true});
            skLineSegment(sketch, "E34.8.2.3", {"start": v(160, 69.28) * mm, "end": v(180, 69.28) * mm, "construction": true});
            skLineSegment(sketch, "E34.8.2.4", {"start": v(170, 51.96) * mm, "end": v(160, 69.28) * mm, "construction": true});
            skLineSegment(sketch, "E34.8.2.5", {"start": v(170, 86.6) * mm, "end": v(160, 69.28) * mm, "construction": true});
            skLineSegment(sketch, "E34.8.2.6", {"start": v(180, 69.28) * mm, "end": v(170, 86.6) * mm, "construction": true});
            skLineSegment(sketch, "E34.8.2.7", {"start": v(170, 86.6) * mm, "end": v(190, 86.6) * mm, "construction": true});
            skLineSegment(sketch, "E34.8.2.8", {"start": v(190, 86.6) * mm, "end": v(180, 69.28) * mm, "construction": true});
            skLineSegment(sketch, "E34.8.3.0", {"start": v(170, 86.6) * mm, "end": v(190, 86.6) * mm, "construction": true});
            skLineSegment(sketch, "E34.8.3.1", {"start": v(180, 103.92) * mm, "end": v(170, 86.6) * mm, "construction": true});
            skLineSegment(sketch, "E34.8.3.2", {"start": v(190, 86.6) * mm, "end": v(180, 103.92) * mm, "construction": true});
            skLineSegment(sketch, "E34.8.3.3", {"start": v(160, 103.92) * mm, "end": v(180, 103.92) * mm, "construction": true});
            skLineSegment(sketch, "E34.8.3.4", {"start": v(170, 86.6) * mm, "end": v(160, 103.92) * mm, "construction": true});
            skLineSegment(sketch, "E34.8.3.5", {"start": v(170, 121.24) * mm, "end": v(160, 103.92) * mm, "construction": true});
            skLineSegment(sketch, "E34.8.3.6", {"start": v(180, 103.92) * mm, "end": v(170, 121.24) * mm, "construction": true});
            skLineSegment(sketch, "E34.8.3.7", {"start": v(170, 121.24) * mm, "end": v(190, 121.24) * mm, "construction": true});
            skLineSegment(sketch, "E34.8.3.8", {"start": v(190, 121.24) * mm, "end": v(180, 103.92) * mm, "construction": true});
            skLineSegment(sketch, "E34.8.4.0", {"start": v(170, 121.24) * mm, "end": v(190, 121.24) * mm, "construction": true});
            skLineSegment(sketch, "E34.8.4.1", {"start": v(180, 138.56) * mm, "end": v(170, 121.24) * mm, "construction": true});
            skLineSegment(sketch, "E34.8.4.2", {"start": v(190, 121.24) * mm, "end": v(180, 138.56) * mm, "construction": true});
            skLineSegment(sketch, "E34.8.4.3", {"start": v(160, 138.56) * mm, "end": v(180, 138.56) * mm, "construction": true});
            skLineSegment(sketch, "E34.8.4.4", {"start": v(170, 121.24) * mm, "end": v(160, 138.56) * mm, "construction": true});
            skLineSegment(sketch, "E34.8.4.5", {"start": v(170, 155.88) * mm, "end": v(160, 138.56) * mm, "construction": true});
            skLineSegment(sketch, "E34.8.4.6", {"start": v(180, 138.56) * mm, "end": v(170, 155.88) * mm, "construction": true});
            skLineSegment(sketch, "E34.8.4.7", {"start": v(170, 155.88) * mm, "end": v(190, 155.88) * mm, "construction": true});
            skLineSegment(sketch, "E34.8.4.8", {"start": v(190, 155.88) * mm, "end": v(180, 138.56) * mm, "construction": true});
            skLineSegment(sketch, "E34.8.5.0", {"start": v(170, 155.88) * mm, "end": v(190, 155.88) * mm, "construction": true});
            skLineSegment(sketch, "E34.8.5.1", {"start": v(180, 173.2) * mm, "end": v(170, 155.88) * mm, "construction": true});
            skLineSegment(sketch, "E34.8.5.2", {"start": v(190, 155.88) * mm, "end": v(180, 173.2) * mm, "construction": true});
            skLineSegment(sketch, "E34.8.5.3", {"start": v(160, 173.2) * mm, "end": v(180, 173.2) * mm, "construction": true});
            skLineSegment(sketch, "E34.8.5.4", {"start": v(170, 155.88) * mm, "end": v(160, 173.2) * mm, "construction": true});
            skLineSegment(sketch, "E34.8.5.5", {"start": v(170, 190.53) * mm, "end": v(160, 173.2) * mm, "construction": true});
            skLineSegment(sketch, "E34.8.5.6", {"start": v(180, 173.2) * mm, "end": v(170, 190.53) * mm, "construction": true});
            skLineSegment(sketch, "E34.8.5.7", {"start": v(170, 190.53) * mm, "end": v(190, 190.53) * mm, "construction": true});
            skLineSegment(sketch, "E34.8.5.8", {"start": v(190, 190.53) * mm, "end": v(180, 173.2) * mm, "construction": true});
            skLineSegment(sketch, "E34.8.6.0", {"start": v(170, 190.53) * mm, "end": v(190, 190.53) * mm, "construction": true});
            skLineSegment(sketch, "E34.8.6.1", {"start": v(180, 207.85) * mm, "end": v(170, 190.53) * mm, "construction": true});
            skLineSegment(sketch, "E34.8.6.2", {"start": v(190, 190.53) * mm, "end": v(180, 207.85) * mm, "construction": true});
            skLineSegment(sketch, "E34.8.6.3", {"start": v(160, 207.85) * mm, "end": v(180, 207.85) * mm, "construction": true});
            skLineSegment(sketch, "E34.8.6.4", {"start": v(170, 190.53) * mm, "end": v(160, 207.85) * mm, "construction": true});
            skLineSegment(sketch, "E34.8.6.5", {"start": v(170, 225.17) * mm, "end": v(160, 207.85) * mm, "construction": true});
            skLineSegment(sketch, "E34.8.6.6", {"start": v(180, 207.85) * mm, "end": v(170, 225.17) * mm, "construction": true});
            skLineSegment(sketch, "E34.8.6.7", {"start": v(170, 225.17) * mm, "end": v(190, 225.17) * mm, "construction": true});
            skLineSegment(sketch, "E34.8.6.8", {"start": v(190, 225.17) * mm, "end": v(180, 207.85) * mm, "construction": true});
            skLineSegment(sketch, "E34.9.0.0", {"start": v(190, -17.32) * mm, "end": v(210, -17.32) * mm, "construction": true});
            skLineSegment(sketch, "E34.9.0.1", {"start": v(200, 0) * mm, "end": v(190, -17.32) * mm, "construction": true});
            skLineSegment(sketch, "E34.9.0.2", {"start": v(210, -17.32) * mm, "end": v(200, 0) * mm, "construction": true});
            skLineSegment(sketch, "E34.9.0.3", {"start": v(180, 0) * mm, "end": v(200, 0) * mm, "construction": true});
            skLineSegment(sketch, "E34.9.0.4", {"start": v(190, -17.32) * mm, "end": v(180, 0) * mm, "construction": true});
            skLineSegment(sketch, "E34.9.0.5", {"start": v(190, 17.32) * mm, "end": v(180, 0) * mm, "construction": true});
            skLineSegment(sketch, "E34.9.0.6", {"start": v(200, 0) * mm, "end": v(190, 17.32) * mm, "construction": true});
            skLineSegment(sketch, "E34.9.0.7", {"start": v(190, 17.32) * mm, "end": v(210, 17.32) * mm, "construction": true});
            skLineSegment(sketch, "E34.9.0.8", {"start": v(210, 17.32) * mm, "end": v(200, 0) * mm, "construction": true});
            skLineSegment(sketch, "E34.9.1.0", {"start": v(190, 17.32) * mm, "end": v(210, 17.32) * mm, "construction": true});
            skLineSegment(sketch, "E34.9.1.1", {"start": v(200, 34.64) * mm, "end": v(190, 17.32) * mm, "construction": true});
            skLineSegment(sketch, "E34.9.1.2", {"start": v(210, 17.32) * mm, "end": v(200, 34.64) * mm, "construction": true});
            skLineSegment(sketch, "E34.9.1.3", {"start": v(180, 34.64) * mm, "end": v(200, 34.64) * mm, "construction": true});
            skLineSegment(sketch, "E34.9.1.4", {"start": v(190, 17.32) * mm, "end": v(180, 34.64) * mm, "construction": true});
            skLineSegment(sketch, "E34.9.1.5", {"start": v(190, 51.96) * mm, "end": v(180, 34.64) * mm, "construction": true});
            skLineSegment(sketch, "E34.9.1.6", {"start": v(200, 34.64) * mm, "end": v(190, 51.96) * mm, "construction": true});
            skLineSegment(sketch, "E34.9.1.7", {"start": v(190, 51.96) * mm, "end": v(210, 51.96) * mm, "construction": true});
            skLineSegment(sketch, "E34.9.1.8", {"start": v(210, 51.96) * mm, "end": v(200, 34.64) * mm, "construction": true});
            skLineSegment(sketch, "E34.9.2.0", {"start": v(190, 51.96) * mm, "end": v(210, 51.96) * mm, "construction": true});
            skLineSegment(sketch, "E34.9.2.1", {"start": v(200, 69.28) * mm, "end": v(190, 51.96) * mm, "construction": true});
            skLineSegment(sketch, "E34.9.2.2", {"start": v(210, 51.96) * mm, "end": v(200, 69.28) * mm, "construction": true});
            skLineSegment(sketch, "E34.9.2.3", {"start": v(180, 69.28) * mm, "end": v(200, 69.28) * mm, "construction": true});
            skLineSegment(sketch, "E34.9.2.4", {"start": v(190, 51.96) * mm, "end": v(180, 69.28) * mm, "construction": true});
            skLineSegment(sketch, "E34.9.2.5", {"start": v(190, 86.6) * mm, "end": v(180, 69.28) * mm, "construction": true});
            skLineSegment(sketch, "E34.9.2.6", {"start": v(200, 69.28) * mm, "end": v(190, 86.6) * mm, "construction": true});
            skLineSegment(sketch, "E34.9.2.7", {"start": v(190, 86.6) * mm, "end": v(210, 86.6) * mm, "construction": true});
            skLineSegment(sketch, "E34.9.2.8", {"start": v(210, 86.6) * mm, "end": v(200, 69.28) * mm, "construction": true});
            skLineSegment(sketch, "E34.9.3.0", {"start": v(190, 86.6) * mm, "end": v(210, 86.6) * mm, "construction": true});
            skLineSegment(sketch, "E34.9.3.1", {"start": v(200, 103.92) * mm, "end": v(190, 86.6) * mm, "construction": true});
            skLineSegment(sketch, "E34.9.3.2", {"start": v(210, 86.6) * mm, "end": v(200, 103.92) * mm, "construction": true});
            skLineSegment(sketch, "E34.9.3.3", {"start": v(180, 103.92) * mm, "end": v(200, 103.92) * mm, "construction": true});
            skLineSegment(sketch, "E34.9.3.4", {"start": v(190, 86.6) * mm, "end": v(180, 103.92) * mm, "construction": true});
            skLineSegment(sketch, "E34.9.3.5", {"start": v(190, 121.24) * mm, "end": v(180, 103.92) * mm, "construction": true});
            skLineSegment(sketch, "E34.9.3.6", {"start": v(200, 103.92) * mm, "end": v(190, 121.24) * mm, "construction": true});
            skLineSegment(sketch, "E34.9.3.7", {"start": v(190, 121.24) * mm, "end": v(210, 121.24) * mm, "construction": true});
            skLineSegment(sketch, "E34.9.3.8", {"start": v(210, 121.24) * mm, "end": v(200, 103.92) * mm, "construction": true});
            skLineSegment(sketch, "E34.9.4.0", {"start": v(190, 121.24) * mm, "end": v(210, 121.24) * mm, "construction": true});
            skLineSegment(sketch, "E34.9.4.1", {"start": v(200, 138.56) * mm, "end": v(190, 121.24) * mm, "construction": true});
            skLineSegment(sketch, "E34.9.4.2", {"start": v(210, 121.24) * mm, "end": v(200, 138.56) * mm, "construction": true});
            skLineSegment(sketch, "E34.9.4.3", {"start": v(180, 138.56) * mm, "end": v(200, 138.56) * mm, "construction": true});
            skLineSegment(sketch, "E34.9.4.4", {"start": v(190, 121.24) * mm, "end": v(180, 138.56) * mm, "construction": true});
            skLineSegment(sketch, "E34.9.4.5", {"start": v(190, 155.88) * mm, "end": v(180, 138.56) * mm, "construction": true});
            skLineSegment(sketch, "E34.9.4.6", {"start": v(200, 138.56) * mm, "end": v(190, 155.88) * mm, "construction": true});
            skLineSegment(sketch, "E34.9.4.7", {"start": v(190, 155.88) * mm, "end": v(210, 155.88) * mm, "construction": true});
            skLineSegment(sketch, "E34.9.4.8", {"start": v(210, 155.88) * mm, "end": v(200, 138.56) * mm, "construction": true});
            skLineSegment(sketch, "E34.9.5.0", {"start": v(190, 155.88) * mm, "end": v(210, 155.88) * mm, "construction": true});
            skLineSegment(sketch, "E34.9.5.1", {"start": v(200, 173.2) * mm, "end": v(190, 155.88) * mm, "construction": true});
            skLineSegment(sketch, "E34.9.5.2", {"start": v(210, 155.88) * mm, "end": v(200, 173.2) * mm, "construction": true});
            skLineSegment(sketch, "E34.9.5.3", {"start": v(180, 173.2) * mm, "end": v(200, 173.2) * mm, "construction": true});
            skLineSegment(sketch, "E34.9.5.4", {"start": v(190, 155.88) * mm, "end": v(180, 173.2) * mm, "construction": true});
            skLineSegment(sketch, "E34.9.5.5", {"start": v(190, 190.53) * mm, "end": v(180, 173.2) * mm, "construction": true});
            skLineSegment(sketch, "E34.9.5.6", {"start": v(200, 173.2) * mm, "end": v(190, 190.53) * mm, "construction": true});
            skLineSegment(sketch, "E34.9.5.7", {"start": v(190, 190.53) * mm, "end": v(210, 190.53) * mm, "construction": true});
            skLineSegment(sketch, "E34.9.5.8", {"start": v(210, 190.53) * mm, "end": v(200, 173.2) * mm, "construction": true});
            skLineSegment(sketch, "E34.9.6.0", {"start": v(190, 190.53) * mm, "end": v(210, 190.53) * mm, "construction": true});
            skLineSegment(sketch, "E34.9.6.1", {"start": v(200, 207.85) * mm, "end": v(190, 190.53) * mm, "construction": true});
            skLineSegment(sketch, "E34.9.6.2", {"start": v(210, 190.53) * mm, "end": v(200, 207.85) * mm, "construction": true});
            skLineSegment(sketch, "E34.9.6.3", {"start": v(180, 207.85) * mm, "end": v(200, 207.85) * mm, "construction": true});
            skLineSegment(sketch, "E34.9.6.4", {"start": v(190, 190.53) * mm, "end": v(180, 207.85) * mm, "construction": true});
            skLineSegment(sketch, "E34.9.6.5", {"start": v(190, 225.17) * mm, "end": v(180, 207.85) * mm, "construction": true});
            skLineSegment(sketch, "E34.9.6.6", {"start": v(200, 207.85) * mm, "end": v(190, 225.17) * mm, "construction": true});
            skLineSegment(sketch, "E34.9.6.7", {"start": v(190, 225.17) * mm, "end": v(210, 225.17) * mm, "construction": true});
            skLineSegment(sketch, "E34.9.6.8", {"start": v(210, 225.17) * mm, "end": v(200, 207.85) * mm, "construction": true});
            skLineSegment(sketch, "E34.10.0.0", {"start": v(210, -17.32) * mm, "end": v(230, -17.32) * mm, "construction": true});
            skLineSegment(sketch, "E34.10.0.1", {"start": v(220, 0) * mm, "end": v(210, -17.32) * mm, "construction": true});
            skLineSegment(sketch, "E34.10.0.2", {"start": v(230, -17.32) * mm, "end": v(220, 0) * mm, "construction": true});
            skLineSegment(sketch, "E34.10.0.3", {"start": v(200, 0) * mm, "end": v(220, 0) * mm, "construction": true});
            skLineSegment(sketch, "E34.10.0.4", {"start": v(210, -17.32) * mm, "end": v(200, 0) * mm, "construction": true});
            skLineSegment(sketch, "E34.10.0.5", {"start": v(210, 17.32) * mm, "end": v(200, 0) * mm, "construction": true});
            skLineSegment(sketch, "E34.10.0.6", {"start": v(220, 0) * mm, "end": v(210, 17.32) * mm, "construction": true});
            skLineSegment(sketch, "E34.10.0.7", {"start": v(210, 17.32) * mm, "end": v(230, 17.32) * mm, "construction": true});
            skLineSegment(sketch, "E34.10.0.8", {"start": v(230, 17.32) * mm, "end": v(220, 0) * mm, "construction": true});
            skLineSegment(sketch, "E34.10.1.0", {"start": v(210, 17.32) * mm, "end": v(230, 17.32) * mm, "construction": true});
            skLineSegment(sketch, "E34.10.1.1", {"start": v(220, 34.64) * mm, "end": v(210, 17.32) * mm, "construction": true});
            skLineSegment(sketch, "E34.10.1.2", {"start": v(230, 17.32) * mm, "end": v(220, 34.64) * mm, "construction": true});
            skLineSegment(sketch, "E34.10.1.3", {"start": v(200, 34.64) * mm, "end": v(220, 34.64) * mm, "construction": true});
            skLineSegment(sketch, "E34.10.1.4", {"start": v(210, 17.32) * mm, "end": v(200, 34.64) * mm, "construction": true});
            skLineSegment(sketch, "E34.10.1.5", {"start": v(210, 51.96) * mm, "end": v(200, 34.64) * mm, "construction": true});
            skLineSegment(sketch, "E34.10.1.6", {"start": v(220, 34.64) * mm, "end": v(210, 51.96) * mm, "construction": true});
            skLineSegment(sketch, "E34.10.1.7", {"start": v(210, 51.96) * mm, "end": v(230, 51.96) * mm, "construction": true});
            skLineSegment(sketch, "E34.10.1.8", {"start": v(230, 51.96) * mm, "end": v(220, 34.64) * mm, "construction": true});
            skLineSegment(sketch, "E34.10.2.0", {"start": v(210, 51.96) * mm, "end": v(230, 51.96) * mm, "construction": true});
            skLineSegment(sketch, "E34.10.2.1", {"start": v(220, 69.28) * mm, "end": v(210, 51.96) * mm, "construction": true});
            skLineSegment(sketch, "E34.10.2.2", {"start": v(230, 51.96) * mm, "end": v(220, 69.28) * mm, "construction": true});
            skLineSegment(sketch, "E34.10.2.3", {"start": v(200, 69.28) * mm, "end": v(220, 69.28) * mm, "construction": true});
            skLineSegment(sketch, "E34.10.2.4", {"start": v(210, 51.96) * mm, "end": v(200, 69.28) * mm, "construction": true});
            skLineSegment(sketch, "E34.10.2.5", {"start": v(210, 86.6) * mm, "end": v(200, 69.28) * mm, "construction": true});
            skLineSegment(sketch, "E34.10.2.6", {"start": v(220, 69.28) * mm, "end": v(210, 86.6) * mm, "construction": true});
            skLineSegment(sketch, "E34.10.2.7", {"start": v(210, 86.6) * mm, "end": v(230, 86.6) * mm, "construction": true});
            skLineSegment(sketch, "E34.10.2.8", {"start": v(230, 86.6) * mm, "end": v(220, 69.28) * mm, "construction": true});
            skLineSegment(sketch, "E34.10.3.0", {"start": v(210, 86.6) * mm, "end": v(230, 86.6) * mm, "construction": true});
            skLineSegment(sketch, "E34.10.3.1", {"start": v(220, 103.92) * mm, "end": v(210, 86.6) * mm, "construction": true});
            skLineSegment(sketch, "E34.10.3.2", {"start": v(230, 86.6) * mm, "end": v(220, 103.92) * mm, "construction": true});
            skLineSegment(sketch, "E34.10.3.3", {"start": v(200, 103.92) * mm, "end": v(220, 103.92) * mm, "construction": true});
            skLineSegment(sketch, "E34.10.3.4", {"start": v(210, 86.6) * mm, "end": v(200, 103.92) * mm, "construction": true});
            skLineSegment(sketch, "E34.10.3.5", {"start": v(210, 121.24) * mm, "end": v(200, 103.92) * mm, "construction": true});
            skLineSegment(sketch, "E34.10.3.6", {"start": v(220, 103.92) * mm, "end": v(210, 121.24) * mm, "construction": true});
            skLineSegment(sketch, "E34.10.3.7", {"start": v(210, 121.24) * mm, "end": v(230, 121.24) * mm, "construction": true});
            skLineSegment(sketch, "E34.10.3.8", {"start": v(230, 121.24) * mm, "end": v(220, 103.92) * mm, "construction": true});
            skLineSegment(sketch, "E34.10.4.0", {"start": v(210, 121.24) * mm, "end": v(230, 121.24) * mm, "construction": true});
            skLineSegment(sketch, "E34.10.4.1", {"start": v(220, 138.56) * mm, "end": v(210, 121.24) * mm, "construction": true});
            skLineSegment(sketch, "E34.10.4.2", {"start": v(230, 121.24) * mm, "end": v(220, 138.56) * mm, "construction": true});
            skLineSegment(sketch, "E34.10.4.3", {"start": v(200, 138.56) * mm, "end": v(220, 138.56) * mm, "construction": true});
            skLineSegment(sketch, "E34.10.4.4", {"start": v(210, 121.24) * mm, "end": v(200, 138.56) * mm, "construction": true});
            skLineSegment(sketch, "E34.10.4.5", {"start": v(210, 155.88) * mm, "end": v(200, 138.56) * mm, "construction": true});
            skLineSegment(sketch, "E34.10.4.6", {"start": v(220, 138.56) * mm, "end": v(210, 155.88) * mm, "construction": true});
            skLineSegment(sketch, "E34.10.4.7", {"start": v(210, 155.88) * mm, "end": v(230, 155.88) * mm, "construction": true});
            skLineSegment(sketch, "E34.10.4.8", {"start": v(230, 155.88) * mm, "end": v(220, 138.56) * mm, "construction": true});
            skLineSegment(sketch, "E34.10.5.0", {"start": v(210, 155.88) * mm, "end": v(230, 155.88) * mm, "construction": true});
            skLineSegment(sketch, "E34.10.5.1", {"start": v(220, 173.2) * mm, "end": v(210, 155.88) * mm, "construction": true});
            skLineSegment(sketch, "E34.10.5.2", {"start": v(230, 155.88) * mm, "end": v(220, 173.2) * mm, "construction": true});
            skLineSegment(sketch, "E34.10.5.3", {"start": v(200, 173.2) * mm, "end": v(220, 173.2) * mm, "construction": true});
            skLineSegment(sketch, "E34.10.5.4", {"start": v(210, 155.88) * mm, "end": v(200, 173.2) * mm, "construction": true});
            skLineSegment(sketch, "E34.10.5.5", {"start": v(210, 190.53) * mm, "end": v(200, 173.2) * mm, "construction": true});
            skLineSegment(sketch, "E34.10.5.6", {"start": v(220, 173.2) * mm, "end": v(210, 190.53) * mm, "construction": true});
            skLineSegment(sketch, "E34.10.5.7", {"start": v(210, 190.53) * mm, "end": v(230, 190.53) * mm, "construction": true});
            skLineSegment(sketch, "E34.10.5.8", {"start": v(230, 190.53) * mm, "end": v(220, 173.2) * mm, "construction": true});
            skLineSegment(sketch, "E34.10.6.0", {"start": v(210, 190.53) * mm, "end": v(230, 190.53) * mm, "construction": true});
            skLineSegment(sketch, "E34.10.6.1", {"start": v(220, 207.85) * mm, "end": v(210, 190.53) * mm, "construction": true});
            skLineSegment(sketch, "E34.10.6.2", {"start": v(230, 190.53) * mm, "end": v(220, 207.85) * mm, "construction": true});
            skLineSegment(sketch, "E34.10.6.3", {"start": v(200, 207.85) * mm, "end": v(220, 207.85) * mm, "construction": true});
            skLineSegment(sketch, "E34.10.6.4", {"start": v(210, 190.53) * mm, "end": v(200, 207.85) * mm, "construction": true});
            skLineSegment(sketch, "E34.10.6.5", {"start": v(210, 225.17) * mm, "end": v(200, 207.85) * mm, "construction": true});
            skLineSegment(sketch, "E34.10.6.6", {"start": v(220, 207.85) * mm, "end": v(210, 225.17) * mm, "construction": true});
            skLineSegment(sketch, "E34.10.6.7", {"start": v(210, 225.17) * mm, "end": v(230, 225.17) * mm, "construction": true});
            skLineSegment(sketch, "E34.10.6.8", {"start": v(230, 225.17) * mm, "end": v(220, 207.85) * mm, "construction": true});
            skLineSegment(sketch, "E34.11.0.0", {"start": v(230, -17.32) * mm, "end": v(250, -17.32) * mm, "construction": true});
            skLineSegment(sketch, "E34.11.0.1", {"start": v(240, 0) * mm, "end": v(230, -17.32) * mm, "construction": true});
            skLineSegment(sketch, "E34.11.0.2", {"start": v(250, -17.32) * mm, "end": v(240, 0) * mm, "construction": true});
            skLineSegment(sketch, "E34.11.0.3", {"start": v(220, 0) * mm, "end": v(240, 0) * mm, "construction": true});
            skLineSegment(sketch, "E34.11.0.4", {"start": v(230, -17.32) * mm, "end": v(220, 0) * mm, "construction": true});
            skLineSegment(sketch, "E34.11.0.5", {"start": v(230, 17.32) * mm, "end": v(220, 0) * mm, "construction": true});
            skLineSegment(sketch, "E34.11.0.6", {"start": v(240, 0) * mm, "end": v(230, 17.32) * mm, "construction": true});
            skLineSegment(sketch, "E34.11.0.7", {"start": v(230, 17.32) * mm, "end": v(250, 17.32) * mm, "construction": true});
            skLineSegment(sketch, "E34.11.0.8", {"start": v(250, 17.32) * mm, "end": v(240, 0) * mm, "construction": true});
            skLineSegment(sketch, "E34.11.1.0", {"start": v(230, 17.32) * mm, "end": v(250, 17.32) * mm, "construction": true});
            skLineSegment(sketch, "E34.11.1.1", {"start": v(240, 34.64) * mm, "end": v(230, 17.32) * mm, "construction": true});
            skLineSegment(sketch, "E34.11.1.2", {"start": v(250, 17.32) * mm, "end": v(240, 34.64) * mm, "construction": true});
            skLineSegment(sketch, "E34.11.1.3", {"start": v(220, 34.64) * mm, "end": v(240, 34.64) * mm, "construction": true});
            skLineSegment(sketch, "E34.11.1.4", {"start": v(230, 17.32) * mm, "end": v(220, 34.64) * mm, "construction": true});
            skLineSegment(sketch, "E34.11.1.5", {"start": v(230, 51.96) * mm, "end": v(220, 34.64) * mm, "construction": true});
            skLineSegment(sketch, "E34.11.1.6", {"start": v(240, 34.64) * mm, "end": v(230, 51.96) * mm, "construction": true});
            skLineSegment(sketch, "E34.11.1.7", {"start": v(230, 51.96) * mm, "end": v(250, 51.96) * mm, "construction": true});
            skLineSegment(sketch, "E34.11.1.8", {"start": v(250, 51.96) * mm, "end": v(240, 34.64) * mm, "construction": true});
            skLineSegment(sketch, "E34.11.2.0", {"start": v(230, 51.96) * mm, "end": v(250, 51.96) * mm, "construction": true});
            skLineSegment(sketch, "E34.11.2.1", {"start": v(240, 69.28) * mm, "end": v(230, 51.96) * mm, "construction": true});
            skLineSegment(sketch, "E34.11.2.2", {"start": v(250, 51.96) * mm, "end": v(240, 69.28) * mm, "construction": true});
            skLineSegment(sketch, "E34.11.2.3", {"start": v(220, 69.28) * mm, "end": v(240, 69.28) * mm, "construction": true});
            skLineSegment(sketch, "E34.11.2.4", {"start": v(230, 51.96) * mm, "end": v(220, 69.28) * mm, "construction": true});
            skLineSegment(sketch, "E34.11.2.5", {"start": v(230, 86.6) * mm, "end": v(220, 69.28) * mm, "construction": true});
            skLineSegment(sketch, "E34.11.2.6", {"start": v(240, 69.28) * mm, "end": v(230, 86.6) * mm, "construction": true});
            skLineSegment(sketch, "E34.11.2.7", {"start": v(230, 86.6) * mm, "end": v(250, 86.6) * mm, "construction": true});
            skLineSegment(sketch, "E34.11.2.8", {"start": v(250, 86.6) * mm, "end": v(240, 69.28) * mm, "construction": true});
            skLineSegment(sketch, "E34.11.3.0", {"start": v(230, 86.6) * mm, "end": v(250, 86.6) * mm, "construction": true});
            skLineSegment(sketch, "E34.11.3.1", {"start": v(240, 103.92) * mm, "end": v(230, 86.6) * mm, "construction": true});
            skLineSegment(sketch, "E34.11.3.2", {"start": v(250, 86.6) * mm, "end": v(240, 103.92) * mm, "construction": true});
            skLineSegment(sketch, "E34.11.3.3", {"start": v(220, 103.92) * mm, "end": v(240, 103.92) * mm, "construction": true});
            skLineSegment(sketch, "E34.11.3.4", {"start": v(230, 86.6) * mm, "end": v(220, 103.92) * mm, "construction": true});
            skLineSegment(sketch, "E34.11.3.5", {"start": v(230, 121.24) * mm, "end": v(220, 103.92) * mm, "construction": true});
            skLineSegment(sketch, "E34.11.3.6", {"start": v(240, 103.92) * mm, "end": v(230, 121.24) * mm, "construction": true});
            skLineSegment(sketch, "E34.11.3.7", {"start": v(230, 121.24) * mm, "end": v(250, 121.24) * mm, "construction": true});
            skLineSegment(sketch, "E34.11.3.8", {"start": v(250, 121.24) * mm, "end": v(240, 103.92) * mm, "construction": true});
            skLineSegment(sketch, "E34.11.4.0", {"start": v(230, 121.24) * mm, "end": v(250, 121.24) * mm, "construction": true});
            skLineSegment(sketch, "E34.11.4.1", {"start": v(240, 138.56) * mm, "end": v(230, 121.24) * mm, "construction": true});
            skLineSegment(sketch, "E34.11.4.2", {"start": v(250, 121.24) * mm, "end": v(240, 138.56) * mm, "construction": true});
            skLineSegment(sketch, "E34.11.4.3", {"start": v(220, 138.56) * mm, "end": v(240, 138.56) * mm, "construction": true});
            skLineSegment(sketch, "E34.11.4.4", {"start": v(230, 121.24) * mm, "end": v(220, 138.56) * mm, "construction": true});
            skLineSegment(sketch, "E34.11.4.5", {"start": v(230, 155.88) * mm, "end": v(220, 138.56) * mm, "construction": true});
            skLineSegment(sketch, "E34.11.4.6", {"start": v(240, 138.56) * mm, "end": v(230, 155.88) * mm, "construction": true});
            skLineSegment(sketch, "E34.11.4.7", {"start": v(230, 155.88) * mm, "end": v(250, 155.88) * mm, "construction": true});
            skLineSegment(sketch, "E34.11.4.8", {"start": v(250, 155.88) * mm, "end": v(240, 138.56) * mm, "construction": true});
            skLineSegment(sketch, "E34.11.5.0", {"start": v(230, 155.88) * mm, "end": v(250, 155.88) * mm, "construction": true});
            skLineSegment(sketch, "E34.11.5.1", {"start": v(240, 173.2) * mm, "end": v(230, 155.88) * mm, "construction": true});
            skLineSegment(sketch, "E34.11.5.2", {"start": v(250, 155.88) * mm, "end": v(240, 173.2) * mm, "construction": true});
            skLineSegment(sketch, "E34.11.5.3", {"start": v(220, 173.2) * mm, "end": v(240, 173.2) * mm, "construction": true});
            skLineSegment(sketch, "E34.11.5.4", {"start": v(230, 155.88) * mm, "end": v(220, 173.2) * mm, "construction": true});
            skLineSegment(sketch, "E34.11.5.5", {"start": v(230, 190.53) * mm, "end": v(220, 173.2) * mm, "construction": true});
            skLineSegment(sketch, "E34.11.5.6", {"start": v(240, 173.2) * mm, "end": v(230, 190.53) * mm, "construction": true});
            skLineSegment(sketch, "E34.11.5.7", {"start": v(230, 190.53) * mm, "end": v(250, 190.53) * mm, "construction": true});
            skLineSegment(sketch, "E34.11.5.8", {"start": v(250, 190.53) * mm, "end": v(240, 173.2) * mm, "construction": true});
            skLineSegment(sketch, "E34.11.6.0", {"start": v(230, 190.53) * mm, "end": v(250, 190.53) * mm, "construction": true});
            skLineSegment(sketch, "E34.11.6.1", {"start": v(240, 207.85) * mm, "end": v(230, 190.53) * mm, "construction": true});
            skLineSegment(sketch, "E34.11.6.2", {"start": v(250, 190.53) * mm, "end": v(240, 207.85) * mm, "construction": true});
            skLineSegment(sketch, "E34.11.6.3", {"start": v(220, 207.85) * mm, "end": v(240, 207.85) * mm, "construction": true});
            skLineSegment(sketch, "E34.11.6.4", {"start": v(230, 190.53) * mm, "end": v(220, 207.85) * mm, "construction": true});
            skLineSegment(sketch, "E34.11.6.5", {"start": v(230, 225.17) * mm, "end": v(220, 207.85) * mm, "construction": true});
            skLineSegment(sketch, "E34.11.6.6", {"start": v(240, 207.85) * mm, "end": v(230, 225.17) * mm, "construction": true});
            skLineSegment(sketch, "E34.11.6.7", {"start": v(230, 225.17) * mm, "end": v(250, 225.17) * mm, "construction": true});
            skLineSegment(sketch, "E34.11.6.8", {"start": v(250, 225.17) * mm, "end": v(240, 207.85) * mm, "construction": true});
            skLineSegment(sketch, "E34.12.0.0", {"start": v(250, -17.32) * mm, "end": v(270, -17.32) * mm, "construction": true});
            skLineSegment(sketch, "E34.12.0.1", {"start": v(260, 0) * mm, "end": v(250, -17.32) * mm, "construction": true});
            skLineSegment(sketch, "E34.12.0.2", {"start": v(270, -17.32) * mm, "end": v(260, 0) * mm, "construction": true});
            skLineSegment(sketch, "E34.12.0.3", {"start": v(240, 0) * mm, "end": v(260, 0) * mm, "construction": true});
            skLineSegment(sketch, "E34.12.0.4", {"start": v(250, -17.32) * mm, "end": v(240, 0) * mm, "construction": true});
            skLineSegment(sketch, "E34.12.0.5", {"start": v(250, 17.32) * mm, "end": v(240, 0) * mm, "construction": true});
            skLineSegment(sketch, "E34.12.0.6", {"start": v(260, 0) * mm, "end": v(250, 17.32) * mm, "construction": true});
            skLineSegment(sketch, "E34.12.0.7", {"start": v(250, 17.32) * mm, "end": v(270, 17.32) * mm, "construction": true});
            skLineSegment(sketch, "E34.12.0.8", {"start": v(270, 17.32) * mm, "end": v(260, 0) * mm, "construction": true});
            skLineSegment(sketch, "E34.12.1.0", {"start": v(250, 17.32) * mm, "end": v(270, 17.32) * mm, "construction": true});
            skLineSegment(sketch, "E34.12.1.1", {"start": v(260, 34.64) * mm, "end": v(250, 17.32) * mm, "construction": true});
            skLineSegment(sketch, "E34.12.1.2", {"start": v(270, 17.32) * mm, "end": v(260, 34.64) * mm, "construction": true});
            skLineSegment(sketch, "E34.12.1.3", {"start": v(240, 34.64) * mm, "end": v(260, 34.64) * mm, "construction": true});
            skLineSegment(sketch, "E34.12.1.4", {"start": v(250, 17.32) * mm, "end": v(240, 34.64) * mm, "construction": true});
            skLineSegment(sketch, "E34.12.1.5", {"start": v(250, 51.96) * mm, "end": v(240, 34.64) * mm, "construction": true});
            skLineSegment(sketch, "E34.12.1.6", {"start": v(260, 34.64) * mm, "end": v(250, 51.96) * mm, "construction": true});
            skLineSegment(sketch, "E34.12.1.7", {"start": v(250, 51.96) * mm, "end": v(270, 51.96) * mm, "construction": true});
            skLineSegment(sketch, "E34.12.1.8", {"start": v(270, 51.96) * mm, "end": v(260, 34.64) * mm, "construction": true});
            skLineSegment(sketch, "E34.12.2.0", {"start": v(250, 51.96) * mm, "end": v(270, 51.96) * mm, "construction": true});
            skLineSegment(sketch, "E34.12.2.1", {"start": v(260, 69.28) * mm, "end": v(250, 51.96) * mm, "construction": true});
            skLineSegment(sketch, "E34.12.2.2", {"start": v(270, 51.96) * mm, "end": v(260, 69.28) * mm, "construction": true});
            skLineSegment(sketch, "E34.12.2.3", {"start": v(240, 69.28) * mm, "end": v(260, 69.28) * mm, "construction": true});
            skLineSegment(sketch, "E34.12.2.4", {"start": v(250, 51.96) * mm, "end": v(240, 69.28) * mm, "construction": true});
            skLineSegment(sketch, "E34.12.2.5", {"start": v(250, 86.6) * mm, "end": v(240, 69.28) * mm, "construction": true});
            skLineSegment(sketch, "E34.12.2.6", {"start": v(260, 69.28) * mm, "end": v(250, 86.6) * mm, "construction": true});
            skLineSegment(sketch, "E34.12.2.7", {"start": v(250, 86.6) * mm, "end": v(270, 86.6) * mm, "construction": true});
            skLineSegment(sketch, "E34.12.2.8", {"start": v(270, 86.6) * mm, "end": v(260, 69.28) * mm, "construction": true});
            skLineSegment(sketch, "E34.12.3.0", {"start": v(250, 86.6) * mm, "end": v(270, 86.6) * mm, "construction": true});
            skLineSegment(sketch, "E34.12.3.1", {"start": v(260, 103.92) * mm, "end": v(250, 86.6) * mm, "construction": true});
            skLineSegment(sketch, "E34.12.3.2", {"start": v(270, 86.6) * mm, "end": v(260, 103.92) * mm, "construction": true});
            skLineSegment(sketch, "E34.12.3.3", {"start": v(240, 103.92) * mm, "end": v(260, 103.92) * mm, "construction": true});
            skLineSegment(sketch, "E34.12.3.4", {"start": v(250, 86.6) * mm, "end": v(240, 103.92) * mm, "construction": true});
            skLineSegment(sketch, "E34.12.3.5", {"start": v(250, 121.24) * mm, "end": v(240, 103.92) * mm, "construction": true});
            skLineSegment(sketch, "E34.12.3.6", {"start": v(260, 103.92) * mm, "end": v(250, 121.24) * mm, "construction": true});
            skLineSegment(sketch, "E34.12.3.7", {"start": v(250, 121.24) * mm, "end": v(270, 121.24) * mm, "construction": true});
            skLineSegment(sketch, "E34.12.3.8", {"start": v(270, 121.24) * mm, "end": v(260, 103.92) * mm, "construction": true});
            skLineSegment(sketch, "E34.12.4.0", {"start": v(250, 121.24) * mm, "end": v(270, 121.24) * mm, "construction": true});
            skLineSegment(sketch, "E34.12.4.1", {"start": v(260, 138.56) * mm, "end": v(250, 121.24) * mm, "construction": true});
            skLineSegment(sketch, "E34.12.4.2", {"start": v(270, 121.24) * mm, "end": v(260, 138.56) * mm, "construction": true});
            skLineSegment(sketch, "E34.12.4.3", {"start": v(240, 138.56) * mm, "end": v(260, 138.56) * mm, "construction": true});
            skLineSegment(sketch, "E34.12.4.4", {"start": v(250, 121.24) * mm, "end": v(240, 138.56) * mm, "construction": true});
            skLineSegment(sketch, "E34.12.4.5", {"start": v(250, 155.88) * mm, "end": v(240, 138.56) * mm, "construction": true});
            skLineSegment(sketch, "E34.12.4.6", {"start": v(260, 138.56) * mm, "end": v(250, 155.88) * mm, "construction": true});
            skLineSegment(sketch, "E34.12.4.7", {"start": v(250, 155.88) * mm, "end": v(270, 155.88) * mm, "construction": true});
            skLineSegment(sketch, "E34.12.4.8", {"start": v(270, 155.88) * mm, "end": v(260, 138.56) * mm, "construction": true});
            skLineSegment(sketch, "E34.12.5.0", {"start": v(250, 155.88) * mm, "end": v(270, 155.88) * mm, "construction": true});
            skLineSegment(sketch, "E34.12.5.1", {"start": v(260, 173.2) * mm, "end": v(250, 155.88) * mm, "construction": true});
            skLineSegment(sketch, "E34.12.5.2", {"start": v(270, 155.88) * mm, "end": v(260, 173.2) * mm, "construction": true});
            skLineSegment(sketch, "E34.12.5.3", {"start": v(240, 173.2) * mm, "end": v(260, 173.2) * mm, "construction": true});
            skLineSegment(sketch, "E34.12.5.4", {"start": v(250, 155.88) * mm, "end": v(240, 173.2) * mm, "construction": true});
            skLineSegment(sketch, "E34.12.5.5", {"start": v(250, 190.53) * mm, "end": v(240, 173.2) * mm, "construction": true});
            skLineSegment(sketch, "E34.12.5.6", {"start": v(260, 173.2) * mm, "end": v(250, 190.53) * mm, "construction": true});
            skLineSegment(sketch, "E34.12.5.7", {"start": v(250, 190.53) * mm, "end": v(270, 190.53) * mm, "construction": true});
            skLineSegment(sketch, "E34.12.5.8", {"start": v(270, 190.53) * mm, "end": v(260, 173.2) * mm, "construction": true});
            skLineSegment(sketch, "E34.12.6.0", {"start": v(250, 190.53) * mm, "end": v(270, 190.53) * mm, "construction": true});
            skLineSegment(sketch, "E34.12.6.1", {"start": v(260, 207.85) * mm, "end": v(250, 190.53) * mm, "construction": true});
            skLineSegment(sketch, "E34.12.6.2", {"start": v(270, 190.53) * mm, "end": v(260, 207.85) * mm, "construction": true});
            skLineSegment(sketch, "E34.12.6.3", {"start": v(240, 207.85) * mm, "end": v(260, 207.85) * mm, "construction": true});
            skLineSegment(sketch, "E34.12.6.4", {"start": v(250, 190.53) * mm, "end": v(240, 207.85) * mm, "construction": true});
            skLineSegment(sketch, "E34.12.6.5", {"start": v(250, 225.17) * mm, "end": v(240, 207.85) * mm, "construction": true});
            skLineSegment(sketch, "E34.12.6.6", {"start": v(260, 207.85) * mm, "end": v(250, 225.17) * mm, "construction": true});
            skLineSegment(sketch, "E34.12.6.7", {"start": v(250, 225.17) * mm, "end": v(270, 225.17) * mm, "construction": true});
            skLineSegment(sketch, "E34.12.6.8", {"start": v(270, 225.17) * mm, "end": v(260, 207.85) * mm, "construction": true});
            skLineSegment(sketch, "E34.13.0.0", {"start": v(270, -17.32) * mm, "end": v(290, -17.32) * mm, "construction": true});
            skLineSegment(sketch, "E34.13.0.1", {"start": v(280, 0) * mm, "end": v(270, -17.32) * mm, "construction": true});
            skLineSegment(sketch, "E34.13.0.2", {"start": v(290, -17.32) * mm, "end": v(280, 0) * mm, "construction": true});
            skLineSegment(sketch, "E34.13.0.3", {"start": v(260, 0) * mm, "end": v(280, 0) * mm, "construction": true});
            skLineSegment(sketch, "E34.13.0.4", {"start": v(270, -17.32) * mm, "end": v(260, 0) * mm, "construction": true});
            skLineSegment(sketch, "E34.13.0.5", {"start": v(270, 17.32) * mm, "end": v(260, 0) * mm, "construction": true});
            skLineSegment(sketch, "E34.13.0.6", {"start": v(280, 0) * mm, "end": v(270, 17.32) * mm, "construction": true});
            skLineSegment(sketch, "E34.13.0.7", {"start": v(270, 17.32) * mm, "end": v(290, 17.32) * mm, "construction": true});
            skLineSegment(sketch, "E34.13.0.8", {"start": v(290, 17.32) * mm, "end": v(280, 0) * mm, "construction": true});
            skLineSegment(sketch, "E34.13.1.0", {"start": v(270, 17.32) * mm, "end": v(290, 17.32) * mm, "construction": true});
            skLineSegment(sketch, "E34.13.1.1", {"start": v(280, 34.64) * mm, "end": v(270, 17.32) * mm, "construction": true});
            skLineSegment(sketch, "E34.13.1.2", {"start": v(290, 17.32) * mm, "end": v(280, 34.64) * mm, "construction": true});
            skLineSegment(sketch, "E34.13.1.3", {"start": v(260, 34.64) * mm, "end": v(280, 34.64) * mm, "construction": true});
            skLineSegment(sketch, "E34.13.1.4", {"start": v(270, 17.32) * mm, "end": v(260, 34.64) * mm, "construction": true});
            skLineSegment(sketch, "E34.13.1.5", {"start": v(270, 51.96) * mm, "end": v(260, 34.64) * mm, "construction": true});
            skLineSegment(sketch, "E34.13.1.6", {"start": v(280, 34.64) * mm, "end": v(270, 51.96) * mm, "construction": true});
            skLineSegment(sketch, "E34.13.1.7", {"start": v(270, 51.96) * mm, "end": v(290, 51.96) * mm, "construction": true});
            skLineSegment(sketch, "E34.13.1.8", {"start": v(290, 51.96) * mm, "end": v(280, 34.64) * mm, "construction": true});
            skLineSegment(sketch, "E34.13.2.0", {"start": v(270, 51.96) * mm, "end": v(290, 51.96) * mm, "construction": true});
            skLineSegment(sketch, "E34.13.2.1", {"start": v(280, 69.28) * mm, "end": v(270, 51.96) * mm, "construction": true});
            skLineSegment(sketch, "E34.13.2.2", {"start": v(290, 51.96) * mm, "end": v(280, 69.28) * mm, "construction": true});
            skLineSegment(sketch, "E34.13.2.3", {"start": v(260, 69.28) * mm, "end": v(280, 69.28) * mm, "construction": true});
            skLineSegment(sketch, "E34.13.2.4", {"start": v(270, 51.96) * mm, "end": v(260, 69.28) * mm, "construction": true});
            skLineSegment(sketch, "E34.13.2.5", {"start": v(270, 86.6) * mm, "end": v(260, 69.28) * mm, "construction": true});
            skLineSegment(sketch, "E34.13.2.6", {"start": v(280, 69.28) * mm, "end": v(270, 86.6) * mm, "construction": true});
            skLineSegment(sketch, "E34.13.2.7", {"start": v(270, 86.6) * mm, "end": v(290, 86.6) * mm, "construction": true});
            skLineSegment(sketch, "E34.13.2.8", {"start": v(290, 86.6) * mm, "end": v(280, 69.28) * mm, "construction": true});
            skLineSegment(sketch, "E34.13.3.0", {"start": v(270, 86.6) * mm, "end": v(290, 86.6) * mm, "construction": true});
            skLineSegment(sketch, "E34.13.3.1", {"start": v(280, 103.92) * mm, "end": v(270, 86.6) * mm, "construction": true});
            skLineSegment(sketch, "E34.13.3.2", {"start": v(290, 86.6) * mm, "end": v(280, 103.92) * mm, "construction": true});
            skLineSegment(sketch, "E34.13.3.3", {"start": v(260, 103.92) * mm, "end": v(280, 103.92) * mm, "construction": true});
            skLineSegment(sketch, "E34.13.3.4", {"start": v(270, 86.6) * mm, "end": v(260, 103.92) * mm, "construction": true});
            skLineSegment(sketch, "E34.13.3.5", {"start": v(270, 121.24) * mm, "end": v(260, 103.92) * mm, "construction": true});
            skLineSegment(sketch, "E34.13.3.6", {"start": v(280, 103.92) * mm, "end": v(270, 121.24) * mm, "construction": true});
            skLineSegment(sketch, "E34.13.3.7", {"start": v(270, 121.24) * mm, "end": v(290, 121.24) * mm, "construction": true});
            skLineSegment(sketch, "E34.13.3.8", {"start": v(290, 121.24) * mm, "end": v(280, 103.92) * mm, "construction": true});
            skLineSegment(sketch, "E34.13.4.0", {"start": v(270, 121.24) * mm, "end": v(290, 121.24) * mm, "construction": true});
            skLineSegment(sketch, "E34.13.4.1", {"start": v(280, 138.56) * mm, "end": v(270, 121.24) * mm, "construction": true});
            skLineSegment(sketch, "E34.13.4.2", {"start": v(290, 121.24) * mm, "end": v(280, 138.56) * mm, "construction": true});
            skLineSegment(sketch, "E34.13.4.3", {"start": v(260, 138.56) * mm, "end": v(280, 138.56) * mm, "construction": true});
            skLineSegment(sketch, "E34.13.4.4", {"start": v(270, 121.24) * mm, "end": v(260, 138.56) * mm, "construction": true});
            skLineSegment(sketch, "E34.13.4.5", {"start": v(270, 155.88) * mm, "end": v(260, 138.56) * mm, "construction": true});
            skLineSegment(sketch, "E34.13.4.6", {"start": v(280, 138.56) * mm, "end": v(270, 155.88) * mm, "construction": true});
            skLineSegment(sketch, "E34.13.4.7", {"start": v(270, 155.88) * mm, "end": v(290, 155.88) * mm, "construction": true});
            skLineSegment(sketch, "E34.13.4.8", {"start": v(290, 155.88) * mm, "end": v(280, 138.56) * mm, "construction": true});
            skLineSegment(sketch, "E34.13.5.0", {"start": v(270, 155.88) * mm, "end": v(290, 155.88) * mm, "construction": true});
            skLineSegment(sketch, "E34.13.5.1", {"start": v(280, 173.2) * mm, "end": v(270, 155.88) * mm, "construction": true});
            skLineSegment(sketch, "E34.13.5.2", {"start": v(290, 155.88) * mm, "end": v(280, 173.2) * mm, "construction": true});
            skLineSegment(sketch, "E34.13.5.3", {"start": v(260, 173.2) * mm, "end": v(280, 173.2) * mm, "construction": true});
            skLineSegment(sketch, "E34.13.5.4", {"start": v(270, 155.88) * mm, "end": v(260, 173.2) * mm, "construction": true});
            skLineSegment(sketch, "E34.13.5.5", {"start": v(270, 190.53) * mm, "end": v(260, 173.2) * mm, "construction": true});
            skLineSegment(sketch, "E34.13.5.6", {"start": v(280, 173.2) * mm, "end": v(270, 190.53) * mm, "construction": true});
            skLineSegment(sketch, "E34.13.5.7", {"start": v(270, 190.53) * mm, "end": v(290, 190.53) * mm, "construction": true});
            skLineSegment(sketch, "E34.13.5.8", {"start": v(290, 190.53) * mm, "end": v(280, 173.2) * mm, "construction": true});
            skLineSegment(sketch, "E34.13.6.0", {"start": v(270, 190.53) * mm, "end": v(290, 190.53) * mm, "construction": true});
            skLineSegment(sketch, "E34.13.6.1", {"start": v(280, 207.85) * mm, "end": v(270, 190.53) * mm, "construction": true});
            skLineSegment(sketch, "E34.13.6.2", {"start": v(290, 190.53) * mm, "end": v(280, 207.85) * mm, "construction": true});
            skLineSegment(sketch, "E34.13.6.3", {"start": v(260, 207.85) * mm, "end": v(280, 207.85) * mm, "construction": true});
            skLineSegment(sketch, "E34.13.6.4", {"start": v(270, 190.53) * mm, "end": v(260, 207.85) * mm, "construction": true});
            skLineSegment(sketch, "E34.13.6.5", {"start": v(270, 225.17) * mm, "end": v(260, 207.85) * mm, "construction": true});
            skLineSegment(sketch, "E34.13.6.6", {"start": v(280, 207.85) * mm, "end": v(270, 225.17) * mm, "construction": true});
            skLineSegment(sketch, "E34.13.6.7", {"start": v(270, 225.17) * mm, "end": v(290, 225.17) * mm, "construction": true});
            skLineSegment(sketch, "E34.13.6.8", {"start": v(290, 225.17) * mm, "end": v(280, 207.85) * mm, "construction": true});
            skLineSegment(sketch, "E34.direction2", {"start": v(10, -17.32) * mm, "end": v(10, 17.32) * mm, "construction": true});
            skLineSegment(sketch, "E35.bottom", {"start": v(-70, -44.58) * mm, "end": v(350, -44.58) * mm});
            skLineSegment(sketch, "E35.top", {"start": v(-70, 252.42) * mm, "end": v(350, 252.42) * mm});
            skLineSegment(sketch, "E35.left", {"start": v(-70, -44.58) * mm, "end": v(-70, 252.42) * mm});
            skLineSegment(sketch, "E35.right", {"start": v(350, -44.58) * mm, "end": v(350, 252.42) * mm});
            skPoint(sketch, "E35.middle", {"position": v(140, 103.92) * mm});
            skPoint(sketch, "E36.middle", {"position": v(-149.88, -103.44) * mm});
            skCircle(sketch, "E37", {"center": v(270, 86.6) * mm, "radius": 1.5 * mm});
            skCircle(sketch, "E38", {"center": v(250, 51.96) * mm, "radius": 1.5 * mm});
            skCircle(sketch, "E39", {"center": v(230, 17.32) * mm, "radius": 1.5 * mm});
            skCircle(sketch, "E40", {"center": v(180, 0) * mm, "radius": 1.5 * mm});
            skCircle(sketch, "E41", {"center": v(100, 0) * mm, "radius": 1.5 * mm});
            skCircle(sketch, "E42", {"center": v(50, 17.32) * mm, "radius": 1.5 * mm});
            skCircle(sketch, "E43", {"center": v(80, 34.64) * mm, "radius": 1.5 * mm});
            skCircle(sketch, "E44", {"center": v(40, 69.28) * mm, "radius": 1.5 * mm});
            skCircle(sketch, "E45", {"center": v(20, 103.92) * mm, "radius": 1.5 * mm});
            skCircle(sketch, "E46", {"center": v(20, 138.56) * mm, "radius": 1.5 * mm});
            skCircle(sketch, "E47", {"center": v(20, 173.2) * mm, "radius": 1.5 * mm});
            skCircle(sketch, "E48", {"center": v(30, 190.53) * mm, "radius": 1.5 * mm});
            skCircle(sketch, "E49", {"center": v(70, 190.53) * mm, "radius": 1.5 * mm});
            skCircle(sketch, "E50", {"center": v(90, 155.88) * mm, "radius": 1.5 * mm});
            skCircle(sketch, "E51", {"center": v(60, 138.56) * mm, "radius": 1.5 * mm});
            skCircle(sketch, "E52", {"center": v(60, 103.92) * mm, "radius": 1.5 * mm});
            skCircle(sketch, "E53", {"center": v(80, 69.28) * mm, "radius": 1.5 * mm});
            skCircle(sketch, "E54", {"center": v(130, 17.32) * mm, "radius": 1.5 * mm});
            skCircle(sketch, "E55", {"center": v(160, 34.64) * mm, "radius": 1.5 * mm});
            skCircle(sketch, "E56", {"center": v(130, 51.96) * mm, "radius": 1.5 * mm});
            skCircle(sketch, "E57", {"center": v(130, 86.6) * mm, "radius": 1.5 * mm});
            skCircle(sketch, "E58", {"center": v(130, 121.24) * mm, "radius": 1.5 * mm});
            skCircle(sketch, "E59", {"center": v(130, 155.88) * mm, "radius": 1.5 * mm});
            skCircle(sketch, "E60", {"center": v(110, 190.53) * mm, "radius": 1.5 * mm});
            skCircle(sketch, "E61", {"center": v(90, 121.24) * mm, "radius": 1.5 * mm});
            skCircle(sketch, "E62", {"center": v(200, 34.64) * mm, "radius": 1.5 * mm});
            skCircle(sketch, "E63", {"center": v(200, 69.28) * mm, "radius": 1.5 * mm});
            skCircle(sketch, "E64", {"center": v(220, 103.92) * mm, "radius": 1.5 * mm});
            skCircle(sketch, "E65", {"center": v(170, 86.6) * mm, "radius": 1.5 * mm});
            skCircle(sketch, "E66", {"center": v(170, 121.24) * mm, "radius": 1.5 * mm});
            skCircle(sketch, "E67", {"center": v(200, 138.56) * mm, "radius": 1.5 * mm});
            skCircle(sketch, "E68", {"center": v(250, 121.24) * mm, "radius": 1.5 * mm});
            skCircle(sketch, "E69", {"center": v(230, 155.88) * mm, "radius": 1.5 * mm});
            skCircle(sketch, "E70", {"center": v(200, 173.2) * mm, "radius": 1.5 * mm});
            skCircle(sketch, "E71", {"center": v(160, 173.2) * mm, "radius": 1.5 * mm});
            skSolve(sketch);
        }
        {
            var Q0;
            Q0=makeQuery(id+"F2.imprint","IMPRINT",FACE,{"disambiguationData":[TD([[makeQuery(id+"F2.imprint","IMPRINT",EDGE,{"derivedFrom":sQuery(id+"F2.wireOp",EDGE,"E42")}),1.0]])]});
            var Q1;
            Q1=makeQuery(id+"F2.imprint","IMPRINT",FACE,{"disambiguationData":[TD([[makeQuery(id+"F2.imprint","IMPRINT",EDGE,{"derivedFrom":sQuery(id+"F2.wireOp",EDGE,"E41")}),1.0]])]});
            var Q2;
            Q2=makeQuery(id+"F2.imprint","IMPRINT",FACE,{"disambiguationData":[TD([[makeQuery(id+"F2.imprint","IMPRINT",EDGE,{"derivedFrom":sQuery(id+"F2.wireOp",EDGE,"E54")}),1.0]])]});
            var Q3;
            Q3=makeQuery(id+"F2.imprint","IMPRINT",FACE,{"disambiguationData":[TD([[makeQuery(id+"F2.imprint","IMPRINT",EDGE,{"derivedFrom":sQuery(id+"F2.wireOp",EDGE,"E43")}),1.0]])]});
            var Q4;
            Q4=makeQuery(id+"F2.imprint","IMPRINT",FACE,{"disambiguationData":[TD([[makeQuery(id+"F2.imprint","IMPRINT",EDGE,{"derivedFrom":sQuery(id+"F2.wireOp",EDGE,"E53")}),1.0]])]});
            var Q5;
            Q5=makeQuery(id+"F2.imprint","IMPRINT",FACE,{"disambiguationData":[TD([[makeQuery(id+"F2.imprint","IMPRINT",EDGE,{"derivedFrom":sQuery(id+"F2.wireOp",EDGE,"E44")}),1.0]])]});
            var Q6;
            Q6=makeQuery(id+"F2.imprint","IMPRINT",FACE,{"disambiguationData":[TD([[makeQuery(id+"F2.imprint","IMPRINT",EDGE,{"derivedFrom":sQuery(id+"F2.wireOp",EDGE,"E56")}),1.0]])]});
            var Q7;
            Q7=makeQuery(id+"F2.imprint","IMPRINT",FACE,{"disambiguationData":[TD([[makeQuery(id+"F2.imprint","IMPRINT",EDGE,{"derivedFrom":sQuery(id+"F2.wireOp",EDGE,"E40")}),1.0]])]});
            var Q8;
            Q8=makeQuery(id+"F2.imprint","IMPRINT",FACE,{"disambiguationData":[TD([[makeQuery(id+"F2.imprint","IMPRINT",EDGE,{"derivedFrom":sQuery(id+"F2.wireOp",EDGE,"E62")}),1.0]])]});
            var Q9;
            Q9=makeQuery(id+"F2.imprint","IMPRINT",FACE,{"disambiguationData":[TD([[makeQuery(id+"F2.imprint","IMPRINT",EDGE,{"derivedFrom":sQuery(id+"F2.wireOp",EDGE,"E55")}),1.0]])]});
            var Q10;
            Q10=makeQuery(id+"F2.imprint","IMPRINT",FACE,{"disambiguationData":[TD([[makeQuery(id+"F2.imprint","IMPRINT",EDGE,{"derivedFrom":sQuery(id+"F2.wireOp",EDGE,"E39")}),1.0]])]});
            var Q11;
            Q11=makeQuery(id+"F2.imprint","IMPRINT",FACE,{"disambiguationData":[TD([[makeQuery(id+"F2.imprint","IMPRINT",EDGE,{"derivedFrom":sQuery(id+"F2.wireOp",EDGE,"E38")}),1.0]])]});
            var Q12;
            Q12=makeQuery(id+"F2.imprint","IMPRINT",FACE,{"disambiguationData":[TD([[makeQuery(id+"F2.imprint","IMPRINT",EDGE,{"derivedFrom":sQuery(id+"F2.wireOp",EDGE,"E37")}),1.0]])]});
            var Q13;
            Q13=makeQuery(id+"F2.imprint","IMPRINT",FACE,{"disambiguationData":[TD([[makeQuery(id+"F2.imprint","IMPRINT",EDGE,{"derivedFrom":sQuery(id+"F2.wireOp",EDGE,"E63")}),1.0]])]});
            var Q14;
            Q14=makeQuery(id+"F2.imprint","IMPRINT",FACE,{"disambiguationData":[TD([[makeQuery(id+"F2.imprint","IMPRINT",EDGE,{"derivedFrom":sQuery(id+"F2.wireOp",EDGE,"E65")}),1.0]])]});
            var Q15;
            Q15=makeQuery(id+"F2.imprint","IMPRINT",FACE,{"disambiguationData":[TD([[makeQuery(id+"F2.imprint","IMPRINT",EDGE,{"derivedFrom":sQuery(id+"F2.wireOp",EDGE,"E57")}),1.0]])]});
            var Q16;
            Q16=makeQuery(id+"F2.imprint","IMPRINT",FACE,{"disambiguationData":[TD([[makeQuery(id+"F2.imprint","IMPRINT",EDGE,{"derivedFrom":sQuery(id+"F2.wireOp",EDGE,"E52")}),1.0]])]});
            var Q17;
            Q17=makeQuery(id+"F2.imprint","IMPRINT",FACE,{"disambiguationData":[TD([[makeQuery(id+"F2.imprint","IMPRINT",EDGE,{"derivedFrom":sQuery(id+"F2.wireOp",EDGE,"E45")}),1.0]])]});
            var Q18;
            Q18=makeQuery(id+"F2.imprint","IMPRINT",FACE,{"disambiguationData":[TD([[makeQuery(id+"F2.imprint","IMPRINT",EDGE,{"derivedFrom":sQuery(id+"F2.wireOp",EDGE,"E61")}),1.0]])]});
            var Q19;
            Q19=makeQuery(id+"F2.imprint","IMPRINT",FACE,{"disambiguationData":[TD([[makeQuery(id+"F2.imprint","IMPRINT",EDGE,{"derivedFrom":sQuery(id+"F2.wireOp",EDGE,"E58")}),1.0]])]});
            var Q20;
            Q20=makeQuery(id+"F2.imprint","IMPRINT",FACE,{"disambiguationData":[TD([[makeQuery(id+"F2.imprint","IMPRINT",EDGE,{"derivedFrom":sQuery(id+"F2.wireOp",EDGE,"E66")}),1.0]])]});
            var Q21;
            Q21=makeQuery(id+"F2.imprint","IMPRINT",FACE,{"disambiguationData":[TD([[makeQuery(id+"F2.imprint","IMPRINT",EDGE,{"derivedFrom":sQuery(id+"F2.wireOp",EDGE,"E64")}),1.0]])]});
            var Q22;
            Q22=makeQuery(id+"F2.imprint","IMPRINT",FACE,{"disambiguationData":[TD([[makeQuery(id+"F2.imprint","IMPRINT",EDGE,{"derivedFrom":sQuery(id+"F2.wireOp",EDGE,"E68")}),1.0]])]});
            var Q23;
            Q23=makeQuery(id+"F2.imprint","IMPRINT",FACE,{"disambiguationData":[TD([[makeQuery(id+"F2.imprint","IMPRINT",EDGE,{"derivedFrom":sQuery(id+"F2.wireOp",EDGE,"E69")}),1.0]])]});
            var Q24;
            Q24=makeQuery(id+"F2.imprint","IMPRINT",FACE,{"disambiguationData":[TD([[makeQuery(id+"F2.imprint","IMPRINT",EDGE,{"derivedFrom":sQuery(id+"F2.wireOp",EDGE,"E67")}),1.0]])]});
            var Q25;
            Q25=makeQuery(id+"F2.imprint","IMPRINT",FACE,{"disambiguationData":[TD([[makeQuery(id+"F2.imprint","IMPRINT",EDGE,{"derivedFrom":sQuery(id+"F2.wireOp",EDGE,"E59")}),1.0]])]});
            var Q26;
            Q26=makeQuery(id+"F2.imprint","IMPRINT",FACE,{"disambiguationData":[TD([[makeQuery(id+"F2.imprint","IMPRINT",EDGE,{"derivedFrom":sQuery(id+"F2.wireOp",EDGE,"E50")}),1.0]])]});
            var Q27;
            Q27=makeQuery(id+"F2.imprint","IMPRINT",FACE,{"disambiguationData":[TD([[makeQuery(id+"F2.imprint","IMPRINT",EDGE,{"derivedFrom":sQuery(id+"F2.wireOp",EDGE,"E51")}),1.0]])]});
            var Q28;
            Q28=makeQuery(id+"F2.imprint","IMPRINT",FACE,{"disambiguationData":[TD([[makeQuery(id+"F2.imprint","IMPRINT",EDGE,{"derivedFrom":sQuery(id+"F2.wireOp",EDGE,"E46")}),1.0]])]});
            var Q29;
            Q29=makeQuery(id+"F2.imprint","IMPRINT",FACE,{"disambiguationData":[TD([[makeQuery(id+"F2.imprint","IMPRINT",EDGE,{"derivedFrom":sQuery(id+"F2.wireOp",EDGE,"E48")}),1.0]])]});
            var Q30;
            Q30=makeQuery(id+"F2.imprint","IMPRINT",FACE,{"disambiguationData":[TD([[makeQuery(id+"F2.imprint","IMPRINT",EDGE,{"derivedFrom":sQuery(id+"F2.wireOp",EDGE,"E47")}),1.0]])]});
            var Q31;
            Q31=makeQuery(id+"F2.imprint","IMPRINT",FACE,{"disambiguationData":[TD([[makeQuery(id+"F2.imprint","IMPRINT",EDGE,{"derivedFrom":sQuery(id+"F2.wireOp",EDGE,"E49")}),1.0]])]});
            var Q32;
            Q32=makeQuery(id+"F2.imprint","IMPRINT",FACE,{"disambiguationData":[TD([[makeQuery(id+"F2.imprint","IMPRINT",EDGE,{"derivedFrom":sQuery(id+"F2.wireOp",EDGE,"E60")}),1.0]])]});
            var Q33;
            Q33=makeQuery(id+"F2.imprint","IMPRINT",FACE,{"disambiguationData":[TD([[makeQuery(id+"F2.imprint","IMPRINT",EDGE,{"derivedFrom":sQuery(id+"F2.wireOp",EDGE,"E71")}),1.0]])]});
            var Q34;
            Q34=makeQuery(id+"F2.imprint","IMPRINT",FACE,{"disambiguationData":[TD([[makeQuery(id+"F2.imprint","IMPRINT",EDGE,{"derivedFrom":sQuery(id+"F2.wireOp",EDGE,"E70")}),1.0]])]});
            extrude(context, id + "F3", {"entities" : qUnion([Q0, Q1, Q2, Q3, Q4, Q5, Q6, Q7, Q8, Q9, Q10, Q11, Q12, Q13, Q14, Q15, Q16, Q17, Q18, Q19, Q20, Q21, Q22, Q23, Q24, Q25, Q26, Q27, Q28, Q29, Q30, Q31, Q32, Q33, Q34]), "depth" : 6 * mm, "offsetDistance" : 25 * mm});
        }
    });
